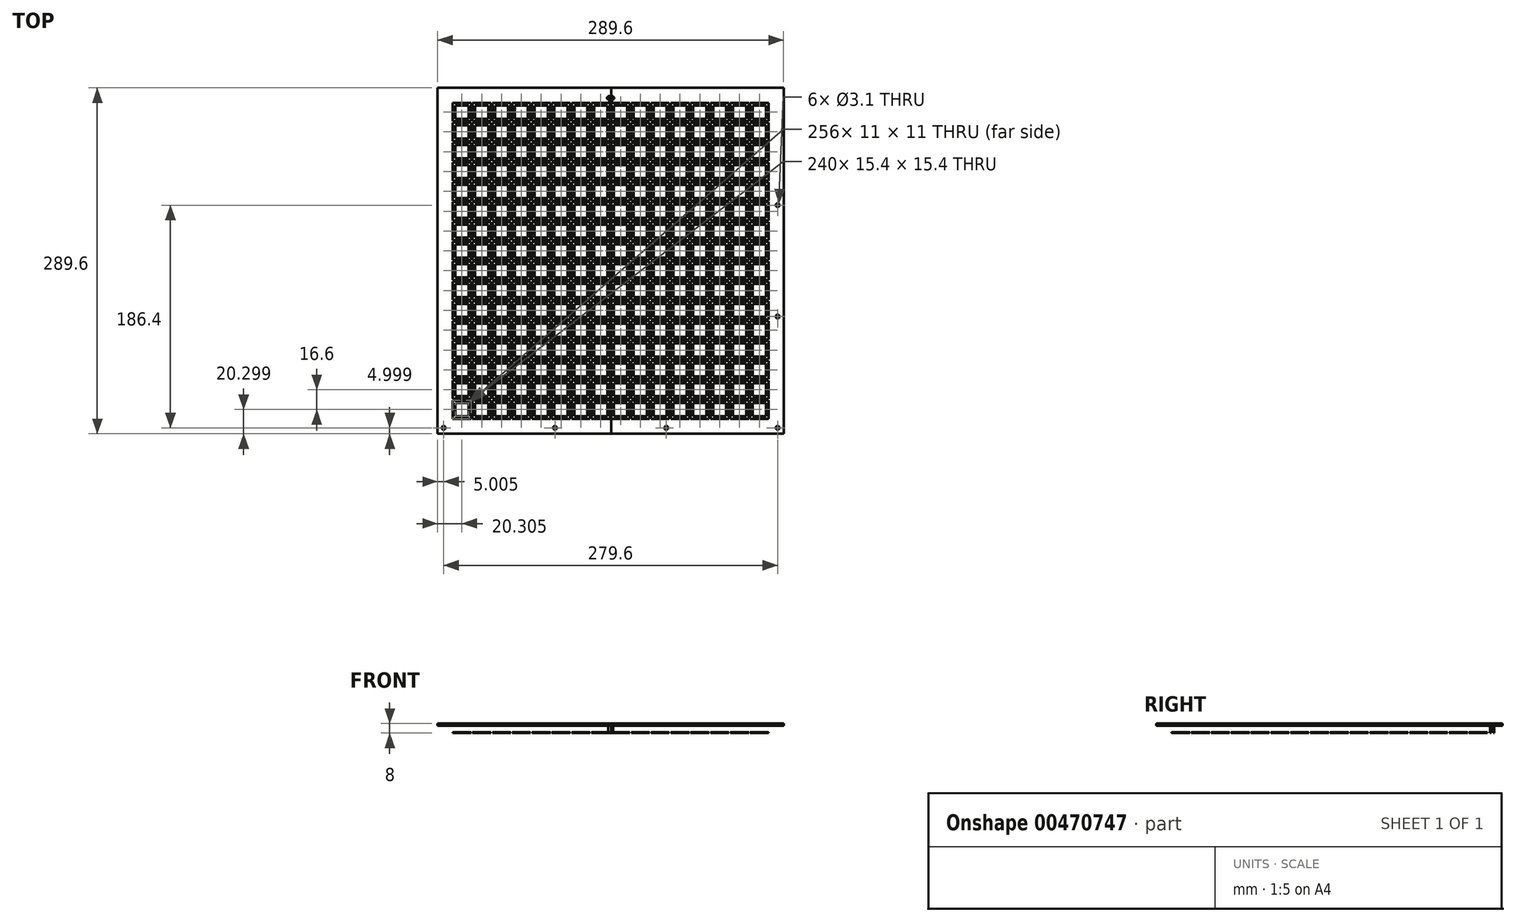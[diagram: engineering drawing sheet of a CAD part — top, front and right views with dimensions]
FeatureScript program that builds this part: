
annotation { "Feature Type Name" : "Feature", "Feature Type Description" : "" }
export const myFeature = defineFeature(function(context is Context, id is Id, definition is map)
    precondition{}
    {
        {
            var Q0;
            Q0=qCreatedBy(makeId("Top.planeOp"),FACE);
            var sketch = newSketch(context, id + "F0", { "sketchPlane" : qUnion([Q0])});
            skLineSegment(sketch, "E0.bottom", {"start": v(-120.53, 25.92) * mm, "end": v(-103.93, 25.92) * mm, "construction": true});
            skLineSegment(sketch, "E0.top", {"start": v(-120.53, 9.32) * mm, "end": v(-103.93, 9.32) * mm, "construction": true});
            skLineSegment(sketch, "E0.left", {"start": v(-120.53, 25.92) * mm, "end": v(-120.53, 9.32) * mm, "construction": true});
            skLineSegment(sketch, "E0.right", {"start": v(-103.93, 25.92) * mm, "end": v(-103.93, 9.32) * mm, "construction": true});
            skLineSegment(sketch, "E1.bottom", {"start": v(-132.53, 286.92) * mm, "end": v(157.07, 286.92) * mm});
            skLineSegment(sketch, "E1.top", {"start": v(-132.53, -2.68) * mm, "end": v(157.07, -2.68) * mm});
            skLineSegment(sketch, "E1.left", {"start": v(-132.53, 286.92) * mm, "end": v(-132.53, -2.68) * mm});
            skLineSegment(sketch, "E1.right", {"start": v(157.07, 286.92) * mm, "end": v(157.07, -2.68) * mm});
            skLineSegment(sketch, "E2.bottom", {"start": v(-127.53, 281.92) * mm, "end": v(152.07, 281.92) * mm, "construction": true});
            skLineSegment(sketch, "E2.top", {"start": v(-127.53, 2.32) * mm, "end": v(152.07, 2.32) * mm, "construction": true});
            skLineSegment(sketch, "E2.left", {"start": v(-127.53, 281.92) * mm, "end": v(-127.53, 2.32) * mm, "construction": true});
            skLineSegment(sketch, "E2.right", {"start": v(152.07, 281.92) * mm, "end": v(152.07, 2.32) * mm, "construction": true});
            skLineSegment(sketch, "E3.bottom", {"start": v(10.27, 280.17) * mm, "end": v(14.27, 280.17) * mm});
            skLineSegment(sketch, "E3.top", {"start": v(10.27, 276.67) * mm, "end": v(14.27, 276.67) * mm});
            skLineSegment(sketch, "E3.left", {"start": v(10.27, 280.17) * mm, "end": v(10.27, 279.42) * mm});
            skLineSegment(sketch, "E3.right", {"start": v(14.27, 280.17) * mm, "end": v(14.27, 279.42) * mm});
            skArc(sketch, "E4", {"start": v(14.27, 277.42) * mm, "mid": v(15.27, 278.42) * mm, "end": v(14.27, 279.42) * mm});
            skArc(sketch, "E5", {"start": v(10.27, 279.42) * mm, "mid": v(9.27, 278.42) * mm, "end": v(10.27, 277.42) * mm});
            skLineSegment(sketch, "E6", {"start": v(10.27, 279.42) * mm, "end": v(14.27, 279.42) * mm});
            skLineSegment(sketch, "E7", {"start": v(14.27, 277.42) * mm, "end": v(10.27, 277.42) * mm});
            skLineSegment(sketch, "E8.trimOffspring", {"start": v(10.27, 277.42) * mm, "end": v(10.27, 276.67) * mm});
            skLineSegment(sketch, "E9.trimOffspring", {"start": v(14.27, 277.42) * mm, "end": v(14.27, 276.67) * mm});
            skLineSegment(sketch, "E10.bottom", {"start": v(-117.73, 12.12) * mm, "end": v(-106.73, 12.12) * mm});
            skLineSegment(sketch, "E10.top", {"start": v(-117.73, 23.12) * mm, "end": v(-106.73, 23.12) * mm});
            skLineSegment(sketch, "E10.left", {"start": v(-117.73, 12.12) * mm, "end": v(-117.73, 23.12) * mm});
            skLineSegment(sketch, "E10.right", {"start": v(-106.73, 12.12) * mm, "end": v(-106.73, 23.12) * mm});
            skLineSegment(sketch, "E11.0.1.0", {"start": v(-117.73, 39.72) * mm, "end": v(-106.73, 39.72) * mm});
            skLineSegment(sketch, "E11.0.1.1", {"start": v(-106.73, 28.72) * mm, "end": v(-106.73, 39.72) * mm});
            skLineSegment(sketch, "E11.0.1.2", {"start": v(-117.73, 28.72) * mm, "end": v(-106.73, 28.72) * mm});
            skLineSegment(sketch, "E11.0.1.3", {"start": v(-117.73, 28.72) * mm, "end": v(-117.73, 39.72) * mm});
            skLineSegment(sketch, "E11.0.2.0", {"start": v(-117.73, 56.32) * mm, "end": v(-106.73, 56.32) * mm});
            skLineSegment(sketch, "E11.0.2.1", {"start": v(-106.73, 45.32) * mm, "end": v(-106.73, 56.32) * mm});
            skLineSegment(sketch, "E11.0.2.2", {"start": v(-117.73, 45.32) * mm, "end": v(-106.73, 45.32) * mm});
            skLineSegment(sketch, "E11.0.2.3", {"start": v(-117.73, 45.32) * mm, "end": v(-117.73, 56.32) * mm});
            skLineSegment(sketch, "E11.0.3.0", {"start": v(-117.73, 72.92) * mm, "end": v(-106.73, 72.92) * mm});
            skLineSegment(sketch, "E11.0.3.1", {"start": v(-106.73, 61.92) * mm, "end": v(-106.73, 72.92) * mm});
            skLineSegment(sketch, "E11.0.3.2", {"start": v(-117.73, 61.92) * mm, "end": v(-106.73, 61.92) * mm});
            skLineSegment(sketch, "E11.0.3.3", {"start": v(-117.73, 61.92) * mm, "end": v(-117.73, 72.92) * mm});
            skLineSegment(sketch, "E11.0.4.0", {"start": v(-117.73, 89.52) * mm, "end": v(-106.73, 89.52) * mm});
            skLineSegment(sketch, "E11.0.4.1", {"start": v(-106.73, 78.52) * mm, "end": v(-106.73, 89.52) * mm});
            skLineSegment(sketch, "E11.0.4.2", {"start": v(-117.73, 78.52) * mm, "end": v(-106.73, 78.52) * mm});
            skLineSegment(sketch, "E11.0.4.3", {"start": v(-117.73, 78.52) * mm, "end": v(-117.73, 89.52) * mm});
            skLineSegment(sketch, "E11.0.5.0", {"start": v(-117.73, 106.12) * mm, "end": v(-106.73, 106.12) * mm});
            skLineSegment(sketch, "E11.0.5.1", {"start": v(-106.73, 95.12) * mm, "end": v(-106.73, 106.12) * mm});
            skLineSegment(sketch, "E11.0.5.2", {"start": v(-117.73, 95.12) * mm, "end": v(-106.73, 95.12) * mm});
            skLineSegment(sketch, "E11.0.5.3", {"start": v(-117.73, 95.12) * mm, "end": v(-117.73, 106.12) * mm});
            skLineSegment(sketch, "E11.0.6.0", {"start": v(-117.73, 122.72) * mm, "end": v(-106.73, 122.72) * mm});
            skLineSegment(sketch, "E11.0.6.1", {"start": v(-106.73, 111.72) * mm, "end": v(-106.73, 122.72) * mm});
            skLineSegment(sketch, "E11.0.6.2", {"start": v(-117.73, 111.72) * mm, "end": v(-106.73, 111.72) * mm});
            skLineSegment(sketch, "E11.0.6.3", {"start": v(-117.73, 111.72) * mm, "end": v(-117.73, 122.72) * mm});
            skLineSegment(sketch, "E11.0.7.0", {"start": v(-117.73, 139.32) * mm, "end": v(-106.73, 139.32) * mm});
            skLineSegment(sketch, "E11.0.7.1", {"start": v(-106.73, 128.32) * mm, "end": v(-106.73, 139.32) * mm});
            skLineSegment(sketch, "E11.0.7.2", {"start": v(-117.73, 128.32) * mm, "end": v(-106.73, 128.32) * mm});
            skLineSegment(sketch, "E11.0.7.3", {"start": v(-117.73, 128.32) * mm, "end": v(-117.73, 139.32) * mm});
            skLineSegment(sketch, "E11.0.8.0", {"start": v(-117.73, 155.92) * mm, "end": v(-106.73, 155.92) * mm});
            skLineSegment(sketch, "E11.0.8.1", {"start": v(-106.73, 144.92) * mm, "end": v(-106.73, 155.92) * mm});
            skLineSegment(sketch, "E11.0.8.2", {"start": v(-117.73, 144.92) * mm, "end": v(-106.73, 144.92) * mm});
            skLineSegment(sketch, "E11.0.8.3", {"start": v(-117.73, 144.92) * mm, "end": v(-117.73, 155.92) * mm});
            skLineSegment(sketch, "E11.0.9.0", {"start": v(-117.73, 172.52) * mm, "end": v(-106.73, 172.52) * mm});
            skLineSegment(sketch, "E11.0.9.1", {"start": v(-106.73, 161.52) * mm, "end": v(-106.73, 172.52) * mm});
            skLineSegment(sketch, "E11.0.9.2", {"start": v(-117.73, 161.52) * mm, "end": v(-106.73, 161.52) * mm});
            skLineSegment(sketch, "E11.0.9.3", {"start": v(-117.73, 161.52) * mm, "end": v(-117.73, 172.52) * mm});
            skLineSegment(sketch, "E11.0.10.0", {"start": v(-117.73, 189.12) * mm, "end": v(-106.73, 189.12) * mm});
            skLineSegment(sketch, "E11.0.10.1", {"start": v(-106.73, 178.12) * mm, "end": v(-106.73, 189.12) * mm});
            skLineSegment(sketch, "E11.0.10.2", {"start": v(-117.73, 178.12) * mm, "end": v(-106.73, 178.12) * mm});
            skLineSegment(sketch, "E11.0.10.3", {"start": v(-117.73, 178.12) * mm, "end": v(-117.73, 189.12) * mm});
            skLineSegment(sketch, "E11.0.11.0", {"start": v(-117.73, 205.72) * mm, "end": v(-106.73, 205.72) * mm});
            skLineSegment(sketch, "E11.0.11.1", {"start": v(-106.73, 194.72) * mm, "end": v(-106.73, 205.72) * mm});
            skLineSegment(sketch, "E11.0.11.2", {"start": v(-117.73, 194.72) * mm, "end": v(-106.73, 194.72) * mm});
            skLineSegment(sketch, "E11.0.11.3", {"start": v(-117.73, 194.72) * mm, "end": v(-117.73, 205.72) * mm});
            skLineSegment(sketch, "E11.0.12.0", {"start": v(-117.73, 222.32) * mm, "end": v(-106.73, 222.32) * mm});
            skLineSegment(sketch, "E11.0.12.1", {"start": v(-106.73, 211.32) * mm, "end": v(-106.73, 222.32) * mm});
            skLineSegment(sketch, "E11.0.12.2", {"start": v(-117.73, 211.32) * mm, "end": v(-106.73, 211.32) * mm});
            skLineSegment(sketch, "E11.0.12.3", {"start": v(-117.73, 211.32) * mm, "end": v(-117.73, 222.32) * mm});
            skLineSegment(sketch, "E11.0.13.0", {"start": v(-117.73, 238.92) * mm, "end": v(-106.73, 238.92) * mm});
            skLineSegment(sketch, "E11.0.13.1", {"start": v(-106.73, 227.92) * mm, "end": v(-106.73, 238.92) * mm});
            skLineSegment(sketch, "E11.0.13.2", {"start": v(-117.73, 227.92) * mm, "end": v(-106.73, 227.92) * mm});
            skLineSegment(sketch, "E11.0.13.3", {"start": v(-117.73, 227.92) * mm, "end": v(-117.73, 238.92) * mm});
            skLineSegment(sketch, "E11.0.14.0", {"start": v(-117.73, 255.52) * mm, "end": v(-106.73, 255.52) * mm});
            skLineSegment(sketch, "E11.0.14.1", {"start": v(-106.73, 244.52) * mm, "end": v(-106.73, 255.52) * mm});
            skLineSegment(sketch, "E11.0.14.2", {"start": v(-117.73, 244.52) * mm, "end": v(-106.73, 244.52) * mm});
            skLineSegment(sketch, "E11.0.14.3", {"start": v(-117.73, 244.52) * mm, "end": v(-117.73, 255.52) * mm});
            skLineSegment(sketch, "E11.0.15.0", {"start": v(-117.73, 272.12) * mm, "end": v(-106.73, 272.12) * mm});
            skLineSegment(sketch, "E11.0.15.1", {"start": v(-106.73, 261.12) * mm, "end": v(-106.73, 272.12) * mm});
            skLineSegment(sketch, "E11.0.15.2", {"start": v(-117.73, 261.12) * mm, "end": v(-106.73, 261.12) * mm});
            skLineSegment(sketch, "E11.0.15.3", {"start": v(-117.73, 261.12) * mm, "end": v(-117.73, 272.12) * mm});
            skLineSegment(sketch, "E11.1.0.0", {"start": v(-101.13, 23.12) * mm, "end": v(-90.13, 23.12) * mm});
            skLineSegment(sketch, "E11.1.0.1", {"start": v(-90.13, 12.12) * mm, "end": v(-90.13, 23.12) * mm});
            skLineSegment(sketch, "E11.1.0.2", {"start": v(-101.13, 12.12) * mm, "end": v(-90.13, 12.12) * mm});
            skLineSegment(sketch, "E11.1.0.3", {"start": v(-101.13, 12.12) * mm, "end": v(-101.13, 23.12) * mm});
            skLineSegment(sketch, "E11.1.1.0", {"start": v(-101.13, 39.72) * mm, "end": v(-90.13, 39.72) * mm});
            skLineSegment(sketch, "E11.1.1.1", {"start": v(-90.13, 28.72) * mm, "end": v(-90.13, 39.72) * mm});
            skLineSegment(sketch, "E11.1.1.2", {"start": v(-101.13, 28.72) * mm, "end": v(-90.13, 28.72) * mm});
            skLineSegment(sketch, "E11.1.1.3", {"start": v(-101.13, 28.72) * mm, "end": v(-101.13, 39.72) * mm});
            skLineSegment(sketch, "E11.1.2.0", {"start": v(-101.13, 56.32) * mm, "end": v(-90.13, 56.32) * mm});
            skLineSegment(sketch, "E11.1.2.1", {"start": v(-90.13, 45.32) * mm, "end": v(-90.13, 56.32) * mm});
            skLineSegment(sketch, "E11.1.2.2", {"start": v(-101.13, 45.32) * mm, "end": v(-90.13, 45.32) * mm});
            skLineSegment(sketch, "E11.1.2.3", {"start": v(-101.13, 45.32) * mm, "end": v(-101.13, 56.32) * mm});
            skLineSegment(sketch, "E11.1.3.0", {"start": v(-101.13, 72.92) * mm, "end": v(-90.13, 72.92) * mm});
            skLineSegment(sketch, "E11.1.3.1", {"start": v(-90.13, 61.92) * mm, "end": v(-90.13, 72.92) * mm});
            skLineSegment(sketch, "E11.1.3.2", {"start": v(-101.13, 61.92) * mm, "end": v(-90.13, 61.92) * mm});
            skLineSegment(sketch, "E11.1.3.3", {"start": v(-101.13, 61.92) * mm, "end": v(-101.13, 72.92) * mm});
            skLineSegment(sketch, "E11.1.4.0", {"start": v(-101.13, 89.52) * mm, "end": v(-90.13, 89.52) * mm});
            skLineSegment(sketch, "E11.1.4.1", {"start": v(-90.13, 78.52) * mm, "end": v(-90.13, 89.52) * mm});
            skLineSegment(sketch, "E11.1.4.2", {"start": v(-101.13, 78.52) * mm, "end": v(-90.13, 78.52) * mm});
            skLineSegment(sketch, "E11.1.4.3", {"start": v(-101.13, 78.52) * mm, "end": v(-101.13, 89.52) * mm});
            skLineSegment(sketch, "E11.1.5.0", {"start": v(-101.13, 106.12) * mm, "end": v(-90.13, 106.12) * mm});
            skLineSegment(sketch, "E11.1.5.1", {"start": v(-90.13, 95.12) * mm, "end": v(-90.13, 106.12) * mm});
            skLineSegment(sketch, "E11.1.5.2", {"start": v(-101.13, 95.12) * mm, "end": v(-90.13, 95.12) * mm});
            skLineSegment(sketch, "E11.1.5.3", {"start": v(-101.13, 95.12) * mm, "end": v(-101.13, 106.12) * mm});
            skLineSegment(sketch, "E11.1.6.0", {"start": v(-101.13, 122.72) * mm, "end": v(-90.13, 122.72) * mm});
            skLineSegment(sketch, "E11.1.6.1", {"start": v(-90.13, 111.72) * mm, "end": v(-90.13, 122.72) * mm});
            skLineSegment(sketch, "E11.1.6.2", {"start": v(-101.13, 111.72) * mm, "end": v(-90.13, 111.72) * mm});
            skLineSegment(sketch, "E11.1.6.3", {"start": v(-101.13, 111.72) * mm, "end": v(-101.13, 122.72) * mm});
            skLineSegment(sketch, "E11.1.7.0", {"start": v(-101.13, 139.32) * mm, "end": v(-90.13, 139.32) * mm});
            skLineSegment(sketch, "E11.1.7.1", {"start": v(-90.13, 128.32) * mm, "end": v(-90.13, 139.32) * mm});
            skLineSegment(sketch, "E11.1.7.2", {"start": v(-101.13, 128.32) * mm, "end": v(-90.13, 128.32) * mm});
            skLineSegment(sketch, "E11.1.7.3", {"start": v(-101.13, 128.32) * mm, "end": v(-101.13, 139.32) * mm});
            skLineSegment(sketch, "E11.1.8.0", {"start": v(-101.13, 155.92) * mm, "end": v(-90.13, 155.92) * mm});
            skLineSegment(sketch, "E11.1.8.1", {"start": v(-90.13, 144.92) * mm, "end": v(-90.13, 155.92) * mm});
            skLineSegment(sketch, "E11.1.8.2", {"start": v(-101.13, 144.92) * mm, "end": v(-90.13, 144.92) * mm});
            skLineSegment(sketch, "E11.1.8.3", {"start": v(-101.13, 144.92) * mm, "end": v(-101.13, 155.92) * mm});
            skLineSegment(sketch, "E11.1.9.0", {"start": v(-101.13, 172.52) * mm, "end": v(-90.13, 172.52) * mm});
            skLineSegment(sketch, "E11.1.9.1", {"start": v(-90.13, 161.52) * mm, "end": v(-90.13, 172.52) * mm});
            skLineSegment(sketch, "E11.1.9.2", {"start": v(-101.13, 161.52) * mm, "end": v(-90.13, 161.52) * mm});
            skLineSegment(sketch, "E11.1.9.3", {"start": v(-101.13, 161.52) * mm, "end": v(-101.13, 172.52) * mm});
            skLineSegment(sketch, "E11.1.10.0", {"start": v(-101.13, 189.12) * mm, "end": v(-90.13, 189.12) * mm});
            skLineSegment(sketch, "E11.1.10.1", {"start": v(-90.13, 178.12) * mm, "end": v(-90.13, 189.12) * mm});
            skLineSegment(sketch, "E11.1.10.2", {"start": v(-101.13, 178.12) * mm, "end": v(-90.13, 178.12) * mm});
            skLineSegment(sketch, "E11.1.10.3", {"start": v(-101.13, 178.12) * mm, "end": v(-101.13, 189.12) * mm});
            skLineSegment(sketch, "E11.1.11.0", {"start": v(-101.13, 205.72) * mm, "end": v(-90.13, 205.72) * mm});
            skLineSegment(sketch, "E11.1.11.1", {"start": v(-90.13, 194.72) * mm, "end": v(-90.13, 205.72) * mm});
            skLineSegment(sketch, "E11.1.11.2", {"start": v(-101.13, 194.72) * mm, "end": v(-90.13, 194.72) * mm});
            skLineSegment(sketch, "E11.1.11.3", {"start": v(-101.13, 194.72) * mm, "end": v(-101.13, 205.72) * mm});
            skLineSegment(sketch, "E11.1.12.0", {"start": v(-101.13, 222.32) * mm, "end": v(-90.13, 222.32) * mm});
            skLineSegment(sketch, "E11.1.12.1", {"start": v(-90.13, 211.32) * mm, "end": v(-90.13, 222.32) * mm});
            skLineSegment(sketch, "E11.1.12.2", {"start": v(-101.13, 211.32) * mm, "end": v(-90.13, 211.32) * mm});
            skLineSegment(sketch, "E11.1.12.3", {"start": v(-101.13, 211.32) * mm, "end": v(-101.13, 222.32) * mm});
            skLineSegment(sketch, "E11.1.13.0", {"start": v(-101.13, 238.92) * mm, "end": v(-90.13, 238.92) * mm});
            skLineSegment(sketch, "E11.1.13.1", {"start": v(-90.13, 227.92) * mm, "end": v(-90.13, 238.92) * mm});
            skLineSegment(sketch, "E11.1.13.2", {"start": v(-101.13, 227.92) * mm, "end": v(-90.13, 227.92) * mm});
            skLineSegment(sketch, "E11.1.13.3", {"start": v(-101.13, 227.92) * mm, "end": v(-101.13, 238.92) * mm});
            skLineSegment(sketch, "E11.1.14.0", {"start": v(-101.13, 255.52) * mm, "end": v(-90.13, 255.52) * mm});
            skLineSegment(sketch, "E11.1.14.1", {"start": v(-90.13, 244.52) * mm, "end": v(-90.13, 255.52) * mm});
            skLineSegment(sketch, "E11.1.14.2", {"start": v(-101.13, 244.52) * mm, "end": v(-90.13, 244.52) * mm});
            skLineSegment(sketch, "E11.1.14.3", {"start": v(-101.13, 244.52) * mm, "end": v(-101.13, 255.52) * mm});
            skLineSegment(sketch, "E11.1.15.0", {"start": v(-101.13, 272.12) * mm, "end": v(-90.13, 272.12) * mm});
            skLineSegment(sketch, "E11.1.15.1", {"start": v(-90.13, 261.12) * mm, "end": v(-90.13, 272.12) * mm});
            skLineSegment(sketch, "E11.1.15.2", {"start": v(-101.13, 261.12) * mm, "end": v(-90.13, 261.12) * mm});
            skLineSegment(sketch, "E11.1.15.3", {"start": v(-101.13, 261.12) * mm, "end": v(-101.13, 272.12) * mm});
            skLineSegment(sketch, "E11.2.0.0", {"start": v(-84.53, 23.12) * mm, "end": v(-73.53, 23.12) * mm});
            skLineSegment(sketch, "E11.2.0.1", {"start": v(-73.53, 12.12) * mm, "end": v(-73.53, 23.12) * mm});
            skLineSegment(sketch, "E11.2.0.2", {"start": v(-84.53, 12.12) * mm, "end": v(-73.53, 12.12) * mm});
            skLineSegment(sketch, "E11.2.0.3", {"start": v(-84.53, 12.12) * mm, "end": v(-84.53, 23.12) * mm});
            skLineSegment(sketch, "E11.2.1.0", {"start": v(-84.53, 39.72) * mm, "end": v(-73.53, 39.72) * mm});
            skLineSegment(sketch, "E11.2.1.1", {"start": v(-73.53, 28.72) * mm, "end": v(-73.53, 39.72) * mm});
            skLineSegment(sketch, "E11.2.1.2", {"start": v(-84.53, 28.72) * mm, "end": v(-73.53, 28.72) * mm});
            skLineSegment(sketch, "E11.2.1.3", {"start": v(-84.53, 28.72) * mm, "end": v(-84.53, 39.72) * mm});
            skLineSegment(sketch, "E11.2.2.0", {"start": v(-84.53, 56.32) * mm, "end": v(-73.53, 56.32) * mm});
            skLineSegment(sketch, "E11.2.2.1", {"start": v(-73.53, 45.32) * mm, "end": v(-73.53, 56.32) * mm});
            skLineSegment(sketch, "E11.2.2.2", {"start": v(-84.53, 45.32) * mm, "end": v(-73.53, 45.32) * mm});
            skLineSegment(sketch, "E11.2.2.3", {"start": v(-84.53, 45.32) * mm, "end": v(-84.53, 56.32) * mm});
            skLineSegment(sketch, "E11.2.3.0", {"start": v(-84.53, 72.92) * mm, "end": v(-73.53, 72.92) * mm});
            skLineSegment(sketch, "E11.2.3.1", {"start": v(-73.53, 61.92) * mm, "end": v(-73.53, 72.92) * mm});
            skLineSegment(sketch, "E11.2.3.2", {"start": v(-84.53, 61.92) * mm, "end": v(-73.53, 61.92) * mm});
            skLineSegment(sketch, "E11.2.3.3", {"start": v(-84.53, 61.92) * mm, "end": v(-84.53, 72.92) * mm});
            skLineSegment(sketch, "E11.2.4.0", {"start": v(-84.53, 89.52) * mm, "end": v(-73.53, 89.52) * mm});
            skLineSegment(sketch, "E11.2.4.1", {"start": v(-73.53, 78.52) * mm, "end": v(-73.53, 89.52) * mm});
            skLineSegment(sketch, "E11.2.4.2", {"start": v(-84.53, 78.52) * mm, "end": v(-73.53, 78.52) * mm});
            skLineSegment(sketch, "E11.2.4.3", {"start": v(-84.53, 78.52) * mm, "end": v(-84.53, 89.52) * mm});
            skLineSegment(sketch, "E11.2.5.0", {"start": v(-84.53, 106.12) * mm, "end": v(-73.53, 106.12) * mm});
            skLineSegment(sketch, "E11.2.5.1", {"start": v(-73.53, 95.12) * mm, "end": v(-73.53, 106.12) * mm});
            skLineSegment(sketch, "E11.2.5.2", {"start": v(-84.53, 95.12) * mm, "end": v(-73.53, 95.12) * mm});
            skLineSegment(sketch, "E11.2.5.3", {"start": v(-84.53, 95.12) * mm, "end": v(-84.53, 106.12) * mm});
            skLineSegment(sketch, "E11.2.6.0", {"start": v(-84.53, 122.72) * mm, "end": v(-73.53, 122.72) * mm});
            skLineSegment(sketch, "E11.2.6.1", {"start": v(-73.53, 111.72) * mm, "end": v(-73.53, 122.72) * mm});
            skLineSegment(sketch, "E11.2.6.2", {"start": v(-84.53, 111.72) * mm, "end": v(-73.53, 111.72) * mm});
            skLineSegment(sketch, "E11.2.6.3", {"start": v(-84.53, 111.72) * mm, "end": v(-84.53, 122.72) * mm});
            skLineSegment(sketch, "E11.2.7.0", {"start": v(-84.53, 139.32) * mm, "end": v(-73.53, 139.32) * mm});
            skLineSegment(sketch, "E11.2.7.1", {"start": v(-73.53, 128.32) * mm, "end": v(-73.53, 139.32) * mm});
            skLineSegment(sketch, "E11.2.7.2", {"start": v(-84.53, 128.32) * mm, "end": v(-73.53, 128.32) * mm});
            skLineSegment(sketch, "E11.2.7.3", {"start": v(-84.53, 128.32) * mm, "end": v(-84.53, 139.32) * mm});
            skLineSegment(sketch, "E11.2.8.0", {"start": v(-84.53, 155.92) * mm, "end": v(-73.53, 155.92) * mm});
            skLineSegment(sketch, "E11.2.8.1", {"start": v(-73.53, 144.92) * mm, "end": v(-73.53, 155.92) * mm});
            skLineSegment(sketch, "E11.2.8.2", {"start": v(-84.53, 144.92) * mm, "end": v(-73.53, 144.92) * mm});
            skLineSegment(sketch, "E11.2.8.3", {"start": v(-84.53, 144.92) * mm, "end": v(-84.53, 155.92) * mm});
            skLineSegment(sketch, "E11.2.9.0", {"start": v(-84.53, 172.52) * mm, "end": v(-73.53, 172.52) * mm});
            skLineSegment(sketch, "E11.2.9.1", {"start": v(-73.53, 161.52) * mm, "end": v(-73.53, 172.52) * mm});
            skLineSegment(sketch, "E11.2.9.2", {"start": v(-84.53, 161.52) * mm, "end": v(-73.53, 161.52) * mm});
            skLineSegment(sketch, "E11.2.9.3", {"start": v(-84.53, 161.52) * mm, "end": v(-84.53, 172.52) * mm});
            skLineSegment(sketch, "E11.2.10.0", {"start": v(-84.53, 189.12) * mm, "end": v(-73.53, 189.12) * mm});
            skLineSegment(sketch, "E11.2.10.1", {"start": v(-73.53, 178.12) * mm, "end": v(-73.53, 189.12) * mm});
            skLineSegment(sketch, "E11.2.10.2", {"start": v(-84.53, 178.12) * mm, "end": v(-73.53, 178.12) * mm});
            skLineSegment(sketch, "E11.2.10.3", {"start": v(-84.53, 178.12) * mm, "end": v(-84.53, 189.12) * mm});
            skLineSegment(sketch, "E11.2.11.0", {"start": v(-84.53, 205.72) * mm, "end": v(-73.53, 205.72) * mm});
            skLineSegment(sketch, "E11.2.11.1", {"start": v(-73.53, 194.72) * mm, "end": v(-73.53, 205.72) * mm});
            skLineSegment(sketch, "E11.2.11.2", {"start": v(-84.53, 194.72) * mm, "end": v(-73.53, 194.72) * mm});
            skLineSegment(sketch, "E11.2.11.3", {"start": v(-84.53, 194.72) * mm, "end": v(-84.53, 205.72) * mm});
            skLineSegment(sketch, "E11.2.12.0", {"start": v(-84.53, 222.32) * mm, "end": v(-73.53, 222.32) * mm});
            skLineSegment(sketch, "E11.2.12.1", {"start": v(-73.53, 211.32) * mm, "end": v(-73.53, 222.32) * mm});
            skLineSegment(sketch, "E11.2.12.2", {"start": v(-84.53, 211.32) * mm, "end": v(-73.53, 211.32) * mm});
            skLineSegment(sketch, "E11.2.12.3", {"start": v(-84.53, 211.32) * mm, "end": v(-84.53, 222.32) * mm});
            skLineSegment(sketch, "E11.2.13.0", {"start": v(-84.53, 238.92) * mm, "end": v(-73.53, 238.92) * mm});
            skLineSegment(sketch, "E11.2.13.1", {"start": v(-73.53, 227.92) * mm, "end": v(-73.53, 238.92) * mm});
            skLineSegment(sketch, "E11.2.13.2", {"start": v(-84.53, 227.92) * mm, "end": v(-73.53, 227.92) * mm});
            skLineSegment(sketch, "E11.2.13.3", {"start": v(-84.53, 227.92) * mm, "end": v(-84.53, 238.92) * mm});
            skLineSegment(sketch, "E11.2.14.0", {"start": v(-84.53, 255.52) * mm, "end": v(-73.53, 255.52) * mm});
            skLineSegment(sketch, "E11.2.14.1", {"start": v(-73.53, 244.52) * mm, "end": v(-73.53, 255.52) * mm});
            skLineSegment(sketch, "E11.2.14.2", {"start": v(-84.53, 244.52) * mm, "end": v(-73.53, 244.52) * mm});
            skLineSegment(sketch, "E11.2.14.3", {"start": v(-84.53, 244.52) * mm, "end": v(-84.53, 255.52) * mm});
            skLineSegment(sketch, "E11.2.15.0", {"start": v(-84.53, 272.12) * mm, "end": v(-73.53, 272.12) * mm});
            skLineSegment(sketch, "E11.2.15.1", {"start": v(-73.53, 261.12) * mm, "end": v(-73.53, 272.12) * mm});
            skLineSegment(sketch, "E11.2.15.2", {"start": v(-84.53, 261.12) * mm, "end": v(-73.53, 261.12) * mm});
            skLineSegment(sketch, "E11.2.15.3", {"start": v(-84.53, 261.12) * mm, "end": v(-84.53, 272.12) * mm});
            skLineSegment(sketch, "E11.3.0.0", {"start": v(-67.93, 23.12) * mm, "end": v(-56.93, 23.12) * mm});
            skLineSegment(sketch, "E11.3.0.1", {"start": v(-56.93, 12.12) * mm, "end": v(-56.93, 23.12) * mm});
            skLineSegment(sketch, "E11.3.0.2", {"start": v(-67.93, 12.12) * mm, "end": v(-56.93, 12.12) * mm});
            skLineSegment(sketch, "E11.3.0.3", {"start": v(-67.93, 12.12) * mm, "end": v(-67.93, 23.12) * mm});
            skLineSegment(sketch, "E11.3.1.0", {"start": v(-67.93, 39.72) * mm, "end": v(-56.93, 39.72) * mm});
            skLineSegment(sketch, "E11.3.1.1", {"start": v(-56.93, 28.72) * mm, "end": v(-56.93, 39.72) * mm});
            skLineSegment(sketch, "E11.3.1.2", {"start": v(-67.93, 28.72) * mm, "end": v(-56.93, 28.72) * mm});
            skLineSegment(sketch, "E11.3.1.3", {"start": v(-67.93, 28.72) * mm, "end": v(-67.93, 39.72) * mm});
            skLineSegment(sketch, "E11.3.2.0", {"start": v(-67.93, 56.32) * mm, "end": v(-56.93, 56.32) * mm});
            skLineSegment(sketch, "E11.3.2.1", {"start": v(-56.93, 45.32) * mm, "end": v(-56.93, 56.32) * mm});
            skLineSegment(sketch, "E11.3.2.2", {"start": v(-67.93, 45.32) * mm, "end": v(-56.93, 45.32) * mm});
            skLineSegment(sketch, "E11.3.2.3", {"start": v(-67.93, 45.32) * mm, "end": v(-67.93, 56.32) * mm});
            skLineSegment(sketch, "E11.3.3.0", {"start": v(-67.93, 72.92) * mm, "end": v(-56.93, 72.92) * mm});
            skLineSegment(sketch, "E11.3.3.1", {"start": v(-56.93, 61.92) * mm, "end": v(-56.93, 72.92) * mm});
            skLineSegment(sketch, "E11.3.3.2", {"start": v(-67.93, 61.92) * mm, "end": v(-56.93, 61.92) * mm});
            skLineSegment(sketch, "E11.3.3.3", {"start": v(-67.93, 61.92) * mm, "end": v(-67.93, 72.92) * mm});
            skLineSegment(sketch, "E11.3.4.0", {"start": v(-67.93, 89.52) * mm, "end": v(-56.93, 89.52) * mm});
            skLineSegment(sketch, "E11.3.4.1", {"start": v(-56.93, 78.52) * mm, "end": v(-56.93, 89.52) * mm});
            skLineSegment(sketch, "E11.3.4.2", {"start": v(-67.93, 78.52) * mm, "end": v(-56.93, 78.52) * mm});
            skLineSegment(sketch, "E11.3.4.3", {"start": v(-67.93, 78.52) * mm, "end": v(-67.93, 89.52) * mm});
            skLineSegment(sketch, "E11.3.5.0", {"start": v(-67.93, 106.12) * mm, "end": v(-56.93, 106.12) * mm});
            skLineSegment(sketch, "E11.3.5.1", {"start": v(-56.93, 95.12) * mm, "end": v(-56.93, 106.12) * mm});
            skLineSegment(sketch, "E11.3.5.2", {"start": v(-67.93, 95.12) * mm, "end": v(-56.93, 95.12) * mm});
            skLineSegment(sketch, "E11.3.5.3", {"start": v(-67.93, 95.12) * mm, "end": v(-67.93, 106.12) * mm});
            skLineSegment(sketch, "E11.3.6.0", {"start": v(-67.93, 122.72) * mm, "end": v(-56.93, 122.72) * mm});
            skLineSegment(sketch, "E11.3.6.1", {"start": v(-56.93, 111.72) * mm, "end": v(-56.93, 122.72) * mm});
            skLineSegment(sketch, "E11.3.6.2", {"start": v(-67.93, 111.72) * mm, "end": v(-56.93, 111.72) * mm});
            skLineSegment(sketch, "E11.3.6.3", {"start": v(-67.93, 111.72) * mm, "end": v(-67.93, 122.72) * mm});
            skLineSegment(sketch, "E11.3.7.0", {"start": v(-67.93, 139.32) * mm, "end": v(-56.93, 139.32) * mm});
            skLineSegment(sketch, "E11.3.7.1", {"start": v(-56.93, 128.32) * mm, "end": v(-56.93, 139.32) * mm});
            skLineSegment(sketch, "E11.3.7.2", {"start": v(-67.93, 128.32) * mm, "end": v(-56.93, 128.32) * mm});
            skLineSegment(sketch, "E11.3.7.3", {"start": v(-67.93, 128.32) * mm, "end": v(-67.93, 139.32) * mm});
            skLineSegment(sketch, "E11.3.8.0", {"start": v(-67.93, 155.92) * mm, "end": v(-56.93, 155.92) * mm});
            skLineSegment(sketch, "E11.3.8.1", {"start": v(-56.93, 144.92) * mm, "end": v(-56.93, 155.92) * mm});
            skLineSegment(sketch, "E11.3.8.2", {"start": v(-67.93, 144.92) * mm, "end": v(-56.93, 144.92) * mm});
            skLineSegment(sketch, "E11.3.8.3", {"start": v(-67.93, 144.92) * mm, "end": v(-67.93, 155.92) * mm});
            skLineSegment(sketch, "E11.3.9.0", {"start": v(-67.93, 172.52) * mm, "end": v(-56.93, 172.52) * mm});
            skLineSegment(sketch, "E11.3.9.1", {"start": v(-56.93, 161.52) * mm, "end": v(-56.93, 172.52) * mm});
            skLineSegment(sketch, "E11.3.9.2", {"start": v(-67.93, 161.52) * mm, "end": v(-56.93, 161.52) * mm});
            skLineSegment(sketch, "E11.3.9.3", {"start": v(-67.93, 161.52) * mm, "end": v(-67.93, 172.52) * mm});
            skLineSegment(sketch, "E11.3.10.0", {"start": v(-67.93, 189.12) * mm, "end": v(-56.93, 189.12) * mm});
            skLineSegment(sketch, "E11.3.10.1", {"start": v(-56.93, 178.12) * mm, "end": v(-56.93, 189.12) * mm});
            skLineSegment(sketch, "E11.3.10.2", {"start": v(-67.93, 178.12) * mm, "end": v(-56.93, 178.12) * mm});
            skLineSegment(sketch, "E11.3.10.3", {"start": v(-67.93, 178.12) * mm, "end": v(-67.93, 189.12) * mm});
            skLineSegment(sketch, "E11.3.11.0", {"start": v(-67.93, 205.72) * mm, "end": v(-56.93, 205.72) * mm});
            skLineSegment(sketch, "E11.3.11.1", {"start": v(-56.93, 194.72) * mm, "end": v(-56.93, 205.72) * mm});
            skLineSegment(sketch, "E11.3.11.2", {"start": v(-67.93, 194.72) * mm, "end": v(-56.93, 194.72) * mm});
            skLineSegment(sketch, "E11.3.11.3", {"start": v(-67.93, 194.72) * mm, "end": v(-67.93, 205.72) * mm});
            skLineSegment(sketch, "E11.3.12.0", {"start": v(-67.93, 222.32) * mm, "end": v(-56.93, 222.32) * mm});
            skLineSegment(sketch, "E11.3.12.1", {"start": v(-56.93, 211.32) * mm, "end": v(-56.93, 222.32) * mm});
            skLineSegment(sketch, "E11.3.12.2", {"start": v(-67.93, 211.32) * mm, "end": v(-56.93, 211.32) * mm});
            skLineSegment(sketch, "E11.3.12.3", {"start": v(-67.93, 211.32) * mm, "end": v(-67.93, 222.32) * mm});
            skLineSegment(sketch, "E11.3.13.0", {"start": v(-67.93, 238.92) * mm, "end": v(-56.93, 238.92) * mm});
            skLineSegment(sketch, "E11.3.13.1", {"start": v(-56.93, 227.92) * mm, "end": v(-56.93, 238.92) * mm});
            skLineSegment(sketch, "E11.3.13.2", {"start": v(-67.93, 227.92) * mm, "end": v(-56.93, 227.92) * mm});
            skLineSegment(sketch, "E11.3.13.3", {"start": v(-67.93, 227.92) * mm, "end": v(-67.93, 238.92) * mm});
            skLineSegment(sketch, "E11.3.14.0", {"start": v(-67.93, 255.52) * mm, "end": v(-56.93, 255.52) * mm});
            skLineSegment(sketch, "E11.3.14.1", {"start": v(-56.93, 244.52) * mm, "end": v(-56.93, 255.52) * mm});
            skLineSegment(sketch, "E11.3.14.2", {"start": v(-67.93, 244.52) * mm, "end": v(-56.93, 244.52) * mm});
            skLineSegment(sketch, "E11.3.14.3", {"start": v(-67.93, 244.52) * mm, "end": v(-67.93, 255.52) * mm});
            skLineSegment(sketch, "E11.3.15.0", {"start": v(-67.93, 272.12) * mm, "end": v(-56.93, 272.12) * mm});
            skLineSegment(sketch, "E11.3.15.1", {"start": v(-56.93, 261.12) * mm, "end": v(-56.93, 272.12) * mm});
            skLineSegment(sketch, "E11.3.15.2", {"start": v(-67.93, 261.12) * mm, "end": v(-56.93, 261.12) * mm});
            skLineSegment(sketch, "E11.3.15.3", {"start": v(-67.93, 261.12) * mm, "end": v(-67.93, 272.12) * mm});
            skLineSegment(sketch, "E11.4.0.0", {"start": v(-51.33, 23.12) * mm, "end": v(-40.33, 23.12) * mm});
            skLineSegment(sketch, "E11.4.0.1", {"start": v(-40.33, 12.12) * mm, "end": v(-40.33, 23.12) * mm});
            skLineSegment(sketch, "E11.4.0.2", {"start": v(-51.33, 12.12) * mm, "end": v(-40.33, 12.12) * mm});
            skLineSegment(sketch, "E11.4.0.3", {"start": v(-51.33, 12.12) * mm, "end": v(-51.33, 23.12) * mm});
            skLineSegment(sketch, "E11.4.1.0", {"start": v(-51.33, 39.72) * mm, "end": v(-40.33, 39.72) * mm});
            skLineSegment(sketch, "E11.4.1.1", {"start": v(-40.33, 28.72) * mm, "end": v(-40.33, 39.72) * mm});
            skLineSegment(sketch, "E11.4.1.2", {"start": v(-51.33, 28.72) * mm, "end": v(-40.33, 28.72) * mm});
            skLineSegment(sketch, "E11.4.1.3", {"start": v(-51.33, 28.72) * mm, "end": v(-51.33, 39.72) * mm});
            skLineSegment(sketch, "E11.4.2.0", {"start": v(-51.33, 56.32) * mm, "end": v(-40.33, 56.32) * mm});
            skLineSegment(sketch, "E11.4.2.1", {"start": v(-40.33, 45.32) * mm, "end": v(-40.33, 56.32) * mm});
            skLineSegment(sketch, "E11.4.2.2", {"start": v(-51.33, 45.32) * mm, "end": v(-40.33, 45.32) * mm});
            skLineSegment(sketch, "E11.4.2.3", {"start": v(-51.33, 45.32) * mm, "end": v(-51.33, 56.32) * mm});
            skLineSegment(sketch, "E11.4.3.0", {"start": v(-51.33, 72.92) * mm, "end": v(-40.33, 72.92) * mm});
            skLineSegment(sketch, "E11.4.3.1", {"start": v(-40.33, 61.92) * mm, "end": v(-40.33, 72.92) * mm});
            skLineSegment(sketch, "E11.4.3.2", {"start": v(-51.33, 61.92) * mm, "end": v(-40.33, 61.92) * mm});
            skLineSegment(sketch, "E11.4.3.3", {"start": v(-51.33, 61.92) * mm, "end": v(-51.33, 72.92) * mm});
            skLineSegment(sketch, "E11.4.4.0", {"start": v(-51.33, 89.52) * mm, "end": v(-40.33, 89.52) * mm});
            skLineSegment(sketch, "E11.4.4.1", {"start": v(-40.33, 78.52) * mm, "end": v(-40.33, 89.52) * mm});
            skLineSegment(sketch, "E11.4.4.2", {"start": v(-51.33, 78.52) * mm, "end": v(-40.33, 78.52) * mm});
            skLineSegment(sketch, "E11.4.4.3", {"start": v(-51.33, 78.52) * mm, "end": v(-51.33, 89.52) * mm});
            skLineSegment(sketch, "E11.4.5.0", {"start": v(-51.33, 106.12) * mm, "end": v(-40.33, 106.12) * mm});
            skLineSegment(sketch, "E11.4.5.1", {"start": v(-40.33, 95.12) * mm, "end": v(-40.33, 106.12) * mm});
            skLineSegment(sketch, "E11.4.5.2", {"start": v(-51.33, 95.12) * mm, "end": v(-40.33, 95.12) * mm});
            skLineSegment(sketch, "E11.4.5.3", {"start": v(-51.33, 95.12) * mm, "end": v(-51.33, 106.12) * mm});
            skLineSegment(sketch, "E11.4.6.0", {"start": v(-51.33, 122.72) * mm, "end": v(-40.33, 122.72) * mm});
            skLineSegment(sketch, "E11.4.6.1", {"start": v(-40.33, 111.72) * mm, "end": v(-40.33, 122.72) * mm});
            skLineSegment(sketch, "E11.4.6.2", {"start": v(-51.33, 111.72) * mm, "end": v(-40.33, 111.72) * mm});
            skLineSegment(sketch, "E11.4.6.3", {"start": v(-51.33, 111.72) * mm, "end": v(-51.33, 122.72) * mm});
            skLineSegment(sketch, "E11.4.7.0", {"start": v(-51.33, 139.32) * mm, "end": v(-40.33, 139.32) * mm});
            skLineSegment(sketch, "E11.4.7.1", {"start": v(-40.33, 128.32) * mm, "end": v(-40.33, 139.32) * mm});
            skLineSegment(sketch, "E11.4.7.2", {"start": v(-51.33, 128.32) * mm, "end": v(-40.33, 128.32) * mm});
            skLineSegment(sketch, "E11.4.7.3", {"start": v(-51.33, 128.32) * mm, "end": v(-51.33, 139.32) * mm});
            skLineSegment(sketch, "E11.4.8.0", {"start": v(-51.33, 155.92) * mm, "end": v(-40.33, 155.92) * mm});
            skLineSegment(sketch, "E11.4.8.1", {"start": v(-40.33, 144.92) * mm, "end": v(-40.33, 155.92) * mm});
            skLineSegment(sketch, "E11.4.8.2", {"start": v(-51.33, 144.92) * mm, "end": v(-40.33, 144.92) * mm});
            skLineSegment(sketch, "E11.4.8.3", {"start": v(-51.33, 144.92) * mm, "end": v(-51.33, 155.92) * mm});
            skLineSegment(sketch, "E11.4.9.0", {"start": v(-51.33, 172.52) * mm, "end": v(-40.33, 172.52) * mm});
            skLineSegment(sketch, "E11.4.9.1", {"start": v(-40.33, 161.52) * mm, "end": v(-40.33, 172.52) * mm});
            skLineSegment(sketch, "E11.4.9.2", {"start": v(-51.33, 161.52) * mm, "end": v(-40.33, 161.52) * mm});
            skLineSegment(sketch, "E11.4.9.3", {"start": v(-51.33, 161.52) * mm, "end": v(-51.33, 172.52) * mm});
            skLineSegment(sketch, "E11.4.10.0", {"start": v(-51.33, 189.12) * mm, "end": v(-40.33, 189.12) * mm});
            skLineSegment(sketch, "E11.4.10.1", {"start": v(-40.33, 178.12) * mm, "end": v(-40.33, 189.12) * mm});
            skLineSegment(sketch, "E11.4.10.2", {"start": v(-51.33, 178.12) * mm, "end": v(-40.33, 178.12) * mm});
            skLineSegment(sketch, "E11.4.10.3", {"start": v(-51.33, 178.12) * mm, "end": v(-51.33, 189.12) * mm});
            skLineSegment(sketch, "E11.4.11.0", {"start": v(-51.33, 205.72) * mm, "end": v(-40.33, 205.72) * mm});
            skLineSegment(sketch, "E11.4.11.1", {"start": v(-40.33, 194.72) * mm, "end": v(-40.33, 205.72) * mm});
            skLineSegment(sketch, "E11.4.11.2", {"start": v(-51.33, 194.72) * mm, "end": v(-40.33, 194.72) * mm});
            skLineSegment(sketch, "E11.4.11.3", {"start": v(-51.33, 194.72) * mm, "end": v(-51.33, 205.72) * mm});
            skLineSegment(sketch, "E11.4.12.0", {"start": v(-51.33, 222.32) * mm, "end": v(-40.33, 222.32) * mm});
            skLineSegment(sketch, "E11.4.12.1", {"start": v(-40.33, 211.32) * mm, "end": v(-40.33, 222.32) * mm});
            skLineSegment(sketch, "E11.4.12.2", {"start": v(-51.33, 211.32) * mm, "end": v(-40.33, 211.32) * mm});
            skLineSegment(sketch, "E11.4.12.3", {"start": v(-51.33, 211.32) * mm, "end": v(-51.33, 222.32) * mm});
            skLineSegment(sketch, "E11.4.13.0", {"start": v(-51.33, 238.92) * mm, "end": v(-40.33, 238.92) * mm});
            skLineSegment(sketch, "E11.4.13.1", {"start": v(-40.33, 227.92) * mm, "end": v(-40.33, 238.92) * mm});
            skLineSegment(sketch, "E11.4.13.2", {"start": v(-51.33, 227.92) * mm, "end": v(-40.33, 227.92) * mm});
            skLineSegment(sketch, "E11.4.13.3", {"start": v(-51.33, 227.92) * mm, "end": v(-51.33, 238.92) * mm});
            skLineSegment(sketch, "E11.4.14.0", {"start": v(-51.33, 255.52) * mm, "end": v(-40.33, 255.52) * mm});
            skLineSegment(sketch, "E11.4.14.1", {"start": v(-40.33, 244.52) * mm, "end": v(-40.33, 255.52) * mm});
            skLineSegment(sketch, "E11.4.14.2", {"start": v(-51.33, 244.52) * mm, "end": v(-40.33, 244.52) * mm});
            skLineSegment(sketch, "E11.4.14.3", {"start": v(-51.33, 244.52) * mm, "end": v(-51.33, 255.52) * mm});
            skLineSegment(sketch, "E11.4.15.0", {"start": v(-51.33, 272.12) * mm, "end": v(-40.33, 272.12) * mm});
            skLineSegment(sketch, "E11.4.15.1", {"start": v(-40.33, 261.12) * mm, "end": v(-40.33, 272.12) * mm});
            skLineSegment(sketch, "E11.4.15.2", {"start": v(-51.33, 261.12) * mm, "end": v(-40.33, 261.12) * mm});
            skLineSegment(sketch, "E11.4.15.3", {"start": v(-51.33, 261.12) * mm, "end": v(-51.33, 272.12) * mm});
            skLineSegment(sketch, "E11.5.0.0", {"start": v(-34.73, 23.12) * mm, "end": v(-23.73, 23.12) * mm});
            skLineSegment(sketch, "E11.5.0.1", {"start": v(-23.73, 12.12) * mm, "end": v(-23.73, 23.12) * mm});
            skLineSegment(sketch, "E11.5.0.2", {"start": v(-34.73, 12.12) * mm, "end": v(-23.73, 12.12) * mm});
            skLineSegment(sketch, "E11.5.0.3", {"start": v(-34.73, 12.12) * mm, "end": v(-34.73, 23.12) * mm});
            skLineSegment(sketch, "E11.5.1.0", {"start": v(-34.73, 39.72) * mm, "end": v(-23.73, 39.72) * mm});
            skLineSegment(sketch, "E11.5.1.1", {"start": v(-23.73, 28.72) * mm, "end": v(-23.73, 39.72) * mm});
            skLineSegment(sketch, "E11.5.1.2", {"start": v(-34.73, 28.72) * mm, "end": v(-23.73, 28.72) * mm});
            skLineSegment(sketch, "E11.5.1.3", {"start": v(-34.73, 28.72) * mm, "end": v(-34.73, 39.72) * mm});
            skLineSegment(sketch, "E11.5.2.0", {"start": v(-34.73, 56.32) * mm, "end": v(-23.73, 56.32) * mm});
            skLineSegment(sketch, "E11.5.2.1", {"start": v(-23.73, 45.32) * mm, "end": v(-23.73, 56.32) * mm});
            skLineSegment(sketch, "E11.5.2.2", {"start": v(-34.73, 45.32) * mm, "end": v(-23.73, 45.32) * mm});
            skLineSegment(sketch, "E11.5.2.3", {"start": v(-34.73, 45.32) * mm, "end": v(-34.73, 56.32) * mm});
            skLineSegment(sketch, "E11.5.3.0", {"start": v(-34.73, 72.92) * mm, "end": v(-23.73, 72.92) * mm});
            skLineSegment(sketch, "E11.5.3.1", {"start": v(-23.73, 61.92) * mm, "end": v(-23.73, 72.92) * mm});
            skLineSegment(sketch, "E11.5.3.2", {"start": v(-34.73, 61.92) * mm, "end": v(-23.73, 61.92) * mm});
            skLineSegment(sketch, "E11.5.3.3", {"start": v(-34.73, 61.92) * mm, "end": v(-34.73, 72.92) * mm});
            skLineSegment(sketch, "E11.5.4.0", {"start": v(-34.73, 89.52) * mm, "end": v(-23.73, 89.52) * mm});
            skLineSegment(sketch, "E11.5.4.1", {"start": v(-23.73, 78.52) * mm, "end": v(-23.73, 89.52) * mm});
            skLineSegment(sketch, "E11.5.4.2", {"start": v(-34.73, 78.52) * mm, "end": v(-23.73, 78.52) * mm});
            skLineSegment(sketch, "E11.5.4.3", {"start": v(-34.73, 78.52) * mm, "end": v(-34.73, 89.52) * mm});
            skLineSegment(sketch, "E11.5.5.0", {"start": v(-34.73, 106.12) * mm, "end": v(-23.73, 106.12) * mm});
            skLineSegment(sketch, "E11.5.5.1", {"start": v(-23.73, 95.12) * mm, "end": v(-23.73, 106.12) * mm});
            skLineSegment(sketch, "E11.5.5.2", {"start": v(-34.73, 95.12) * mm, "end": v(-23.73, 95.12) * mm});
            skLineSegment(sketch, "E11.5.5.3", {"start": v(-34.73, 95.12) * mm, "end": v(-34.73, 106.12) * mm});
            skLineSegment(sketch, "E11.5.6.0", {"start": v(-34.73, 122.72) * mm, "end": v(-23.73, 122.72) * mm});
            skLineSegment(sketch, "E11.5.6.1", {"start": v(-23.73, 111.72) * mm, "end": v(-23.73, 122.72) * mm});
            skLineSegment(sketch, "E11.5.6.2", {"start": v(-34.73, 111.72) * mm, "end": v(-23.73, 111.72) * mm});
            skLineSegment(sketch, "E11.5.6.3", {"start": v(-34.73, 111.72) * mm, "end": v(-34.73, 122.72) * mm});
            skLineSegment(sketch, "E11.5.7.0", {"start": v(-34.73, 139.32) * mm, "end": v(-23.73, 139.32) * mm});
            skLineSegment(sketch, "E11.5.7.1", {"start": v(-23.73, 128.32) * mm, "end": v(-23.73, 139.32) * mm});
            skLineSegment(sketch, "E11.5.7.2", {"start": v(-34.73, 128.32) * mm, "end": v(-23.73, 128.32) * mm});
            skLineSegment(sketch, "E11.5.7.3", {"start": v(-34.73, 128.32) * mm, "end": v(-34.73, 139.32) * mm});
            skLineSegment(sketch, "E11.5.8.0", {"start": v(-34.73, 155.92) * mm, "end": v(-23.73, 155.92) * mm});
            skLineSegment(sketch, "E11.5.8.1", {"start": v(-23.73, 144.92) * mm, "end": v(-23.73, 155.92) * mm});
            skLineSegment(sketch, "E11.5.8.2", {"start": v(-34.73, 144.92) * mm, "end": v(-23.73, 144.92) * mm});
            skLineSegment(sketch, "E11.5.8.3", {"start": v(-34.73, 144.92) * mm, "end": v(-34.73, 155.92) * mm});
            skLineSegment(sketch, "E11.5.9.0", {"start": v(-34.73, 172.52) * mm, "end": v(-23.73, 172.52) * mm});
            skLineSegment(sketch, "E11.5.9.1", {"start": v(-23.73, 161.52) * mm, "end": v(-23.73, 172.52) * mm});
            skLineSegment(sketch, "E11.5.9.2", {"start": v(-34.73, 161.52) * mm, "end": v(-23.73, 161.52) * mm});
            skLineSegment(sketch, "E11.5.9.3", {"start": v(-34.73, 161.52) * mm, "end": v(-34.73, 172.52) * mm});
            skLineSegment(sketch, "E11.5.10.0", {"start": v(-34.73, 189.12) * mm, "end": v(-23.73, 189.12) * mm});
            skLineSegment(sketch, "E11.5.10.1", {"start": v(-23.73, 178.12) * mm, "end": v(-23.73, 189.12) * mm});
            skLineSegment(sketch, "E11.5.10.2", {"start": v(-34.73, 178.12) * mm, "end": v(-23.73, 178.12) * mm});
            skLineSegment(sketch, "E11.5.10.3", {"start": v(-34.73, 178.12) * mm, "end": v(-34.73, 189.12) * mm});
            skLineSegment(sketch, "E11.5.11.0", {"start": v(-34.73, 205.72) * mm, "end": v(-23.73, 205.72) * mm});
            skLineSegment(sketch, "E11.5.11.1", {"start": v(-23.73, 194.72) * mm, "end": v(-23.73, 205.72) * mm});
            skLineSegment(sketch, "E11.5.11.2", {"start": v(-34.73, 194.72) * mm, "end": v(-23.73, 194.72) * mm});
            skLineSegment(sketch, "E11.5.11.3", {"start": v(-34.73, 194.72) * mm, "end": v(-34.73, 205.72) * mm});
            skLineSegment(sketch, "E11.5.12.0", {"start": v(-34.73, 222.32) * mm, "end": v(-23.73, 222.32) * mm});
            skLineSegment(sketch, "E11.5.12.1", {"start": v(-23.73, 211.32) * mm, "end": v(-23.73, 222.32) * mm});
            skLineSegment(sketch, "E11.5.12.2", {"start": v(-34.73, 211.32) * mm, "end": v(-23.73, 211.32) * mm});
            skLineSegment(sketch, "E11.5.12.3", {"start": v(-34.73, 211.32) * mm, "end": v(-34.73, 222.32) * mm});
            skLineSegment(sketch, "E11.5.13.0", {"start": v(-34.73, 238.92) * mm, "end": v(-23.73, 238.92) * mm});
            skLineSegment(sketch, "E11.5.13.1", {"start": v(-23.73, 227.92) * mm, "end": v(-23.73, 238.92) * mm});
            skLineSegment(sketch, "E11.5.13.2", {"start": v(-34.73, 227.92) * mm, "end": v(-23.73, 227.92) * mm});
            skLineSegment(sketch, "E11.5.13.3", {"start": v(-34.73, 227.92) * mm, "end": v(-34.73, 238.92) * mm});
            skLineSegment(sketch, "E11.5.14.0", {"start": v(-34.73, 255.52) * mm, "end": v(-23.73, 255.52) * mm});
            skLineSegment(sketch, "E11.5.14.1", {"start": v(-23.73, 244.52) * mm, "end": v(-23.73, 255.52) * mm});
            skLineSegment(sketch, "E11.5.14.2", {"start": v(-34.73, 244.52) * mm, "end": v(-23.73, 244.52) * mm});
            skLineSegment(sketch, "E11.5.14.3", {"start": v(-34.73, 244.52) * mm, "end": v(-34.73, 255.52) * mm});
            skLineSegment(sketch, "E11.5.15.0", {"start": v(-34.73, 272.12) * mm, "end": v(-23.73, 272.12) * mm});
            skLineSegment(sketch, "E11.5.15.1", {"start": v(-23.73, 261.12) * mm, "end": v(-23.73, 272.12) * mm});
            skLineSegment(sketch, "E11.5.15.2", {"start": v(-34.73, 261.12) * mm, "end": v(-23.73, 261.12) * mm});
            skLineSegment(sketch, "E11.5.15.3", {"start": v(-34.73, 261.12) * mm, "end": v(-34.73, 272.12) * mm});
            skLineSegment(sketch, "E11.6.0.0", {"start": v(-18.13, 23.12) * mm, "end": v(-7.13, 23.12) * mm});
            skLineSegment(sketch, "E11.6.0.1", {"start": v(-7.13, 12.12) * mm, "end": v(-7.13, 23.12) * mm});
            skLineSegment(sketch, "E11.6.0.2", {"start": v(-18.13, 12.12) * mm, "end": v(-7.13, 12.12) * mm});
            skLineSegment(sketch, "E11.6.0.3", {"start": v(-18.13, 12.12) * mm, "end": v(-18.13, 23.12) * mm});
            skLineSegment(sketch, "E11.6.1.0", {"start": v(-18.13, 39.72) * mm, "end": v(-7.13, 39.72) * mm});
            skLineSegment(sketch, "E11.6.1.1", {"start": v(-7.13, 28.72) * mm, "end": v(-7.13, 39.72) * mm});
            skLineSegment(sketch, "E11.6.1.2", {"start": v(-18.13, 28.72) * mm, "end": v(-7.13, 28.72) * mm});
            skLineSegment(sketch, "E11.6.1.3", {"start": v(-18.13, 28.72) * mm, "end": v(-18.13, 39.72) * mm});
            skLineSegment(sketch, "E11.6.2.0", {"start": v(-18.13, 56.32) * mm, "end": v(-7.13, 56.32) * mm});
            skLineSegment(sketch, "E11.6.2.1", {"start": v(-7.13, 45.32) * mm, "end": v(-7.13, 56.32) * mm});
            skLineSegment(sketch, "E11.6.2.2", {"start": v(-18.13, 45.32) * mm, "end": v(-7.13, 45.32) * mm});
            skLineSegment(sketch, "E11.6.2.3", {"start": v(-18.13, 45.32) * mm, "end": v(-18.13, 56.32) * mm});
            skLineSegment(sketch, "E11.6.3.0", {"start": v(-18.13, 72.92) * mm, "end": v(-7.13, 72.92) * mm});
            skLineSegment(sketch, "E11.6.3.1", {"start": v(-7.13, 61.92) * mm, "end": v(-7.13, 72.92) * mm});
            skLineSegment(sketch, "E11.6.3.2", {"start": v(-18.13, 61.92) * mm, "end": v(-7.13, 61.92) * mm});
            skLineSegment(sketch, "E11.6.3.3", {"start": v(-18.13, 61.92) * mm, "end": v(-18.13, 72.92) * mm});
            skLineSegment(sketch, "E11.6.4.0", {"start": v(-18.13, 89.52) * mm, "end": v(-7.13, 89.52) * mm});
            skLineSegment(sketch, "E11.6.4.1", {"start": v(-7.13, 78.52) * mm, "end": v(-7.13, 89.52) * mm});
            skLineSegment(sketch, "E11.6.4.2", {"start": v(-18.13, 78.52) * mm, "end": v(-7.13, 78.52) * mm});
            skLineSegment(sketch, "E11.6.4.3", {"start": v(-18.13, 78.52) * mm, "end": v(-18.13, 89.52) * mm});
            skLineSegment(sketch, "E11.6.5.0", {"start": v(-18.13, 106.12) * mm, "end": v(-7.13, 106.12) * mm});
            skLineSegment(sketch, "E11.6.5.1", {"start": v(-7.13, 95.12) * mm, "end": v(-7.13, 106.12) * mm});
            skLineSegment(sketch, "E11.6.5.2", {"start": v(-18.13, 95.12) * mm, "end": v(-7.13, 95.12) * mm});
            skLineSegment(sketch, "E11.6.5.3", {"start": v(-18.13, 95.12) * mm, "end": v(-18.13, 106.12) * mm});
            skLineSegment(sketch, "E11.6.6.0", {"start": v(-18.13, 122.72) * mm, "end": v(-7.13, 122.72) * mm});
            skLineSegment(sketch, "E11.6.6.1", {"start": v(-7.13, 111.72) * mm, "end": v(-7.13, 122.72) * mm});
            skLineSegment(sketch, "E11.6.6.2", {"start": v(-18.13, 111.72) * mm, "end": v(-7.13, 111.72) * mm});
            skLineSegment(sketch, "E11.6.6.3", {"start": v(-18.13, 111.72) * mm, "end": v(-18.13, 122.72) * mm});
            skLineSegment(sketch, "E11.6.7.0", {"start": v(-18.13, 139.32) * mm, "end": v(-7.13, 139.32) * mm});
            skLineSegment(sketch, "E11.6.7.1", {"start": v(-7.13, 128.32) * mm, "end": v(-7.13, 139.32) * mm});
            skLineSegment(sketch, "E11.6.7.2", {"start": v(-18.13, 128.32) * mm, "end": v(-7.13, 128.32) * mm});
            skLineSegment(sketch, "E11.6.7.3", {"start": v(-18.13, 128.32) * mm, "end": v(-18.13, 139.32) * mm});
            skLineSegment(sketch, "E11.6.8.0", {"start": v(-18.13, 155.92) * mm, "end": v(-7.13, 155.92) * mm});
            skLineSegment(sketch, "E11.6.8.1", {"start": v(-7.13, 144.92) * mm, "end": v(-7.13, 155.92) * mm});
            skLineSegment(sketch, "E11.6.8.2", {"start": v(-18.13, 144.92) * mm, "end": v(-7.13, 144.92) * mm});
            skLineSegment(sketch, "E11.6.8.3", {"start": v(-18.13, 144.92) * mm, "end": v(-18.13, 155.92) * mm});
            skLineSegment(sketch, "E11.6.9.0", {"start": v(-18.13, 172.52) * mm, "end": v(-7.13, 172.52) * mm});
            skLineSegment(sketch, "E11.6.9.1", {"start": v(-7.13, 161.52) * mm, "end": v(-7.13, 172.52) * mm});
            skLineSegment(sketch, "E11.6.9.2", {"start": v(-18.13, 161.52) * mm, "end": v(-7.13, 161.52) * mm});
            skLineSegment(sketch, "E11.6.9.3", {"start": v(-18.13, 161.52) * mm, "end": v(-18.13, 172.52) * mm});
            skLineSegment(sketch, "E11.6.10.0", {"start": v(-18.13, 189.12) * mm, "end": v(-7.13, 189.12) * mm});
            skLineSegment(sketch, "E11.6.10.1", {"start": v(-7.13, 178.12) * mm, "end": v(-7.13, 189.12) * mm});
            skLineSegment(sketch, "E11.6.10.2", {"start": v(-18.13, 178.12) * mm, "end": v(-7.13, 178.12) * mm});
            skLineSegment(sketch, "E11.6.10.3", {"start": v(-18.13, 178.12) * mm, "end": v(-18.13, 189.12) * mm});
            skLineSegment(sketch, "E11.6.11.0", {"start": v(-18.13, 205.72) * mm, "end": v(-7.13, 205.72) * mm});
            skLineSegment(sketch, "E11.6.11.1", {"start": v(-7.13, 194.72) * mm, "end": v(-7.13, 205.72) * mm});
            skLineSegment(sketch, "E11.6.11.2", {"start": v(-18.13, 194.72) * mm, "end": v(-7.13, 194.72) * mm});
            skLineSegment(sketch, "E11.6.11.3", {"start": v(-18.13, 194.72) * mm, "end": v(-18.13, 205.72) * mm});
            skLineSegment(sketch, "E11.6.12.0", {"start": v(-18.13, 222.32) * mm, "end": v(-7.13, 222.32) * mm});
            skLineSegment(sketch, "E11.6.12.1", {"start": v(-7.13, 211.32) * mm, "end": v(-7.13, 222.32) * mm});
            skLineSegment(sketch, "E11.6.12.2", {"start": v(-18.13, 211.32) * mm, "end": v(-7.13, 211.32) * mm});
            skLineSegment(sketch, "E11.6.12.3", {"start": v(-18.13, 211.32) * mm, "end": v(-18.13, 222.32) * mm});
            skLineSegment(sketch, "E11.6.13.0", {"start": v(-18.13, 238.92) * mm, "end": v(-7.13, 238.92) * mm});
            skLineSegment(sketch, "E11.6.13.1", {"start": v(-7.13, 227.92) * mm, "end": v(-7.13, 238.92) * mm});
            skLineSegment(sketch, "E11.6.13.2", {"start": v(-18.13, 227.92) * mm, "end": v(-7.13, 227.92) * mm});
            skLineSegment(sketch, "E11.6.13.3", {"start": v(-18.13, 227.92) * mm, "end": v(-18.13, 238.92) * mm});
            skLineSegment(sketch, "E11.6.14.0", {"start": v(-18.13, 255.52) * mm, "end": v(-7.13, 255.52) * mm});
            skLineSegment(sketch, "E11.6.14.1", {"start": v(-7.13, 244.52) * mm, "end": v(-7.13, 255.52) * mm});
            skLineSegment(sketch, "E11.6.14.2", {"start": v(-18.13, 244.52) * mm, "end": v(-7.13, 244.52) * mm});
            skLineSegment(sketch, "E11.6.14.3", {"start": v(-18.13, 244.52) * mm, "end": v(-18.13, 255.52) * mm});
            skLineSegment(sketch, "E11.6.15.0", {"start": v(-18.13, 272.12) * mm, "end": v(-7.13, 272.12) * mm});
            skLineSegment(sketch, "E11.6.15.1", {"start": v(-7.13, 261.12) * mm, "end": v(-7.13, 272.12) * mm});
            skLineSegment(sketch, "E11.6.15.2", {"start": v(-18.13, 261.12) * mm, "end": v(-7.13, 261.12) * mm});
            skLineSegment(sketch, "E11.6.15.3", {"start": v(-18.13, 261.12) * mm, "end": v(-18.13, 272.12) * mm});
            skLineSegment(sketch, "E11.7.0.0", {"start": v(-1.53, 23.12) * mm, "end": v(9.47, 23.12) * mm});
            skLineSegment(sketch, "E11.7.0.1", {"start": v(9.47, 12.12) * mm, "end": v(9.47, 23.12) * mm});
            skLineSegment(sketch, "E11.7.0.2", {"start": v(-1.53, 12.12) * mm, "end": v(9.47, 12.12) * mm});
            skLineSegment(sketch, "E11.7.0.3", {"start": v(-1.53, 12.12) * mm, "end": v(-1.53, 23.12) * mm});
            skLineSegment(sketch, "E11.7.1.0", {"start": v(-1.53, 39.72) * mm, "end": v(9.47, 39.72) * mm});
            skLineSegment(sketch, "E11.7.1.1", {"start": v(9.47, 28.72) * mm, "end": v(9.47, 39.72) * mm});
            skLineSegment(sketch, "E11.7.1.2", {"start": v(-1.53, 28.72) * mm, "end": v(9.47, 28.72) * mm});
            skLineSegment(sketch, "E11.7.1.3", {"start": v(-1.53, 28.72) * mm, "end": v(-1.53, 39.72) * mm});
            skLineSegment(sketch, "E11.7.2.0", {"start": v(-1.53, 56.32) * mm, "end": v(9.47, 56.32) * mm});
            skLineSegment(sketch, "E11.7.2.1", {"start": v(9.47, 45.32) * mm, "end": v(9.47, 56.32) * mm});
            skLineSegment(sketch, "E11.7.2.2", {"start": v(-1.53, 45.32) * mm, "end": v(9.47, 45.32) * mm});
            skLineSegment(sketch, "E11.7.2.3", {"start": v(-1.53, 45.32) * mm, "end": v(-1.53, 56.32) * mm});
            skLineSegment(sketch, "E11.7.3.0", {"start": v(-1.53, 72.92) * mm, "end": v(9.47, 72.92) * mm});
            skLineSegment(sketch, "E11.7.3.1", {"start": v(9.47, 61.92) * mm, "end": v(9.47, 72.92) * mm});
            skLineSegment(sketch, "E11.7.3.2", {"start": v(-1.53, 61.92) * mm, "end": v(9.47, 61.92) * mm});
            skLineSegment(sketch, "E11.7.3.3", {"start": v(-1.53, 61.92) * mm, "end": v(-1.53, 72.92) * mm});
            skLineSegment(sketch, "E11.7.4.0", {"start": v(-1.53, 89.52) * mm, "end": v(9.47, 89.52) * mm});
            skLineSegment(sketch, "E11.7.4.1", {"start": v(9.47, 78.52) * mm, "end": v(9.47, 89.52) * mm});
            skLineSegment(sketch, "E11.7.4.2", {"start": v(-1.53, 78.52) * mm, "end": v(9.47, 78.52) * mm});
            skLineSegment(sketch, "E11.7.4.3", {"start": v(-1.53, 78.52) * mm, "end": v(-1.53, 89.52) * mm});
            skLineSegment(sketch, "E11.7.5.0", {"start": v(-1.53, 106.12) * mm, "end": v(9.47, 106.12) * mm});
            skLineSegment(sketch, "E11.7.5.1", {"start": v(9.47, 95.12) * mm, "end": v(9.47, 106.12) * mm});
            skLineSegment(sketch, "E11.7.5.2", {"start": v(-1.53, 95.12) * mm, "end": v(9.47, 95.12) * mm});
            skLineSegment(sketch, "E11.7.5.3", {"start": v(-1.53, 95.12) * mm, "end": v(-1.53, 106.12) * mm});
            skLineSegment(sketch, "E11.7.6.0", {"start": v(-1.53, 122.72) * mm, "end": v(9.47, 122.72) * mm});
            skLineSegment(sketch, "E11.7.6.1", {"start": v(9.47, 111.72) * mm, "end": v(9.47, 122.72) * mm});
            skLineSegment(sketch, "E11.7.6.2", {"start": v(-1.53, 111.72) * mm, "end": v(9.47, 111.72) * mm});
            skLineSegment(sketch, "E11.7.6.3", {"start": v(-1.53, 111.72) * mm, "end": v(-1.53, 122.72) * mm});
            skLineSegment(sketch, "E11.7.7.0", {"start": v(-1.53, 139.32) * mm, "end": v(9.47, 139.32) * mm});
            skLineSegment(sketch, "E11.7.7.1", {"start": v(9.47, 128.32) * mm, "end": v(9.47, 139.32) * mm});
            skLineSegment(sketch, "E11.7.7.2", {"start": v(-1.53, 128.32) * mm, "end": v(9.47, 128.32) * mm});
            skLineSegment(sketch, "E11.7.7.3", {"start": v(-1.53, 128.32) * mm, "end": v(-1.53, 139.32) * mm});
            skLineSegment(sketch, "E11.7.8.0", {"start": v(-1.53, 155.92) * mm, "end": v(9.47, 155.92) * mm});
            skLineSegment(sketch, "E11.7.8.1", {"start": v(9.47, 144.92) * mm, "end": v(9.47, 155.92) * mm});
            skLineSegment(sketch, "E11.7.8.2", {"start": v(-1.53, 144.92) * mm, "end": v(9.47, 144.92) * mm});
            skLineSegment(sketch, "E11.7.8.3", {"start": v(-1.53, 144.92) * mm, "end": v(-1.53, 155.92) * mm});
            skLineSegment(sketch, "E11.7.9.0", {"start": v(-1.53, 172.52) * mm, "end": v(9.47, 172.52) * mm});
            skLineSegment(sketch, "E11.7.9.1", {"start": v(9.47, 161.52) * mm, "end": v(9.47, 172.52) * mm});
            skLineSegment(sketch, "E11.7.9.2", {"start": v(-1.53, 161.52) * mm, "end": v(9.47, 161.52) * mm});
            skLineSegment(sketch, "E11.7.9.3", {"start": v(-1.53, 161.52) * mm, "end": v(-1.53, 172.52) * mm});
            skLineSegment(sketch, "E11.7.10.0", {"start": v(-1.53, 189.12) * mm, "end": v(9.47, 189.12) * mm});
            skLineSegment(sketch, "E11.7.10.1", {"start": v(9.47, 178.12) * mm, "end": v(9.47, 189.12) * mm});
            skLineSegment(sketch, "E11.7.10.2", {"start": v(-1.53, 178.12) * mm, "end": v(9.47, 178.12) * mm});
            skLineSegment(sketch, "E11.7.10.3", {"start": v(-1.53, 178.12) * mm, "end": v(-1.53, 189.12) * mm});
            skLineSegment(sketch, "E11.7.11.0", {"start": v(-1.53, 205.72) * mm, "end": v(9.47, 205.72) * mm});
            skLineSegment(sketch, "E11.7.11.1", {"start": v(9.47, 194.72) * mm, "end": v(9.47, 205.72) * mm});
            skLineSegment(sketch, "E11.7.11.2", {"start": v(-1.53, 194.72) * mm, "end": v(9.47, 194.72) * mm});
            skLineSegment(sketch, "E11.7.11.3", {"start": v(-1.53, 194.72) * mm, "end": v(-1.53, 205.72) * mm});
            skLineSegment(sketch, "E11.7.12.0", {"start": v(-1.53, 222.32) * mm, "end": v(9.47, 222.32) * mm});
            skLineSegment(sketch, "E11.7.12.1", {"start": v(9.47, 211.32) * mm, "end": v(9.47, 222.32) * mm});
            skLineSegment(sketch, "E11.7.12.2", {"start": v(-1.53, 211.32) * mm, "end": v(9.47, 211.32) * mm});
            skLineSegment(sketch, "E11.7.12.3", {"start": v(-1.53, 211.32) * mm, "end": v(-1.53, 222.32) * mm});
            skLineSegment(sketch, "E11.7.13.0", {"start": v(-1.53, 238.92) * mm, "end": v(9.47, 238.92) * mm});
            skLineSegment(sketch, "E11.7.13.1", {"start": v(9.47, 227.92) * mm, "end": v(9.47, 238.92) * mm});
            skLineSegment(sketch, "E11.7.13.2", {"start": v(-1.53, 227.92) * mm, "end": v(9.47, 227.92) * mm});
            skLineSegment(sketch, "E11.7.13.3", {"start": v(-1.53, 227.92) * mm, "end": v(-1.53, 238.92) * mm});
            skLineSegment(sketch, "E11.7.14.0", {"start": v(-1.53, 255.52) * mm, "end": v(9.47, 255.52) * mm});
            skLineSegment(sketch, "E11.7.14.1", {"start": v(9.47, 244.52) * mm, "end": v(9.47, 255.52) * mm});
            skLineSegment(sketch, "E11.7.14.2", {"start": v(-1.53, 244.52) * mm, "end": v(9.47, 244.52) * mm});
            skLineSegment(sketch, "E11.7.14.3", {"start": v(-1.53, 244.52) * mm, "end": v(-1.53, 255.52) * mm});
            skLineSegment(sketch, "E11.7.15.0", {"start": v(-1.53, 272.12) * mm, "end": v(9.47, 272.12) * mm});
            skLineSegment(sketch, "E11.7.15.1", {"start": v(9.47, 261.12) * mm, "end": v(9.47, 272.12) * mm});
            skLineSegment(sketch, "E11.7.15.2", {"start": v(-1.53, 261.12) * mm, "end": v(9.47, 261.12) * mm});
            skLineSegment(sketch, "E11.7.15.3", {"start": v(-1.53, 261.12) * mm, "end": v(-1.53, 272.12) * mm});
            skLineSegment(sketch, "E11.8.0.0", {"start": v(15.07, 23.12) * mm, "end": v(26.07, 23.12) * mm});
            skLineSegment(sketch, "E11.8.0.1", {"start": v(26.07, 12.12) * mm, "end": v(26.07, 23.12) * mm});
            skLineSegment(sketch, "E11.8.0.2", {"start": v(15.07, 12.12) * mm, "end": v(26.07, 12.12) * mm});
            skLineSegment(sketch, "E11.8.0.3", {"start": v(15.07, 12.12) * mm, "end": v(15.07, 23.12) * mm});
            skLineSegment(sketch, "E11.8.1.0", {"start": v(15.07, 39.72) * mm, "end": v(26.07, 39.72) * mm});
            skLineSegment(sketch, "E11.8.1.1", {"start": v(26.07, 28.72) * mm, "end": v(26.07, 39.72) * mm});
            skLineSegment(sketch, "E11.8.1.2", {"start": v(15.07, 28.72) * mm, "end": v(26.07, 28.72) * mm});
            skLineSegment(sketch, "E11.8.1.3", {"start": v(15.07, 28.72) * mm, "end": v(15.07, 39.72) * mm});
            skLineSegment(sketch, "E11.8.2.0", {"start": v(15.07, 56.32) * mm, "end": v(26.07, 56.32) * mm});
            skLineSegment(sketch, "E11.8.2.1", {"start": v(26.07, 45.32) * mm, "end": v(26.07, 56.32) * mm});
            skLineSegment(sketch, "E11.8.2.2", {"start": v(15.07, 45.32) * mm, "end": v(26.07, 45.32) * mm});
            skLineSegment(sketch, "E11.8.2.3", {"start": v(15.07, 45.32) * mm, "end": v(15.07, 56.32) * mm});
            skLineSegment(sketch, "E11.8.3.0", {"start": v(15.07, 72.92) * mm, "end": v(26.07, 72.92) * mm});
            skLineSegment(sketch, "E11.8.3.1", {"start": v(26.07, 61.92) * mm, "end": v(26.07, 72.92) * mm});
            skLineSegment(sketch, "E11.8.3.2", {"start": v(15.07, 61.92) * mm, "end": v(26.07, 61.92) * mm});
            skLineSegment(sketch, "E11.8.3.3", {"start": v(15.07, 61.92) * mm, "end": v(15.07, 72.92) * mm});
            skLineSegment(sketch, "E11.8.4.0", {"start": v(15.07, 89.52) * mm, "end": v(26.07, 89.52) * mm});
            skLineSegment(sketch, "E11.8.4.1", {"start": v(26.07, 78.52) * mm, "end": v(26.07, 89.52) * mm});
            skLineSegment(sketch, "E11.8.4.2", {"start": v(15.07, 78.52) * mm, "end": v(26.07, 78.52) * mm});
            skLineSegment(sketch, "E11.8.4.3", {"start": v(15.07, 78.52) * mm, "end": v(15.07, 89.52) * mm});
            skLineSegment(sketch, "E11.8.5.0", {"start": v(15.07, 106.12) * mm, "end": v(26.07, 106.12) * mm});
            skLineSegment(sketch, "E11.8.5.1", {"start": v(26.07, 95.12) * mm, "end": v(26.07, 106.12) * mm});
            skLineSegment(sketch, "E11.8.5.2", {"start": v(15.07, 95.12) * mm, "end": v(26.07, 95.12) * mm});
            skLineSegment(sketch, "E11.8.5.3", {"start": v(15.07, 95.12) * mm, "end": v(15.07, 106.12) * mm});
            skLineSegment(sketch, "E11.8.6.0", {"start": v(15.07, 122.72) * mm, "end": v(26.07, 122.72) * mm});
            skLineSegment(sketch, "E11.8.6.1", {"start": v(26.07, 111.72) * mm, "end": v(26.07, 122.72) * mm});
            skLineSegment(sketch, "E11.8.6.2", {"start": v(15.07, 111.72) * mm, "end": v(26.07, 111.72) * mm});
            skLineSegment(sketch, "E11.8.6.3", {"start": v(15.07, 111.72) * mm, "end": v(15.07, 122.72) * mm});
            skLineSegment(sketch, "E11.8.7.0", {"start": v(15.07, 139.32) * mm, "end": v(26.07, 139.32) * mm});
            skLineSegment(sketch, "E11.8.7.1", {"start": v(26.07, 128.32) * mm, "end": v(26.07, 139.32) * mm});
            skLineSegment(sketch, "E11.8.7.2", {"start": v(15.07, 128.32) * mm, "end": v(26.07, 128.32) * mm});
            skLineSegment(sketch, "E11.8.7.3", {"start": v(15.07, 128.32) * mm, "end": v(15.07, 139.32) * mm});
            skLineSegment(sketch, "E11.8.8.0", {"start": v(15.07, 155.92) * mm, "end": v(26.07, 155.92) * mm});
            skLineSegment(sketch, "E11.8.8.1", {"start": v(26.07, 144.92) * mm, "end": v(26.07, 155.92) * mm});
            skLineSegment(sketch, "E11.8.8.2", {"start": v(15.07, 144.92) * mm, "end": v(26.07, 144.92) * mm});
            skLineSegment(sketch, "E11.8.8.3", {"start": v(15.07, 144.92) * mm, "end": v(15.07, 155.92) * mm});
            skLineSegment(sketch, "E11.8.9.0", {"start": v(15.07, 172.52) * mm, "end": v(26.07, 172.52) * mm});
            skLineSegment(sketch, "E11.8.9.1", {"start": v(26.07, 161.52) * mm, "end": v(26.07, 172.52) * mm});
            skLineSegment(sketch, "E11.8.9.2", {"start": v(15.07, 161.52) * mm, "end": v(26.07, 161.52) * mm});
            skLineSegment(sketch, "E11.8.9.3", {"start": v(15.07, 161.52) * mm, "end": v(15.07, 172.52) * mm});
            skLineSegment(sketch, "E11.8.10.0", {"start": v(15.07, 189.12) * mm, "end": v(26.07, 189.12) * mm});
            skLineSegment(sketch, "E11.8.10.1", {"start": v(26.07, 178.12) * mm, "end": v(26.07, 189.12) * mm});
            skLineSegment(sketch, "E11.8.10.2", {"start": v(15.07, 178.12) * mm, "end": v(26.07, 178.12) * mm});
            skLineSegment(sketch, "E11.8.10.3", {"start": v(15.07, 178.12) * mm, "end": v(15.07, 189.12) * mm});
            skLineSegment(sketch, "E11.8.11.0", {"start": v(15.07, 205.72) * mm, "end": v(26.07, 205.72) * mm});
            skLineSegment(sketch, "E11.8.11.1", {"start": v(26.07, 194.72) * mm, "end": v(26.07, 205.72) * mm});
            skLineSegment(sketch, "E11.8.11.2", {"start": v(15.07, 194.72) * mm, "end": v(26.07, 194.72) * mm});
            skLineSegment(sketch, "E11.8.11.3", {"start": v(15.07, 194.72) * mm, "end": v(15.07, 205.72) * mm});
            skLineSegment(sketch, "E11.8.12.0", {"start": v(15.07, 222.32) * mm, "end": v(26.07, 222.32) * mm});
            skLineSegment(sketch, "E11.8.12.1", {"start": v(26.07, 211.32) * mm, "end": v(26.07, 222.32) * mm});
            skLineSegment(sketch, "E11.8.12.2", {"start": v(15.07, 211.32) * mm, "end": v(26.07, 211.32) * mm});
            skLineSegment(sketch, "E11.8.12.3", {"start": v(15.07, 211.32) * mm, "end": v(15.07, 222.32) * mm});
            skLineSegment(sketch, "E11.8.13.0", {"start": v(15.07, 238.92) * mm, "end": v(26.07, 238.92) * mm});
            skLineSegment(sketch, "E11.8.13.1", {"start": v(26.07, 227.92) * mm, "end": v(26.07, 238.92) * mm});
            skLineSegment(sketch, "E11.8.13.2", {"start": v(15.07, 227.92) * mm, "end": v(26.07, 227.92) * mm});
            skLineSegment(sketch, "E11.8.13.3", {"start": v(15.07, 227.92) * mm, "end": v(15.07, 238.92) * mm});
            skLineSegment(sketch, "E11.8.14.0", {"start": v(15.07, 255.52) * mm, "end": v(26.07, 255.52) * mm});
            skLineSegment(sketch, "E11.8.14.1", {"start": v(26.07, 244.52) * mm, "end": v(26.07, 255.52) * mm});
            skLineSegment(sketch, "E11.8.14.2", {"start": v(15.07, 244.52) * mm, "end": v(26.07, 244.52) * mm});
            skLineSegment(sketch, "E11.8.14.3", {"start": v(15.07, 244.52) * mm, "end": v(15.07, 255.52) * mm});
            skLineSegment(sketch, "E11.8.15.0", {"start": v(15.07, 272.12) * mm, "end": v(26.07, 272.12) * mm});
            skLineSegment(sketch, "E11.8.15.1", {"start": v(26.07, 261.12) * mm, "end": v(26.07, 272.12) * mm});
            skLineSegment(sketch, "E11.8.15.2", {"start": v(15.07, 261.12) * mm, "end": v(26.07, 261.12) * mm});
            skLineSegment(sketch, "E11.8.15.3", {"start": v(15.07, 261.12) * mm, "end": v(15.07, 272.12) * mm});
            skLineSegment(sketch, "E11.9.0.0", {"start": v(31.67, 23.12) * mm, "end": v(42.67, 23.12) * mm});
            skLineSegment(sketch, "E11.9.0.1", {"start": v(42.67, 12.12) * mm, "end": v(42.67, 23.12) * mm});
            skLineSegment(sketch, "E11.9.0.2", {"start": v(31.67, 12.12) * mm, "end": v(42.67, 12.12) * mm});
            skLineSegment(sketch, "E11.9.0.3", {"start": v(31.67, 12.12) * mm, "end": v(31.67, 23.12) * mm});
            skLineSegment(sketch, "E11.9.1.0", {"start": v(31.67, 39.72) * mm, "end": v(42.67, 39.72) * mm});
            skLineSegment(sketch, "E11.9.1.1", {"start": v(42.67, 28.72) * mm, "end": v(42.67, 39.72) * mm});
            skLineSegment(sketch, "E11.9.1.2", {"start": v(31.67, 28.72) * mm, "end": v(42.67, 28.72) * mm});
            skLineSegment(sketch, "E11.9.1.3", {"start": v(31.67, 28.72) * mm, "end": v(31.67, 39.72) * mm});
            skLineSegment(sketch, "E11.9.2.0", {"start": v(31.67, 56.32) * mm, "end": v(42.67, 56.32) * mm});
            skLineSegment(sketch, "E11.9.2.1", {"start": v(42.67, 45.32) * mm, "end": v(42.67, 56.32) * mm});
            skLineSegment(sketch, "E11.9.2.2", {"start": v(31.67, 45.32) * mm, "end": v(42.67, 45.32) * mm});
            skLineSegment(sketch, "E11.9.2.3", {"start": v(31.67, 45.32) * mm, "end": v(31.67, 56.32) * mm});
            skLineSegment(sketch, "E11.9.3.0", {"start": v(31.67, 72.92) * mm, "end": v(42.67, 72.92) * mm});
            skLineSegment(sketch, "E11.9.3.1", {"start": v(42.67, 61.92) * mm, "end": v(42.67, 72.92) * mm});
            skLineSegment(sketch, "E11.9.3.2", {"start": v(31.67, 61.92) * mm, "end": v(42.67, 61.92) * mm});
            skLineSegment(sketch, "E11.9.3.3", {"start": v(31.67, 61.92) * mm, "end": v(31.67, 72.92) * mm});
            skLineSegment(sketch, "E11.9.4.0", {"start": v(31.67, 89.52) * mm, "end": v(42.67, 89.52) * mm});
            skLineSegment(sketch, "E11.9.4.1", {"start": v(42.67, 78.52) * mm, "end": v(42.67, 89.52) * mm});
            skLineSegment(sketch, "E11.9.4.2", {"start": v(31.67, 78.52) * mm, "end": v(42.67, 78.52) * mm});
            skLineSegment(sketch, "E11.9.4.3", {"start": v(31.67, 78.52) * mm, "end": v(31.67, 89.52) * mm});
            skLineSegment(sketch, "E11.9.5.0", {"start": v(31.67, 106.12) * mm, "end": v(42.67, 106.12) * mm});
            skLineSegment(sketch, "E11.9.5.1", {"start": v(42.67, 95.12) * mm, "end": v(42.67, 106.12) * mm});
            skLineSegment(sketch, "E11.9.5.2", {"start": v(31.67, 95.12) * mm, "end": v(42.67, 95.12) * mm});
            skLineSegment(sketch, "E11.9.5.3", {"start": v(31.67, 95.12) * mm, "end": v(31.67, 106.12) * mm});
            skLineSegment(sketch, "E11.9.6.0", {"start": v(31.67, 122.72) * mm, "end": v(42.67, 122.72) * mm});
            skLineSegment(sketch, "E11.9.6.1", {"start": v(42.67, 111.72) * mm, "end": v(42.67, 122.72) * mm});
            skLineSegment(sketch, "E11.9.6.2", {"start": v(31.67, 111.72) * mm, "end": v(42.67, 111.72) * mm});
            skLineSegment(sketch, "E11.9.6.3", {"start": v(31.67, 111.72) * mm, "end": v(31.67, 122.72) * mm});
            skLineSegment(sketch, "E11.9.7.0", {"start": v(31.67, 139.32) * mm, "end": v(42.67, 139.32) * mm});
            skLineSegment(sketch, "E11.9.7.1", {"start": v(42.67, 128.32) * mm, "end": v(42.67, 139.32) * mm});
            skLineSegment(sketch, "E11.9.7.2", {"start": v(31.67, 128.32) * mm, "end": v(42.67, 128.32) * mm});
            skLineSegment(sketch, "E11.9.7.3", {"start": v(31.67, 128.32) * mm, "end": v(31.67, 139.32) * mm});
            skLineSegment(sketch, "E11.9.8.0", {"start": v(31.67, 155.92) * mm, "end": v(42.67, 155.92) * mm});
            skLineSegment(sketch, "E11.9.8.1", {"start": v(42.67, 144.92) * mm, "end": v(42.67, 155.92) * mm});
            skLineSegment(sketch, "E11.9.8.2", {"start": v(31.67, 144.92) * mm, "end": v(42.67, 144.92) * mm});
            skLineSegment(sketch, "E11.9.8.3", {"start": v(31.67, 144.92) * mm, "end": v(31.67, 155.92) * mm});
            skLineSegment(sketch, "E11.9.9.0", {"start": v(31.67, 172.52) * mm, "end": v(42.67, 172.52) * mm});
            skLineSegment(sketch, "E11.9.9.1", {"start": v(42.67, 161.52) * mm, "end": v(42.67, 172.52) * mm});
            skLineSegment(sketch, "E11.9.9.2", {"start": v(31.67, 161.52) * mm, "end": v(42.67, 161.52) * mm});
            skLineSegment(sketch, "E11.9.9.3", {"start": v(31.67, 161.52) * mm, "end": v(31.67, 172.52) * mm});
            skLineSegment(sketch, "E11.9.10.0", {"start": v(31.67, 189.12) * mm, "end": v(42.67, 189.12) * mm});
            skLineSegment(sketch, "E11.9.10.1", {"start": v(42.67, 178.12) * mm, "end": v(42.67, 189.12) * mm});
            skLineSegment(sketch, "E11.9.10.2", {"start": v(31.67, 178.12) * mm, "end": v(42.67, 178.12) * mm});
            skLineSegment(sketch, "E11.9.10.3", {"start": v(31.67, 178.12) * mm, "end": v(31.67, 189.12) * mm});
            skLineSegment(sketch, "E11.9.11.0", {"start": v(31.67, 205.72) * mm, "end": v(42.67, 205.72) * mm});
            skLineSegment(sketch, "E11.9.11.1", {"start": v(42.67, 194.72) * mm, "end": v(42.67, 205.72) * mm});
            skLineSegment(sketch, "E11.9.11.2", {"start": v(31.67, 194.72) * mm, "end": v(42.67, 194.72) * mm});
            skLineSegment(sketch, "E11.9.11.3", {"start": v(31.67, 194.72) * mm, "end": v(31.67, 205.72) * mm});
            skLineSegment(sketch, "E11.9.12.0", {"start": v(31.67, 222.32) * mm, "end": v(42.67, 222.32) * mm});
            skLineSegment(sketch, "E11.9.12.1", {"start": v(42.67, 211.32) * mm, "end": v(42.67, 222.32) * mm});
            skLineSegment(sketch, "E11.9.12.2", {"start": v(31.67, 211.32) * mm, "end": v(42.67, 211.32) * mm});
            skLineSegment(sketch, "E11.9.12.3", {"start": v(31.67, 211.32) * mm, "end": v(31.67, 222.32) * mm});
            skLineSegment(sketch, "E11.9.13.0", {"start": v(31.67, 238.92) * mm, "end": v(42.67, 238.92) * mm});
            skLineSegment(sketch, "E11.9.13.1", {"start": v(42.67, 227.92) * mm, "end": v(42.67, 238.92) * mm});
            skLineSegment(sketch, "E11.9.13.2", {"start": v(31.67, 227.92) * mm, "end": v(42.67, 227.92) * mm});
            skLineSegment(sketch, "E11.9.13.3", {"start": v(31.67, 227.92) * mm, "end": v(31.67, 238.92) * mm});
            skLineSegment(sketch, "E11.9.14.0", {"start": v(31.67, 255.52) * mm, "end": v(42.67, 255.52) * mm});
            skLineSegment(sketch, "E11.9.14.1", {"start": v(42.67, 244.52) * mm, "end": v(42.67, 255.52) * mm});
            skLineSegment(sketch, "E11.9.14.2", {"start": v(31.67, 244.52) * mm, "end": v(42.67, 244.52) * mm});
            skLineSegment(sketch, "E11.9.14.3", {"start": v(31.67, 244.52) * mm, "end": v(31.67, 255.52) * mm});
            skLineSegment(sketch, "E11.9.15.0", {"start": v(31.67, 272.12) * mm, "end": v(42.67, 272.12) * mm});
            skLineSegment(sketch, "E11.9.15.1", {"start": v(42.67, 261.12) * mm, "end": v(42.67, 272.12) * mm});
            skLineSegment(sketch, "E11.9.15.2", {"start": v(31.67, 261.12) * mm, "end": v(42.67, 261.12) * mm});
            skLineSegment(sketch, "E11.9.15.3", {"start": v(31.67, 261.12) * mm, "end": v(31.67, 272.12) * mm});
            skLineSegment(sketch, "E11.10.0.0", {"start": v(48.27, 23.12) * mm, "end": v(59.27, 23.12) * mm});
            skLineSegment(sketch, "E11.10.0.1", {"start": v(59.27, 12.12) * mm, "end": v(59.27, 23.12) * mm});
            skLineSegment(sketch, "E11.10.0.2", {"start": v(48.27, 12.12) * mm, "end": v(59.27, 12.12) * mm});
            skLineSegment(sketch, "E11.10.0.3", {"start": v(48.27, 12.12) * mm, "end": v(48.27, 23.12) * mm});
            skLineSegment(sketch, "E11.10.1.0", {"start": v(48.27, 39.72) * mm, "end": v(59.27, 39.72) * mm});
            skLineSegment(sketch, "E11.10.1.1", {"start": v(59.27, 28.72) * mm, "end": v(59.27, 39.72) * mm});
            skLineSegment(sketch, "E11.10.1.2", {"start": v(48.27, 28.72) * mm, "end": v(59.27, 28.72) * mm});
            skLineSegment(sketch, "E11.10.1.3", {"start": v(48.27, 28.72) * mm, "end": v(48.27, 39.72) * mm});
            skLineSegment(sketch, "E11.10.2.0", {"start": v(48.27, 56.32) * mm, "end": v(59.27, 56.32) * mm});
            skLineSegment(sketch, "E11.10.2.1", {"start": v(59.27, 45.32) * mm, "end": v(59.27, 56.32) * mm});
            skLineSegment(sketch, "E11.10.2.2", {"start": v(48.27, 45.32) * mm, "end": v(59.27, 45.32) * mm});
            skLineSegment(sketch, "E11.10.2.3", {"start": v(48.27, 45.32) * mm, "end": v(48.27, 56.32) * mm});
            skLineSegment(sketch, "E11.10.3.0", {"start": v(48.27, 72.92) * mm, "end": v(59.27, 72.92) * mm});
            skLineSegment(sketch, "E11.10.3.1", {"start": v(59.27, 61.92) * mm, "end": v(59.27, 72.92) * mm});
            skLineSegment(sketch, "E11.10.3.2", {"start": v(48.27, 61.92) * mm, "end": v(59.27, 61.92) * mm});
            skLineSegment(sketch, "E11.10.3.3", {"start": v(48.27, 61.92) * mm, "end": v(48.27, 72.92) * mm});
            skLineSegment(sketch, "E11.10.4.0", {"start": v(48.27, 89.52) * mm, "end": v(59.27, 89.52) * mm});
            skLineSegment(sketch, "E11.10.4.1", {"start": v(59.27, 78.52) * mm, "end": v(59.27, 89.52) * mm});
            skLineSegment(sketch, "E11.10.4.2", {"start": v(48.27, 78.52) * mm, "end": v(59.27, 78.52) * mm});
            skLineSegment(sketch, "E11.10.4.3", {"start": v(48.27, 78.52) * mm, "end": v(48.27, 89.52) * mm});
            skLineSegment(sketch, "E11.10.5.0", {"start": v(48.27, 106.12) * mm, "end": v(59.27, 106.12) * mm});
            skLineSegment(sketch, "E11.10.5.1", {"start": v(59.27, 95.12) * mm, "end": v(59.27, 106.12) * mm});
            skLineSegment(sketch, "E11.10.5.2", {"start": v(48.27, 95.12) * mm, "end": v(59.27, 95.12) * mm});
            skLineSegment(sketch, "E11.10.5.3", {"start": v(48.27, 95.12) * mm, "end": v(48.27, 106.12) * mm});
            skLineSegment(sketch, "E11.10.6.0", {"start": v(48.27, 122.72) * mm, "end": v(59.27, 122.72) * mm});
            skLineSegment(sketch, "E11.10.6.1", {"start": v(59.27, 111.72) * mm, "end": v(59.27, 122.72) * mm});
            skLineSegment(sketch, "E11.10.6.2", {"start": v(48.27, 111.72) * mm, "end": v(59.27, 111.72) * mm});
            skLineSegment(sketch, "E11.10.6.3", {"start": v(48.27, 111.72) * mm, "end": v(48.27, 122.72) * mm});
            skLineSegment(sketch, "E11.10.7.0", {"start": v(48.27, 139.32) * mm, "end": v(59.27, 139.32) * mm});
            skLineSegment(sketch, "E11.10.7.1", {"start": v(59.27, 128.32) * mm, "end": v(59.27, 139.32) * mm});
            skLineSegment(sketch, "E11.10.7.2", {"start": v(48.27, 128.32) * mm, "end": v(59.27, 128.32) * mm});
            skLineSegment(sketch, "E11.10.7.3", {"start": v(48.27, 128.32) * mm, "end": v(48.27, 139.32) * mm});
            skLineSegment(sketch, "E11.10.8.0", {"start": v(48.27, 155.92) * mm, "end": v(59.27, 155.92) * mm});
            skLineSegment(sketch, "E11.10.8.1", {"start": v(59.27, 144.92) * mm, "end": v(59.27, 155.92) * mm});
            skLineSegment(sketch, "E11.10.8.2", {"start": v(48.27, 144.92) * mm, "end": v(59.27, 144.92) * mm});
            skLineSegment(sketch, "E11.10.8.3", {"start": v(48.27, 144.92) * mm, "end": v(48.27, 155.92) * mm});
            skLineSegment(sketch, "E11.10.9.0", {"start": v(48.27, 172.52) * mm, "end": v(59.27, 172.52) * mm});
            skLineSegment(sketch, "E11.10.9.1", {"start": v(59.27, 161.52) * mm, "end": v(59.27, 172.52) * mm});
            skLineSegment(sketch, "E11.10.9.2", {"start": v(48.27, 161.52) * mm, "end": v(59.27, 161.52) * mm});
            skLineSegment(sketch, "E11.10.9.3", {"start": v(48.27, 161.52) * mm, "end": v(48.27, 172.52) * mm});
            skLineSegment(sketch, "E11.10.10.0", {"start": v(48.27, 189.12) * mm, "end": v(59.27, 189.12) * mm});
            skLineSegment(sketch, "E11.10.10.1", {"start": v(59.27, 178.12) * mm, "end": v(59.27, 189.12) * mm});
            skLineSegment(sketch, "E11.10.10.2", {"start": v(48.27, 178.12) * mm, "end": v(59.27, 178.12) * mm});
            skLineSegment(sketch, "E11.10.10.3", {"start": v(48.27, 178.12) * mm, "end": v(48.27, 189.12) * mm});
            skLineSegment(sketch, "E11.10.11.0", {"start": v(48.27, 205.72) * mm, "end": v(59.27, 205.72) * mm});
            skLineSegment(sketch, "E11.10.11.1", {"start": v(59.27, 194.72) * mm, "end": v(59.27, 205.72) * mm});
            skLineSegment(sketch, "E11.10.11.2", {"start": v(48.27, 194.72) * mm, "end": v(59.27, 194.72) * mm});
            skLineSegment(sketch, "E11.10.11.3", {"start": v(48.27, 194.72) * mm, "end": v(48.27, 205.72) * mm});
            skLineSegment(sketch, "E11.10.12.0", {"start": v(48.27, 222.32) * mm, "end": v(59.27, 222.32) * mm});
            skLineSegment(sketch, "E11.10.12.1", {"start": v(59.27, 211.32) * mm, "end": v(59.27, 222.32) * mm});
            skLineSegment(sketch, "E11.10.12.2", {"start": v(48.27, 211.32) * mm, "end": v(59.27, 211.32) * mm});
            skLineSegment(sketch, "E11.10.12.3", {"start": v(48.27, 211.32) * mm, "end": v(48.27, 222.32) * mm});
            skLineSegment(sketch, "E11.10.13.0", {"start": v(48.27, 238.92) * mm, "end": v(59.27, 238.92) * mm});
            skLineSegment(sketch, "E11.10.13.1", {"start": v(59.27, 227.92) * mm, "end": v(59.27, 238.92) * mm});
            skLineSegment(sketch, "E11.10.13.2", {"start": v(48.27, 227.92) * mm, "end": v(59.27, 227.92) * mm});
            skLineSegment(sketch, "E11.10.13.3", {"start": v(48.27, 227.92) * mm, "end": v(48.27, 238.92) * mm});
            skLineSegment(sketch, "E11.10.14.0", {"start": v(48.27, 255.52) * mm, "end": v(59.27, 255.52) * mm});
            skLineSegment(sketch, "E11.10.14.1", {"start": v(59.27, 244.52) * mm, "end": v(59.27, 255.52) * mm});
            skLineSegment(sketch, "E11.10.14.2", {"start": v(48.27, 244.52) * mm, "end": v(59.27, 244.52) * mm});
            skLineSegment(sketch, "E11.10.14.3", {"start": v(48.27, 244.52) * mm, "end": v(48.27, 255.52) * mm});
            skLineSegment(sketch, "E11.10.15.0", {"start": v(48.27, 272.12) * mm, "end": v(59.27, 272.12) * mm});
            skLineSegment(sketch, "E11.10.15.1", {"start": v(59.27, 261.12) * mm, "end": v(59.27, 272.12) * mm});
            skLineSegment(sketch, "E11.10.15.2", {"start": v(48.27, 261.12) * mm, "end": v(59.27, 261.12) * mm});
            skLineSegment(sketch, "E11.10.15.3", {"start": v(48.27, 261.12) * mm, "end": v(48.27, 272.12) * mm});
            skLineSegment(sketch, "E11.11.0.0", {"start": v(64.87, 23.12) * mm, "end": v(75.87, 23.12) * mm});
            skLineSegment(sketch, "E11.11.0.1", {"start": v(75.87, 12.12) * mm, "end": v(75.87, 23.12) * mm});
            skLineSegment(sketch, "E11.11.0.2", {"start": v(64.87, 12.12) * mm, "end": v(75.87, 12.12) * mm});
            skLineSegment(sketch, "E11.11.0.3", {"start": v(64.87, 12.12) * mm, "end": v(64.87, 23.12) * mm});
            skLineSegment(sketch, "E11.11.1.0", {"start": v(64.87, 39.72) * mm, "end": v(75.87, 39.72) * mm});
            skLineSegment(sketch, "E11.11.1.1", {"start": v(75.87, 28.72) * mm, "end": v(75.87, 39.72) * mm});
            skLineSegment(sketch, "E11.11.1.2", {"start": v(64.87, 28.72) * mm, "end": v(75.87, 28.72) * mm});
            skLineSegment(sketch, "E11.11.1.3", {"start": v(64.87, 28.72) * mm, "end": v(64.87, 39.72) * mm});
            skLineSegment(sketch, "E11.11.2.0", {"start": v(64.87, 56.32) * mm, "end": v(75.87, 56.32) * mm});
            skLineSegment(sketch, "E11.11.2.1", {"start": v(75.87, 45.32) * mm, "end": v(75.87, 56.32) * mm});
            skLineSegment(sketch, "E11.11.2.2", {"start": v(64.87, 45.32) * mm, "end": v(75.87, 45.32) * mm});
            skLineSegment(sketch, "E11.11.2.3", {"start": v(64.87, 45.32) * mm, "end": v(64.87, 56.32) * mm});
            skLineSegment(sketch, "E11.11.3.0", {"start": v(64.87, 72.92) * mm, "end": v(75.87, 72.92) * mm});
            skLineSegment(sketch, "E11.11.3.1", {"start": v(75.87, 61.92) * mm, "end": v(75.87, 72.92) * mm});
            skLineSegment(sketch, "E11.11.3.2", {"start": v(64.87, 61.92) * mm, "end": v(75.87, 61.92) * mm});
            skLineSegment(sketch, "E11.11.3.3", {"start": v(64.87, 61.92) * mm, "end": v(64.87, 72.92) * mm});
            skLineSegment(sketch, "E11.11.4.0", {"start": v(64.87, 89.52) * mm, "end": v(75.87, 89.52) * mm});
            skLineSegment(sketch, "E11.11.4.1", {"start": v(75.87, 78.52) * mm, "end": v(75.87, 89.52) * mm});
            skLineSegment(sketch, "E11.11.4.2", {"start": v(64.87, 78.52) * mm, "end": v(75.87, 78.52) * mm});
            skLineSegment(sketch, "E11.11.4.3", {"start": v(64.87, 78.52) * mm, "end": v(64.87, 89.52) * mm});
            skLineSegment(sketch, "E11.11.5.0", {"start": v(64.87, 106.12) * mm, "end": v(75.87, 106.12) * mm});
            skLineSegment(sketch, "E11.11.5.1", {"start": v(75.87, 95.12) * mm, "end": v(75.87, 106.12) * mm});
            skLineSegment(sketch, "E11.11.5.2", {"start": v(64.87, 95.12) * mm, "end": v(75.87, 95.12) * mm});
            skLineSegment(sketch, "E11.11.5.3", {"start": v(64.87, 95.12) * mm, "end": v(64.87, 106.12) * mm});
            skLineSegment(sketch, "E11.11.6.0", {"start": v(64.87, 122.72) * mm, "end": v(75.87, 122.72) * mm});
            skLineSegment(sketch, "E11.11.6.1", {"start": v(75.87, 111.72) * mm, "end": v(75.87, 122.72) * mm});
            skLineSegment(sketch, "E11.11.6.2", {"start": v(64.87, 111.72) * mm, "end": v(75.87, 111.72) * mm});
            skLineSegment(sketch, "E11.11.6.3", {"start": v(64.87, 111.72) * mm, "end": v(64.87, 122.72) * mm});
            skLineSegment(sketch, "E11.11.7.0", {"start": v(64.87, 139.32) * mm, "end": v(75.87, 139.32) * mm});
            skLineSegment(sketch, "E11.11.7.1", {"start": v(75.87, 128.32) * mm, "end": v(75.87, 139.32) * mm});
            skLineSegment(sketch, "E11.11.7.2", {"start": v(64.87, 128.32) * mm, "end": v(75.87, 128.32) * mm});
            skLineSegment(sketch, "E11.11.7.3", {"start": v(64.87, 128.32) * mm, "end": v(64.87, 139.32) * mm});
            skLineSegment(sketch, "E11.11.8.0", {"start": v(64.87, 155.92) * mm, "end": v(75.87, 155.92) * mm});
            skLineSegment(sketch, "E11.11.8.1", {"start": v(75.87, 144.92) * mm, "end": v(75.87, 155.92) * mm});
            skLineSegment(sketch, "E11.11.8.2", {"start": v(64.87, 144.92) * mm, "end": v(75.87, 144.92) * mm});
            skLineSegment(sketch, "E11.11.8.3", {"start": v(64.87, 144.92) * mm, "end": v(64.87, 155.92) * mm});
            skLineSegment(sketch, "E11.11.9.0", {"start": v(64.87, 172.52) * mm, "end": v(75.87, 172.52) * mm});
            skLineSegment(sketch, "E11.11.9.1", {"start": v(75.87, 161.52) * mm, "end": v(75.87, 172.52) * mm});
            skLineSegment(sketch, "E11.11.9.2", {"start": v(64.87, 161.52) * mm, "end": v(75.87, 161.52) * mm});
            skLineSegment(sketch, "E11.11.9.3", {"start": v(64.87, 161.52) * mm, "end": v(64.87, 172.52) * mm});
            skLineSegment(sketch, "E11.11.10.0", {"start": v(64.87, 189.12) * mm, "end": v(75.87, 189.12) * mm});
            skLineSegment(sketch, "E11.11.10.1", {"start": v(75.87, 178.12) * mm, "end": v(75.87, 189.12) * mm});
            skLineSegment(sketch, "E11.11.10.2", {"start": v(64.87, 178.12) * mm, "end": v(75.87, 178.12) * mm});
            skLineSegment(sketch, "E11.11.10.3", {"start": v(64.87, 178.12) * mm, "end": v(64.87, 189.12) * mm});
            skLineSegment(sketch, "E11.11.11.0", {"start": v(64.87, 205.72) * mm, "end": v(75.87, 205.72) * mm});
            skLineSegment(sketch, "E11.11.11.1", {"start": v(75.87, 194.72) * mm, "end": v(75.87, 205.72) * mm});
            skLineSegment(sketch, "E11.11.11.2", {"start": v(64.87, 194.72) * mm, "end": v(75.87, 194.72) * mm});
            skLineSegment(sketch, "E11.11.11.3", {"start": v(64.87, 194.72) * mm, "end": v(64.87, 205.72) * mm});
            skLineSegment(sketch, "E11.11.12.0", {"start": v(64.87, 222.32) * mm, "end": v(75.87, 222.32) * mm});
            skLineSegment(sketch, "E11.11.12.1", {"start": v(75.87, 211.32) * mm, "end": v(75.87, 222.32) * mm});
            skLineSegment(sketch, "E11.11.12.2", {"start": v(64.87, 211.32) * mm, "end": v(75.87, 211.32) * mm});
            skLineSegment(sketch, "E11.11.12.3", {"start": v(64.87, 211.32) * mm, "end": v(64.87, 222.32) * mm});
            skLineSegment(sketch, "E11.11.13.0", {"start": v(64.87, 238.92) * mm, "end": v(75.87, 238.92) * mm});
            skLineSegment(sketch, "E11.11.13.1", {"start": v(75.87, 227.92) * mm, "end": v(75.87, 238.92) * mm});
            skLineSegment(sketch, "E11.11.13.2", {"start": v(64.87, 227.92) * mm, "end": v(75.87, 227.92) * mm});
            skLineSegment(sketch, "E11.11.13.3", {"start": v(64.87, 227.92) * mm, "end": v(64.87, 238.92) * mm});
            skLineSegment(sketch, "E11.11.14.0", {"start": v(64.87, 255.52) * mm, "end": v(75.87, 255.52) * mm});
            skLineSegment(sketch, "E11.11.14.1", {"start": v(75.87, 244.52) * mm, "end": v(75.87, 255.52) * mm});
            skLineSegment(sketch, "E11.11.14.2", {"start": v(64.87, 244.52) * mm, "end": v(75.87, 244.52) * mm});
            skLineSegment(sketch, "E11.11.14.3", {"start": v(64.87, 244.52) * mm, "end": v(64.87, 255.52) * mm});
            skLineSegment(sketch, "E11.11.15.0", {"start": v(64.87, 272.12) * mm, "end": v(75.87, 272.12) * mm});
            skLineSegment(sketch, "E11.11.15.1", {"start": v(75.87, 261.12) * mm, "end": v(75.87, 272.12) * mm});
            skLineSegment(sketch, "E11.11.15.2", {"start": v(64.87, 261.12) * mm, "end": v(75.87, 261.12) * mm});
            skLineSegment(sketch, "E11.11.15.3", {"start": v(64.87, 261.12) * mm, "end": v(64.87, 272.12) * mm});
            skLineSegment(sketch, "E11.12.0.0", {"start": v(81.47, 23.12) * mm, "end": v(92.47, 23.12) * mm});
            skLineSegment(sketch, "E11.12.0.1", {"start": v(92.47, 12.12) * mm, "end": v(92.47, 23.12) * mm});
            skLineSegment(sketch, "E11.12.0.2", {"start": v(81.47, 12.12) * mm, "end": v(92.47, 12.12) * mm});
            skLineSegment(sketch, "E11.12.0.3", {"start": v(81.47, 12.12) * mm, "end": v(81.47, 23.12) * mm});
            skLineSegment(sketch, "E11.12.1.0", {"start": v(81.47, 39.72) * mm, "end": v(92.47, 39.72) * mm});
            skLineSegment(sketch, "E11.12.1.1", {"start": v(92.47, 28.72) * mm, "end": v(92.47, 39.72) * mm});
            skLineSegment(sketch, "E11.12.1.2", {"start": v(81.47, 28.72) * mm, "end": v(92.47, 28.72) * mm});
            skLineSegment(sketch, "E11.12.1.3", {"start": v(81.47, 28.72) * mm, "end": v(81.47, 39.72) * mm});
            skLineSegment(sketch, "E11.12.2.0", {"start": v(81.47, 56.32) * mm, "end": v(92.47, 56.32) * mm});
            skLineSegment(sketch, "E11.12.2.1", {"start": v(92.47, 45.32) * mm, "end": v(92.47, 56.32) * mm});
            skLineSegment(sketch, "E11.12.2.2", {"start": v(81.47, 45.32) * mm, "end": v(92.47, 45.32) * mm});
            skLineSegment(sketch, "E11.12.2.3", {"start": v(81.47, 45.32) * mm, "end": v(81.47, 56.32) * mm});
            skLineSegment(sketch, "E11.12.3.0", {"start": v(81.47, 72.92) * mm, "end": v(92.47, 72.92) * mm});
            skLineSegment(sketch, "E11.12.3.1", {"start": v(92.47, 61.92) * mm, "end": v(92.47, 72.92) * mm});
            skLineSegment(sketch, "E11.12.3.2", {"start": v(81.47, 61.92) * mm, "end": v(92.47, 61.92) * mm});
            skLineSegment(sketch, "E11.12.3.3", {"start": v(81.47, 61.92) * mm, "end": v(81.47, 72.92) * mm});
            skLineSegment(sketch, "E11.12.4.0", {"start": v(81.47, 89.52) * mm, "end": v(92.47, 89.52) * mm});
            skLineSegment(sketch, "E11.12.4.1", {"start": v(92.47, 78.52) * mm, "end": v(92.47, 89.52) * mm});
            skLineSegment(sketch, "E11.12.4.2", {"start": v(81.47, 78.52) * mm, "end": v(92.47, 78.52) * mm});
            skLineSegment(sketch, "E11.12.4.3", {"start": v(81.47, 78.52) * mm, "end": v(81.47, 89.52) * mm});
            skLineSegment(sketch, "E11.12.5.0", {"start": v(81.47, 106.12) * mm, "end": v(92.47, 106.12) * mm});
            skLineSegment(sketch, "E11.12.5.1", {"start": v(92.47, 95.12) * mm, "end": v(92.47, 106.12) * mm});
            skLineSegment(sketch, "E11.12.5.2", {"start": v(81.47, 95.12) * mm, "end": v(92.47, 95.12) * mm});
            skLineSegment(sketch, "E11.12.5.3", {"start": v(81.47, 95.12) * mm, "end": v(81.47, 106.12) * mm});
            skLineSegment(sketch, "E11.12.6.0", {"start": v(81.47, 122.72) * mm, "end": v(92.47, 122.72) * mm});
            skLineSegment(sketch, "E11.12.6.1", {"start": v(92.47, 111.72) * mm, "end": v(92.47, 122.72) * mm});
            skLineSegment(sketch, "E11.12.6.2", {"start": v(81.47, 111.72) * mm, "end": v(92.47, 111.72) * mm});
            skLineSegment(sketch, "E11.12.6.3", {"start": v(81.47, 111.72) * mm, "end": v(81.47, 122.72) * mm});
            skLineSegment(sketch, "E11.12.7.0", {"start": v(81.47, 139.32) * mm, "end": v(92.47, 139.32) * mm});
            skLineSegment(sketch, "E11.12.7.1", {"start": v(92.47, 128.32) * mm, "end": v(92.47, 139.32) * mm});
            skLineSegment(sketch, "E11.12.7.2", {"start": v(81.47, 128.32) * mm, "end": v(92.47, 128.32) * mm});
            skLineSegment(sketch, "E11.12.7.3", {"start": v(81.47, 128.32) * mm, "end": v(81.47, 139.32) * mm});
            skLineSegment(sketch, "E11.12.8.0", {"start": v(81.47, 155.92) * mm, "end": v(92.47, 155.92) * mm});
            skLineSegment(sketch, "E11.12.8.1", {"start": v(92.47, 144.92) * mm, "end": v(92.47, 155.92) * mm});
            skLineSegment(sketch, "E11.12.8.2", {"start": v(81.47, 144.92) * mm, "end": v(92.47, 144.92) * mm});
            skLineSegment(sketch, "E11.12.8.3", {"start": v(81.47, 144.92) * mm, "end": v(81.47, 155.92) * mm});
            skLineSegment(sketch, "E11.12.9.0", {"start": v(81.47, 172.52) * mm, "end": v(92.47, 172.52) * mm});
            skLineSegment(sketch, "E11.12.9.1", {"start": v(92.47, 161.52) * mm, "end": v(92.47, 172.52) * mm});
            skLineSegment(sketch, "E11.12.9.2", {"start": v(81.47, 161.52) * mm, "end": v(92.47, 161.52) * mm});
            skLineSegment(sketch, "E11.12.9.3", {"start": v(81.47, 161.52) * mm, "end": v(81.47, 172.52) * mm});
            skLineSegment(sketch, "E11.12.10.0", {"start": v(81.47, 189.12) * mm, "end": v(92.47, 189.12) * mm});
            skLineSegment(sketch, "E11.12.10.1", {"start": v(92.47, 178.12) * mm, "end": v(92.47, 189.12) * mm});
            skLineSegment(sketch, "E11.12.10.2", {"start": v(81.47, 178.12) * mm, "end": v(92.47, 178.12) * mm});
            skLineSegment(sketch, "E11.12.10.3", {"start": v(81.47, 178.12) * mm, "end": v(81.47, 189.12) * mm});
            skLineSegment(sketch, "E11.12.11.0", {"start": v(81.47, 205.72) * mm, "end": v(92.47, 205.72) * mm});
            skLineSegment(sketch, "E11.12.11.1", {"start": v(92.47, 194.72) * mm, "end": v(92.47, 205.72) * mm});
            skLineSegment(sketch, "E11.12.11.2", {"start": v(81.47, 194.72) * mm, "end": v(92.47, 194.72) * mm});
            skLineSegment(sketch, "E11.12.11.3", {"start": v(81.47, 194.72) * mm, "end": v(81.47, 205.72) * mm});
            skLineSegment(sketch, "E11.12.12.0", {"start": v(81.47, 222.32) * mm, "end": v(92.47, 222.32) * mm});
            skLineSegment(sketch, "E11.12.12.1", {"start": v(92.47, 211.32) * mm, "end": v(92.47, 222.32) * mm});
            skLineSegment(sketch, "E11.12.12.2", {"start": v(81.47, 211.32) * mm, "end": v(92.47, 211.32) * mm});
            skLineSegment(sketch, "E11.12.12.3", {"start": v(81.47, 211.32) * mm, "end": v(81.47, 222.32) * mm});
            skLineSegment(sketch, "E11.12.13.0", {"start": v(81.47, 238.92) * mm, "end": v(92.47, 238.92) * mm});
            skLineSegment(sketch, "E11.12.13.1", {"start": v(92.47, 227.92) * mm, "end": v(92.47, 238.92) * mm});
            skLineSegment(sketch, "E11.12.13.2", {"start": v(81.47, 227.92) * mm, "end": v(92.47, 227.92) * mm});
            skLineSegment(sketch, "E11.12.13.3", {"start": v(81.47, 227.92) * mm, "end": v(81.47, 238.92) * mm});
            skLineSegment(sketch, "E11.12.14.0", {"start": v(81.47, 255.52) * mm, "end": v(92.47, 255.52) * mm});
            skLineSegment(sketch, "E11.12.14.1", {"start": v(92.47, 244.52) * mm, "end": v(92.47, 255.52) * mm});
            skLineSegment(sketch, "E11.12.14.2", {"start": v(81.47, 244.52) * mm, "end": v(92.47, 244.52) * mm});
            skLineSegment(sketch, "E11.12.14.3", {"start": v(81.47, 244.52) * mm, "end": v(81.47, 255.52) * mm});
            skLineSegment(sketch, "E11.12.15.0", {"start": v(81.47, 272.12) * mm, "end": v(92.47, 272.12) * mm});
            skLineSegment(sketch, "E11.12.15.1", {"start": v(92.47, 261.12) * mm, "end": v(92.47, 272.12) * mm});
            skLineSegment(sketch, "E11.12.15.2", {"start": v(81.47, 261.12) * mm, "end": v(92.47, 261.12) * mm});
            skLineSegment(sketch, "E11.12.15.3", {"start": v(81.47, 261.12) * mm, "end": v(81.47, 272.12) * mm});
            skLineSegment(sketch, "E11.13.0.0", {"start": v(98.07, 23.12) * mm, "end": v(109.07, 23.12) * mm});
            skLineSegment(sketch, "E11.13.0.1", {"start": v(109.07, 12.12) * mm, "end": v(109.07, 23.12) * mm});
            skLineSegment(sketch, "E11.13.0.2", {"start": v(98.07, 12.12) * mm, "end": v(109.07, 12.12) * mm});
            skLineSegment(sketch, "E11.13.0.3", {"start": v(98.07, 12.12) * mm, "end": v(98.07, 23.12) * mm});
            skLineSegment(sketch, "E11.13.1.0", {"start": v(98.07, 39.72) * mm, "end": v(109.07, 39.72) * mm});
            skLineSegment(sketch, "E11.13.1.1", {"start": v(109.07, 28.72) * mm, "end": v(109.07, 39.72) * mm});
            skLineSegment(sketch, "E11.13.1.2", {"start": v(98.07, 28.72) * mm, "end": v(109.07, 28.72) * mm});
            skLineSegment(sketch, "E11.13.1.3", {"start": v(98.07, 28.72) * mm, "end": v(98.07, 39.72) * mm});
            skLineSegment(sketch, "E11.13.2.0", {"start": v(98.07, 56.32) * mm, "end": v(109.07, 56.32) * mm});
            skLineSegment(sketch, "E11.13.2.1", {"start": v(109.07, 45.32) * mm, "end": v(109.07, 56.32) * mm});
            skLineSegment(sketch, "E11.13.2.2", {"start": v(98.07, 45.32) * mm, "end": v(109.07, 45.32) * mm});
            skLineSegment(sketch, "E11.13.2.3", {"start": v(98.07, 45.32) * mm, "end": v(98.07, 56.32) * mm});
            skLineSegment(sketch, "E11.13.3.0", {"start": v(98.07, 72.92) * mm, "end": v(109.07, 72.92) * mm});
            skLineSegment(sketch, "E11.13.3.1", {"start": v(109.07, 61.92) * mm, "end": v(109.07, 72.92) * mm});
            skLineSegment(sketch, "E11.13.3.2", {"start": v(98.07, 61.92) * mm, "end": v(109.07, 61.92) * mm});
            skLineSegment(sketch, "E11.13.3.3", {"start": v(98.07, 61.92) * mm, "end": v(98.07, 72.92) * mm});
            skLineSegment(sketch, "E11.13.4.0", {"start": v(98.07, 89.52) * mm, "end": v(109.07, 89.52) * mm});
            skLineSegment(sketch, "E11.13.4.1", {"start": v(109.07, 78.52) * mm, "end": v(109.07, 89.52) * mm});
            skLineSegment(sketch, "E11.13.4.2", {"start": v(98.07, 78.52) * mm, "end": v(109.07, 78.52) * mm});
            skLineSegment(sketch, "E11.13.4.3", {"start": v(98.07, 78.52) * mm, "end": v(98.07, 89.52) * mm});
            skLineSegment(sketch, "E11.13.5.0", {"start": v(98.07, 106.12) * mm, "end": v(109.07, 106.12) * mm});
            skLineSegment(sketch, "E11.13.5.1", {"start": v(109.07, 95.12) * mm, "end": v(109.07, 106.12) * mm});
            skLineSegment(sketch, "E11.13.5.2", {"start": v(98.07, 95.12) * mm, "end": v(109.07, 95.12) * mm});
            skLineSegment(sketch, "E11.13.5.3", {"start": v(98.07, 95.12) * mm, "end": v(98.07, 106.12) * mm});
            skLineSegment(sketch, "E11.13.6.0", {"start": v(98.07, 122.72) * mm, "end": v(109.07, 122.72) * mm});
            skLineSegment(sketch, "E11.13.6.1", {"start": v(109.07, 111.72) * mm, "end": v(109.07, 122.72) * mm});
            skLineSegment(sketch, "E11.13.6.2", {"start": v(98.07, 111.72) * mm, "end": v(109.07, 111.72) * mm});
            skLineSegment(sketch, "E11.13.6.3", {"start": v(98.07, 111.72) * mm, "end": v(98.07, 122.72) * mm});
            skLineSegment(sketch, "E11.13.7.0", {"start": v(98.07, 139.32) * mm, "end": v(109.07, 139.32) * mm});
            skLineSegment(sketch, "E11.13.7.1", {"start": v(109.07, 128.32) * mm, "end": v(109.07, 139.32) * mm});
            skLineSegment(sketch, "E11.13.7.2", {"start": v(98.07, 128.32) * mm, "end": v(109.07, 128.32) * mm});
            skLineSegment(sketch, "E11.13.7.3", {"start": v(98.07, 128.32) * mm, "end": v(98.07, 139.32) * mm});
            skLineSegment(sketch, "E11.13.8.0", {"start": v(98.07, 155.92) * mm, "end": v(109.07, 155.92) * mm});
            skLineSegment(sketch, "E11.13.8.1", {"start": v(109.07, 144.92) * mm, "end": v(109.07, 155.92) * mm});
            skLineSegment(sketch, "E11.13.8.2", {"start": v(98.07, 144.92) * mm, "end": v(109.07, 144.92) * mm});
            skLineSegment(sketch, "E11.13.8.3", {"start": v(98.07, 144.92) * mm, "end": v(98.07, 155.92) * mm});
            skLineSegment(sketch, "E11.13.9.0", {"start": v(98.07, 172.52) * mm, "end": v(109.07, 172.52) * mm});
            skLineSegment(sketch, "E11.13.9.1", {"start": v(109.07, 161.52) * mm, "end": v(109.07, 172.52) * mm});
            skLineSegment(sketch, "E11.13.9.2", {"start": v(98.07, 161.52) * mm, "end": v(109.07, 161.52) * mm});
            skLineSegment(sketch, "E11.13.9.3", {"start": v(98.07, 161.52) * mm, "end": v(98.07, 172.52) * mm});
            skLineSegment(sketch, "E11.13.10.0", {"start": v(98.07, 189.12) * mm, "end": v(109.07, 189.12) * mm});
            skLineSegment(sketch, "E11.13.10.1", {"start": v(109.07, 178.12) * mm, "end": v(109.07, 189.12) * mm});
            skLineSegment(sketch, "E11.13.10.2", {"start": v(98.07, 178.12) * mm, "end": v(109.07, 178.12) * mm});
            skLineSegment(sketch, "E11.13.10.3", {"start": v(98.07, 178.12) * mm, "end": v(98.07, 189.12) * mm});
            skLineSegment(sketch, "E11.13.11.0", {"start": v(98.07, 205.72) * mm, "end": v(109.07, 205.72) * mm});
            skLineSegment(sketch, "E11.13.11.1", {"start": v(109.07, 194.72) * mm, "end": v(109.07, 205.72) * mm});
            skLineSegment(sketch, "E11.13.11.2", {"start": v(98.07, 194.72) * mm, "end": v(109.07, 194.72) * mm});
            skLineSegment(sketch, "E11.13.11.3", {"start": v(98.07, 194.72) * mm, "end": v(98.07, 205.72) * mm});
            skLineSegment(sketch, "E11.13.12.0", {"start": v(98.07, 222.32) * mm, "end": v(109.07, 222.32) * mm});
            skLineSegment(sketch, "E11.13.12.1", {"start": v(109.07, 211.32) * mm, "end": v(109.07, 222.32) * mm});
            skLineSegment(sketch, "E11.13.12.2", {"start": v(98.07, 211.32) * mm, "end": v(109.07, 211.32) * mm});
            skLineSegment(sketch, "E11.13.12.3", {"start": v(98.07, 211.32) * mm, "end": v(98.07, 222.32) * mm});
            skLineSegment(sketch, "E11.13.13.0", {"start": v(98.07, 238.92) * mm, "end": v(109.07, 238.92) * mm});
            skLineSegment(sketch, "E11.13.13.1", {"start": v(109.07, 227.92) * mm, "end": v(109.07, 238.92) * mm});
            skLineSegment(sketch, "E11.13.13.2", {"start": v(98.07, 227.92) * mm, "end": v(109.07, 227.92) * mm});
            skLineSegment(sketch, "E11.13.13.3", {"start": v(98.07, 227.92) * mm, "end": v(98.07, 238.92) * mm});
            skLineSegment(sketch, "E11.13.14.0", {"start": v(98.07, 255.52) * mm, "end": v(109.07, 255.52) * mm});
            skLineSegment(sketch, "E11.13.14.1", {"start": v(109.07, 244.52) * mm, "end": v(109.07, 255.52) * mm});
            skLineSegment(sketch, "E11.13.14.2", {"start": v(98.07, 244.52) * mm, "end": v(109.07, 244.52) * mm});
            skLineSegment(sketch, "E11.13.14.3", {"start": v(98.07, 244.52) * mm, "end": v(98.07, 255.52) * mm});
            skLineSegment(sketch, "E11.13.15.0", {"start": v(98.07, 272.12) * mm, "end": v(109.07, 272.12) * mm});
            skLineSegment(sketch, "E11.13.15.1", {"start": v(109.07, 261.12) * mm, "end": v(109.07, 272.12) * mm});
            skLineSegment(sketch, "E11.13.15.2", {"start": v(98.07, 261.12) * mm, "end": v(109.07, 261.12) * mm});
            skLineSegment(sketch, "E11.13.15.3", {"start": v(98.07, 261.12) * mm, "end": v(98.07, 272.12) * mm});
            skLineSegment(sketch, "E11.14.0.0", {"start": v(114.67, 23.12) * mm, "end": v(125.67, 23.12) * mm});
            skLineSegment(sketch, "E11.14.0.1", {"start": v(125.67, 12.12) * mm, "end": v(125.67, 23.12) * mm});
            skLineSegment(sketch, "E11.14.0.2", {"start": v(114.67, 12.12) * mm, "end": v(125.67, 12.12) * mm});
            skLineSegment(sketch, "E11.14.0.3", {"start": v(114.67, 12.12) * mm, "end": v(114.67, 23.12) * mm});
            skLineSegment(sketch, "E11.14.1.0", {"start": v(114.67, 39.72) * mm, "end": v(125.67, 39.72) * mm});
            skLineSegment(sketch, "E11.14.1.1", {"start": v(125.67, 28.72) * mm, "end": v(125.67, 39.72) * mm});
            skLineSegment(sketch, "E11.14.1.2", {"start": v(114.67, 28.72) * mm, "end": v(125.67, 28.72) * mm});
            skLineSegment(sketch, "E11.14.1.3", {"start": v(114.67, 28.72) * mm, "end": v(114.67, 39.72) * mm});
            skLineSegment(sketch, "E11.14.2.0", {"start": v(114.67, 56.32) * mm, "end": v(125.67, 56.32) * mm});
            skLineSegment(sketch, "E11.14.2.1", {"start": v(125.67, 45.32) * mm, "end": v(125.67, 56.32) * mm});
            skLineSegment(sketch, "E11.14.2.2", {"start": v(114.67, 45.32) * mm, "end": v(125.67, 45.32) * mm});
            skLineSegment(sketch, "E11.14.2.3", {"start": v(114.67, 45.32) * mm, "end": v(114.67, 56.32) * mm});
            skLineSegment(sketch, "E11.14.3.0", {"start": v(114.67, 72.92) * mm, "end": v(125.67, 72.92) * mm});
            skLineSegment(sketch, "E11.14.3.1", {"start": v(125.67, 61.92) * mm, "end": v(125.67, 72.92) * mm});
            skLineSegment(sketch, "E11.14.3.2", {"start": v(114.67, 61.92) * mm, "end": v(125.67, 61.92) * mm});
            skLineSegment(sketch, "E11.14.3.3", {"start": v(114.67, 61.92) * mm, "end": v(114.67, 72.92) * mm});
            skLineSegment(sketch, "E11.14.4.0", {"start": v(114.67, 89.52) * mm, "end": v(125.67, 89.52) * mm});
            skLineSegment(sketch, "E11.14.4.1", {"start": v(125.67, 78.52) * mm, "end": v(125.67, 89.52) * mm});
            skLineSegment(sketch, "E11.14.4.2", {"start": v(114.67, 78.52) * mm, "end": v(125.67, 78.52) * mm});
            skLineSegment(sketch, "E11.14.4.3", {"start": v(114.67, 78.52) * mm, "end": v(114.67, 89.52) * mm});
            skLineSegment(sketch, "E11.14.5.0", {"start": v(114.67, 106.12) * mm, "end": v(125.67, 106.12) * mm});
            skLineSegment(sketch, "E11.14.5.1", {"start": v(125.67, 95.12) * mm, "end": v(125.67, 106.12) * mm});
            skLineSegment(sketch, "E11.14.5.2", {"start": v(114.67, 95.12) * mm, "end": v(125.67, 95.12) * mm});
            skLineSegment(sketch, "E11.14.5.3", {"start": v(114.67, 95.12) * mm, "end": v(114.67, 106.12) * mm});
            skLineSegment(sketch, "E11.14.6.0", {"start": v(114.67, 122.72) * mm, "end": v(125.67, 122.72) * mm});
            skLineSegment(sketch, "E11.14.6.1", {"start": v(125.67, 111.72) * mm, "end": v(125.67, 122.72) * mm});
            skLineSegment(sketch, "E11.14.6.2", {"start": v(114.67, 111.72) * mm, "end": v(125.67, 111.72) * mm});
            skLineSegment(sketch, "E11.14.6.3", {"start": v(114.67, 111.72) * mm, "end": v(114.67, 122.72) * mm});
            skLineSegment(sketch, "E11.14.7.0", {"start": v(114.67, 139.32) * mm, "end": v(125.67, 139.32) * mm});
            skLineSegment(sketch, "E11.14.7.1", {"start": v(125.67, 128.32) * mm, "end": v(125.67, 139.32) * mm});
            skLineSegment(sketch, "E11.14.7.2", {"start": v(114.67, 128.32) * mm, "end": v(125.67, 128.32) * mm});
            skLineSegment(sketch, "E11.14.7.3", {"start": v(114.67, 128.32) * mm, "end": v(114.67, 139.32) * mm});
            skLineSegment(sketch, "E11.14.8.0", {"start": v(114.67, 155.92) * mm, "end": v(125.67, 155.92) * mm});
            skLineSegment(sketch, "E11.14.8.1", {"start": v(125.67, 144.92) * mm, "end": v(125.67, 155.92) * mm});
            skLineSegment(sketch, "E11.14.8.2", {"start": v(114.67, 144.92) * mm, "end": v(125.67, 144.92) * mm});
            skLineSegment(sketch, "E11.14.8.3", {"start": v(114.67, 144.92) * mm, "end": v(114.67, 155.92) * mm});
            skLineSegment(sketch, "E11.14.9.0", {"start": v(114.67, 172.52) * mm, "end": v(125.67, 172.52) * mm});
            skLineSegment(sketch, "E11.14.9.1", {"start": v(125.67, 161.52) * mm, "end": v(125.67, 172.52) * mm});
            skLineSegment(sketch, "E11.14.9.2", {"start": v(114.67, 161.52) * mm, "end": v(125.67, 161.52) * mm});
            skLineSegment(sketch, "E11.14.9.3", {"start": v(114.67, 161.52) * mm, "end": v(114.67, 172.52) * mm});
            skLineSegment(sketch, "E11.14.10.0", {"start": v(114.67, 189.12) * mm, "end": v(125.67, 189.12) * mm});
            skLineSegment(sketch, "E11.14.10.1", {"start": v(125.67, 178.12) * mm, "end": v(125.67, 189.12) * mm});
            skLineSegment(sketch, "E11.14.10.2", {"start": v(114.67, 178.12) * mm, "end": v(125.67, 178.12) * mm});
            skLineSegment(sketch, "E11.14.10.3", {"start": v(114.67, 178.12) * mm, "end": v(114.67, 189.12) * mm});
            skLineSegment(sketch, "E11.14.11.0", {"start": v(114.67, 205.72) * mm, "end": v(125.67, 205.72) * mm});
            skLineSegment(sketch, "E11.14.11.1", {"start": v(125.67, 194.72) * mm, "end": v(125.67, 205.72) * mm});
            skLineSegment(sketch, "E11.14.11.2", {"start": v(114.67, 194.72) * mm, "end": v(125.67, 194.72) * mm});
            skLineSegment(sketch, "E11.14.11.3", {"start": v(114.67, 194.72) * mm, "end": v(114.67, 205.72) * mm});
            skLineSegment(sketch, "E11.14.12.0", {"start": v(114.67, 222.32) * mm, "end": v(125.67, 222.32) * mm});
            skLineSegment(sketch, "E11.14.12.1", {"start": v(125.67, 211.32) * mm, "end": v(125.67, 222.32) * mm});
            skLineSegment(sketch, "E11.14.12.2", {"start": v(114.67, 211.32) * mm, "end": v(125.67, 211.32) * mm});
            skLineSegment(sketch, "E11.14.12.3", {"start": v(114.67, 211.32) * mm, "end": v(114.67, 222.32) * mm});
            skLineSegment(sketch, "E11.14.13.0", {"start": v(114.67, 238.92) * mm, "end": v(125.67, 238.92) * mm});
            skLineSegment(sketch, "E11.14.13.1", {"start": v(125.67, 227.92) * mm, "end": v(125.67, 238.92) * mm});
            skLineSegment(sketch, "E11.14.13.2", {"start": v(114.67, 227.92) * mm, "end": v(125.67, 227.92) * mm});
            skLineSegment(sketch, "E11.14.13.3", {"start": v(114.67, 227.92) * mm, "end": v(114.67, 238.92) * mm});
            skLineSegment(sketch, "E11.14.14.0", {"start": v(114.67, 255.52) * mm, "end": v(125.67, 255.52) * mm});
            skLineSegment(sketch, "E11.14.14.1", {"start": v(125.67, 244.52) * mm, "end": v(125.67, 255.52) * mm});
            skLineSegment(sketch, "E11.14.14.2", {"start": v(114.67, 244.52) * mm, "end": v(125.67, 244.52) * mm});
            skLineSegment(sketch, "E11.14.14.3", {"start": v(114.67, 244.52) * mm, "end": v(114.67, 255.52) * mm});
            skLineSegment(sketch, "E11.14.15.0", {"start": v(114.67, 272.12) * mm, "end": v(125.67, 272.12) * mm});
            skLineSegment(sketch, "E11.14.15.1", {"start": v(125.67, 261.12) * mm, "end": v(125.67, 272.12) * mm});
            skLineSegment(sketch, "E11.14.15.2", {"start": v(114.67, 261.12) * mm, "end": v(125.67, 261.12) * mm});
            skLineSegment(sketch, "E11.14.15.3", {"start": v(114.67, 261.12) * mm, "end": v(114.67, 272.12) * mm});
            skLineSegment(sketch, "E11.15.0.0", {"start": v(131.27, 23.12) * mm, "end": v(142.27, 23.12) * mm});
            skLineSegment(sketch, "E11.15.0.1", {"start": v(142.27, 12.12) * mm, "end": v(142.27, 23.12) * mm});
            skLineSegment(sketch, "E11.15.0.2", {"start": v(131.27, 12.12) * mm, "end": v(142.27, 12.12) * mm});
            skLineSegment(sketch, "E11.15.0.3", {"start": v(131.27, 12.12) * mm, "end": v(131.27, 23.12) * mm});
            skLineSegment(sketch, "E11.15.1.0", {"start": v(131.27, 39.72) * mm, "end": v(142.27, 39.72) * mm});
            skLineSegment(sketch, "E11.15.1.1", {"start": v(142.27, 28.72) * mm, "end": v(142.27, 39.72) * mm});
            skLineSegment(sketch, "E11.15.1.2", {"start": v(131.27, 28.72) * mm, "end": v(142.27, 28.72) * mm});
            skLineSegment(sketch, "E11.15.1.3", {"start": v(131.27, 28.72) * mm, "end": v(131.27, 39.72) * mm});
            skLineSegment(sketch, "E11.15.2.0", {"start": v(131.27, 56.32) * mm, "end": v(142.27, 56.32) * mm});
            skLineSegment(sketch, "E11.15.2.1", {"start": v(142.27, 45.32) * mm, "end": v(142.27, 56.32) * mm});
            skLineSegment(sketch, "E11.15.2.2", {"start": v(131.27, 45.32) * mm, "end": v(142.27, 45.32) * mm});
            skLineSegment(sketch, "E11.15.2.3", {"start": v(131.27, 45.32) * mm, "end": v(131.27, 56.32) * mm});
            skLineSegment(sketch, "E11.15.3.0", {"start": v(131.27, 72.92) * mm, "end": v(142.27, 72.92) * mm});
            skLineSegment(sketch, "E11.15.3.1", {"start": v(142.27, 61.92) * mm, "end": v(142.27, 72.92) * mm});
            skLineSegment(sketch, "E11.15.3.2", {"start": v(131.27, 61.92) * mm, "end": v(142.27, 61.92) * mm});
            skLineSegment(sketch, "E11.15.3.3", {"start": v(131.27, 61.92) * mm, "end": v(131.27, 72.92) * mm});
            skLineSegment(sketch, "E11.15.4.0", {"start": v(131.27, 89.52) * mm, "end": v(142.27, 89.52) * mm});
            skLineSegment(sketch, "E11.15.4.1", {"start": v(142.27, 78.52) * mm, "end": v(142.27, 89.52) * mm});
            skLineSegment(sketch, "E11.15.4.2", {"start": v(131.27, 78.52) * mm, "end": v(142.27, 78.52) * mm});
            skLineSegment(sketch, "E11.15.4.3", {"start": v(131.27, 78.52) * mm, "end": v(131.27, 89.52) * mm});
            skLineSegment(sketch, "E11.15.5.0", {"start": v(131.27, 106.12) * mm, "end": v(142.27, 106.12) * mm});
            skLineSegment(sketch, "E11.15.5.1", {"start": v(142.27, 95.12) * mm, "end": v(142.27, 106.12) * mm});
            skLineSegment(sketch, "E11.15.5.2", {"start": v(131.27, 95.12) * mm, "end": v(142.27, 95.12) * mm});
            skLineSegment(sketch, "E11.15.5.3", {"start": v(131.27, 95.12) * mm, "end": v(131.27, 106.12) * mm});
            skLineSegment(sketch, "E11.15.6.0", {"start": v(131.27, 122.72) * mm, "end": v(142.27, 122.72) * mm});
            skLineSegment(sketch, "E11.15.6.1", {"start": v(142.27, 111.72) * mm, "end": v(142.27, 122.72) * mm});
            skLineSegment(sketch, "E11.15.6.2", {"start": v(131.27, 111.72) * mm, "end": v(142.27, 111.72) * mm});
            skLineSegment(sketch, "E11.15.6.3", {"start": v(131.27, 111.72) * mm, "end": v(131.27, 122.72) * mm});
            skLineSegment(sketch, "E11.15.7.0", {"start": v(131.27, 139.32) * mm, "end": v(142.27, 139.32) * mm});
            skLineSegment(sketch, "E11.15.7.1", {"start": v(142.27, 128.32) * mm, "end": v(142.27, 139.32) * mm});
            skLineSegment(sketch, "E11.15.7.2", {"start": v(131.27, 128.32) * mm, "end": v(142.27, 128.32) * mm});
            skLineSegment(sketch, "E11.15.7.3", {"start": v(131.27, 128.32) * mm, "end": v(131.27, 139.32) * mm});
            skLineSegment(sketch, "E11.15.8.0", {"start": v(131.27, 155.92) * mm, "end": v(142.27, 155.92) * mm});
            skLineSegment(sketch, "E11.15.8.1", {"start": v(142.27, 144.92) * mm, "end": v(142.27, 155.92) * mm});
            skLineSegment(sketch, "E11.15.8.2", {"start": v(131.27, 144.92) * mm, "end": v(142.27, 144.92) * mm});
            skLineSegment(sketch, "E11.15.8.3", {"start": v(131.27, 144.92) * mm, "end": v(131.27, 155.92) * mm});
            skLineSegment(sketch, "E11.15.9.0", {"start": v(131.27, 172.52) * mm, "end": v(142.27, 172.52) * mm});
            skLineSegment(sketch, "E11.15.9.1", {"start": v(142.27, 161.52) * mm, "end": v(142.27, 172.52) * mm});
            skLineSegment(sketch, "E11.15.9.2", {"start": v(131.27, 161.52) * mm, "end": v(142.27, 161.52) * mm});
            skLineSegment(sketch, "E11.15.9.3", {"start": v(131.27, 161.52) * mm, "end": v(131.27, 172.52) * mm});
            skLineSegment(sketch, "E11.15.10.0", {"start": v(131.27, 189.12) * mm, "end": v(142.27, 189.12) * mm});
            skLineSegment(sketch, "E11.15.10.1", {"start": v(142.27, 178.12) * mm, "end": v(142.27, 189.12) * mm});
            skLineSegment(sketch, "E11.15.10.2", {"start": v(131.27, 178.12) * mm, "end": v(142.27, 178.12) * mm});
            skLineSegment(sketch, "E11.15.10.3", {"start": v(131.27, 178.12) * mm, "end": v(131.27, 189.12) * mm});
            skLineSegment(sketch, "E11.15.11.0", {"start": v(131.27, 205.72) * mm, "end": v(142.27, 205.72) * mm});
            skLineSegment(sketch, "E11.15.11.1", {"start": v(142.27, 194.72) * mm, "end": v(142.27, 205.72) * mm});
            skLineSegment(sketch, "E11.15.11.2", {"start": v(131.27, 194.72) * mm, "end": v(142.27, 194.72) * mm});
            skLineSegment(sketch, "E11.15.11.3", {"start": v(131.27, 194.72) * mm, "end": v(131.27, 205.72) * mm});
            skLineSegment(sketch, "E11.15.12.0", {"start": v(131.27, 222.32) * mm, "end": v(142.27, 222.32) * mm});
            skLineSegment(sketch, "E11.15.12.1", {"start": v(142.27, 211.32) * mm, "end": v(142.27, 222.32) * mm});
            skLineSegment(sketch, "E11.15.12.2", {"start": v(131.27, 211.32) * mm, "end": v(142.27, 211.32) * mm});
            skLineSegment(sketch, "E11.15.12.3", {"start": v(131.27, 211.32) * mm, "end": v(131.27, 222.32) * mm});
            skLineSegment(sketch, "E11.15.13.0", {"start": v(131.27, 238.92) * mm, "end": v(142.27, 238.92) * mm});
            skLineSegment(sketch, "E11.15.13.1", {"start": v(142.27, 227.92) * mm, "end": v(142.27, 238.92) * mm});
            skLineSegment(sketch, "E11.15.13.2", {"start": v(131.27, 227.92) * mm, "end": v(142.27, 227.92) * mm});
            skLineSegment(sketch, "E11.15.13.3", {"start": v(131.27, 227.92) * mm, "end": v(131.27, 238.92) * mm});
            skLineSegment(sketch, "E11.15.14.0", {"start": v(131.27, 255.52) * mm, "end": v(142.27, 255.52) * mm});
            skLineSegment(sketch, "E11.15.14.1", {"start": v(142.27, 244.52) * mm, "end": v(142.27, 255.52) * mm});
            skLineSegment(sketch, "E11.15.14.2", {"start": v(131.27, 244.52) * mm, "end": v(142.27, 244.52) * mm});
            skLineSegment(sketch, "E11.15.14.3", {"start": v(131.27, 244.52) * mm, "end": v(131.27, 255.52) * mm});
            skLineSegment(sketch, "E11.15.15.0", {"start": v(131.27, 272.12) * mm, "end": v(142.27, 272.12) * mm});
            skLineSegment(sketch, "E11.15.15.1", {"start": v(142.27, 261.12) * mm, "end": v(142.27, 272.12) * mm});
            skLineSegment(sketch, "E11.15.15.2", {"start": v(131.27, 261.12) * mm, "end": v(142.27, 261.12) * mm});
            skLineSegment(sketch, "E11.15.15.3", {"start": v(131.27, 261.12) * mm, "end": v(131.27, 272.12) * mm});
            skLineSegment(sketch, "E11.direction2", {"start": v(-117.73, 12.12) * mm, "end": v(-117.73, 28.72) * mm, "construction": true});
            skLineSegment(sketch, "E12.bottom", {"start": v(-119.93, 9.92) * mm, "end": v(-104.53, 9.92) * mm});
            skLineSegment(sketch, "E12.top", {"start": v(-119.93, 25.32) * mm, "end": v(-104.53, 25.32) * mm});
            skLineSegment(sketch, "E12.left", {"start": v(-119.93, 9.92) * mm, "end": v(-119.93, 25.32) * mm});
            skLineSegment(sketch, "E12.right", {"start": v(-104.53, 9.92) * mm, "end": v(-104.53, 25.32) * mm});
            skLineSegment(sketch, "E13.0.1.0", {"start": v(-119.93, 26.52) * mm, "end": v(-119.93, 41.92) * mm});
            skLineSegment(sketch, "E13.0.1.1", {"start": v(-119.93, 26.52) * mm, "end": v(-104.53, 26.52) * mm});
            skLineSegment(sketch, "E13.0.1.2", {"start": v(-104.53, 26.52) * mm, "end": v(-104.53, 41.92) * mm});
            skLineSegment(sketch, "E13.0.1.3", {"start": v(-119.93, 41.92) * mm, "end": v(-104.53, 41.92) * mm});
            skLineSegment(sketch, "E13.0.2.0", {"start": v(-119.93, 43.12) * mm, "end": v(-119.93, 58.52) * mm});
            skLineSegment(sketch, "E13.0.2.1", {"start": v(-119.93, 43.12) * mm, "end": v(-104.53, 43.12) * mm});
            skLineSegment(sketch, "E13.0.2.2", {"start": v(-104.53, 43.12) * mm, "end": v(-104.53, 58.52) * mm});
            skLineSegment(sketch, "E13.0.2.3", {"start": v(-119.93, 58.52) * mm, "end": v(-104.53, 58.52) * mm});
            skLineSegment(sketch, "E13.0.3.0", {"start": v(-119.93, 59.72) * mm, "end": v(-119.93, 75.12) * mm});
            skLineSegment(sketch, "E13.0.3.1", {"start": v(-119.93, 59.72) * mm, "end": v(-104.53, 59.72) * mm});
            skLineSegment(sketch, "E13.0.3.2", {"start": v(-104.53, 59.72) * mm, "end": v(-104.53, 75.12) * mm});
            skLineSegment(sketch, "E13.0.3.3", {"start": v(-119.93, 75.12) * mm, "end": v(-104.53, 75.12) * mm});
            skLineSegment(sketch, "E13.0.4.0", {"start": v(-119.93, 76.32) * mm, "end": v(-119.93, 91.72) * mm});
            skLineSegment(sketch, "E13.0.4.1", {"start": v(-119.93, 76.32) * mm, "end": v(-104.53, 76.32) * mm});
            skLineSegment(sketch, "E13.0.4.2", {"start": v(-104.53, 76.32) * mm, "end": v(-104.53, 91.72) * mm});
            skLineSegment(sketch, "E13.0.4.3", {"start": v(-119.93, 91.72) * mm, "end": v(-104.53, 91.72) * mm});
            skLineSegment(sketch, "E13.0.5.0", {"start": v(-119.93, 92.92) * mm, "end": v(-119.93, 108.32) * mm});
            skLineSegment(sketch, "E13.0.5.1", {"start": v(-119.93, 92.92) * mm, "end": v(-104.53, 92.92) * mm});
            skLineSegment(sketch, "E13.0.5.2", {"start": v(-104.53, 92.92) * mm, "end": v(-104.53, 108.32) * mm});
            skLineSegment(sketch, "E13.0.5.3", {"start": v(-119.93, 108.32) * mm, "end": v(-104.53, 108.32) * mm});
            skLineSegment(sketch, "E13.0.6.0", {"start": v(-119.93, 109.52) * mm, "end": v(-119.93, 124.92) * mm});
            skLineSegment(sketch, "E13.0.6.1", {"start": v(-119.93, 109.52) * mm, "end": v(-104.53, 109.52) * mm});
            skLineSegment(sketch, "E13.0.6.2", {"start": v(-104.53, 109.52) * mm, "end": v(-104.53, 124.92) * mm});
            skLineSegment(sketch, "E13.0.6.3", {"start": v(-119.93, 124.92) * mm, "end": v(-104.53, 124.92) * mm});
            skLineSegment(sketch, "E13.0.7.0", {"start": v(-119.93, 126.12) * mm, "end": v(-119.93, 141.52) * mm});
            skLineSegment(sketch, "E13.0.7.1", {"start": v(-119.93, 126.12) * mm, "end": v(-104.53, 126.12) * mm});
            skLineSegment(sketch, "E13.0.7.2", {"start": v(-104.53, 126.12) * mm, "end": v(-104.53, 141.52) * mm});
            skLineSegment(sketch, "E13.0.7.3", {"start": v(-119.93, 141.52) * mm, "end": v(-104.53, 141.52) * mm});
            skLineSegment(sketch, "E13.0.8.0", {"start": v(-119.93, 142.72) * mm, "end": v(-119.93, 158.12) * mm});
            skLineSegment(sketch, "E13.0.8.1", {"start": v(-119.93, 142.72) * mm, "end": v(-104.53, 142.72) * mm});
            skLineSegment(sketch, "E13.0.8.2", {"start": v(-104.53, 142.72) * mm, "end": v(-104.53, 158.12) * mm});
            skLineSegment(sketch, "E13.0.8.3", {"start": v(-119.93, 158.12) * mm, "end": v(-104.53, 158.12) * mm});
            skLineSegment(sketch, "E13.0.9.0", {"start": v(-119.93, 159.32) * mm, "end": v(-119.93, 174.72) * mm});
            skLineSegment(sketch, "E13.0.9.1", {"start": v(-119.93, 159.32) * mm, "end": v(-104.53, 159.32) * mm});
            skLineSegment(sketch, "E13.0.9.2", {"start": v(-104.53, 159.32) * mm, "end": v(-104.53, 174.72) * mm});
            skLineSegment(sketch, "E13.0.9.3", {"start": v(-119.93, 174.72) * mm, "end": v(-104.53, 174.72) * mm});
            skLineSegment(sketch, "E13.0.10.0", {"start": v(-119.93, 175.92) * mm, "end": v(-119.93, 191.32) * mm});
            skLineSegment(sketch, "E13.0.10.1", {"start": v(-119.93, 175.92) * mm, "end": v(-104.53, 175.92) * mm});
            skLineSegment(sketch, "E13.0.10.2", {"start": v(-104.53, 175.92) * mm, "end": v(-104.53, 191.32) * mm});
            skLineSegment(sketch, "E13.0.10.3", {"start": v(-119.93, 191.32) * mm, "end": v(-104.53, 191.32) * mm});
            skLineSegment(sketch, "E13.0.11.0", {"start": v(-119.93, 192.52) * mm, "end": v(-119.93, 207.92) * mm});
            skLineSegment(sketch, "E13.0.11.1", {"start": v(-119.93, 192.52) * mm, "end": v(-104.53, 192.52) * mm});
            skLineSegment(sketch, "E13.0.11.2", {"start": v(-104.53, 192.52) * mm, "end": v(-104.53, 207.92) * mm});
            skLineSegment(sketch, "E13.0.11.3", {"start": v(-119.93, 207.92) * mm, "end": v(-104.53, 207.92) * mm});
            skLineSegment(sketch, "E13.0.12.0", {"start": v(-119.93, 209.12) * mm, "end": v(-119.93, 224.52) * mm});
            skLineSegment(sketch, "E13.0.12.1", {"start": v(-119.93, 209.12) * mm, "end": v(-104.53, 209.12) * mm});
            skLineSegment(sketch, "E13.0.12.2", {"start": v(-104.53, 209.12) * mm, "end": v(-104.53, 224.52) * mm});
            skLineSegment(sketch, "E13.0.12.3", {"start": v(-119.93, 224.52) * mm, "end": v(-104.53, 224.52) * mm});
            skLineSegment(sketch, "E13.0.13.0", {"start": v(-119.93, 225.72) * mm, "end": v(-119.93, 241.12) * mm});
            skLineSegment(sketch, "E13.0.13.1", {"start": v(-119.93, 225.72) * mm, "end": v(-104.53, 225.72) * mm});
            skLineSegment(sketch, "E13.0.13.2", {"start": v(-104.53, 225.72) * mm, "end": v(-104.53, 241.12) * mm});
            skLineSegment(sketch, "E13.0.13.3", {"start": v(-119.93, 241.12) * mm, "end": v(-104.53, 241.12) * mm});
            skLineSegment(sketch, "E13.0.14.0", {"start": v(-119.93, 242.32) * mm, "end": v(-119.93, 257.72) * mm});
            skLineSegment(sketch, "E13.0.14.1", {"start": v(-119.93, 242.32) * mm, "end": v(-104.53, 242.32) * mm});
            skLineSegment(sketch, "E13.0.14.2", {"start": v(-104.53, 242.32) * mm, "end": v(-104.53, 257.72) * mm});
            skLineSegment(sketch, "E13.0.14.3", {"start": v(-119.93, 257.72) * mm, "end": v(-104.53, 257.72) * mm});
            skLineSegment(sketch, "E13.0.15.0", {"start": v(-119.93, 258.92) * mm, "end": v(-119.93, 274.32) * mm});
            skLineSegment(sketch, "E13.0.15.1", {"start": v(-119.93, 258.92) * mm, "end": v(-104.53, 258.92) * mm});
            skLineSegment(sketch, "E13.0.15.2", {"start": v(-104.53, 258.92) * mm, "end": v(-104.53, 274.32) * mm});
            skLineSegment(sketch, "E13.0.15.3", {"start": v(-119.93, 274.32) * mm, "end": v(-104.53, 274.32) * mm});
            skLineSegment(sketch, "E13.1.0.0", {"start": v(-103.33, 9.92) * mm, "end": v(-103.33, 25.32) * mm});
            skLineSegment(sketch, "E13.1.0.1", {"start": v(-103.33, 9.92) * mm, "end": v(-87.93, 9.92) * mm});
            skLineSegment(sketch, "E13.1.0.2", {"start": v(-87.93, 9.92) * mm, "end": v(-87.93, 25.32) * mm});
            skLineSegment(sketch, "E13.1.0.3", {"start": v(-103.33, 25.32) * mm, "end": v(-87.93, 25.32) * mm});
            skLineSegment(sketch, "E13.1.1.0", {"start": v(-103.33, 26.52) * mm, "end": v(-103.33, 41.92) * mm});
            skLineSegment(sketch, "E13.1.1.1", {"start": v(-103.33, 26.52) * mm, "end": v(-87.93, 26.52) * mm});
            skLineSegment(sketch, "E13.1.1.2", {"start": v(-87.93, 26.52) * mm, "end": v(-87.93, 41.92) * mm});
            skLineSegment(sketch, "E13.1.1.3", {"start": v(-103.33, 41.92) * mm, "end": v(-87.93, 41.92) * mm});
            skLineSegment(sketch, "E13.1.2.0", {"start": v(-103.33, 43.12) * mm, "end": v(-103.33, 58.52) * mm});
            skLineSegment(sketch, "E13.1.2.1", {"start": v(-103.33, 43.12) * mm, "end": v(-87.93, 43.12) * mm});
            skLineSegment(sketch, "E13.1.2.2", {"start": v(-87.93, 43.12) * mm, "end": v(-87.93, 58.52) * mm});
            skLineSegment(sketch, "E13.1.2.3", {"start": v(-103.33, 58.52) * mm, "end": v(-87.93, 58.52) * mm});
            skLineSegment(sketch, "E13.1.3.0", {"start": v(-103.33, 59.72) * mm, "end": v(-103.33, 75.12) * mm});
            skLineSegment(sketch, "E13.1.3.1", {"start": v(-103.33, 59.72) * mm, "end": v(-87.93, 59.72) * mm});
            skLineSegment(sketch, "E13.1.3.2", {"start": v(-87.93, 59.72) * mm, "end": v(-87.93, 75.12) * mm});
            skLineSegment(sketch, "E13.1.3.3", {"start": v(-103.33, 75.12) * mm, "end": v(-87.93, 75.12) * mm});
            skLineSegment(sketch, "E13.1.4.0", {"start": v(-103.33, 76.32) * mm, "end": v(-103.33, 91.72) * mm});
            skLineSegment(sketch, "E13.1.4.1", {"start": v(-103.33, 76.32) * mm, "end": v(-87.93, 76.32) * mm});
            skLineSegment(sketch, "E13.1.4.2", {"start": v(-87.93, 76.32) * mm, "end": v(-87.93, 91.72) * mm});
            skLineSegment(sketch, "E13.1.4.3", {"start": v(-103.33, 91.72) * mm, "end": v(-87.93, 91.72) * mm});
            skLineSegment(sketch, "E13.1.5.0", {"start": v(-103.33, 92.92) * mm, "end": v(-103.33, 108.32) * mm});
            skLineSegment(sketch, "E13.1.5.1", {"start": v(-103.33, 92.92) * mm, "end": v(-87.93, 92.92) * mm});
            skLineSegment(sketch, "E13.1.5.2", {"start": v(-87.93, 92.92) * mm, "end": v(-87.93, 108.32) * mm});
            skLineSegment(sketch, "E13.1.5.3", {"start": v(-103.33, 108.32) * mm, "end": v(-87.93, 108.32) * mm});
            skLineSegment(sketch, "E13.1.6.0", {"start": v(-103.33, 109.52) * mm, "end": v(-103.33, 124.92) * mm});
            skLineSegment(sketch, "E13.1.6.1", {"start": v(-103.33, 109.52) * mm, "end": v(-87.93, 109.52) * mm});
            skLineSegment(sketch, "E13.1.6.2", {"start": v(-87.93, 109.52) * mm, "end": v(-87.93, 124.92) * mm});
            skLineSegment(sketch, "E13.1.6.3", {"start": v(-103.33, 124.92) * mm, "end": v(-87.93, 124.92) * mm});
            skLineSegment(sketch, "E13.1.7.0", {"start": v(-103.33, 126.12) * mm, "end": v(-103.33, 141.52) * mm});
            skLineSegment(sketch, "E13.1.7.1", {"start": v(-103.33, 126.12) * mm, "end": v(-87.93, 126.12) * mm});
            skLineSegment(sketch, "E13.1.7.2", {"start": v(-87.93, 126.12) * mm, "end": v(-87.93, 141.52) * mm});
            skLineSegment(sketch, "E13.1.7.3", {"start": v(-103.33, 141.52) * mm, "end": v(-87.93, 141.52) * mm});
            skLineSegment(sketch, "E13.1.8.0", {"start": v(-103.33, 142.72) * mm, "end": v(-103.33, 158.12) * mm});
            skLineSegment(sketch, "E13.1.8.1", {"start": v(-103.33, 142.72) * mm, "end": v(-87.93, 142.72) * mm});
            skLineSegment(sketch, "E13.1.8.2", {"start": v(-87.93, 142.72) * mm, "end": v(-87.93, 158.12) * mm});
            skLineSegment(sketch, "E13.1.8.3", {"start": v(-103.33, 158.12) * mm, "end": v(-87.93, 158.12) * mm});
            skLineSegment(sketch, "E13.1.9.0", {"start": v(-103.33, 159.32) * mm, "end": v(-103.33, 174.72) * mm});
            skLineSegment(sketch, "E13.1.9.1", {"start": v(-103.33, 159.32) * mm, "end": v(-87.93, 159.32) * mm});
            skLineSegment(sketch, "E13.1.9.2", {"start": v(-87.93, 159.32) * mm, "end": v(-87.93, 174.72) * mm});
            skLineSegment(sketch, "E13.1.9.3", {"start": v(-103.33, 174.72) * mm, "end": v(-87.93, 174.72) * mm});
            skLineSegment(sketch, "E13.1.10.0", {"start": v(-103.33, 175.92) * mm, "end": v(-103.33, 191.32) * mm});
            skLineSegment(sketch, "E13.1.10.1", {"start": v(-103.33, 175.92) * mm, "end": v(-87.93, 175.92) * mm});
            skLineSegment(sketch, "E13.1.10.2", {"start": v(-87.93, 175.92) * mm, "end": v(-87.93, 191.32) * mm});
            skLineSegment(sketch, "E13.1.10.3", {"start": v(-103.33, 191.32) * mm, "end": v(-87.93, 191.32) * mm});
            skLineSegment(sketch, "E13.1.11.0", {"start": v(-103.33, 192.52) * mm, "end": v(-103.33, 207.92) * mm});
            skLineSegment(sketch, "E13.1.11.1", {"start": v(-103.33, 192.52) * mm, "end": v(-87.93, 192.52) * mm});
            skLineSegment(sketch, "E13.1.11.2", {"start": v(-87.93, 192.52) * mm, "end": v(-87.93, 207.92) * mm});
            skLineSegment(sketch, "E13.1.11.3", {"start": v(-103.33, 207.92) * mm, "end": v(-87.93, 207.92) * mm});
            skLineSegment(sketch, "E13.1.12.0", {"start": v(-103.33, 209.12) * mm, "end": v(-103.33, 224.52) * mm});
            skLineSegment(sketch, "E13.1.12.1", {"start": v(-103.33, 209.12) * mm, "end": v(-87.93, 209.12) * mm});
            skLineSegment(sketch, "E13.1.12.2", {"start": v(-87.93, 209.12) * mm, "end": v(-87.93, 224.52) * mm});
            skLineSegment(sketch, "E13.1.12.3", {"start": v(-103.33, 224.52) * mm, "end": v(-87.93, 224.52) * mm});
            skLineSegment(sketch, "E13.1.13.0", {"start": v(-103.33, 225.72) * mm, "end": v(-103.33, 241.12) * mm});
            skLineSegment(sketch, "E13.1.13.1", {"start": v(-103.33, 225.72) * mm, "end": v(-87.93, 225.72) * mm});
            skLineSegment(sketch, "E13.1.13.2", {"start": v(-87.93, 225.72) * mm, "end": v(-87.93, 241.12) * mm});
            skLineSegment(sketch, "E13.1.13.3", {"start": v(-103.33, 241.12) * mm, "end": v(-87.93, 241.12) * mm});
            skLineSegment(sketch, "E13.1.14.0", {"start": v(-103.33, 242.32) * mm, "end": v(-103.33, 257.72) * mm});
            skLineSegment(sketch, "E13.1.14.1", {"start": v(-103.33, 242.32) * mm, "end": v(-87.93, 242.32) * mm});
            skLineSegment(sketch, "E13.1.14.2", {"start": v(-87.93, 242.32) * mm, "end": v(-87.93, 257.72) * mm});
            skLineSegment(sketch, "E13.1.14.3", {"start": v(-103.33, 257.72) * mm, "end": v(-87.93, 257.72) * mm});
            skLineSegment(sketch, "E13.1.15.0", {"start": v(-103.33, 258.92) * mm, "end": v(-103.33, 274.32) * mm});
            skLineSegment(sketch, "E13.1.15.1", {"start": v(-103.33, 258.92) * mm, "end": v(-87.93, 258.92) * mm});
            skLineSegment(sketch, "E13.1.15.2", {"start": v(-87.93, 258.92) * mm, "end": v(-87.93, 274.32) * mm});
            skLineSegment(sketch, "E13.1.15.3", {"start": v(-103.33, 274.32) * mm, "end": v(-87.93, 274.32) * mm});
            skLineSegment(sketch, "E13.2.0.0", {"start": v(-86.73, 9.92) * mm, "end": v(-86.73, 25.32) * mm});
            skLineSegment(sketch, "E13.2.0.1", {"start": v(-86.73, 9.92) * mm, "end": v(-71.33, 9.92) * mm});
            skLineSegment(sketch, "E13.2.0.2", {"start": v(-71.33, 9.92) * mm, "end": v(-71.33, 25.32) * mm});
            skLineSegment(sketch, "E13.2.0.3", {"start": v(-86.73, 25.32) * mm, "end": v(-71.33, 25.32) * mm});
            skLineSegment(sketch, "E13.2.1.0", {"start": v(-86.73, 26.52) * mm, "end": v(-86.73, 41.92) * mm});
            skLineSegment(sketch, "E13.2.1.1", {"start": v(-86.73, 26.52) * mm, "end": v(-71.33, 26.52) * mm});
            skLineSegment(sketch, "E13.2.1.2", {"start": v(-71.33, 26.52) * mm, "end": v(-71.33, 41.92) * mm});
            skLineSegment(sketch, "E13.2.1.3", {"start": v(-86.73, 41.92) * mm, "end": v(-71.33, 41.92) * mm});
            skLineSegment(sketch, "E13.2.2.0", {"start": v(-86.73, 43.12) * mm, "end": v(-86.73, 58.52) * mm});
            skLineSegment(sketch, "E13.2.2.1", {"start": v(-86.73, 43.12) * mm, "end": v(-71.33, 43.12) * mm});
            skLineSegment(sketch, "E13.2.2.2", {"start": v(-71.33, 43.12) * mm, "end": v(-71.33, 58.52) * mm});
            skLineSegment(sketch, "E13.2.2.3", {"start": v(-86.73, 58.52) * mm, "end": v(-71.33, 58.52) * mm});
            skLineSegment(sketch, "E13.2.3.0", {"start": v(-86.73, 59.72) * mm, "end": v(-86.73, 75.12) * mm});
            skLineSegment(sketch, "E13.2.3.1", {"start": v(-86.73, 59.72) * mm, "end": v(-71.33, 59.72) * mm});
            skLineSegment(sketch, "E13.2.3.2", {"start": v(-71.33, 59.72) * mm, "end": v(-71.33, 75.12) * mm});
            skLineSegment(sketch, "E13.2.3.3", {"start": v(-86.73, 75.12) * mm, "end": v(-71.33, 75.12) * mm});
            skLineSegment(sketch, "E13.2.4.0", {"start": v(-86.73, 76.32) * mm, "end": v(-86.73, 91.72) * mm});
            skLineSegment(sketch, "E13.2.4.1", {"start": v(-86.73, 76.32) * mm, "end": v(-71.33, 76.32) * mm});
            skLineSegment(sketch, "E13.2.4.2", {"start": v(-71.33, 76.32) * mm, "end": v(-71.33, 91.72) * mm});
            skLineSegment(sketch, "E13.2.4.3", {"start": v(-86.73, 91.72) * mm, "end": v(-71.33, 91.72) * mm});
            skLineSegment(sketch, "E13.2.5.0", {"start": v(-86.73, 92.92) * mm, "end": v(-86.73, 108.32) * mm});
            skLineSegment(sketch, "E13.2.5.1", {"start": v(-86.73, 92.92) * mm, "end": v(-71.33, 92.92) * mm});
            skLineSegment(sketch, "E13.2.5.2", {"start": v(-71.33, 92.92) * mm, "end": v(-71.33, 108.32) * mm});
            skLineSegment(sketch, "E13.2.5.3", {"start": v(-86.73, 108.32) * mm, "end": v(-71.33, 108.32) * mm});
            skLineSegment(sketch, "E13.2.6.0", {"start": v(-86.73, 109.52) * mm, "end": v(-86.73, 124.92) * mm});
            skLineSegment(sketch, "E13.2.6.1", {"start": v(-86.73, 109.52) * mm, "end": v(-71.33, 109.52) * mm});
            skLineSegment(sketch, "E13.2.6.2", {"start": v(-71.33, 109.52) * mm, "end": v(-71.33, 124.92) * mm});
            skLineSegment(sketch, "E13.2.6.3", {"start": v(-86.73, 124.92) * mm, "end": v(-71.33, 124.92) * mm});
            skLineSegment(sketch, "E13.2.7.0", {"start": v(-86.73, 126.12) * mm, "end": v(-86.73, 141.52) * mm});
            skLineSegment(sketch, "E13.2.7.1", {"start": v(-86.73, 126.12) * mm, "end": v(-71.33, 126.12) * mm});
            skLineSegment(sketch, "E13.2.7.2", {"start": v(-71.33, 126.12) * mm, "end": v(-71.33, 141.52) * mm});
            skLineSegment(sketch, "E13.2.7.3", {"start": v(-86.73, 141.52) * mm, "end": v(-71.33, 141.52) * mm});
            skLineSegment(sketch, "E13.2.8.0", {"start": v(-86.73, 142.72) * mm, "end": v(-86.73, 158.12) * mm});
            skLineSegment(sketch, "E13.2.8.1", {"start": v(-86.73, 142.72) * mm, "end": v(-71.33, 142.72) * mm});
            skLineSegment(sketch, "E13.2.8.2", {"start": v(-71.33, 142.72) * mm, "end": v(-71.33, 158.12) * mm});
            skLineSegment(sketch, "E13.2.8.3", {"start": v(-86.73, 158.12) * mm, "end": v(-71.33, 158.12) * mm});
            skLineSegment(sketch, "E13.2.9.0", {"start": v(-86.73, 159.32) * mm, "end": v(-86.73, 174.72) * mm});
            skLineSegment(sketch, "E13.2.9.1", {"start": v(-86.73, 159.32) * mm, "end": v(-71.33, 159.32) * mm});
            skLineSegment(sketch, "E13.2.9.2", {"start": v(-71.33, 159.32) * mm, "end": v(-71.33, 174.72) * mm});
            skLineSegment(sketch, "E13.2.9.3", {"start": v(-86.73, 174.72) * mm, "end": v(-71.33, 174.72) * mm});
            skLineSegment(sketch, "E13.2.10.0", {"start": v(-86.73, 175.92) * mm, "end": v(-86.73, 191.32) * mm});
            skLineSegment(sketch, "E13.2.10.1", {"start": v(-86.73, 175.92) * mm, "end": v(-71.33, 175.92) * mm});
            skLineSegment(sketch, "E13.2.10.2", {"start": v(-71.33, 175.92) * mm, "end": v(-71.33, 191.32) * mm});
            skLineSegment(sketch, "E13.2.10.3", {"start": v(-86.73, 191.32) * mm, "end": v(-71.33, 191.32) * mm});
            skLineSegment(sketch, "E13.2.11.0", {"start": v(-86.73, 192.52) * mm, "end": v(-86.73, 207.92) * mm});
            skLineSegment(sketch, "E13.2.11.1", {"start": v(-86.73, 192.52) * mm, "end": v(-71.33, 192.52) * mm});
            skLineSegment(sketch, "E13.2.11.2", {"start": v(-71.33, 192.52) * mm, "end": v(-71.33, 207.92) * mm});
            skLineSegment(sketch, "E13.2.11.3", {"start": v(-86.73, 207.92) * mm, "end": v(-71.33, 207.92) * mm});
            skLineSegment(sketch, "E13.2.12.0", {"start": v(-86.73, 209.12) * mm, "end": v(-86.73, 224.52) * mm});
            skLineSegment(sketch, "E13.2.12.1", {"start": v(-86.73, 209.12) * mm, "end": v(-71.33, 209.12) * mm});
            skLineSegment(sketch, "E13.2.12.2", {"start": v(-71.33, 209.12) * mm, "end": v(-71.33, 224.52) * mm});
            skLineSegment(sketch, "E13.2.12.3", {"start": v(-86.73, 224.52) * mm, "end": v(-71.33, 224.52) * mm});
            skLineSegment(sketch, "E13.2.13.0", {"start": v(-86.73, 225.72) * mm, "end": v(-86.73, 241.12) * mm});
            skLineSegment(sketch, "E13.2.13.1", {"start": v(-86.73, 225.72) * mm, "end": v(-71.33, 225.72) * mm});
            skLineSegment(sketch, "E13.2.13.2", {"start": v(-71.33, 225.72) * mm, "end": v(-71.33, 241.12) * mm});
            skLineSegment(sketch, "E13.2.13.3", {"start": v(-86.73, 241.12) * mm, "end": v(-71.33, 241.12) * mm});
            skLineSegment(sketch, "E13.2.14.0", {"start": v(-86.73, 242.32) * mm, "end": v(-86.73, 257.72) * mm});
            skLineSegment(sketch, "E13.2.14.1", {"start": v(-86.73, 242.32) * mm, "end": v(-71.33, 242.32) * mm});
            skLineSegment(sketch, "E13.2.14.2", {"start": v(-71.33, 242.32) * mm, "end": v(-71.33, 257.72) * mm});
            skLineSegment(sketch, "E13.2.14.3", {"start": v(-86.73, 257.72) * mm, "end": v(-71.33, 257.72) * mm});
            skLineSegment(sketch, "E13.2.15.0", {"start": v(-86.73, 258.92) * mm, "end": v(-86.73, 274.32) * mm});
            skLineSegment(sketch, "E13.2.15.1", {"start": v(-86.73, 258.92) * mm, "end": v(-71.33, 258.92) * mm});
            skLineSegment(sketch, "E13.2.15.2", {"start": v(-71.33, 258.92) * mm, "end": v(-71.33, 274.32) * mm});
            skLineSegment(sketch, "E13.2.15.3", {"start": v(-86.73, 274.32) * mm, "end": v(-71.33, 274.32) * mm});
            skLineSegment(sketch, "E13.3.0.0", {"start": v(-70.13, 9.92) * mm, "end": v(-70.13, 25.32) * mm});
            skLineSegment(sketch, "E13.3.0.1", {"start": v(-70.13, 9.92) * mm, "end": v(-54.73, 9.92) * mm});
            skLineSegment(sketch, "E13.3.0.2", {"start": v(-54.73, 9.92) * mm, "end": v(-54.73, 25.32) * mm});
            skLineSegment(sketch, "E13.3.0.3", {"start": v(-70.13, 25.32) * mm, "end": v(-54.73, 25.32) * mm});
            skLineSegment(sketch, "E13.3.1.0", {"start": v(-70.13, 26.52) * mm, "end": v(-70.13, 41.92) * mm});
            skLineSegment(sketch, "E13.3.1.1", {"start": v(-70.13, 26.52) * mm, "end": v(-54.73, 26.52) * mm});
            skLineSegment(sketch, "E13.3.1.2", {"start": v(-54.73, 26.52) * mm, "end": v(-54.73, 41.92) * mm});
            skLineSegment(sketch, "E13.3.1.3", {"start": v(-70.13, 41.92) * mm, "end": v(-54.73, 41.92) * mm});
            skLineSegment(sketch, "E13.3.2.0", {"start": v(-70.13, 43.12) * mm, "end": v(-70.13, 58.52) * mm});
            skLineSegment(sketch, "E13.3.2.1", {"start": v(-70.13, 43.12) * mm, "end": v(-54.73, 43.12) * mm});
            skLineSegment(sketch, "E13.3.2.2", {"start": v(-54.73, 43.12) * mm, "end": v(-54.73, 58.52) * mm});
            skLineSegment(sketch, "E13.3.2.3", {"start": v(-70.13, 58.52) * mm, "end": v(-54.73, 58.52) * mm});
            skLineSegment(sketch, "E13.3.3.0", {"start": v(-70.13, 59.72) * mm, "end": v(-70.13, 75.12) * mm});
            skLineSegment(sketch, "E13.3.3.1", {"start": v(-70.13, 59.72) * mm, "end": v(-54.73, 59.72) * mm});
            skLineSegment(sketch, "E13.3.3.2", {"start": v(-54.73, 59.72) * mm, "end": v(-54.73, 75.12) * mm});
            skLineSegment(sketch, "E13.3.3.3", {"start": v(-70.13, 75.12) * mm, "end": v(-54.73, 75.12) * mm});
            skLineSegment(sketch, "E13.3.4.0", {"start": v(-70.13, 76.32) * mm, "end": v(-70.13, 91.72) * mm});
            skLineSegment(sketch, "E13.3.4.1", {"start": v(-70.13, 76.32) * mm, "end": v(-54.73, 76.32) * mm});
            skLineSegment(sketch, "E13.3.4.2", {"start": v(-54.73, 76.32) * mm, "end": v(-54.73, 91.72) * mm});
            skLineSegment(sketch, "E13.3.4.3", {"start": v(-70.13, 91.72) * mm, "end": v(-54.73, 91.72) * mm});
            skLineSegment(sketch, "E13.3.5.0", {"start": v(-70.13, 92.92) * mm, "end": v(-70.13, 108.32) * mm});
            skLineSegment(sketch, "E13.3.5.1", {"start": v(-70.13, 92.92) * mm, "end": v(-54.73, 92.92) * mm});
            skLineSegment(sketch, "E13.3.5.2", {"start": v(-54.73, 92.92) * mm, "end": v(-54.73, 108.32) * mm});
            skLineSegment(sketch, "E13.3.5.3", {"start": v(-70.13, 108.32) * mm, "end": v(-54.73, 108.32) * mm});
            skLineSegment(sketch, "E13.3.6.0", {"start": v(-70.13, 109.52) * mm, "end": v(-70.13, 124.92) * mm});
            skLineSegment(sketch, "E13.3.6.1", {"start": v(-70.13, 109.52) * mm, "end": v(-54.73, 109.52) * mm});
            skLineSegment(sketch, "E13.3.6.2", {"start": v(-54.73, 109.52) * mm, "end": v(-54.73, 124.92) * mm});
            skLineSegment(sketch, "E13.3.6.3", {"start": v(-70.13, 124.92) * mm, "end": v(-54.73, 124.92) * mm});
            skLineSegment(sketch, "E13.3.7.0", {"start": v(-70.13, 126.12) * mm, "end": v(-70.13, 141.52) * mm});
            skLineSegment(sketch, "E13.3.7.1", {"start": v(-70.13, 126.12) * mm, "end": v(-54.73, 126.12) * mm});
            skLineSegment(sketch, "E13.3.7.2", {"start": v(-54.73, 126.12) * mm, "end": v(-54.73, 141.52) * mm});
            skLineSegment(sketch, "E13.3.7.3", {"start": v(-70.13, 141.52) * mm, "end": v(-54.73, 141.52) * mm});
            skLineSegment(sketch, "E13.3.8.0", {"start": v(-70.13, 142.72) * mm, "end": v(-70.13, 158.12) * mm});
            skLineSegment(sketch, "E13.3.8.1", {"start": v(-70.13, 142.72) * mm, "end": v(-54.73, 142.72) * mm});
            skLineSegment(sketch, "E13.3.8.2", {"start": v(-54.73, 142.72) * mm, "end": v(-54.73, 158.12) * mm});
            skLineSegment(sketch, "E13.3.8.3", {"start": v(-70.13, 158.12) * mm, "end": v(-54.73, 158.12) * mm});
            skLineSegment(sketch, "E13.3.9.0", {"start": v(-70.13, 159.32) * mm, "end": v(-70.13, 174.72) * mm});
            skLineSegment(sketch, "E13.3.9.1", {"start": v(-70.13, 159.32) * mm, "end": v(-54.73, 159.32) * mm});
            skLineSegment(sketch, "E13.3.9.2", {"start": v(-54.73, 159.32) * mm, "end": v(-54.73, 174.72) * mm});
            skLineSegment(sketch, "E13.3.9.3", {"start": v(-70.13, 174.72) * mm, "end": v(-54.73, 174.72) * mm});
            skLineSegment(sketch, "E13.3.10.0", {"start": v(-70.13, 175.92) * mm, "end": v(-70.13, 191.32) * mm});
            skLineSegment(sketch, "E13.3.10.1", {"start": v(-70.13, 175.92) * mm, "end": v(-54.73, 175.92) * mm});
            skLineSegment(sketch, "E13.3.10.2", {"start": v(-54.73, 175.92) * mm, "end": v(-54.73, 191.32) * mm});
            skLineSegment(sketch, "E13.3.10.3", {"start": v(-70.13, 191.32) * mm, "end": v(-54.73, 191.32) * mm});
            skLineSegment(sketch, "E13.3.11.0", {"start": v(-70.13, 192.52) * mm, "end": v(-70.13, 207.92) * mm});
            skLineSegment(sketch, "E13.3.11.1", {"start": v(-70.13, 192.52) * mm, "end": v(-54.73, 192.52) * mm});
            skLineSegment(sketch, "E13.3.11.2", {"start": v(-54.73, 192.52) * mm, "end": v(-54.73, 207.92) * mm});
            skLineSegment(sketch, "E13.3.11.3", {"start": v(-70.13, 207.92) * mm, "end": v(-54.73, 207.92) * mm});
            skLineSegment(sketch, "E13.3.12.0", {"start": v(-70.13, 209.12) * mm, "end": v(-70.13, 224.52) * mm});
            skLineSegment(sketch, "E13.3.12.1", {"start": v(-70.13, 209.12) * mm, "end": v(-54.73, 209.12) * mm});
            skLineSegment(sketch, "E13.3.12.2", {"start": v(-54.73, 209.12) * mm, "end": v(-54.73, 224.52) * mm});
            skLineSegment(sketch, "E13.3.12.3", {"start": v(-70.13, 224.52) * mm, "end": v(-54.73, 224.52) * mm});
            skLineSegment(sketch, "E13.3.13.0", {"start": v(-70.13, 225.72) * mm, "end": v(-70.13, 241.12) * mm});
            skLineSegment(sketch, "E13.3.13.1", {"start": v(-70.13, 225.72) * mm, "end": v(-54.73, 225.72) * mm});
            skLineSegment(sketch, "E13.3.13.2", {"start": v(-54.73, 225.72) * mm, "end": v(-54.73, 241.12) * mm});
            skLineSegment(sketch, "E13.3.13.3", {"start": v(-70.13, 241.12) * mm, "end": v(-54.73, 241.12) * mm});
            skLineSegment(sketch, "E13.3.14.0", {"start": v(-70.13, 242.32) * mm, "end": v(-70.13, 257.72) * mm});
            skLineSegment(sketch, "E13.3.14.1", {"start": v(-70.13, 242.32) * mm, "end": v(-54.73, 242.32) * mm});
            skLineSegment(sketch, "E13.3.14.2", {"start": v(-54.73, 242.32) * mm, "end": v(-54.73, 257.72) * mm});
            skLineSegment(sketch, "E13.3.14.3", {"start": v(-70.13, 257.72) * mm, "end": v(-54.73, 257.72) * mm});
            skLineSegment(sketch, "E13.3.15.0", {"start": v(-70.13, 258.92) * mm, "end": v(-70.13, 274.32) * mm});
            skLineSegment(sketch, "E13.3.15.1", {"start": v(-70.13, 258.92) * mm, "end": v(-54.73, 258.92) * mm});
            skLineSegment(sketch, "E13.3.15.2", {"start": v(-54.73, 258.92) * mm, "end": v(-54.73, 274.32) * mm});
            skLineSegment(sketch, "E13.3.15.3", {"start": v(-70.13, 274.32) * mm, "end": v(-54.73, 274.32) * mm});
            skLineSegment(sketch, "E13.4.0.0", {"start": v(-53.53, 9.92) * mm, "end": v(-53.53, 25.32) * mm});
            skLineSegment(sketch, "E13.4.0.1", {"start": v(-53.53, 9.92) * mm, "end": v(-38.13, 9.92) * mm});
            skLineSegment(sketch, "E13.4.0.2", {"start": v(-38.13, 9.92) * mm, "end": v(-38.13, 25.32) * mm});
            skLineSegment(sketch, "E13.4.0.3", {"start": v(-53.53, 25.32) * mm, "end": v(-38.13, 25.32) * mm});
            skLineSegment(sketch, "E13.4.1.0", {"start": v(-53.53, 26.52) * mm, "end": v(-53.53, 41.92) * mm});
            skLineSegment(sketch, "E13.4.1.1", {"start": v(-53.53, 26.52) * mm, "end": v(-38.13, 26.52) * mm});
            skLineSegment(sketch, "E13.4.1.2", {"start": v(-38.13, 26.52) * mm, "end": v(-38.13, 41.92) * mm});
            skLineSegment(sketch, "E13.4.1.3", {"start": v(-53.53, 41.92) * mm, "end": v(-38.13, 41.92) * mm});
            skLineSegment(sketch, "E13.4.2.0", {"start": v(-53.53, 43.12) * mm, "end": v(-53.53, 58.52) * mm});
            skLineSegment(sketch, "E13.4.2.1", {"start": v(-53.53, 43.12) * mm, "end": v(-38.13, 43.12) * mm});
            skLineSegment(sketch, "E13.4.2.2", {"start": v(-38.13, 43.12) * mm, "end": v(-38.13, 58.52) * mm});
            skLineSegment(sketch, "E13.4.2.3", {"start": v(-53.53, 58.52) * mm, "end": v(-38.13, 58.52) * mm});
            skLineSegment(sketch, "E13.4.3.0", {"start": v(-53.53, 59.72) * mm, "end": v(-53.53, 75.12) * mm});
            skLineSegment(sketch, "E13.4.3.1", {"start": v(-53.53, 59.72) * mm, "end": v(-38.13, 59.72) * mm});
            skLineSegment(sketch, "E13.4.3.2", {"start": v(-38.13, 59.72) * mm, "end": v(-38.13, 75.12) * mm});
            skLineSegment(sketch, "E13.4.3.3", {"start": v(-53.53, 75.12) * mm, "end": v(-38.13, 75.12) * mm});
            skLineSegment(sketch, "E13.4.4.0", {"start": v(-53.53, 76.32) * mm, "end": v(-53.53, 91.72) * mm});
            skLineSegment(sketch, "E13.4.4.1", {"start": v(-53.53, 76.32) * mm, "end": v(-38.13, 76.32) * mm});
            skLineSegment(sketch, "E13.4.4.2", {"start": v(-38.13, 76.32) * mm, "end": v(-38.13, 91.72) * mm});
            skLineSegment(sketch, "E13.4.4.3", {"start": v(-53.53, 91.72) * mm, "end": v(-38.13, 91.72) * mm});
            skLineSegment(sketch, "E13.4.5.0", {"start": v(-53.53, 92.92) * mm, "end": v(-53.53, 108.32) * mm});
            skLineSegment(sketch, "E13.4.5.1", {"start": v(-53.53, 92.92) * mm, "end": v(-38.13, 92.92) * mm});
            skLineSegment(sketch, "E13.4.5.2", {"start": v(-38.13, 92.92) * mm, "end": v(-38.13, 108.32) * mm});
            skLineSegment(sketch, "E13.4.5.3", {"start": v(-53.53, 108.32) * mm, "end": v(-38.13, 108.32) * mm});
            skLineSegment(sketch, "E13.4.6.0", {"start": v(-53.53, 109.52) * mm, "end": v(-53.53, 124.92) * mm});
            skLineSegment(sketch, "E13.4.6.1", {"start": v(-53.53, 109.52) * mm, "end": v(-38.13, 109.52) * mm});
            skLineSegment(sketch, "E13.4.6.2", {"start": v(-38.13, 109.52) * mm, "end": v(-38.13, 124.92) * mm});
            skLineSegment(sketch, "E13.4.6.3", {"start": v(-53.53, 124.92) * mm, "end": v(-38.13, 124.92) * mm});
            skLineSegment(sketch, "E13.4.7.0", {"start": v(-53.53, 126.12) * mm, "end": v(-53.53, 141.52) * mm});
            skLineSegment(sketch, "E13.4.7.1", {"start": v(-53.53, 126.12) * mm, "end": v(-38.13, 126.12) * mm});
            skLineSegment(sketch, "E13.4.7.2", {"start": v(-38.13, 126.12) * mm, "end": v(-38.13, 141.52) * mm});
            skLineSegment(sketch, "E13.4.7.3", {"start": v(-53.53, 141.52) * mm, "end": v(-38.13, 141.52) * mm});
            skLineSegment(sketch, "E13.4.8.0", {"start": v(-53.53, 142.72) * mm, "end": v(-53.53, 158.12) * mm});
            skLineSegment(sketch, "E13.4.8.1", {"start": v(-53.53, 142.72) * mm, "end": v(-38.13, 142.72) * mm});
            skLineSegment(sketch, "E13.4.8.2", {"start": v(-38.13, 142.72) * mm, "end": v(-38.13, 158.12) * mm});
            skLineSegment(sketch, "E13.4.8.3", {"start": v(-53.53, 158.12) * mm, "end": v(-38.13, 158.12) * mm});
            skLineSegment(sketch, "E13.4.9.0", {"start": v(-53.53, 159.32) * mm, "end": v(-53.53, 174.72) * mm});
            skLineSegment(sketch, "E13.4.9.1", {"start": v(-53.53, 159.32) * mm, "end": v(-38.13, 159.32) * mm});
            skLineSegment(sketch, "E13.4.9.2", {"start": v(-38.13, 159.32) * mm, "end": v(-38.13, 174.72) * mm});
            skLineSegment(sketch, "E13.4.9.3", {"start": v(-53.53, 174.72) * mm, "end": v(-38.13, 174.72) * mm});
            skLineSegment(sketch, "E13.4.10.0", {"start": v(-53.53, 175.92) * mm, "end": v(-53.53, 191.32) * mm});
            skLineSegment(sketch, "E13.4.10.1", {"start": v(-53.53, 175.92) * mm, "end": v(-38.13, 175.92) * mm});
            skLineSegment(sketch, "E13.4.10.2", {"start": v(-38.13, 175.92) * mm, "end": v(-38.13, 191.32) * mm});
            skLineSegment(sketch, "E13.4.10.3", {"start": v(-53.53, 191.32) * mm, "end": v(-38.13, 191.32) * mm});
            skLineSegment(sketch, "E13.4.11.0", {"start": v(-53.53, 192.52) * mm, "end": v(-53.53, 207.92) * mm});
            skLineSegment(sketch, "E13.4.11.1", {"start": v(-53.53, 192.52) * mm, "end": v(-38.13, 192.52) * mm});
            skLineSegment(sketch, "E13.4.11.2", {"start": v(-38.13, 192.52) * mm, "end": v(-38.13, 207.92) * mm});
            skLineSegment(sketch, "E13.4.11.3", {"start": v(-53.53, 207.92) * mm, "end": v(-38.13, 207.92) * mm});
            skLineSegment(sketch, "E13.4.12.0", {"start": v(-53.53, 209.12) * mm, "end": v(-53.53, 224.52) * mm});
            skLineSegment(sketch, "E13.4.12.1", {"start": v(-53.53, 209.12) * mm, "end": v(-38.13, 209.12) * mm});
            skLineSegment(sketch, "E13.4.12.2", {"start": v(-38.13, 209.12) * mm, "end": v(-38.13, 224.52) * mm});
            skLineSegment(sketch, "E13.4.12.3", {"start": v(-53.53, 224.52) * mm, "end": v(-38.13, 224.52) * mm});
            skLineSegment(sketch, "E13.4.13.0", {"start": v(-53.53, 225.72) * mm, "end": v(-53.53, 241.12) * mm});
            skLineSegment(sketch, "E13.4.13.1", {"start": v(-53.53, 225.72) * mm, "end": v(-38.13, 225.72) * mm});
            skLineSegment(sketch, "E13.4.13.2", {"start": v(-38.13, 225.72) * mm, "end": v(-38.13, 241.12) * mm});
            skLineSegment(sketch, "E13.4.13.3", {"start": v(-53.53, 241.12) * mm, "end": v(-38.13, 241.12) * mm});
            skLineSegment(sketch, "E13.4.14.0", {"start": v(-53.53, 242.32) * mm, "end": v(-53.53, 257.72) * mm});
            skLineSegment(sketch, "E13.4.14.1", {"start": v(-53.53, 242.32) * mm, "end": v(-38.13, 242.32) * mm});
            skLineSegment(sketch, "E13.4.14.2", {"start": v(-38.13, 242.32) * mm, "end": v(-38.13, 257.72) * mm});
            skLineSegment(sketch, "E13.4.14.3", {"start": v(-53.53, 257.72) * mm, "end": v(-38.13, 257.72) * mm});
            skLineSegment(sketch, "E13.4.15.0", {"start": v(-53.53, 258.92) * mm, "end": v(-53.53, 274.32) * mm});
            skLineSegment(sketch, "E13.4.15.1", {"start": v(-53.53, 258.92) * mm, "end": v(-38.13, 258.92) * mm});
            skLineSegment(sketch, "E13.4.15.2", {"start": v(-38.13, 258.92) * mm, "end": v(-38.13, 274.32) * mm});
            skLineSegment(sketch, "E13.4.15.3", {"start": v(-53.53, 274.32) * mm, "end": v(-38.13, 274.32) * mm});
            skLineSegment(sketch, "E13.5.0.0", {"start": v(-36.93, 9.92) * mm, "end": v(-36.93, 25.32) * mm});
            skLineSegment(sketch, "E13.5.0.1", {"start": v(-36.93, 9.92) * mm, "end": v(-21.53, 9.92) * mm});
            skLineSegment(sketch, "E13.5.0.2", {"start": v(-21.53, 9.92) * mm, "end": v(-21.53, 25.32) * mm});
            skLineSegment(sketch, "E13.5.0.3", {"start": v(-36.93, 25.32) * mm, "end": v(-21.53, 25.32) * mm});
            skLineSegment(sketch, "E13.5.1.0", {"start": v(-36.93, 26.52) * mm, "end": v(-36.93, 41.92) * mm});
            skLineSegment(sketch, "E13.5.1.1", {"start": v(-36.93, 26.52) * mm, "end": v(-21.53, 26.52) * mm});
            skLineSegment(sketch, "E13.5.1.2", {"start": v(-21.53, 26.52) * mm, "end": v(-21.53, 41.92) * mm});
            skLineSegment(sketch, "E13.5.1.3", {"start": v(-36.93, 41.92) * mm, "end": v(-21.53, 41.92) * mm});
            skLineSegment(sketch, "E13.5.2.0", {"start": v(-36.93, 43.12) * mm, "end": v(-36.93, 58.52) * mm});
            skLineSegment(sketch, "E13.5.2.1", {"start": v(-36.93, 43.12) * mm, "end": v(-21.53, 43.12) * mm});
            skLineSegment(sketch, "E13.5.2.2", {"start": v(-21.53, 43.12) * mm, "end": v(-21.53, 58.52) * mm});
            skLineSegment(sketch, "E13.5.2.3", {"start": v(-36.93, 58.52) * mm, "end": v(-21.53, 58.52) * mm});
            skLineSegment(sketch, "E13.5.3.0", {"start": v(-36.93, 59.72) * mm, "end": v(-36.93, 75.12) * mm});
            skLineSegment(sketch, "E13.5.3.1", {"start": v(-36.93, 59.72) * mm, "end": v(-21.53, 59.72) * mm});
            skLineSegment(sketch, "E13.5.3.2", {"start": v(-21.53, 59.72) * mm, "end": v(-21.53, 75.12) * mm});
            skLineSegment(sketch, "E13.5.3.3", {"start": v(-36.93, 75.12) * mm, "end": v(-21.53, 75.12) * mm});
            skLineSegment(sketch, "E13.5.4.0", {"start": v(-36.93, 76.32) * mm, "end": v(-36.93, 91.72) * mm});
            skLineSegment(sketch, "E13.5.4.1", {"start": v(-36.93, 76.32) * mm, "end": v(-21.53, 76.32) * mm});
            skLineSegment(sketch, "E13.5.4.2", {"start": v(-21.53, 76.32) * mm, "end": v(-21.53, 91.72) * mm});
            skLineSegment(sketch, "E13.5.4.3", {"start": v(-36.93, 91.72) * mm, "end": v(-21.53, 91.72) * mm});
            skLineSegment(sketch, "E13.5.5.0", {"start": v(-36.93, 92.92) * mm, "end": v(-36.93, 108.32) * mm});
            skLineSegment(sketch, "E13.5.5.1", {"start": v(-36.93, 92.92) * mm, "end": v(-21.53, 92.92) * mm});
            skLineSegment(sketch, "E13.5.5.2", {"start": v(-21.53, 92.92) * mm, "end": v(-21.53, 108.32) * mm});
            skLineSegment(sketch, "E13.5.5.3", {"start": v(-36.93, 108.32) * mm, "end": v(-21.53, 108.32) * mm});
            skLineSegment(sketch, "E13.5.6.0", {"start": v(-36.93, 109.52) * mm, "end": v(-36.93, 124.92) * mm});
            skLineSegment(sketch, "E13.5.6.1", {"start": v(-36.93, 109.52) * mm, "end": v(-21.53, 109.52) * mm});
            skLineSegment(sketch, "E13.5.6.2", {"start": v(-21.53, 109.52) * mm, "end": v(-21.53, 124.92) * mm});
            skLineSegment(sketch, "E13.5.6.3", {"start": v(-36.93, 124.92) * mm, "end": v(-21.53, 124.92) * mm});
            skLineSegment(sketch, "E13.5.7.0", {"start": v(-36.93, 126.12) * mm, "end": v(-36.93, 141.52) * mm});
            skLineSegment(sketch, "E13.5.7.1", {"start": v(-36.93, 126.12) * mm, "end": v(-21.53, 126.12) * mm});
            skLineSegment(sketch, "E13.5.7.2", {"start": v(-21.53, 126.12) * mm, "end": v(-21.53, 141.52) * mm});
            skLineSegment(sketch, "E13.5.7.3", {"start": v(-36.93, 141.52) * mm, "end": v(-21.53, 141.52) * mm});
            skLineSegment(sketch, "E13.5.8.0", {"start": v(-36.93, 142.72) * mm, "end": v(-36.93, 158.12) * mm});
            skLineSegment(sketch, "E13.5.8.1", {"start": v(-36.93, 142.72) * mm, "end": v(-21.53, 142.72) * mm});
            skLineSegment(sketch, "E13.5.8.2", {"start": v(-21.53, 142.72) * mm, "end": v(-21.53, 158.12) * mm});
            skLineSegment(sketch, "E13.5.8.3", {"start": v(-36.93, 158.12) * mm, "end": v(-21.53, 158.12) * mm});
            skLineSegment(sketch, "E13.5.9.0", {"start": v(-36.93, 159.32) * mm, "end": v(-36.93, 174.72) * mm});
            skLineSegment(sketch, "E13.5.9.1", {"start": v(-36.93, 159.32) * mm, "end": v(-21.53, 159.32) * mm});
            skLineSegment(sketch, "E13.5.9.2", {"start": v(-21.53, 159.32) * mm, "end": v(-21.53, 174.72) * mm});
            skLineSegment(sketch, "E13.5.9.3", {"start": v(-36.93, 174.72) * mm, "end": v(-21.53, 174.72) * mm});
            skLineSegment(sketch, "E13.5.10.0", {"start": v(-36.93, 175.92) * mm, "end": v(-36.93, 191.32) * mm});
            skLineSegment(sketch, "E13.5.10.1", {"start": v(-36.93, 175.92) * mm, "end": v(-21.53, 175.92) * mm});
            skLineSegment(sketch, "E13.5.10.2", {"start": v(-21.53, 175.92) * mm, "end": v(-21.53, 191.32) * mm});
            skLineSegment(sketch, "E13.5.10.3", {"start": v(-36.93, 191.32) * mm, "end": v(-21.53, 191.32) * mm});
            skLineSegment(sketch, "E13.5.11.0", {"start": v(-36.93, 192.52) * mm, "end": v(-36.93, 207.92) * mm});
            skLineSegment(sketch, "E13.5.11.1", {"start": v(-36.93, 192.52) * mm, "end": v(-21.53, 192.52) * mm});
            skLineSegment(sketch, "E13.5.11.2", {"start": v(-21.53, 192.52) * mm, "end": v(-21.53, 207.92) * mm});
            skLineSegment(sketch, "E13.5.11.3", {"start": v(-36.93, 207.92) * mm, "end": v(-21.53, 207.92) * mm});
            skLineSegment(sketch, "E13.5.12.0", {"start": v(-36.93, 209.12) * mm, "end": v(-36.93, 224.52) * mm});
            skLineSegment(sketch, "E13.5.12.1", {"start": v(-36.93, 209.12) * mm, "end": v(-21.53, 209.12) * mm});
            skLineSegment(sketch, "E13.5.12.2", {"start": v(-21.53, 209.12) * mm, "end": v(-21.53, 224.52) * mm});
            skLineSegment(sketch, "E13.5.12.3", {"start": v(-36.93, 224.52) * mm, "end": v(-21.53, 224.52) * mm});
            skLineSegment(sketch, "E13.5.13.0", {"start": v(-36.93, 225.72) * mm, "end": v(-36.93, 241.12) * mm});
            skLineSegment(sketch, "E13.5.13.1", {"start": v(-36.93, 225.72) * mm, "end": v(-21.53, 225.72) * mm});
            skLineSegment(sketch, "E13.5.13.2", {"start": v(-21.53, 225.72) * mm, "end": v(-21.53, 241.12) * mm});
            skLineSegment(sketch, "E13.5.13.3", {"start": v(-36.93, 241.12) * mm, "end": v(-21.53, 241.12) * mm});
            skLineSegment(sketch, "E13.5.14.0", {"start": v(-36.93, 242.32) * mm, "end": v(-36.93, 257.72) * mm});
            skLineSegment(sketch, "E13.5.14.1", {"start": v(-36.93, 242.32) * mm, "end": v(-21.53, 242.32) * mm});
            skLineSegment(sketch, "E13.5.14.2", {"start": v(-21.53, 242.32) * mm, "end": v(-21.53, 257.72) * mm});
            skLineSegment(sketch, "E13.5.14.3", {"start": v(-36.93, 257.72) * mm, "end": v(-21.53, 257.72) * mm});
            skLineSegment(sketch, "E13.5.15.0", {"start": v(-36.93, 258.92) * mm, "end": v(-36.93, 274.32) * mm});
            skLineSegment(sketch, "E13.5.15.1", {"start": v(-36.93, 258.92) * mm, "end": v(-21.53, 258.92) * mm});
            skLineSegment(sketch, "E13.5.15.2", {"start": v(-21.53, 258.92) * mm, "end": v(-21.53, 274.32) * mm});
            skLineSegment(sketch, "E13.5.15.3", {"start": v(-36.93, 274.32) * mm, "end": v(-21.53, 274.32) * mm});
            skLineSegment(sketch, "E13.6.0.0", {"start": v(-20.33, 9.92) * mm, "end": v(-20.33, 25.32) * mm});
            skLineSegment(sketch, "E13.6.0.1", {"start": v(-20.33, 9.92) * mm, "end": v(-4.93, 9.92) * mm});
            skLineSegment(sketch, "E13.6.0.2", {"start": v(-4.93, 9.92) * mm, "end": v(-4.93, 25.32) * mm});
            skLineSegment(sketch, "E13.6.0.3", {"start": v(-20.33, 25.32) * mm, "end": v(-4.93, 25.32) * mm});
            skLineSegment(sketch, "E13.6.1.0", {"start": v(-20.33, 26.52) * mm, "end": v(-20.33, 41.92) * mm});
            skLineSegment(sketch, "E13.6.1.1", {"start": v(-20.33, 26.52) * mm, "end": v(-4.93, 26.52) * mm});
            skLineSegment(sketch, "E13.6.1.2", {"start": v(-4.93, 26.52) * mm, "end": v(-4.93, 41.92) * mm});
            skLineSegment(sketch, "E13.6.1.3", {"start": v(-20.33, 41.92) * mm, "end": v(-4.93, 41.92) * mm});
            skLineSegment(sketch, "E13.6.2.0", {"start": v(-20.33, 43.12) * mm, "end": v(-20.33, 58.52) * mm});
            skLineSegment(sketch, "E13.6.2.1", {"start": v(-20.33, 43.12) * mm, "end": v(-4.93, 43.12) * mm});
            skLineSegment(sketch, "E13.6.2.2", {"start": v(-4.93, 43.12) * mm, "end": v(-4.93, 58.52) * mm});
            skLineSegment(sketch, "E13.6.2.3", {"start": v(-20.33, 58.52) * mm, "end": v(-4.93, 58.52) * mm});
            skLineSegment(sketch, "E13.6.3.0", {"start": v(-20.33, 59.72) * mm, "end": v(-20.33, 75.12) * mm});
            skLineSegment(sketch, "E13.6.3.1", {"start": v(-20.33, 59.72) * mm, "end": v(-4.93, 59.72) * mm});
            skLineSegment(sketch, "E13.6.3.2", {"start": v(-4.93, 59.72) * mm, "end": v(-4.93, 75.12) * mm});
            skLineSegment(sketch, "E13.6.3.3", {"start": v(-20.33, 75.12) * mm, "end": v(-4.93, 75.12) * mm});
            skLineSegment(sketch, "E13.6.4.0", {"start": v(-20.33, 76.32) * mm, "end": v(-20.33, 91.72) * mm});
            skLineSegment(sketch, "E13.6.4.1", {"start": v(-20.33, 76.32) * mm, "end": v(-4.93, 76.32) * mm});
            skLineSegment(sketch, "E13.6.4.2", {"start": v(-4.93, 76.32) * mm, "end": v(-4.93, 91.72) * mm});
            skLineSegment(sketch, "E13.6.4.3", {"start": v(-20.33, 91.72) * mm, "end": v(-4.93, 91.72) * mm});
            skLineSegment(sketch, "E13.6.5.0", {"start": v(-20.33, 92.92) * mm, "end": v(-20.33, 108.32) * mm});
            skLineSegment(sketch, "E13.6.5.1", {"start": v(-20.33, 92.92) * mm, "end": v(-4.93, 92.92) * mm});
            skLineSegment(sketch, "E13.6.5.2", {"start": v(-4.93, 92.92) * mm, "end": v(-4.93, 108.32) * mm});
            skLineSegment(sketch, "E13.6.5.3", {"start": v(-20.33, 108.32) * mm, "end": v(-4.93, 108.32) * mm});
            skLineSegment(sketch, "E13.6.6.0", {"start": v(-20.33, 109.52) * mm, "end": v(-20.33, 124.92) * mm});
            skLineSegment(sketch, "E13.6.6.1", {"start": v(-20.33, 109.52) * mm, "end": v(-4.93, 109.52) * mm});
            skLineSegment(sketch, "E13.6.6.2", {"start": v(-4.93, 109.52) * mm, "end": v(-4.93, 124.92) * mm});
            skLineSegment(sketch, "E13.6.6.3", {"start": v(-20.33, 124.92) * mm, "end": v(-4.93, 124.92) * mm});
            skLineSegment(sketch, "E13.6.7.0", {"start": v(-20.33, 126.12) * mm, "end": v(-20.33, 141.52) * mm});
            skLineSegment(sketch, "E13.6.7.1", {"start": v(-20.33, 126.12) * mm, "end": v(-4.93, 126.12) * mm});
            skLineSegment(sketch, "E13.6.7.2", {"start": v(-4.93, 126.12) * mm, "end": v(-4.93, 141.52) * mm});
            skLineSegment(sketch, "E13.6.7.3", {"start": v(-20.33, 141.52) * mm, "end": v(-4.93, 141.52) * mm});
            skLineSegment(sketch, "E13.6.8.0", {"start": v(-20.33, 142.72) * mm, "end": v(-20.33, 158.12) * mm});
            skLineSegment(sketch, "E13.6.8.1", {"start": v(-20.33, 142.72) * mm, "end": v(-4.93, 142.72) * mm});
            skLineSegment(sketch, "E13.6.8.2", {"start": v(-4.93, 142.72) * mm, "end": v(-4.93, 158.12) * mm});
            skLineSegment(sketch, "E13.6.8.3", {"start": v(-20.33, 158.12) * mm, "end": v(-4.93, 158.12) * mm});
            skLineSegment(sketch, "E13.6.9.0", {"start": v(-20.33, 159.32) * mm, "end": v(-20.33, 174.72) * mm});
            skLineSegment(sketch, "E13.6.9.1", {"start": v(-20.33, 159.32) * mm, "end": v(-4.93, 159.32) * mm});
            skLineSegment(sketch, "E13.6.9.2", {"start": v(-4.93, 159.32) * mm, "end": v(-4.93, 174.72) * mm});
            skLineSegment(sketch, "E13.6.9.3", {"start": v(-20.33, 174.72) * mm, "end": v(-4.93, 174.72) * mm});
            skLineSegment(sketch, "E13.6.10.0", {"start": v(-20.33, 175.92) * mm, "end": v(-20.33, 191.32) * mm});
            skLineSegment(sketch, "E13.6.10.1", {"start": v(-20.33, 175.92) * mm, "end": v(-4.93, 175.92) * mm});
            skLineSegment(sketch, "E13.6.10.2", {"start": v(-4.93, 175.92) * mm, "end": v(-4.93, 191.32) * mm});
            skLineSegment(sketch, "E13.6.10.3", {"start": v(-20.33, 191.32) * mm, "end": v(-4.93, 191.32) * mm});
            skLineSegment(sketch, "E13.6.11.0", {"start": v(-20.33, 192.52) * mm, "end": v(-20.33, 207.92) * mm});
            skLineSegment(sketch, "E13.6.11.1", {"start": v(-20.33, 192.52) * mm, "end": v(-4.93, 192.52) * mm});
            skLineSegment(sketch, "E13.6.11.2", {"start": v(-4.93, 192.52) * mm, "end": v(-4.93, 207.92) * mm});
            skLineSegment(sketch, "E13.6.11.3", {"start": v(-20.33, 207.92) * mm, "end": v(-4.93, 207.92) * mm});
            skLineSegment(sketch, "E13.6.12.0", {"start": v(-20.33, 209.12) * mm, "end": v(-20.33, 224.52) * mm});
            skLineSegment(sketch, "E13.6.12.1", {"start": v(-20.33, 209.12) * mm, "end": v(-4.93, 209.12) * mm});
            skLineSegment(sketch, "E13.6.12.2", {"start": v(-4.93, 209.12) * mm, "end": v(-4.93, 224.52) * mm});
            skLineSegment(sketch, "E13.6.12.3", {"start": v(-20.33, 224.52) * mm, "end": v(-4.93, 224.52) * mm});
            skLineSegment(sketch, "E13.6.13.0", {"start": v(-20.33, 225.72) * mm, "end": v(-20.33, 241.12) * mm});
            skLineSegment(sketch, "E13.6.13.1", {"start": v(-20.33, 225.72) * mm, "end": v(-4.93, 225.72) * mm});
            skLineSegment(sketch, "E13.6.13.2", {"start": v(-4.93, 225.72) * mm, "end": v(-4.93, 241.12) * mm});
            skLineSegment(sketch, "E13.6.13.3", {"start": v(-20.33, 241.12) * mm, "end": v(-4.93, 241.12) * mm});
            skLineSegment(sketch, "E13.6.14.0", {"start": v(-20.33, 242.32) * mm, "end": v(-20.33, 257.72) * mm});
            skLineSegment(sketch, "E13.6.14.1", {"start": v(-20.33, 242.32) * mm, "end": v(-4.93, 242.32) * mm});
            skLineSegment(sketch, "E13.6.14.2", {"start": v(-4.93, 242.32) * mm, "end": v(-4.93, 257.72) * mm});
            skLineSegment(sketch, "E13.6.14.3", {"start": v(-20.33, 257.72) * mm, "end": v(-4.93, 257.72) * mm});
            skLineSegment(sketch, "E13.6.15.0", {"start": v(-20.33, 258.92) * mm, "end": v(-20.33, 274.32) * mm});
            skLineSegment(sketch, "E13.6.15.1", {"start": v(-20.33, 258.92) * mm, "end": v(-4.93, 258.92) * mm});
            skLineSegment(sketch, "E13.6.15.2", {"start": v(-4.93, 258.92) * mm, "end": v(-4.93, 274.32) * mm});
            skLineSegment(sketch, "E13.6.15.3", {"start": v(-20.33, 274.32) * mm, "end": v(-4.93, 274.32) * mm});
            skLineSegment(sketch, "E13.7.0.0", {"start": v(-3.73, 9.92) * mm, "end": v(-3.73, 25.32) * mm});
            skLineSegment(sketch, "E13.7.0.1", {"start": v(-3.73, 9.92) * mm, "end": v(11.67, 9.92) * mm});
            skLineSegment(sketch, "E13.7.0.2", {"start": v(11.67, 9.92) * mm, "end": v(11.67, 25.32) * mm});
            skLineSegment(sketch, "E13.7.0.3", {"start": v(-3.73, 25.32) * mm, "end": v(11.67, 25.32) * mm});
            skLineSegment(sketch, "E13.7.1.0", {"start": v(-3.73, 26.52) * mm, "end": v(-3.73, 41.92) * mm});
            skLineSegment(sketch, "E13.7.1.1", {"start": v(-3.73, 26.52) * mm, "end": v(11.67, 26.52) * mm});
            skLineSegment(sketch, "E13.7.1.2", {"start": v(11.67, 26.52) * mm, "end": v(11.67, 41.92) * mm});
            skLineSegment(sketch, "E13.7.1.3", {"start": v(-3.73, 41.92) * mm, "end": v(11.67, 41.92) * mm});
            skLineSegment(sketch, "E13.7.2.0", {"start": v(-3.73, 43.12) * mm, "end": v(-3.73, 58.52) * mm});
            skLineSegment(sketch, "E13.7.2.1", {"start": v(-3.73, 43.12) * mm, "end": v(11.67, 43.12) * mm});
            skLineSegment(sketch, "E13.7.2.2", {"start": v(11.67, 43.12) * mm, "end": v(11.67, 58.52) * mm});
            skLineSegment(sketch, "E13.7.2.3", {"start": v(-3.73, 58.52) * mm, "end": v(11.67, 58.52) * mm});
            skLineSegment(sketch, "E13.7.3.0", {"start": v(-3.73, 59.72) * mm, "end": v(-3.73, 75.12) * mm});
            skLineSegment(sketch, "E13.7.3.1", {"start": v(-3.73, 59.72) * mm, "end": v(11.67, 59.72) * mm});
            skLineSegment(sketch, "E13.7.3.2", {"start": v(11.67, 59.72) * mm, "end": v(11.67, 75.12) * mm});
            skLineSegment(sketch, "E13.7.3.3", {"start": v(-3.73, 75.12) * mm, "end": v(11.67, 75.12) * mm});
            skLineSegment(sketch, "E13.7.4.0", {"start": v(-3.73, 76.32) * mm, "end": v(-3.73, 91.72) * mm});
            skLineSegment(sketch, "E13.7.4.1", {"start": v(-3.73, 76.32) * mm, "end": v(11.67, 76.32) * mm});
            skLineSegment(sketch, "E13.7.4.2", {"start": v(11.67, 76.32) * mm, "end": v(11.67, 91.72) * mm});
            skLineSegment(sketch, "E13.7.4.3", {"start": v(-3.73, 91.72) * mm, "end": v(11.67, 91.72) * mm});
            skLineSegment(sketch, "E13.7.5.0", {"start": v(-3.73, 92.92) * mm, "end": v(-3.73, 108.32) * mm});
            skLineSegment(sketch, "E13.7.5.1", {"start": v(-3.73, 92.92) * mm, "end": v(11.67, 92.92) * mm});
            skLineSegment(sketch, "E13.7.5.2", {"start": v(11.67, 92.92) * mm, "end": v(11.67, 108.32) * mm});
            skLineSegment(sketch, "E13.7.5.3", {"start": v(-3.73, 108.32) * mm, "end": v(11.67, 108.32) * mm});
            skLineSegment(sketch, "E13.7.6.0", {"start": v(-3.73, 109.52) * mm, "end": v(-3.73, 124.92) * mm});
            skLineSegment(sketch, "E13.7.6.1", {"start": v(-3.73, 109.52) * mm, "end": v(11.67, 109.52) * mm});
            skLineSegment(sketch, "E13.7.6.2", {"start": v(11.67, 109.52) * mm, "end": v(11.67, 124.92) * mm});
            skLineSegment(sketch, "E13.7.6.3", {"start": v(-3.73, 124.92) * mm, "end": v(11.67, 124.92) * mm});
            skLineSegment(sketch, "E13.7.7.0", {"start": v(-3.73, 126.12) * mm, "end": v(-3.73, 141.52) * mm});
            skLineSegment(sketch, "E13.7.7.1", {"start": v(-3.73, 126.12) * mm, "end": v(11.67, 126.12) * mm});
            skLineSegment(sketch, "E13.7.7.2", {"start": v(11.67, 126.12) * mm, "end": v(11.67, 141.52) * mm});
            skLineSegment(sketch, "E13.7.7.3", {"start": v(-3.73, 141.52) * mm, "end": v(11.67, 141.52) * mm});
            skLineSegment(sketch, "E13.7.8.0", {"start": v(-3.73, 142.72) * mm, "end": v(-3.73, 158.12) * mm});
            skLineSegment(sketch, "E13.7.8.1", {"start": v(-3.73, 142.72) * mm, "end": v(11.67, 142.72) * mm});
            skLineSegment(sketch, "E13.7.8.2", {"start": v(11.67, 142.72) * mm, "end": v(11.67, 158.12) * mm});
            skLineSegment(sketch, "E13.7.8.3", {"start": v(-3.73, 158.12) * mm, "end": v(11.67, 158.12) * mm});
            skLineSegment(sketch, "E13.7.9.0", {"start": v(-3.73, 159.32) * mm, "end": v(-3.73, 174.72) * mm});
            skLineSegment(sketch, "E13.7.9.1", {"start": v(-3.73, 159.32) * mm, "end": v(11.67, 159.32) * mm});
            skLineSegment(sketch, "E13.7.9.2", {"start": v(11.67, 159.32) * mm, "end": v(11.67, 174.72) * mm});
            skLineSegment(sketch, "E13.7.9.3", {"start": v(-3.73, 174.72) * mm, "end": v(11.67, 174.72) * mm});
            skLineSegment(sketch, "E13.7.10.0", {"start": v(-3.73, 175.92) * mm, "end": v(-3.73, 191.32) * mm});
            skLineSegment(sketch, "E13.7.10.1", {"start": v(-3.73, 175.92) * mm, "end": v(11.67, 175.92) * mm});
            skLineSegment(sketch, "E13.7.10.2", {"start": v(11.67, 175.92) * mm, "end": v(11.67, 191.32) * mm});
            skLineSegment(sketch, "E13.7.10.3", {"start": v(-3.73, 191.32) * mm, "end": v(11.67, 191.32) * mm});
            skLineSegment(sketch, "E13.7.11.0", {"start": v(-3.73, 192.52) * mm, "end": v(-3.73, 207.92) * mm});
            skLineSegment(sketch, "E13.7.11.1", {"start": v(-3.73, 192.52) * mm, "end": v(11.67, 192.52) * mm});
            skLineSegment(sketch, "E13.7.11.2", {"start": v(11.67, 192.52) * mm, "end": v(11.67, 207.92) * mm});
            skLineSegment(sketch, "E13.7.11.3", {"start": v(-3.73, 207.92) * mm, "end": v(11.67, 207.92) * mm});
            skLineSegment(sketch, "E13.7.12.0", {"start": v(-3.73, 209.12) * mm, "end": v(-3.73, 224.52) * mm});
            skLineSegment(sketch, "E13.7.12.1", {"start": v(-3.73, 209.12) * mm, "end": v(11.67, 209.12) * mm});
            skLineSegment(sketch, "E13.7.12.2", {"start": v(11.67, 209.12) * mm, "end": v(11.67, 224.52) * mm});
            skLineSegment(sketch, "E13.7.12.3", {"start": v(-3.73, 224.52) * mm, "end": v(11.67, 224.52) * mm});
            skLineSegment(sketch, "E13.7.13.0", {"start": v(-3.73, 225.72) * mm, "end": v(-3.73, 241.12) * mm});
            skLineSegment(sketch, "E13.7.13.1", {"start": v(-3.73, 225.72) * mm, "end": v(11.67, 225.72) * mm});
            skLineSegment(sketch, "E13.7.13.2", {"start": v(11.67, 225.72) * mm, "end": v(11.67, 241.12) * mm});
            skLineSegment(sketch, "E13.7.13.3", {"start": v(-3.73, 241.12) * mm, "end": v(11.67, 241.12) * mm});
            skLineSegment(sketch, "E13.7.14.0", {"start": v(-3.73, 242.32) * mm, "end": v(-3.73, 257.72) * mm});
            skLineSegment(sketch, "E13.7.14.1", {"start": v(-3.73, 242.32) * mm, "end": v(11.67, 242.32) * mm});
            skLineSegment(sketch, "E13.7.14.2", {"start": v(11.67, 242.32) * mm, "end": v(11.67, 257.72) * mm});
            skLineSegment(sketch, "E13.7.14.3", {"start": v(-3.73, 257.72) * mm, "end": v(11.67, 257.72) * mm});
            skLineSegment(sketch, "E13.7.15.0", {"start": v(-3.73, 258.92) * mm, "end": v(-3.73, 274.32) * mm});
            skLineSegment(sketch, "E13.7.15.1", {"start": v(-3.73, 258.92) * mm, "end": v(11.67, 258.92) * mm});
            skLineSegment(sketch, "E13.7.15.2", {"start": v(11.67, 258.92) * mm, "end": v(11.67, 274.32) * mm});
            skLineSegment(sketch, "E13.7.15.3", {"start": v(-3.73, 274.32) * mm, "end": v(11.67, 274.32) * mm});
            skLineSegment(sketch, "E13.8.0.0", {"start": v(12.87, 9.92) * mm, "end": v(12.87, 25.32) * mm});
            skLineSegment(sketch, "E13.8.0.1", {"start": v(12.87, 9.92) * mm, "end": v(28.27, 9.92) * mm});
            skLineSegment(sketch, "E13.8.0.2", {"start": v(28.27, 9.92) * mm, "end": v(28.27, 25.32) * mm});
            skLineSegment(sketch, "E13.8.0.3", {"start": v(12.87, 25.32) * mm, "end": v(28.27, 25.32) * mm});
            skLineSegment(sketch, "E13.8.1.0", {"start": v(12.87, 26.52) * mm, "end": v(12.87, 41.92) * mm});
            skLineSegment(sketch, "E13.8.1.1", {"start": v(12.87, 26.52) * mm, "end": v(28.27, 26.52) * mm});
            skLineSegment(sketch, "E13.8.1.2", {"start": v(28.27, 26.52) * mm, "end": v(28.27, 41.92) * mm});
            skLineSegment(sketch, "E13.8.1.3", {"start": v(12.87, 41.92) * mm, "end": v(28.27, 41.92) * mm});
            skLineSegment(sketch, "E13.8.2.0", {"start": v(12.87, 43.12) * mm, "end": v(12.87, 58.52) * mm});
            skLineSegment(sketch, "E13.8.2.1", {"start": v(12.87, 43.12) * mm, "end": v(28.27, 43.12) * mm});
            skLineSegment(sketch, "E13.8.2.2", {"start": v(28.27, 43.12) * mm, "end": v(28.27, 58.52) * mm});
            skLineSegment(sketch, "E13.8.2.3", {"start": v(12.87, 58.52) * mm, "end": v(28.27, 58.52) * mm});
            skLineSegment(sketch, "E13.8.3.0", {"start": v(12.87, 59.72) * mm, "end": v(12.87, 75.12) * mm});
            skLineSegment(sketch, "E13.8.3.1", {"start": v(12.87, 59.72) * mm, "end": v(28.27, 59.72) * mm});
            skLineSegment(sketch, "E13.8.3.2", {"start": v(28.27, 59.72) * mm, "end": v(28.27, 75.12) * mm});
            skLineSegment(sketch, "E13.8.3.3", {"start": v(12.87, 75.12) * mm, "end": v(28.27, 75.12) * mm});
            skLineSegment(sketch, "E13.8.4.0", {"start": v(12.87, 76.32) * mm, "end": v(12.87, 91.72) * mm});
            skLineSegment(sketch, "E13.8.4.1", {"start": v(12.87, 76.32) * mm, "end": v(28.27, 76.32) * mm});
            skLineSegment(sketch, "E13.8.4.2", {"start": v(28.27, 76.32) * mm, "end": v(28.27, 91.72) * mm});
            skLineSegment(sketch, "E13.8.4.3", {"start": v(12.87, 91.72) * mm, "end": v(28.27, 91.72) * mm});
            skLineSegment(sketch, "E13.8.5.0", {"start": v(12.87, 92.92) * mm, "end": v(12.87, 108.32) * mm});
            skLineSegment(sketch, "E13.8.5.1", {"start": v(12.87, 92.92) * mm, "end": v(28.27, 92.92) * mm});
            skLineSegment(sketch, "E13.8.5.2", {"start": v(28.27, 92.92) * mm, "end": v(28.27, 108.32) * mm});
            skLineSegment(sketch, "E13.8.5.3", {"start": v(12.87, 108.32) * mm, "end": v(28.27, 108.32) * mm});
            skLineSegment(sketch, "E13.8.6.0", {"start": v(12.87, 109.52) * mm, "end": v(12.87, 124.92) * mm});
            skLineSegment(sketch, "E13.8.6.1", {"start": v(12.87, 109.52) * mm, "end": v(28.27, 109.52) * mm});
            skLineSegment(sketch, "E13.8.6.2", {"start": v(28.27, 109.52) * mm, "end": v(28.27, 124.92) * mm});
            skLineSegment(sketch, "E13.8.6.3", {"start": v(12.87, 124.92) * mm, "end": v(28.27, 124.92) * mm});
            skLineSegment(sketch, "E13.8.7.0", {"start": v(12.87, 126.12) * mm, "end": v(12.87, 141.52) * mm});
            skLineSegment(sketch, "E13.8.7.1", {"start": v(12.87, 126.12) * mm, "end": v(28.27, 126.12) * mm});
            skLineSegment(sketch, "E13.8.7.2", {"start": v(28.27, 126.12) * mm, "end": v(28.27, 141.52) * mm});
            skLineSegment(sketch, "E13.8.7.3", {"start": v(12.87, 141.52) * mm, "end": v(28.27, 141.52) * mm});
            skLineSegment(sketch, "E13.8.8.0", {"start": v(12.87, 142.72) * mm, "end": v(12.87, 158.12) * mm});
            skLineSegment(sketch, "E13.8.8.1", {"start": v(12.87, 142.72) * mm, "end": v(28.27, 142.72) * mm});
            skLineSegment(sketch, "E13.8.8.2", {"start": v(28.27, 142.72) * mm, "end": v(28.27, 158.12) * mm});
            skLineSegment(sketch, "E13.8.8.3", {"start": v(12.87, 158.12) * mm, "end": v(28.27, 158.12) * mm});
            skLineSegment(sketch, "E13.8.9.0", {"start": v(12.87, 159.32) * mm, "end": v(12.87, 174.72) * mm});
            skLineSegment(sketch, "E13.8.9.1", {"start": v(12.87, 159.32) * mm, "end": v(28.27, 159.32) * mm});
            skLineSegment(sketch, "E13.8.9.2", {"start": v(28.27, 159.32) * mm, "end": v(28.27, 174.72) * mm});
            skLineSegment(sketch, "E13.8.9.3", {"start": v(12.87, 174.72) * mm, "end": v(28.27, 174.72) * mm});
            skLineSegment(sketch, "E13.8.10.0", {"start": v(12.87, 175.92) * mm, "end": v(12.87, 191.32) * mm});
            skLineSegment(sketch, "E13.8.10.1", {"start": v(12.87, 175.92) * mm, "end": v(28.27, 175.92) * mm});
            skLineSegment(sketch, "E13.8.10.2", {"start": v(28.27, 175.92) * mm, "end": v(28.27, 191.32) * mm});
            skLineSegment(sketch, "E13.8.10.3", {"start": v(12.87, 191.32) * mm, "end": v(28.27, 191.32) * mm});
            skLineSegment(sketch, "E13.8.11.0", {"start": v(12.87, 192.52) * mm, "end": v(12.87, 207.92) * mm});
            skLineSegment(sketch, "E13.8.11.1", {"start": v(12.87, 192.52) * mm, "end": v(28.27, 192.52) * mm});
            skLineSegment(sketch, "E13.8.11.2", {"start": v(28.27, 192.52) * mm, "end": v(28.27, 207.92) * mm});
            skLineSegment(sketch, "E13.8.11.3", {"start": v(12.87, 207.92) * mm, "end": v(28.27, 207.92) * mm});
            skLineSegment(sketch, "E13.8.12.0", {"start": v(12.87, 209.12) * mm, "end": v(12.87, 224.52) * mm});
            skLineSegment(sketch, "E13.8.12.1", {"start": v(12.87, 209.12) * mm, "end": v(28.27, 209.12) * mm});
            skLineSegment(sketch, "E13.8.12.2", {"start": v(28.27, 209.12) * mm, "end": v(28.27, 224.52) * mm});
            skLineSegment(sketch, "E13.8.12.3", {"start": v(12.87, 224.52) * mm, "end": v(28.27, 224.52) * mm});
            skLineSegment(sketch, "E13.8.13.0", {"start": v(12.87, 225.72) * mm, "end": v(12.87, 241.12) * mm});
            skLineSegment(sketch, "E13.8.13.1", {"start": v(12.87, 225.72) * mm, "end": v(28.27, 225.72) * mm});
            skLineSegment(sketch, "E13.8.13.2", {"start": v(28.27, 225.72) * mm, "end": v(28.27, 241.12) * mm});
            skLineSegment(sketch, "E13.8.13.3", {"start": v(12.87, 241.12) * mm, "end": v(28.27, 241.12) * mm});
            skLineSegment(sketch, "E13.8.14.0", {"start": v(12.87, 242.32) * mm, "end": v(12.87, 257.72) * mm});
            skLineSegment(sketch, "E13.8.14.1", {"start": v(12.87, 242.32) * mm, "end": v(28.27, 242.32) * mm});
            skLineSegment(sketch, "E13.8.14.2", {"start": v(28.27, 242.32) * mm, "end": v(28.27, 257.72) * mm});
            skLineSegment(sketch, "E13.8.14.3", {"start": v(12.87, 257.72) * mm, "end": v(28.27, 257.72) * mm});
            skLineSegment(sketch, "E13.8.15.0", {"start": v(12.87, 258.92) * mm, "end": v(12.87, 274.32) * mm});
            skLineSegment(sketch, "E13.8.15.1", {"start": v(12.87, 258.92) * mm, "end": v(28.27, 258.92) * mm});
            skLineSegment(sketch, "E13.8.15.2", {"start": v(28.27, 258.92) * mm, "end": v(28.27, 274.32) * mm});
            skLineSegment(sketch, "E13.8.15.3", {"start": v(12.87, 274.32) * mm, "end": v(28.27, 274.32) * mm});
            skLineSegment(sketch, "E13.9.0.0", {"start": v(29.47, 9.92) * mm, "end": v(29.47, 25.32) * mm});
            skLineSegment(sketch, "E13.9.0.1", {"start": v(29.47, 9.92) * mm, "end": v(44.87, 9.92) * mm});
            skLineSegment(sketch, "E13.9.0.2", {"start": v(44.87, 9.92) * mm, "end": v(44.87, 25.32) * mm});
            skLineSegment(sketch, "E13.9.0.3", {"start": v(29.47, 25.32) * mm, "end": v(44.87, 25.32) * mm});
            skLineSegment(sketch, "E13.9.1.0", {"start": v(29.47, 26.52) * mm, "end": v(29.47, 41.92) * mm});
            skLineSegment(sketch, "E13.9.1.1", {"start": v(29.47, 26.52) * mm, "end": v(44.87, 26.52) * mm});
            skLineSegment(sketch, "E13.9.1.2", {"start": v(44.87, 26.52) * mm, "end": v(44.87, 41.92) * mm});
            skLineSegment(sketch, "E13.9.1.3", {"start": v(29.47, 41.92) * mm, "end": v(44.87, 41.92) * mm});
            skLineSegment(sketch, "E13.9.2.0", {"start": v(29.47, 43.12) * mm, "end": v(29.47, 58.52) * mm});
            skLineSegment(sketch, "E13.9.2.1", {"start": v(29.47, 43.12) * mm, "end": v(44.87, 43.12) * mm});
            skLineSegment(sketch, "E13.9.2.2", {"start": v(44.87, 43.12) * mm, "end": v(44.87, 58.52) * mm});
            skLineSegment(sketch, "E13.9.2.3", {"start": v(29.47, 58.52) * mm, "end": v(44.87, 58.52) * mm});
            skLineSegment(sketch, "E13.9.3.0", {"start": v(29.47, 59.72) * mm, "end": v(29.47, 75.12) * mm});
            skLineSegment(sketch, "E13.9.3.1", {"start": v(29.47, 59.72) * mm, "end": v(44.87, 59.72) * mm});
            skLineSegment(sketch, "E13.9.3.2", {"start": v(44.87, 59.72) * mm, "end": v(44.87, 75.12) * mm});
            skLineSegment(sketch, "E13.9.3.3", {"start": v(29.47, 75.12) * mm, "end": v(44.87, 75.12) * mm});
            skLineSegment(sketch, "E13.9.4.0", {"start": v(29.47, 76.32) * mm, "end": v(29.47, 91.72) * mm});
            skLineSegment(sketch, "E13.9.4.1", {"start": v(29.47, 76.32) * mm, "end": v(44.87, 76.32) * mm});
            skLineSegment(sketch, "E13.9.4.2", {"start": v(44.87, 76.32) * mm, "end": v(44.87, 91.72) * mm});
            skLineSegment(sketch, "E13.9.4.3", {"start": v(29.47, 91.72) * mm, "end": v(44.87, 91.72) * mm});
            skLineSegment(sketch, "E13.9.5.0", {"start": v(29.47, 92.92) * mm, "end": v(29.47, 108.32) * mm});
            skLineSegment(sketch, "E13.9.5.1", {"start": v(29.47, 92.92) * mm, "end": v(44.87, 92.92) * mm});
            skLineSegment(sketch, "E13.9.5.2", {"start": v(44.87, 92.92) * mm, "end": v(44.87, 108.32) * mm});
            skLineSegment(sketch, "E13.9.5.3", {"start": v(29.47, 108.32) * mm, "end": v(44.87, 108.32) * mm});
            skLineSegment(sketch, "E13.9.6.0", {"start": v(29.47, 109.52) * mm, "end": v(29.47, 124.92) * mm});
            skLineSegment(sketch, "E13.9.6.1", {"start": v(29.47, 109.52) * mm, "end": v(44.87, 109.52) * mm});
            skLineSegment(sketch, "E13.9.6.2", {"start": v(44.87, 109.52) * mm, "end": v(44.87, 124.92) * mm});
            skLineSegment(sketch, "E13.9.6.3", {"start": v(29.47, 124.92) * mm, "end": v(44.87, 124.92) * mm});
            skLineSegment(sketch, "E13.9.7.0", {"start": v(29.47, 126.12) * mm, "end": v(29.47, 141.52) * mm});
            skLineSegment(sketch, "E13.9.7.1", {"start": v(29.47, 126.12) * mm, "end": v(44.87, 126.12) * mm});
            skLineSegment(sketch, "E13.9.7.2", {"start": v(44.87, 126.12) * mm, "end": v(44.87, 141.52) * mm});
            skLineSegment(sketch, "E13.9.7.3", {"start": v(29.47, 141.52) * mm, "end": v(44.87, 141.52) * mm});
            skLineSegment(sketch, "E13.9.8.0", {"start": v(29.47, 142.72) * mm, "end": v(29.47, 158.12) * mm});
            skLineSegment(sketch, "E13.9.8.1", {"start": v(29.47, 142.72) * mm, "end": v(44.87, 142.72) * mm});
            skLineSegment(sketch, "E13.9.8.2", {"start": v(44.87, 142.72) * mm, "end": v(44.87, 158.12) * mm});
            skLineSegment(sketch, "E13.9.8.3", {"start": v(29.47, 158.12) * mm, "end": v(44.87, 158.12) * mm});
            skLineSegment(sketch, "E13.9.9.0", {"start": v(29.47, 159.32) * mm, "end": v(29.47, 174.72) * mm});
            skLineSegment(sketch, "E13.9.9.1", {"start": v(29.47, 159.32) * mm, "end": v(44.87, 159.32) * mm});
            skLineSegment(sketch, "E13.9.9.2", {"start": v(44.87, 159.32) * mm, "end": v(44.87, 174.72) * mm});
            skLineSegment(sketch, "E13.9.9.3", {"start": v(29.47, 174.72) * mm, "end": v(44.87, 174.72) * mm});
            skLineSegment(sketch, "E13.9.10.0", {"start": v(29.47, 175.92) * mm, "end": v(29.47, 191.32) * mm});
            skLineSegment(sketch, "E13.9.10.1", {"start": v(29.47, 175.92) * mm, "end": v(44.87, 175.92) * mm});
            skLineSegment(sketch, "E13.9.10.2", {"start": v(44.87, 175.92) * mm, "end": v(44.87, 191.32) * mm});
            skLineSegment(sketch, "E13.9.10.3", {"start": v(29.47, 191.32) * mm, "end": v(44.87, 191.32) * mm});
            skLineSegment(sketch, "E13.9.11.0", {"start": v(29.47, 192.52) * mm, "end": v(29.47, 207.92) * mm});
            skLineSegment(sketch, "E13.9.11.1", {"start": v(29.47, 192.52) * mm, "end": v(44.87, 192.52) * mm});
            skLineSegment(sketch, "E13.9.11.2", {"start": v(44.87, 192.52) * mm, "end": v(44.87, 207.92) * mm});
            skLineSegment(sketch, "E13.9.11.3", {"start": v(29.47, 207.92) * mm, "end": v(44.87, 207.92) * mm});
            skLineSegment(sketch, "E13.9.12.0", {"start": v(29.47, 209.12) * mm, "end": v(29.47, 224.52) * mm});
            skLineSegment(sketch, "E13.9.12.1", {"start": v(29.47, 209.12) * mm, "end": v(44.87, 209.12) * mm});
            skLineSegment(sketch, "E13.9.12.2", {"start": v(44.87, 209.12) * mm, "end": v(44.87, 224.52) * mm});
            skLineSegment(sketch, "E13.9.12.3", {"start": v(29.47, 224.52) * mm, "end": v(44.87, 224.52) * mm});
            skLineSegment(sketch, "E13.9.13.0", {"start": v(29.47, 225.72) * mm, "end": v(29.47, 241.12) * mm});
            skLineSegment(sketch, "E13.9.13.1", {"start": v(29.47, 225.72) * mm, "end": v(44.87, 225.72) * mm});
            skLineSegment(sketch, "E13.9.13.2", {"start": v(44.87, 225.72) * mm, "end": v(44.87, 241.12) * mm});
            skLineSegment(sketch, "E13.9.13.3", {"start": v(29.47, 241.12) * mm, "end": v(44.87, 241.12) * mm});
            skLineSegment(sketch, "E13.9.14.0", {"start": v(29.47, 242.32) * mm, "end": v(29.47, 257.72) * mm});
            skLineSegment(sketch, "E13.9.14.1", {"start": v(29.47, 242.32) * mm, "end": v(44.87, 242.32) * mm});
            skLineSegment(sketch, "E13.9.14.2", {"start": v(44.87, 242.32) * mm, "end": v(44.87, 257.72) * mm});
            skLineSegment(sketch, "E13.9.14.3", {"start": v(29.47, 257.72) * mm, "end": v(44.87, 257.72) * mm});
            skLineSegment(sketch, "E13.9.15.0", {"start": v(29.47, 258.92) * mm, "end": v(29.47, 274.32) * mm});
            skLineSegment(sketch, "E13.9.15.1", {"start": v(29.47, 258.92) * mm, "end": v(44.87, 258.92) * mm});
            skLineSegment(sketch, "E13.9.15.2", {"start": v(44.87, 258.92) * mm, "end": v(44.87, 274.32) * mm});
            skLineSegment(sketch, "E13.9.15.3", {"start": v(29.47, 274.32) * mm, "end": v(44.87, 274.32) * mm});
            skLineSegment(sketch, "E13.10.0.0", {"start": v(46.07, 9.92) * mm, "end": v(46.07, 25.32) * mm});
            skLineSegment(sketch, "E13.10.0.1", {"start": v(46.07, 9.92) * mm, "end": v(61.47, 9.92) * mm});
            skLineSegment(sketch, "E13.10.0.2", {"start": v(61.47, 9.92) * mm, "end": v(61.47, 25.32) * mm});
            skLineSegment(sketch, "E13.10.0.3", {"start": v(46.07, 25.32) * mm, "end": v(61.47, 25.32) * mm});
            skLineSegment(sketch, "E13.10.1.0", {"start": v(46.07, 26.52) * mm, "end": v(46.07, 41.92) * mm});
            skLineSegment(sketch, "E13.10.1.1", {"start": v(46.07, 26.52) * mm, "end": v(61.47, 26.52) * mm});
            skLineSegment(sketch, "E13.10.1.2", {"start": v(61.47, 26.52) * mm, "end": v(61.47, 41.92) * mm});
            skLineSegment(sketch, "E13.10.1.3", {"start": v(46.07, 41.92) * mm, "end": v(61.47, 41.92) * mm});
            skLineSegment(sketch, "E13.10.2.0", {"start": v(46.07, 43.12) * mm, "end": v(46.07, 58.52) * mm});
            skLineSegment(sketch, "E13.10.2.1", {"start": v(46.07, 43.12) * mm, "end": v(61.47, 43.12) * mm});
            skLineSegment(sketch, "E13.10.2.2", {"start": v(61.47, 43.12) * mm, "end": v(61.47, 58.52) * mm});
            skLineSegment(sketch, "E13.10.2.3", {"start": v(46.07, 58.52) * mm, "end": v(61.47, 58.52) * mm});
            skLineSegment(sketch, "E13.10.3.0", {"start": v(46.07, 59.72) * mm, "end": v(46.07, 75.12) * mm});
            skLineSegment(sketch, "E13.10.3.1", {"start": v(46.07, 59.72) * mm, "end": v(61.47, 59.72) * mm});
            skLineSegment(sketch, "E13.10.3.2", {"start": v(61.47, 59.72) * mm, "end": v(61.47, 75.12) * mm});
            skLineSegment(sketch, "E13.10.3.3", {"start": v(46.07, 75.12) * mm, "end": v(61.47, 75.12) * mm});
            skLineSegment(sketch, "E13.10.4.0", {"start": v(46.07, 76.32) * mm, "end": v(46.07, 91.72) * mm});
            skLineSegment(sketch, "E13.10.4.1", {"start": v(46.07, 76.32) * mm, "end": v(61.47, 76.32) * mm});
            skLineSegment(sketch, "E13.10.4.2", {"start": v(61.47, 76.32) * mm, "end": v(61.47, 91.72) * mm});
            skLineSegment(sketch, "E13.10.4.3", {"start": v(46.07, 91.72) * mm, "end": v(61.47, 91.72) * mm});
            skLineSegment(sketch, "E13.10.5.0", {"start": v(46.07, 92.92) * mm, "end": v(46.07, 108.32) * mm});
            skLineSegment(sketch, "E13.10.5.1", {"start": v(46.07, 92.92) * mm, "end": v(61.47, 92.92) * mm});
            skLineSegment(sketch, "E13.10.5.2", {"start": v(61.47, 92.92) * mm, "end": v(61.47, 108.32) * mm});
            skLineSegment(sketch, "E13.10.5.3", {"start": v(46.07, 108.32) * mm, "end": v(61.47, 108.32) * mm});
            skLineSegment(sketch, "E13.10.6.0", {"start": v(46.07, 109.52) * mm, "end": v(46.07, 124.92) * mm});
            skLineSegment(sketch, "E13.10.6.1", {"start": v(46.07, 109.52) * mm, "end": v(61.47, 109.52) * mm});
            skLineSegment(sketch, "E13.10.6.2", {"start": v(61.47, 109.52) * mm, "end": v(61.47, 124.92) * mm});
            skLineSegment(sketch, "E13.10.6.3", {"start": v(46.07, 124.92) * mm, "end": v(61.47, 124.92) * mm});
            skLineSegment(sketch, "E13.10.7.0", {"start": v(46.07, 126.12) * mm, "end": v(46.07, 141.52) * mm});
            skLineSegment(sketch, "E13.10.7.1", {"start": v(46.07, 126.12) * mm, "end": v(61.47, 126.12) * mm});
            skLineSegment(sketch, "E13.10.7.2", {"start": v(61.47, 126.12) * mm, "end": v(61.47, 141.52) * mm});
            skLineSegment(sketch, "E13.10.7.3", {"start": v(46.07, 141.52) * mm, "end": v(61.47, 141.52) * mm});
            skLineSegment(sketch, "E13.10.8.0", {"start": v(46.07, 142.72) * mm, "end": v(46.07, 158.12) * mm});
            skLineSegment(sketch, "E13.10.8.1", {"start": v(46.07, 142.72) * mm, "end": v(61.47, 142.72) * mm});
            skLineSegment(sketch, "E13.10.8.2", {"start": v(61.47, 142.72) * mm, "end": v(61.47, 158.12) * mm});
            skLineSegment(sketch, "E13.10.8.3", {"start": v(46.07, 158.12) * mm, "end": v(61.47, 158.12) * mm});
            skLineSegment(sketch, "E13.10.9.0", {"start": v(46.07, 159.32) * mm, "end": v(46.07, 174.72) * mm});
            skLineSegment(sketch, "E13.10.9.1", {"start": v(46.07, 159.32) * mm, "end": v(61.47, 159.32) * mm});
            skLineSegment(sketch, "E13.10.9.2", {"start": v(61.47, 159.32) * mm, "end": v(61.47, 174.72) * mm});
            skLineSegment(sketch, "E13.10.9.3", {"start": v(46.07, 174.72) * mm, "end": v(61.47, 174.72) * mm});
            skLineSegment(sketch, "E13.10.10.0", {"start": v(46.07, 175.92) * mm, "end": v(46.07, 191.32) * mm});
            skLineSegment(sketch, "E13.10.10.1", {"start": v(46.07, 175.92) * mm, "end": v(61.47, 175.92) * mm});
            skLineSegment(sketch, "E13.10.10.2", {"start": v(61.47, 175.92) * mm, "end": v(61.47, 191.32) * mm});
            skLineSegment(sketch, "E13.10.10.3", {"start": v(46.07, 191.32) * mm, "end": v(61.47, 191.32) * mm});
            skLineSegment(sketch, "E13.10.11.0", {"start": v(46.07, 192.52) * mm, "end": v(46.07, 207.92) * mm});
            skLineSegment(sketch, "E13.10.11.1", {"start": v(46.07, 192.52) * mm, "end": v(61.47, 192.52) * mm});
            skLineSegment(sketch, "E13.10.11.2", {"start": v(61.47, 192.52) * mm, "end": v(61.47, 207.92) * mm});
            skLineSegment(sketch, "E13.10.11.3", {"start": v(46.07, 207.92) * mm, "end": v(61.47, 207.92) * mm});
            skLineSegment(sketch, "E13.10.12.0", {"start": v(46.07, 209.12) * mm, "end": v(46.07, 224.52) * mm});
            skLineSegment(sketch, "E13.10.12.1", {"start": v(46.07, 209.12) * mm, "end": v(61.47, 209.12) * mm});
            skLineSegment(sketch, "E13.10.12.2", {"start": v(61.47, 209.12) * mm, "end": v(61.47, 224.52) * mm});
            skLineSegment(sketch, "E13.10.12.3", {"start": v(46.07, 224.52) * mm, "end": v(61.47, 224.52) * mm});
            skLineSegment(sketch, "E13.10.13.0", {"start": v(46.07, 225.72) * mm, "end": v(46.07, 241.12) * mm});
            skLineSegment(sketch, "E13.10.13.1", {"start": v(46.07, 225.72) * mm, "end": v(61.47, 225.72) * mm});
            skLineSegment(sketch, "E13.10.13.2", {"start": v(61.47, 225.72) * mm, "end": v(61.47, 241.12) * mm});
            skLineSegment(sketch, "E13.10.13.3", {"start": v(46.07, 241.12) * mm, "end": v(61.47, 241.12) * mm});
            skLineSegment(sketch, "E13.10.14.0", {"start": v(46.07, 242.32) * mm, "end": v(46.07, 257.72) * mm});
            skLineSegment(sketch, "E13.10.14.1", {"start": v(46.07, 242.32) * mm, "end": v(61.47, 242.32) * mm});
            skLineSegment(sketch, "E13.10.14.2", {"start": v(61.47, 242.32) * mm, "end": v(61.47, 257.72) * mm});
            skLineSegment(sketch, "E13.10.14.3", {"start": v(46.07, 257.72) * mm, "end": v(61.47, 257.72) * mm});
            skLineSegment(sketch, "E13.10.15.0", {"start": v(46.07, 258.92) * mm, "end": v(46.07, 274.32) * mm});
            skLineSegment(sketch, "E13.10.15.1", {"start": v(46.07, 258.92) * mm, "end": v(61.47, 258.92) * mm});
            skLineSegment(sketch, "E13.10.15.2", {"start": v(61.47, 258.92) * mm, "end": v(61.47, 274.32) * mm});
            skLineSegment(sketch, "E13.10.15.3", {"start": v(46.07, 274.32) * mm, "end": v(61.47, 274.32) * mm});
            skLineSegment(sketch, "E13.11.0.0", {"start": v(62.67, 9.92) * mm, "end": v(62.67, 25.32) * mm});
            skLineSegment(sketch, "E13.11.0.1", {"start": v(62.67, 9.92) * mm, "end": v(78.07, 9.92) * mm});
            skLineSegment(sketch, "E13.11.0.2", {"start": v(78.07, 9.92) * mm, "end": v(78.07, 25.32) * mm});
            skLineSegment(sketch, "E13.11.0.3", {"start": v(62.67, 25.32) * mm, "end": v(78.07, 25.32) * mm});
            skLineSegment(sketch, "E13.11.1.0", {"start": v(62.67, 26.52) * mm, "end": v(62.67, 41.92) * mm});
            skLineSegment(sketch, "E13.11.1.1", {"start": v(62.67, 26.52) * mm, "end": v(78.07, 26.52) * mm});
            skLineSegment(sketch, "E13.11.1.2", {"start": v(78.07, 26.52) * mm, "end": v(78.07, 41.92) * mm});
            skLineSegment(sketch, "E13.11.1.3", {"start": v(62.67, 41.92) * mm, "end": v(78.07, 41.92) * mm});
            skLineSegment(sketch, "E13.11.2.0", {"start": v(62.67, 43.12) * mm, "end": v(62.67, 58.52) * mm});
            skLineSegment(sketch, "E13.11.2.1", {"start": v(62.67, 43.12) * mm, "end": v(78.07, 43.12) * mm});
            skLineSegment(sketch, "E13.11.2.2", {"start": v(78.07, 43.12) * mm, "end": v(78.07, 58.52) * mm});
            skLineSegment(sketch, "E13.11.2.3", {"start": v(62.67, 58.52) * mm, "end": v(78.07, 58.52) * mm});
            skLineSegment(sketch, "E13.11.3.0", {"start": v(62.67, 59.72) * mm, "end": v(62.67, 75.12) * mm});
            skLineSegment(sketch, "E13.11.3.1", {"start": v(62.67, 59.72) * mm, "end": v(78.07, 59.72) * mm});
            skLineSegment(sketch, "E13.11.3.2", {"start": v(78.07, 59.72) * mm, "end": v(78.07, 75.12) * mm});
            skLineSegment(sketch, "E13.11.3.3", {"start": v(62.67, 75.12) * mm, "end": v(78.07, 75.12) * mm});
            skLineSegment(sketch, "E13.11.4.0", {"start": v(62.67, 76.32) * mm, "end": v(62.67, 91.72) * mm});
            skLineSegment(sketch, "E13.11.4.1", {"start": v(62.67, 76.32) * mm, "end": v(78.07, 76.32) * mm});
            skLineSegment(sketch, "E13.11.4.2", {"start": v(78.07, 76.32) * mm, "end": v(78.07, 91.72) * mm});
            skLineSegment(sketch, "E13.11.4.3", {"start": v(62.67, 91.72) * mm, "end": v(78.07, 91.72) * mm});
            skLineSegment(sketch, "E13.11.5.0", {"start": v(62.67, 92.92) * mm, "end": v(62.67, 108.32) * mm});
            skLineSegment(sketch, "E13.11.5.1", {"start": v(62.67, 92.92) * mm, "end": v(78.07, 92.92) * mm});
            skLineSegment(sketch, "E13.11.5.2", {"start": v(78.07, 92.92) * mm, "end": v(78.07, 108.32) * mm});
            skLineSegment(sketch, "E13.11.5.3", {"start": v(62.67, 108.32) * mm, "end": v(78.07, 108.32) * mm});
            skLineSegment(sketch, "E13.11.6.0", {"start": v(62.67, 109.52) * mm, "end": v(62.67, 124.92) * mm});
            skLineSegment(sketch, "E13.11.6.1", {"start": v(62.67, 109.52) * mm, "end": v(78.07, 109.52) * mm});
            skLineSegment(sketch, "E13.11.6.2", {"start": v(78.07, 109.52) * mm, "end": v(78.07, 124.92) * mm});
            skLineSegment(sketch, "E13.11.6.3", {"start": v(62.67, 124.92) * mm, "end": v(78.07, 124.92) * mm});
            skLineSegment(sketch, "E13.11.7.0", {"start": v(62.67, 126.12) * mm, "end": v(62.67, 141.52) * mm});
            skLineSegment(sketch, "E13.11.7.1", {"start": v(62.67, 126.12) * mm, "end": v(78.07, 126.12) * mm});
            skLineSegment(sketch, "E13.11.7.2", {"start": v(78.07, 126.12) * mm, "end": v(78.07, 141.52) * mm});
            skLineSegment(sketch, "E13.11.7.3", {"start": v(62.67, 141.52) * mm, "end": v(78.07, 141.52) * mm});
            skLineSegment(sketch, "E13.11.8.0", {"start": v(62.67, 142.72) * mm, "end": v(62.67, 158.12) * mm});
            skLineSegment(sketch, "E13.11.8.1", {"start": v(62.67, 142.72) * mm, "end": v(78.07, 142.72) * mm});
            skLineSegment(sketch, "E13.11.8.2", {"start": v(78.07, 142.72) * mm, "end": v(78.07, 158.12) * mm});
            skLineSegment(sketch, "E13.11.8.3", {"start": v(62.67, 158.12) * mm, "end": v(78.07, 158.12) * mm});
            skLineSegment(sketch, "E13.11.9.0", {"start": v(62.67, 159.32) * mm, "end": v(62.67, 174.72) * mm});
            skLineSegment(sketch, "E13.11.9.1", {"start": v(62.67, 159.32) * mm, "end": v(78.07, 159.32) * mm});
            skLineSegment(sketch, "E13.11.9.2", {"start": v(78.07, 159.32) * mm, "end": v(78.07, 174.72) * mm});
            skLineSegment(sketch, "E13.11.9.3", {"start": v(62.67, 174.72) * mm, "end": v(78.07, 174.72) * mm});
            skLineSegment(sketch, "E13.11.10.0", {"start": v(62.67, 175.92) * mm, "end": v(62.67, 191.32) * mm});
            skLineSegment(sketch, "E13.11.10.1", {"start": v(62.67, 175.92) * mm, "end": v(78.07, 175.92) * mm});
            skLineSegment(sketch, "E13.11.10.2", {"start": v(78.07, 175.92) * mm, "end": v(78.07, 191.32) * mm});
            skLineSegment(sketch, "E13.11.10.3", {"start": v(62.67, 191.32) * mm, "end": v(78.07, 191.32) * mm});
            skLineSegment(sketch, "E13.11.11.0", {"start": v(62.67, 192.52) * mm, "end": v(62.67, 207.92) * mm});
            skLineSegment(sketch, "E13.11.11.1", {"start": v(62.67, 192.52) * mm, "end": v(78.07, 192.52) * mm});
            skLineSegment(sketch, "E13.11.11.2", {"start": v(78.07, 192.52) * mm, "end": v(78.07, 207.92) * mm});
            skLineSegment(sketch, "E13.11.11.3", {"start": v(62.67, 207.92) * mm, "end": v(78.07, 207.92) * mm});
            skLineSegment(sketch, "E13.11.12.0", {"start": v(62.67, 209.12) * mm, "end": v(62.67, 224.52) * mm});
            skLineSegment(sketch, "E13.11.12.1", {"start": v(62.67, 209.12) * mm, "end": v(78.07, 209.12) * mm});
            skLineSegment(sketch, "E13.11.12.2", {"start": v(78.07, 209.12) * mm, "end": v(78.07, 224.52) * mm});
            skLineSegment(sketch, "E13.11.12.3", {"start": v(62.67, 224.52) * mm, "end": v(78.07, 224.52) * mm});
            skLineSegment(sketch, "E13.11.13.0", {"start": v(62.67, 225.72) * mm, "end": v(62.67, 241.12) * mm});
            skLineSegment(sketch, "E13.11.13.1", {"start": v(62.67, 225.72) * mm, "end": v(78.07, 225.72) * mm});
            skLineSegment(sketch, "E13.11.13.2", {"start": v(78.07, 225.72) * mm, "end": v(78.07, 241.12) * mm});
            skLineSegment(sketch, "E13.11.13.3", {"start": v(62.67, 241.12) * mm, "end": v(78.07, 241.12) * mm});
            skLineSegment(sketch, "E13.11.14.0", {"start": v(62.67, 242.32) * mm, "end": v(62.67, 257.72) * mm});
            skLineSegment(sketch, "E13.11.14.1", {"start": v(62.67, 242.32) * mm, "end": v(78.07, 242.32) * mm});
            skLineSegment(sketch, "E13.11.14.2", {"start": v(78.07, 242.32) * mm, "end": v(78.07, 257.72) * mm});
            skLineSegment(sketch, "E13.11.14.3", {"start": v(62.67, 257.72) * mm, "end": v(78.07, 257.72) * mm});
            skLineSegment(sketch, "E13.11.15.0", {"start": v(62.67, 258.92) * mm, "end": v(62.67, 274.32) * mm});
            skLineSegment(sketch, "E13.11.15.1", {"start": v(62.67, 258.92) * mm, "end": v(78.07, 258.92) * mm});
            skLineSegment(sketch, "E13.11.15.2", {"start": v(78.07, 258.92) * mm, "end": v(78.07, 274.32) * mm});
            skLineSegment(sketch, "E13.11.15.3", {"start": v(62.67, 274.32) * mm, "end": v(78.07, 274.32) * mm});
            skLineSegment(sketch, "E13.12.0.0", {"start": v(79.27, 9.92) * mm, "end": v(79.27, 25.32) * mm});
            skLineSegment(sketch, "E13.12.0.1", {"start": v(79.27, 9.92) * mm, "end": v(94.67, 9.92) * mm});
            skLineSegment(sketch, "E13.12.0.2", {"start": v(94.67, 9.92) * mm, "end": v(94.67, 25.32) * mm});
            skLineSegment(sketch, "E13.12.0.3", {"start": v(79.27, 25.32) * mm, "end": v(94.67, 25.32) * mm});
            skLineSegment(sketch, "E13.12.1.0", {"start": v(79.27, 26.52) * mm, "end": v(79.27, 41.92) * mm});
            skLineSegment(sketch, "E13.12.1.1", {"start": v(79.27, 26.52) * mm, "end": v(94.67, 26.52) * mm});
            skLineSegment(sketch, "E13.12.1.2", {"start": v(94.67, 26.52) * mm, "end": v(94.67, 41.92) * mm});
            skLineSegment(sketch, "E13.12.1.3", {"start": v(79.27, 41.92) * mm, "end": v(94.67, 41.92) * mm});
            skLineSegment(sketch, "E13.12.2.0", {"start": v(79.27, 43.12) * mm, "end": v(79.27, 58.52) * mm});
            skLineSegment(sketch, "E13.12.2.1", {"start": v(79.27, 43.12) * mm, "end": v(94.67, 43.12) * mm});
            skLineSegment(sketch, "E13.12.2.2", {"start": v(94.67, 43.12) * mm, "end": v(94.67, 58.52) * mm});
            skLineSegment(sketch, "E13.12.2.3", {"start": v(79.27, 58.52) * mm, "end": v(94.67, 58.52) * mm});
            skLineSegment(sketch, "E13.12.3.0", {"start": v(79.27, 59.72) * mm, "end": v(79.27, 75.12) * mm});
            skLineSegment(sketch, "E13.12.3.1", {"start": v(79.27, 59.72) * mm, "end": v(94.67, 59.72) * mm});
            skLineSegment(sketch, "E13.12.3.2", {"start": v(94.67, 59.72) * mm, "end": v(94.67, 75.12) * mm});
            skLineSegment(sketch, "E13.12.3.3", {"start": v(79.27, 75.12) * mm, "end": v(94.67, 75.12) * mm});
            skLineSegment(sketch, "E13.12.4.0", {"start": v(79.27, 76.32) * mm, "end": v(79.27, 91.72) * mm});
            skLineSegment(sketch, "E13.12.4.1", {"start": v(79.27, 76.32) * mm, "end": v(94.67, 76.32) * mm});
            skLineSegment(sketch, "E13.12.4.2", {"start": v(94.67, 76.32) * mm, "end": v(94.67, 91.72) * mm});
            skLineSegment(sketch, "E13.12.4.3", {"start": v(79.27, 91.72) * mm, "end": v(94.67, 91.72) * mm});
            skLineSegment(sketch, "E13.12.5.0", {"start": v(79.27, 92.92) * mm, "end": v(79.27, 108.32) * mm});
            skLineSegment(sketch, "E13.12.5.1", {"start": v(79.27, 92.92) * mm, "end": v(94.67, 92.92) * mm});
            skLineSegment(sketch, "E13.12.5.2", {"start": v(94.67, 92.92) * mm, "end": v(94.67, 108.32) * mm});
            skLineSegment(sketch, "E13.12.5.3", {"start": v(79.27, 108.32) * mm, "end": v(94.67, 108.32) * mm});
            skLineSegment(sketch, "E13.12.6.0", {"start": v(79.27, 109.52) * mm, "end": v(79.27, 124.92) * mm});
            skLineSegment(sketch, "E13.12.6.1", {"start": v(79.27, 109.52) * mm, "end": v(94.67, 109.52) * mm});
            skLineSegment(sketch, "E13.12.6.2", {"start": v(94.67, 109.52) * mm, "end": v(94.67, 124.92) * mm});
            skLineSegment(sketch, "E13.12.6.3", {"start": v(79.27, 124.92) * mm, "end": v(94.67, 124.92) * mm});
            skLineSegment(sketch, "E13.12.7.0", {"start": v(79.27, 126.12) * mm, "end": v(79.27, 141.52) * mm});
            skLineSegment(sketch, "E13.12.7.1", {"start": v(79.27, 126.12) * mm, "end": v(94.67, 126.12) * mm});
            skLineSegment(sketch, "E13.12.7.2", {"start": v(94.67, 126.12) * mm, "end": v(94.67, 141.52) * mm});
            skLineSegment(sketch, "E13.12.7.3", {"start": v(79.27, 141.52) * mm, "end": v(94.67, 141.52) * mm});
            skLineSegment(sketch, "E13.12.8.0", {"start": v(79.27, 142.72) * mm, "end": v(79.27, 158.12) * mm});
            skLineSegment(sketch, "E13.12.8.1", {"start": v(79.27, 142.72) * mm, "end": v(94.67, 142.72) * mm});
            skLineSegment(sketch, "E13.12.8.2", {"start": v(94.67, 142.72) * mm, "end": v(94.67, 158.12) * mm});
            skLineSegment(sketch, "E13.12.8.3", {"start": v(79.27, 158.12) * mm, "end": v(94.67, 158.12) * mm});
            skLineSegment(sketch, "E13.12.9.0", {"start": v(79.27, 159.32) * mm, "end": v(79.27, 174.72) * mm});
            skLineSegment(sketch, "E13.12.9.1", {"start": v(79.27, 159.32) * mm, "end": v(94.67, 159.32) * mm});
            skLineSegment(sketch, "E13.12.9.2", {"start": v(94.67, 159.32) * mm, "end": v(94.67, 174.72) * mm});
            skLineSegment(sketch, "E13.12.9.3", {"start": v(79.27, 174.72) * mm, "end": v(94.67, 174.72) * mm});
            skLineSegment(sketch, "E13.12.10.0", {"start": v(79.27, 175.92) * mm, "end": v(79.27, 191.32) * mm});
            skLineSegment(sketch, "E13.12.10.1", {"start": v(79.27, 175.92) * mm, "end": v(94.67, 175.92) * mm});
            skLineSegment(sketch, "E13.12.10.2", {"start": v(94.67, 175.92) * mm, "end": v(94.67, 191.32) * mm});
            skLineSegment(sketch, "E13.12.10.3", {"start": v(79.27, 191.32) * mm, "end": v(94.67, 191.32) * mm});
            skLineSegment(sketch, "E13.12.11.0", {"start": v(79.27, 192.52) * mm, "end": v(79.27, 207.92) * mm});
            skLineSegment(sketch, "E13.12.11.1", {"start": v(79.27, 192.52) * mm, "end": v(94.67, 192.52) * mm});
            skLineSegment(sketch, "E13.12.11.2", {"start": v(94.67, 192.52) * mm, "end": v(94.67, 207.92) * mm});
            skLineSegment(sketch, "E13.12.11.3", {"start": v(79.27, 207.92) * mm, "end": v(94.67, 207.92) * mm});
            skLineSegment(sketch, "E13.12.12.0", {"start": v(79.27, 209.12) * mm, "end": v(79.27, 224.52) * mm});
            skLineSegment(sketch, "E13.12.12.1", {"start": v(79.27, 209.12) * mm, "end": v(94.67, 209.12) * mm});
            skLineSegment(sketch, "E13.12.12.2", {"start": v(94.67, 209.12) * mm, "end": v(94.67, 224.52) * mm});
            skLineSegment(sketch, "E13.12.12.3", {"start": v(79.27, 224.52) * mm, "end": v(94.67, 224.52) * mm});
            skLineSegment(sketch, "E13.12.13.0", {"start": v(79.27, 225.72) * mm, "end": v(79.27, 241.12) * mm});
            skLineSegment(sketch, "E13.12.13.1", {"start": v(79.27, 225.72) * mm, "end": v(94.67, 225.72) * mm});
            skLineSegment(sketch, "E13.12.13.2", {"start": v(94.67, 225.72) * mm, "end": v(94.67, 241.12) * mm});
            skLineSegment(sketch, "E13.12.13.3", {"start": v(79.27, 241.12) * mm, "end": v(94.67, 241.12) * mm});
            skLineSegment(sketch, "E13.12.14.0", {"start": v(79.27, 242.32) * mm, "end": v(79.27, 257.72) * mm});
            skLineSegment(sketch, "E13.12.14.1", {"start": v(79.27, 242.32) * mm, "end": v(94.67, 242.32) * mm});
            skLineSegment(sketch, "E13.12.14.2", {"start": v(94.67, 242.32) * mm, "end": v(94.67, 257.72) * mm});
            skLineSegment(sketch, "E13.12.14.3", {"start": v(79.27, 257.72) * mm, "end": v(94.67, 257.72) * mm});
            skLineSegment(sketch, "E13.12.15.0", {"start": v(79.27, 258.92) * mm, "end": v(79.27, 274.32) * mm});
            skLineSegment(sketch, "E13.12.15.1", {"start": v(79.27, 258.92) * mm, "end": v(94.67, 258.92) * mm});
            skLineSegment(sketch, "E13.12.15.2", {"start": v(94.67, 258.92) * mm, "end": v(94.67, 274.32) * mm});
            skLineSegment(sketch, "E13.12.15.3", {"start": v(79.27, 274.32) * mm, "end": v(94.67, 274.32) * mm});
            skLineSegment(sketch, "E13.13.0.0", {"start": v(95.87, 9.92) * mm, "end": v(95.87, 25.32) * mm});
            skLineSegment(sketch, "E13.13.0.1", {"start": v(95.87, 9.92) * mm, "end": v(111.27, 9.92) * mm});
            skLineSegment(sketch, "E13.13.0.2", {"start": v(111.27, 9.92) * mm, "end": v(111.27, 25.32) * mm});
            skLineSegment(sketch, "E13.13.0.3", {"start": v(95.87, 25.32) * mm, "end": v(111.27, 25.32) * mm});
            skLineSegment(sketch, "E13.13.1.0", {"start": v(95.87, 26.52) * mm, "end": v(95.87, 41.92) * mm});
            skLineSegment(sketch, "E13.13.1.1", {"start": v(95.87, 26.52) * mm, "end": v(111.27, 26.52) * mm});
            skLineSegment(sketch, "E13.13.1.2", {"start": v(111.27, 26.52) * mm, "end": v(111.27, 41.92) * mm});
            skLineSegment(sketch, "E13.13.1.3", {"start": v(95.87, 41.92) * mm, "end": v(111.27, 41.92) * mm});
            skLineSegment(sketch, "E13.13.2.0", {"start": v(95.87, 43.12) * mm, "end": v(95.87, 58.52) * mm});
            skLineSegment(sketch, "E13.13.2.1", {"start": v(95.87, 43.12) * mm, "end": v(111.27, 43.12) * mm});
            skLineSegment(sketch, "E13.13.2.2", {"start": v(111.27, 43.12) * mm, "end": v(111.27, 58.52) * mm});
            skLineSegment(sketch, "E13.13.2.3", {"start": v(95.87, 58.52) * mm, "end": v(111.27, 58.52) * mm});
            skLineSegment(sketch, "E13.13.3.0", {"start": v(95.87, 59.72) * mm, "end": v(95.87, 75.12) * mm});
            skLineSegment(sketch, "E13.13.3.1", {"start": v(95.87, 59.72) * mm, "end": v(111.27, 59.72) * mm});
            skLineSegment(sketch, "E13.13.3.2", {"start": v(111.27, 59.72) * mm, "end": v(111.27, 75.12) * mm});
            skLineSegment(sketch, "E13.13.3.3", {"start": v(95.87, 75.12) * mm, "end": v(111.27, 75.12) * mm});
            skLineSegment(sketch, "E13.13.4.0", {"start": v(95.87, 76.32) * mm, "end": v(95.87, 91.72) * mm});
            skLineSegment(sketch, "E13.13.4.1", {"start": v(95.87, 76.32) * mm, "end": v(111.27, 76.32) * mm});
            skLineSegment(sketch, "E13.13.4.2", {"start": v(111.27, 76.32) * mm, "end": v(111.27, 91.72) * mm});
            skLineSegment(sketch, "E13.13.4.3", {"start": v(95.87, 91.72) * mm, "end": v(111.27, 91.72) * mm});
            skLineSegment(sketch, "E13.13.5.0", {"start": v(95.87, 92.92) * mm, "end": v(95.87, 108.32) * mm});
            skLineSegment(sketch, "E13.13.5.1", {"start": v(95.87, 92.92) * mm, "end": v(111.27, 92.92) * mm});
            skLineSegment(sketch, "E13.13.5.2", {"start": v(111.27, 92.92) * mm, "end": v(111.27, 108.32) * mm});
            skLineSegment(sketch, "E13.13.5.3", {"start": v(95.87, 108.32) * mm, "end": v(111.27, 108.32) * mm});
            skLineSegment(sketch, "E13.13.6.0", {"start": v(95.87, 109.52) * mm, "end": v(95.87, 124.92) * mm});
            skLineSegment(sketch, "E13.13.6.1", {"start": v(95.87, 109.52) * mm, "end": v(111.27, 109.52) * mm});
            skLineSegment(sketch, "E13.13.6.2", {"start": v(111.27, 109.52) * mm, "end": v(111.27, 124.92) * mm});
            skLineSegment(sketch, "E13.13.6.3", {"start": v(95.87, 124.92) * mm, "end": v(111.27, 124.92) * mm});
            skLineSegment(sketch, "E13.13.7.0", {"start": v(95.87, 126.12) * mm, "end": v(95.87, 141.52) * mm});
            skLineSegment(sketch, "E13.13.7.1", {"start": v(95.87, 126.12) * mm, "end": v(111.27, 126.12) * mm});
            skLineSegment(sketch, "E13.13.7.2", {"start": v(111.27, 126.12) * mm, "end": v(111.27, 141.52) * mm});
            skLineSegment(sketch, "E13.13.7.3", {"start": v(95.87, 141.52) * mm, "end": v(111.27, 141.52) * mm});
            skLineSegment(sketch, "E13.13.8.0", {"start": v(95.87, 142.72) * mm, "end": v(95.87, 158.12) * mm});
            skLineSegment(sketch, "E13.13.8.1", {"start": v(95.87, 142.72) * mm, "end": v(111.27, 142.72) * mm});
            skLineSegment(sketch, "E13.13.8.2", {"start": v(111.27, 142.72) * mm, "end": v(111.27, 158.12) * mm});
            skLineSegment(sketch, "E13.13.8.3", {"start": v(95.87, 158.12) * mm, "end": v(111.27, 158.12) * mm});
            skLineSegment(sketch, "E13.13.9.0", {"start": v(95.87, 159.32) * mm, "end": v(95.87, 174.72) * mm});
            skLineSegment(sketch, "E13.13.9.1", {"start": v(95.87, 159.32) * mm, "end": v(111.27, 159.32) * mm});
            skLineSegment(sketch, "E13.13.9.2", {"start": v(111.27, 159.32) * mm, "end": v(111.27, 174.72) * mm});
            skLineSegment(sketch, "E13.13.9.3", {"start": v(95.87, 174.72) * mm, "end": v(111.27, 174.72) * mm});
            skLineSegment(sketch, "E13.13.10.0", {"start": v(95.87, 175.92) * mm, "end": v(95.87, 191.32) * mm});
            skLineSegment(sketch, "E13.13.10.1", {"start": v(95.87, 175.92) * mm, "end": v(111.27, 175.92) * mm});
            skLineSegment(sketch, "E13.13.10.2", {"start": v(111.27, 175.92) * mm, "end": v(111.27, 191.32) * mm});
            skLineSegment(sketch, "E13.13.10.3", {"start": v(95.87, 191.32) * mm, "end": v(111.27, 191.32) * mm});
            skLineSegment(sketch, "E13.13.11.0", {"start": v(95.87, 192.52) * mm, "end": v(95.87, 207.92) * mm});
            skLineSegment(sketch, "E13.13.11.1", {"start": v(95.87, 192.52) * mm, "end": v(111.27, 192.52) * mm});
            skLineSegment(sketch, "E13.13.11.2", {"start": v(111.27, 192.52) * mm, "end": v(111.27, 207.92) * mm});
            skLineSegment(sketch, "E13.13.11.3", {"start": v(95.87, 207.92) * mm, "end": v(111.27, 207.92) * mm});
            skLineSegment(sketch, "E13.13.12.0", {"start": v(95.87, 209.12) * mm, "end": v(95.87, 224.52) * mm});
            skLineSegment(sketch, "E13.13.12.1", {"start": v(95.87, 209.12) * mm, "end": v(111.27, 209.12) * mm});
            skLineSegment(sketch, "E13.13.12.2", {"start": v(111.27, 209.12) * mm, "end": v(111.27, 224.52) * mm});
            skLineSegment(sketch, "E13.13.12.3", {"start": v(95.87, 224.52) * mm, "end": v(111.27, 224.52) * mm});
            skLineSegment(sketch, "E13.13.13.0", {"start": v(95.87, 225.72) * mm, "end": v(95.87, 241.12) * mm});
            skLineSegment(sketch, "E13.13.13.1", {"start": v(95.87, 225.72) * mm, "end": v(111.27, 225.72) * mm});
            skLineSegment(sketch, "E13.13.13.2", {"start": v(111.27, 225.72) * mm, "end": v(111.27, 241.12) * mm});
            skLineSegment(sketch, "E13.13.13.3", {"start": v(95.87, 241.12) * mm, "end": v(111.27, 241.12) * mm});
            skLineSegment(sketch, "E13.13.14.0", {"start": v(95.87, 242.32) * mm, "end": v(95.87, 257.72) * mm});
            skLineSegment(sketch, "E13.13.14.1", {"start": v(95.87, 242.32) * mm, "end": v(111.27, 242.32) * mm});
            skLineSegment(sketch, "E13.13.14.2", {"start": v(111.27, 242.32) * mm, "end": v(111.27, 257.72) * mm});
            skLineSegment(sketch, "E13.13.14.3", {"start": v(95.87, 257.72) * mm, "end": v(111.27, 257.72) * mm});
            skLineSegment(sketch, "E13.13.15.0", {"start": v(95.87, 258.92) * mm, "end": v(95.87, 274.32) * mm});
            skLineSegment(sketch, "E13.13.15.1", {"start": v(95.87, 258.92) * mm, "end": v(111.27, 258.92) * mm});
            skLineSegment(sketch, "E13.13.15.2", {"start": v(111.27, 258.92) * mm, "end": v(111.27, 274.32) * mm});
            skLineSegment(sketch, "E13.13.15.3", {"start": v(95.87, 274.32) * mm, "end": v(111.27, 274.32) * mm});
            skLineSegment(sketch, "E13.14.0.0", {"start": v(112.47, 9.92) * mm, "end": v(112.47, 25.32) * mm});
            skLineSegment(sketch, "E13.14.0.1", {"start": v(112.47, 9.92) * mm, "end": v(127.87, 9.92) * mm});
            skLineSegment(sketch, "E13.14.0.2", {"start": v(127.87, 9.92) * mm, "end": v(127.87, 25.32) * mm});
            skLineSegment(sketch, "E13.14.0.3", {"start": v(112.47, 25.32) * mm, "end": v(127.87, 25.32) * mm});
            skLineSegment(sketch, "E13.14.1.0", {"start": v(112.47, 26.52) * mm, "end": v(112.47, 41.92) * mm});
            skLineSegment(sketch, "E13.14.1.1", {"start": v(112.47, 26.52) * mm, "end": v(127.87, 26.52) * mm});
            skLineSegment(sketch, "E13.14.1.2", {"start": v(127.87, 26.52) * mm, "end": v(127.87, 41.92) * mm});
            skLineSegment(sketch, "E13.14.1.3", {"start": v(112.47, 41.92) * mm, "end": v(127.87, 41.92) * mm});
            skLineSegment(sketch, "E13.14.2.0", {"start": v(112.47, 43.12) * mm, "end": v(112.47, 58.52) * mm});
            skLineSegment(sketch, "E13.14.2.1", {"start": v(112.47, 43.12) * mm, "end": v(127.87, 43.12) * mm});
            skLineSegment(sketch, "E13.14.2.2", {"start": v(127.87, 43.12) * mm, "end": v(127.87, 58.52) * mm});
            skLineSegment(sketch, "E13.14.2.3", {"start": v(112.47, 58.52) * mm, "end": v(127.87, 58.52) * mm});
            skLineSegment(sketch, "E13.14.3.0", {"start": v(112.47, 59.72) * mm, "end": v(112.47, 75.12) * mm});
            skLineSegment(sketch, "E13.14.3.1", {"start": v(112.47, 59.72) * mm, "end": v(127.87, 59.72) * mm});
            skLineSegment(sketch, "E13.14.3.2", {"start": v(127.87, 59.72) * mm, "end": v(127.87, 75.12) * mm});
            skLineSegment(sketch, "E13.14.3.3", {"start": v(112.47, 75.12) * mm, "end": v(127.87, 75.12) * mm});
            skLineSegment(sketch, "E13.14.4.0", {"start": v(112.47, 76.32) * mm, "end": v(112.47, 91.72) * mm});
            skLineSegment(sketch, "E13.14.4.1", {"start": v(112.47, 76.32) * mm, "end": v(127.87, 76.32) * mm});
            skLineSegment(sketch, "E13.14.4.2", {"start": v(127.87, 76.32) * mm, "end": v(127.87, 91.72) * mm});
            skLineSegment(sketch, "E13.14.4.3", {"start": v(112.47, 91.72) * mm, "end": v(127.87, 91.72) * mm});
            skLineSegment(sketch, "E13.14.5.0", {"start": v(112.47, 92.92) * mm, "end": v(112.47, 108.32) * mm});
            skLineSegment(sketch, "E13.14.5.1", {"start": v(112.47, 92.92) * mm, "end": v(127.87, 92.92) * mm});
            skLineSegment(sketch, "E13.14.5.2", {"start": v(127.87, 92.92) * mm, "end": v(127.87, 108.32) * mm});
            skLineSegment(sketch, "E13.14.5.3", {"start": v(112.47, 108.32) * mm, "end": v(127.87, 108.32) * mm});
            skLineSegment(sketch, "E13.14.6.0", {"start": v(112.47, 109.52) * mm, "end": v(112.47, 124.92) * mm});
            skLineSegment(sketch, "E13.14.6.1", {"start": v(112.47, 109.52) * mm, "end": v(127.87, 109.52) * mm});
            skLineSegment(sketch, "E13.14.6.2", {"start": v(127.87, 109.52) * mm, "end": v(127.87, 124.92) * mm});
            skLineSegment(sketch, "E13.14.6.3", {"start": v(112.47, 124.92) * mm, "end": v(127.87, 124.92) * mm});
            skLineSegment(sketch, "E13.14.7.0", {"start": v(112.47, 126.12) * mm, "end": v(112.47, 141.52) * mm});
            skLineSegment(sketch, "E13.14.7.1", {"start": v(112.47, 126.12) * mm, "end": v(127.87, 126.12) * mm});
            skLineSegment(sketch, "E13.14.7.2", {"start": v(127.87, 126.12) * mm, "end": v(127.87, 141.52) * mm});
            skLineSegment(sketch, "E13.14.7.3", {"start": v(112.47, 141.52) * mm, "end": v(127.87, 141.52) * mm});
            skLineSegment(sketch, "E13.14.8.0", {"start": v(112.47, 142.72) * mm, "end": v(112.47, 158.12) * mm});
            skLineSegment(sketch, "E13.14.8.1", {"start": v(112.47, 142.72) * mm, "end": v(127.87, 142.72) * mm});
            skLineSegment(sketch, "E13.14.8.2", {"start": v(127.87, 142.72) * mm, "end": v(127.87, 158.12) * mm});
            skLineSegment(sketch, "E13.14.8.3", {"start": v(112.47, 158.12) * mm, "end": v(127.87, 158.12) * mm});
            skLineSegment(sketch, "E13.14.9.0", {"start": v(112.47, 159.32) * mm, "end": v(112.47, 174.72) * mm});
            skLineSegment(sketch, "E13.14.9.1", {"start": v(112.47, 159.32) * mm, "end": v(127.87, 159.32) * mm});
            skLineSegment(sketch, "E13.14.9.2", {"start": v(127.87, 159.32) * mm, "end": v(127.87, 174.72) * mm});
            skLineSegment(sketch, "E13.14.9.3", {"start": v(112.47, 174.72) * mm, "end": v(127.87, 174.72) * mm});
            skLineSegment(sketch, "E13.14.10.0", {"start": v(112.47, 175.92) * mm, "end": v(112.47, 191.32) * mm});
            skLineSegment(sketch, "E13.14.10.1", {"start": v(112.47, 175.92) * mm, "end": v(127.87, 175.92) * mm});
            skLineSegment(sketch, "E13.14.10.2", {"start": v(127.87, 175.92) * mm, "end": v(127.87, 191.32) * mm});
            skLineSegment(sketch, "E13.14.10.3", {"start": v(112.47, 191.32) * mm, "end": v(127.87, 191.32) * mm});
            skLineSegment(sketch, "E13.14.11.0", {"start": v(112.47, 192.52) * mm, "end": v(112.47, 207.92) * mm});
            skLineSegment(sketch, "E13.14.11.1", {"start": v(112.47, 192.52) * mm, "end": v(127.87, 192.52) * mm});
            skLineSegment(sketch, "E13.14.11.2", {"start": v(127.87, 192.52) * mm, "end": v(127.87, 207.92) * mm});
            skLineSegment(sketch, "E13.14.11.3", {"start": v(112.47, 207.92) * mm, "end": v(127.87, 207.92) * mm});
            skLineSegment(sketch, "E13.14.12.0", {"start": v(112.47, 209.12) * mm, "end": v(112.47, 224.52) * mm});
            skLineSegment(sketch, "E13.14.12.1", {"start": v(112.47, 209.12) * mm, "end": v(127.87, 209.12) * mm});
            skLineSegment(sketch, "E13.14.12.2", {"start": v(127.87, 209.12) * mm, "end": v(127.87, 224.52) * mm});
            skLineSegment(sketch, "E13.14.12.3", {"start": v(112.47, 224.52) * mm, "end": v(127.87, 224.52) * mm});
            skLineSegment(sketch, "E13.14.13.0", {"start": v(112.47, 225.72) * mm, "end": v(112.47, 241.12) * mm});
            skLineSegment(sketch, "E13.14.13.1", {"start": v(112.47, 225.72) * mm, "end": v(127.87, 225.72) * mm});
            skLineSegment(sketch, "E13.14.13.2", {"start": v(127.87, 225.72) * mm, "end": v(127.87, 241.12) * mm});
            skLineSegment(sketch, "E13.14.13.3", {"start": v(112.47, 241.12) * mm, "end": v(127.87, 241.12) * mm});
            skLineSegment(sketch, "E13.14.14.0", {"start": v(112.47, 242.32) * mm, "end": v(112.47, 257.72) * mm});
            skLineSegment(sketch, "E13.14.14.1", {"start": v(112.47, 242.32) * mm, "end": v(127.87, 242.32) * mm});
            skLineSegment(sketch, "E13.14.14.2", {"start": v(127.87, 242.32) * mm, "end": v(127.87, 257.72) * mm});
            skLineSegment(sketch, "E13.14.14.3", {"start": v(112.47, 257.72) * mm, "end": v(127.87, 257.72) * mm});
            skLineSegment(sketch, "E13.14.15.0", {"start": v(112.47, 258.92) * mm, "end": v(112.47, 274.32) * mm});
            skLineSegment(sketch, "E13.14.15.1", {"start": v(112.47, 258.92) * mm, "end": v(127.87, 258.92) * mm});
            skLineSegment(sketch, "E13.14.15.2", {"start": v(127.87, 258.92) * mm, "end": v(127.87, 274.32) * mm});
            skLineSegment(sketch, "E13.14.15.3", {"start": v(112.47, 274.32) * mm, "end": v(127.87, 274.32) * mm});
            skLineSegment(sketch, "E13.15.0.0", {"start": v(129.07, 9.92) * mm, "end": v(129.07, 25.32) * mm});
            skLineSegment(sketch, "E13.15.0.1", {"start": v(129.07, 9.92) * mm, "end": v(144.47, 9.92) * mm});
            skLineSegment(sketch, "E13.15.0.2", {"start": v(144.47, 9.92) * mm, "end": v(144.47, 25.32) * mm});
            skLineSegment(sketch, "E13.15.0.3", {"start": v(129.07, 25.32) * mm, "end": v(144.47, 25.32) * mm});
            skLineSegment(sketch, "E13.15.1.0", {"start": v(129.07, 26.52) * mm, "end": v(129.07, 41.92) * mm});
            skLineSegment(sketch, "E13.15.1.1", {"start": v(129.07, 26.52) * mm, "end": v(144.47, 26.52) * mm});
            skLineSegment(sketch, "E13.15.1.2", {"start": v(144.47, 26.52) * mm, "end": v(144.47, 41.92) * mm});
            skLineSegment(sketch, "E13.15.1.3", {"start": v(129.07, 41.92) * mm, "end": v(144.47, 41.92) * mm});
            skLineSegment(sketch, "E13.15.2.0", {"start": v(129.07, 43.12) * mm, "end": v(129.07, 58.52) * mm});
            skLineSegment(sketch, "E13.15.2.1", {"start": v(129.07, 43.12) * mm, "end": v(144.47, 43.12) * mm});
            skLineSegment(sketch, "E13.15.2.2", {"start": v(144.47, 43.12) * mm, "end": v(144.47, 58.52) * mm});
            skLineSegment(sketch, "E13.15.2.3", {"start": v(129.07, 58.52) * mm, "end": v(144.47, 58.52) * mm});
            skLineSegment(sketch, "E13.15.3.0", {"start": v(129.07, 59.72) * mm, "end": v(129.07, 75.12) * mm});
            skLineSegment(sketch, "E13.15.3.1", {"start": v(129.07, 59.72) * mm, "end": v(144.47, 59.72) * mm});
            skLineSegment(sketch, "E13.15.3.2", {"start": v(144.47, 59.72) * mm, "end": v(144.47, 75.12) * mm});
            skLineSegment(sketch, "E13.15.3.3", {"start": v(129.07, 75.12) * mm, "end": v(144.47, 75.12) * mm});
            skLineSegment(sketch, "E13.15.4.0", {"start": v(129.07, 76.32) * mm, "end": v(129.07, 91.72) * mm});
            skLineSegment(sketch, "E13.15.4.1", {"start": v(129.07, 76.32) * mm, "end": v(144.47, 76.32) * mm});
            skLineSegment(sketch, "E13.15.4.2", {"start": v(144.47, 76.32) * mm, "end": v(144.47, 91.72) * mm});
            skLineSegment(sketch, "E13.15.4.3", {"start": v(129.07, 91.72) * mm, "end": v(144.47, 91.72) * mm});
            skLineSegment(sketch, "E13.15.5.0", {"start": v(129.07, 92.92) * mm, "end": v(129.07, 108.32) * mm});
            skLineSegment(sketch, "E13.15.5.1", {"start": v(129.07, 92.92) * mm, "end": v(144.47, 92.92) * mm});
            skLineSegment(sketch, "E13.15.5.2", {"start": v(144.47, 92.92) * mm, "end": v(144.47, 108.32) * mm});
            skLineSegment(sketch, "E13.15.5.3", {"start": v(129.07, 108.32) * mm, "end": v(144.47, 108.32) * mm});
            skLineSegment(sketch, "E13.15.6.0", {"start": v(129.07, 109.52) * mm, "end": v(129.07, 124.92) * mm});
            skLineSegment(sketch, "E13.15.6.1", {"start": v(129.07, 109.52) * mm, "end": v(144.47, 109.52) * mm});
            skLineSegment(sketch, "E13.15.6.2", {"start": v(144.47, 109.52) * mm, "end": v(144.47, 124.92) * mm});
            skLineSegment(sketch, "E13.15.6.3", {"start": v(129.07, 124.92) * mm, "end": v(144.47, 124.92) * mm});
            skLineSegment(sketch, "E13.15.7.0", {"start": v(129.07, 126.12) * mm, "end": v(129.07, 141.52) * mm});
            skLineSegment(sketch, "E13.15.7.1", {"start": v(129.07, 126.12) * mm, "end": v(144.47, 126.12) * mm});
            skLineSegment(sketch, "E13.15.7.2", {"start": v(144.47, 126.12) * mm, "end": v(144.47, 141.52) * mm});
            skLineSegment(sketch, "E13.15.7.3", {"start": v(129.07, 141.52) * mm, "end": v(144.47, 141.52) * mm});
            skLineSegment(sketch, "E13.15.8.0", {"start": v(129.07, 142.72) * mm, "end": v(129.07, 158.12) * mm});
            skLineSegment(sketch, "E13.15.8.1", {"start": v(129.07, 142.72) * mm, "end": v(144.47, 142.72) * mm});
            skLineSegment(sketch, "E13.15.8.2", {"start": v(144.47, 142.72) * mm, "end": v(144.47, 158.12) * mm});
            skLineSegment(sketch, "E13.15.8.3", {"start": v(129.07, 158.12) * mm, "end": v(144.47, 158.12) * mm});
            skLineSegment(sketch, "E13.15.9.0", {"start": v(129.07, 159.32) * mm, "end": v(129.07, 174.72) * mm});
            skLineSegment(sketch, "E13.15.9.1", {"start": v(129.07, 159.32) * mm, "end": v(144.47, 159.32) * mm});
            skLineSegment(sketch, "E13.15.9.2", {"start": v(144.47, 159.32) * mm, "end": v(144.47, 174.72) * mm});
            skLineSegment(sketch, "E13.15.9.3", {"start": v(129.07, 174.72) * mm, "end": v(144.47, 174.72) * mm});
            skLineSegment(sketch, "E13.15.10.0", {"start": v(129.07, 175.92) * mm, "end": v(129.07, 191.32) * mm});
            skLineSegment(sketch, "E13.15.10.1", {"start": v(129.07, 175.92) * mm, "end": v(144.47, 175.92) * mm});
            skLineSegment(sketch, "E13.15.10.2", {"start": v(144.47, 175.92) * mm, "end": v(144.47, 191.32) * mm});
            skLineSegment(sketch, "E13.15.10.3", {"start": v(129.07, 191.32) * mm, "end": v(144.47, 191.32) * mm});
            skLineSegment(sketch, "E13.15.11.0", {"start": v(129.07, 192.52) * mm, "end": v(129.07, 207.92) * mm});
            skLineSegment(sketch, "E13.15.11.1", {"start": v(129.07, 192.52) * mm, "end": v(144.47, 192.52) * mm});
            skLineSegment(sketch, "E13.15.11.2", {"start": v(144.47, 192.52) * mm, "end": v(144.47, 207.92) * mm});
            skLineSegment(sketch, "E13.15.11.3", {"start": v(129.07, 207.92) * mm, "end": v(144.47, 207.92) * mm});
            skLineSegment(sketch, "E13.15.12.0", {"start": v(129.07, 209.12) * mm, "end": v(129.07, 224.52) * mm});
            skLineSegment(sketch, "E13.15.12.1", {"start": v(129.07, 209.12) * mm, "end": v(144.47, 209.12) * mm});
            skLineSegment(sketch, "E13.15.12.2", {"start": v(144.47, 209.12) * mm, "end": v(144.47, 224.52) * mm});
            skLineSegment(sketch, "E13.15.12.3", {"start": v(129.07, 224.52) * mm, "end": v(144.47, 224.52) * mm});
            skLineSegment(sketch, "E13.15.13.0", {"start": v(129.07, 225.72) * mm, "end": v(129.07, 241.12) * mm});
            skLineSegment(sketch, "E13.15.13.1", {"start": v(129.07, 225.72) * mm, "end": v(144.47, 225.72) * mm});
            skLineSegment(sketch, "E13.15.13.2", {"start": v(144.47, 225.72) * mm, "end": v(144.47, 241.12) * mm});
            skLineSegment(sketch, "E13.15.13.3", {"start": v(129.07, 241.12) * mm, "end": v(144.47, 241.12) * mm});
            skLineSegment(sketch, "E13.15.14.0", {"start": v(129.07, 242.32) * mm, "end": v(129.07, 257.72) * mm});
            skLineSegment(sketch, "E13.15.14.1", {"start": v(129.07, 242.32) * mm, "end": v(144.47, 242.32) * mm});
            skLineSegment(sketch, "E13.15.14.2", {"start": v(144.47, 242.32) * mm, "end": v(144.47, 257.72) * mm});
            skLineSegment(sketch, "E13.15.14.3", {"start": v(129.07, 257.72) * mm, "end": v(144.47, 257.72) * mm});
            skLineSegment(sketch, "E13.15.15.0", {"start": v(129.07, 258.92) * mm, "end": v(129.07, 274.32) * mm});
            skLineSegment(sketch, "E13.15.15.1", {"start": v(129.07, 258.92) * mm, "end": v(144.47, 258.92) * mm});
            skLineSegment(sketch, "E13.15.15.2", {"start": v(144.47, 258.92) * mm, "end": v(144.47, 274.32) * mm});
            skLineSegment(sketch, "E13.15.15.3", {"start": v(129.07, 274.32) * mm, "end": v(144.47, 274.32) * mm});
            skLineSegment(sketch, "E13.direction2", {"start": v(-119.93, 9.92) * mm, "end": v(-119.93, 26.52) * mm, "construction": true});
            skLineSegment(sketch, "E14.0.1.1", {"start": v(-120.53, 42.52) * mm, "end": v(-120.53, 25.92) * mm, "construction": true});
            skLineSegment(sketch, "E14.0.1.2", {"start": v(-120.53, 42.52) * mm, "end": v(-103.93, 42.52) * mm, "construction": true});
            skLineSegment(sketch, "E14.0.1.3", {"start": v(-103.93, 42.52) * mm, "end": v(-103.93, 25.92) * mm, "construction": true});
            skLineSegment(sketch, "E14.0.2.0", {"start": v(-120.53, 42.52) * mm, "end": v(-103.93, 42.52) * mm, "construction": true});
            skLineSegment(sketch, "E14.0.2.1", {"start": v(-120.53, 59.12) * mm, "end": v(-120.53, 42.52) * mm, "construction": true});
            skLineSegment(sketch, "E14.0.2.2", {"start": v(-120.53, 59.12) * mm, "end": v(-103.93, 59.12) * mm, "construction": true});
            skLineSegment(sketch, "E14.0.2.3", {"start": v(-103.93, 59.12) * mm, "end": v(-103.93, 42.52) * mm, "construction": true});
            skLineSegment(sketch, "E14.0.3.0", {"start": v(-120.53, 59.12) * mm, "end": v(-103.93, 59.12) * mm, "construction": true});
            skLineSegment(sketch, "E14.0.3.1", {"start": v(-120.53, 75.72) * mm, "end": v(-120.53, 59.12) * mm, "construction": true});
            skLineSegment(sketch, "E14.0.3.2", {"start": v(-120.53, 75.72) * mm, "end": v(-103.93, 75.72) * mm, "construction": true});
            skLineSegment(sketch, "E14.0.3.3", {"start": v(-103.93, 75.72) * mm, "end": v(-103.93, 59.12) * mm, "construction": true});
            skLineSegment(sketch, "E14.0.4.0", {"start": v(-120.53, 75.72) * mm, "end": v(-103.93, 75.72) * mm, "construction": true});
            skLineSegment(sketch, "E14.0.4.1", {"start": v(-120.53, 92.32) * mm, "end": v(-120.53, 75.72) * mm, "construction": true});
            skLineSegment(sketch, "E14.0.4.2", {"start": v(-120.53, 92.32) * mm, "end": v(-103.93, 92.32) * mm, "construction": true});
            skLineSegment(sketch, "E14.0.4.3", {"start": v(-103.93, 92.32) * mm, "end": v(-103.93, 75.72) * mm, "construction": true});
            skLineSegment(sketch, "E14.0.5.0", {"start": v(-120.53, 92.32) * mm, "end": v(-103.93, 92.32) * mm, "construction": true});
            skLineSegment(sketch, "E14.0.5.1", {"start": v(-120.53, 108.92) * mm, "end": v(-120.53, 92.32) * mm, "construction": true});
            skLineSegment(sketch, "E14.0.5.2", {"start": v(-120.53, 108.92) * mm, "end": v(-103.93, 108.92) * mm, "construction": true});
            skLineSegment(sketch, "E14.0.5.3", {"start": v(-103.93, 108.92) * mm, "end": v(-103.93, 92.32) * mm, "construction": true});
            skLineSegment(sketch, "E14.0.6.0", {"start": v(-120.53, 108.92) * mm, "end": v(-103.93, 108.92) * mm, "construction": true});
            skLineSegment(sketch, "E14.0.6.1", {"start": v(-120.53, 125.52) * mm, "end": v(-120.53, 108.92) * mm, "construction": true});
            skLineSegment(sketch, "E14.0.6.2", {"start": v(-120.53, 125.52) * mm, "end": v(-103.93, 125.52) * mm, "construction": true});
            skLineSegment(sketch, "E14.0.6.3", {"start": v(-103.93, 125.52) * mm, "end": v(-103.93, 108.92) * mm, "construction": true});
            skLineSegment(sketch, "E14.0.7.0", {"start": v(-120.53, 125.52) * mm, "end": v(-103.93, 125.52) * mm, "construction": true});
            skLineSegment(sketch, "E14.0.7.1", {"start": v(-120.53, 142.12) * mm, "end": v(-120.53, 125.52) * mm, "construction": true});
            skLineSegment(sketch, "E14.0.7.2", {"start": v(-120.53, 142.12) * mm, "end": v(-103.93, 142.12) * mm, "construction": true});
            skLineSegment(sketch, "E14.0.7.3", {"start": v(-103.93, 142.12) * mm, "end": v(-103.93, 125.52) * mm, "construction": true});
            skLineSegment(sketch, "E14.0.8.0", {"start": v(-120.53, 142.12) * mm, "end": v(-103.93, 142.12) * mm, "construction": true});
            skLineSegment(sketch, "E14.0.8.1", {"start": v(-120.53, 158.72) * mm, "end": v(-120.53, 142.12) * mm, "construction": true});
            skLineSegment(sketch, "E14.0.8.2", {"start": v(-120.53, 158.72) * mm, "end": v(-103.93, 158.72) * mm, "construction": true});
            skLineSegment(sketch, "E14.0.8.3", {"start": v(-103.93, 158.72) * mm, "end": v(-103.93, 142.12) * mm, "construction": true});
            skLineSegment(sketch, "E14.0.9.0", {"start": v(-120.53, 158.72) * mm, "end": v(-103.93, 158.72) * mm, "construction": true});
            skLineSegment(sketch, "E14.0.9.1", {"start": v(-120.53, 175.32) * mm, "end": v(-120.53, 158.72) * mm, "construction": true});
            skLineSegment(sketch, "E14.0.9.2", {"start": v(-120.53, 175.32) * mm, "end": v(-103.93, 175.32) * mm, "construction": true});
            skLineSegment(sketch, "E14.0.9.3", {"start": v(-103.93, 175.32) * mm, "end": v(-103.93, 158.72) * mm, "construction": true});
            skLineSegment(sketch, "E14.0.10.0", {"start": v(-120.53, 175.32) * mm, "end": v(-103.93, 175.32) * mm, "construction": true});
            skLineSegment(sketch, "E14.0.10.1", {"start": v(-120.53, 191.92) * mm, "end": v(-120.53, 175.32) * mm, "construction": true});
            skLineSegment(sketch, "E14.0.10.2", {"start": v(-120.53, 191.92) * mm, "end": v(-103.93, 191.92) * mm, "construction": true});
            skLineSegment(sketch, "E14.0.10.3", {"start": v(-103.93, 191.92) * mm, "end": v(-103.93, 175.32) * mm, "construction": true});
            skLineSegment(sketch, "E14.0.11.0", {"start": v(-120.53, 191.92) * mm, "end": v(-103.93, 191.92) * mm, "construction": true});
            skLineSegment(sketch, "E14.0.11.1", {"start": v(-120.53, 208.52) * mm, "end": v(-120.53, 191.92) * mm, "construction": true});
            skLineSegment(sketch, "E14.0.11.2", {"start": v(-120.53, 208.52) * mm, "end": v(-103.93, 208.52) * mm, "construction": true});
            skLineSegment(sketch, "E14.0.11.3", {"start": v(-103.93, 208.52) * mm, "end": v(-103.93, 191.92) * mm, "construction": true});
            skLineSegment(sketch, "E14.0.12.0", {"start": v(-120.53, 208.52) * mm, "end": v(-103.93, 208.52) * mm, "construction": true});
            skLineSegment(sketch, "E14.0.12.1", {"start": v(-120.53, 225.12) * mm, "end": v(-120.53, 208.52) * mm, "construction": true});
            skLineSegment(sketch, "E14.0.12.2", {"start": v(-120.53, 225.12) * mm, "end": v(-103.93, 225.12) * mm, "construction": true});
            skLineSegment(sketch, "E14.0.12.3", {"start": v(-103.93, 225.12) * mm, "end": v(-103.93, 208.52) * mm, "construction": true});
            skLineSegment(sketch, "E14.0.13.0", {"start": v(-120.53, 225.12) * mm, "end": v(-103.93, 225.12) * mm, "construction": true});
            skLineSegment(sketch, "E14.0.13.1", {"start": v(-120.53, 241.72) * mm, "end": v(-120.53, 225.12) * mm, "construction": true});
            skLineSegment(sketch, "E14.0.13.2", {"start": v(-120.53, 241.72) * mm, "end": v(-103.93, 241.72) * mm, "construction": true});
            skLineSegment(sketch, "E14.0.13.3", {"start": v(-103.93, 241.72) * mm, "end": v(-103.93, 225.12) * mm, "construction": true});
            skLineSegment(sketch, "E14.0.14.0", {"start": v(-120.53, 241.72) * mm, "end": v(-103.93, 241.72) * mm, "construction": true});
            skLineSegment(sketch, "E14.0.14.1", {"start": v(-120.53, 258.32) * mm, "end": v(-120.53, 241.72) * mm, "construction": true});
            skLineSegment(sketch, "E14.0.14.2", {"start": v(-120.53, 258.32) * mm, "end": v(-103.93, 258.32) * mm, "construction": true});
            skLineSegment(sketch, "E14.0.14.3", {"start": v(-103.93, 258.32) * mm, "end": v(-103.93, 241.72) * mm, "construction": true});
            skLineSegment(sketch, "E14.0.15.0", {"start": v(-120.53, 258.32) * mm, "end": v(-103.93, 258.32) * mm, "construction": true});
            skLineSegment(sketch, "E14.0.15.1", {"start": v(-120.53, 274.92) * mm, "end": v(-120.53, 258.32) * mm, "construction": true});
            skLineSegment(sketch, "E14.0.15.2", {"start": v(-120.53, 274.92) * mm, "end": v(-103.93, 274.92) * mm, "construction": true});
            skLineSegment(sketch, "E14.0.15.3", {"start": v(-103.93, 274.92) * mm, "end": v(-103.93, 258.32) * mm, "construction": true});
            skLineSegment(sketch, "E14.1.0.0", {"start": v(-103.93, 9.32) * mm, "end": v(-87.33, 9.32) * mm, "construction": true});
            skLineSegment(sketch, "E14.1.0.2", {"start": v(-103.93, 25.92) * mm, "end": v(-87.33, 25.92) * mm, "construction": true});
            skLineSegment(sketch, "E14.1.0.3", {"start": v(-87.33, 25.92) * mm, "end": v(-87.33, 9.32) * mm, "construction": true});
            skLineSegment(sketch, "E14.1.1.0", {"start": v(-103.93, 25.92) * mm, "end": v(-87.33, 25.92) * mm, "construction": true});
            skLineSegment(sketch, "E14.1.1.1", {"start": v(-103.93, 42.52) * mm, "end": v(-103.93, 25.92) * mm, "construction": true});
            skLineSegment(sketch, "E14.1.1.2", {"start": v(-103.93, 42.52) * mm, "end": v(-87.33, 42.52) * mm, "construction": true});
            skLineSegment(sketch, "E14.1.1.3", {"start": v(-87.33, 42.52) * mm, "end": v(-87.33, 25.92) * mm, "construction": true});
            skLineSegment(sketch, "E14.1.2.0", {"start": v(-103.93, 42.52) * mm, "end": v(-87.33, 42.52) * mm, "construction": true});
            skLineSegment(sketch, "E14.1.2.1", {"start": v(-103.93, 59.12) * mm, "end": v(-103.93, 42.52) * mm, "construction": true});
            skLineSegment(sketch, "E14.1.2.2", {"start": v(-103.93, 59.12) * mm, "end": v(-87.33, 59.12) * mm, "construction": true});
            skLineSegment(sketch, "E14.1.2.3", {"start": v(-87.33, 59.12) * mm, "end": v(-87.33, 42.52) * mm, "construction": true});
            skLineSegment(sketch, "E14.1.3.0", {"start": v(-103.93, 59.12) * mm, "end": v(-87.33, 59.12) * mm, "construction": true});
            skLineSegment(sketch, "E14.1.3.1", {"start": v(-103.93, 75.72) * mm, "end": v(-103.93, 59.12) * mm, "construction": true});
            skLineSegment(sketch, "E14.1.3.2", {"start": v(-103.93, 75.72) * mm, "end": v(-87.33, 75.72) * mm, "construction": true});
            skLineSegment(sketch, "E14.1.3.3", {"start": v(-87.33, 75.72) * mm, "end": v(-87.33, 59.12) * mm, "construction": true});
            skLineSegment(sketch, "E14.1.4.0", {"start": v(-103.93, 75.72) * mm, "end": v(-87.33, 75.72) * mm, "construction": true});
            skLineSegment(sketch, "E14.1.4.1", {"start": v(-103.93, 92.32) * mm, "end": v(-103.93, 75.72) * mm, "construction": true});
            skLineSegment(sketch, "E14.1.4.2", {"start": v(-103.93, 92.32) * mm, "end": v(-87.33, 92.32) * mm, "construction": true});
            skLineSegment(sketch, "E14.1.4.3", {"start": v(-87.33, 92.32) * mm, "end": v(-87.33, 75.72) * mm, "construction": true});
            skLineSegment(sketch, "E14.1.5.0", {"start": v(-103.93, 92.32) * mm, "end": v(-87.33, 92.32) * mm, "construction": true});
            skLineSegment(sketch, "E14.1.5.1", {"start": v(-103.93, 108.92) * mm, "end": v(-103.93, 92.32) * mm, "construction": true});
            skLineSegment(sketch, "E14.1.5.2", {"start": v(-103.93, 108.92) * mm, "end": v(-87.33, 108.92) * mm, "construction": true});
            skLineSegment(sketch, "E14.1.5.3", {"start": v(-87.33, 108.92) * mm, "end": v(-87.33, 92.32) * mm, "construction": true});
            skLineSegment(sketch, "E14.1.6.0", {"start": v(-103.93, 108.92) * mm, "end": v(-87.33, 108.92) * mm, "construction": true});
            skLineSegment(sketch, "E14.1.6.1", {"start": v(-103.93, 125.52) * mm, "end": v(-103.93, 108.92) * mm, "construction": true});
            skLineSegment(sketch, "E14.1.6.2", {"start": v(-103.93, 125.52) * mm, "end": v(-87.33, 125.52) * mm, "construction": true});
            skLineSegment(sketch, "E14.1.6.3", {"start": v(-87.33, 125.52) * mm, "end": v(-87.33, 108.92) * mm, "construction": true});
            skLineSegment(sketch, "E14.1.7.0", {"start": v(-103.93, 125.52) * mm, "end": v(-87.33, 125.52) * mm, "construction": true});
            skLineSegment(sketch, "E14.1.7.1", {"start": v(-103.93, 142.12) * mm, "end": v(-103.93, 125.52) * mm, "construction": true});
            skLineSegment(sketch, "E14.1.7.2", {"start": v(-103.93, 142.12) * mm, "end": v(-87.33, 142.12) * mm, "construction": true});
            skLineSegment(sketch, "E14.1.7.3", {"start": v(-87.33, 142.12) * mm, "end": v(-87.33, 125.52) * mm, "construction": true});
            skLineSegment(sketch, "E14.1.8.0", {"start": v(-103.93, 142.12) * mm, "end": v(-87.33, 142.12) * mm, "construction": true});
            skLineSegment(sketch, "E14.1.8.1", {"start": v(-103.93, 158.72) * mm, "end": v(-103.93, 142.12) * mm, "construction": true});
            skLineSegment(sketch, "E14.1.8.2", {"start": v(-103.93, 158.72) * mm, "end": v(-87.33, 158.72) * mm, "construction": true});
            skLineSegment(sketch, "E14.1.8.3", {"start": v(-87.33, 158.72) * mm, "end": v(-87.33, 142.12) * mm, "construction": true});
            skLineSegment(sketch, "E14.1.9.0", {"start": v(-103.93, 158.72) * mm, "end": v(-87.33, 158.72) * mm, "construction": true});
            skLineSegment(sketch, "E14.1.9.1", {"start": v(-103.93, 175.32) * mm, "end": v(-103.93, 158.72) * mm, "construction": true});
            skLineSegment(sketch, "E14.1.9.2", {"start": v(-103.93, 175.32) * mm, "end": v(-87.33, 175.32) * mm, "construction": true});
            skLineSegment(sketch, "E14.1.9.3", {"start": v(-87.33, 175.32) * mm, "end": v(-87.33, 158.72) * mm, "construction": true});
            skLineSegment(sketch, "E14.1.10.0", {"start": v(-103.93, 175.32) * mm, "end": v(-87.33, 175.32) * mm, "construction": true});
            skLineSegment(sketch, "E14.1.10.1", {"start": v(-103.93, 191.92) * mm, "end": v(-103.93, 175.32) * mm, "construction": true});
            skLineSegment(sketch, "E14.1.10.2", {"start": v(-103.93, 191.92) * mm, "end": v(-87.33, 191.92) * mm, "construction": true});
            skLineSegment(sketch, "E14.1.10.3", {"start": v(-87.33, 191.92) * mm, "end": v(-87.33, 175.32) * mm, "construction": true});
            skLineSegment(sketch, "E14.1.11.0", {"start": v(-103.93, 191.92) * mm, "end": v(-87.33, 191.92) * mm, "construction": true});
            skLineSegment(sketch, "E14.1.11.1", {"start": v(-103.93, 208.52) * mm, "end": v(-103.93, 191.92) * mm, "construction": true});
            skLineSegment(sketch, "E14.1.11.2", {"start": v(-103.93, 208.52) * mm, "end": v(-87.33, 208.52) * mm, "construction": true});
            skLineSegment(sketch, "E14.1.11.3", {"start": v(-87.33, 208.52) * mm, "end": v(-87.33, 191.92) * mm, "construction": true});
            skLineSegment(sketch, "E14.1.12.0", {"start": v(-103.93, 208.52) * mm, "end": v(-87.33, 208.52) * mm, "construction": true});
            skLineSegment(sketch, "E14.1.12.1", {"start": v(-103.93, 225.12) * mm, "end": v(-103.93, 208.52) * mm, "construction": true});
            skLineSegment(sketch, "E14.1.12.2", {"start": v(-103.93, 225.12) * mm, "end": v(-87.33, 225.12) * mm, "construction": true});
            skLineSegment(sketch, "E14.1.12.3", {"start": v(-87.33, 225.12) * mm, "end": v(-87.33, 208.52) * mm, "construction": true});
            skLineSegment(sketch, "E14.1.13.0", {"start": v(-103.93, 225.12) * mm, "end": v(-87.33, 225.12) * mm, "construction": true});
            skLineSegment(sketch, "E14.1.13.1", {"start": v(-103.93, 241.72) * mm, "end": v(-103.93, 225.12) * mm, "construction": true});
            skLineSegment(sketch, "E14.1.13.2", {"start": v(-103.93, 241.72) * mm, "end": v(-87.33, 241.72) * mm, "construction": true});
            skLineSegment(sketch, "E14.1.13.3", {"start": v(-87.33, 241.72) * mm, "end": v(-87.33, 225.12) * mm, "construction": true});
            skLineSegment(sketch, "E14.1.14.0", {"start": v(-103.93, 241.72) * mm, "end": v(-87.33, 241.72) * mm, "construction": true});
            skLineSegment(sketch, "E14.1.14.1", {"start": v(-103.93, 258.32) * mm, "end": v(-103.93, 241.72) * mm, "construction": true});
            skLineSegment(sketch, "E14.1.14.2", {"start": v(-103.93, 258.32) * mm, "end": v(-87.33, 258.32) * mm, "construction": true});
            skLineSegment(sketch, "E14.1.14.3", {"start": v(-87.33, 258.32) * mm, "end": v(-87.33, 241.72) * mm, "construction": true});
            skLineSegment(sketch, "E14.1.15.0", {"start": v(-103.93, 258.32) * mm, "end": v(-87.33, 258.32) * mm, "construction": true});
            skLineSegment(sketch, "E14.1.15.1", {"start": v(-103.93, 274.92) * mm, "end": v(-103.93, 258.32) * mm, "construction": true});
            skLineSegment(sketch, "E14.1.15.2", {"start": v(-103.93, 274.92) * mm, "end": v(-87.33, 274.92) * mm, "construction": true});
            skLineSegment(sketch, "E14.1.15.3", {"start": v(-87.33, 274.92) * mm, "end": v(-87.33, 258.32) * mm, "construction": true});
            skLineSegment(sketch, "E14.2.0.0", {"start": v(-87.33, 9.32) * mm, "end": v(-70.73, 9.32) * mm, "construction": true});
            skLineSegment(sketch, "E14.2.0.1", {"start": v(-87.33, 25.92) * mm, "end": v(-87.33, 9.32) * mm, "construction": true});
            skLineSegment(sketch, "E14.2.0.2", {"start": v(-87.33, 25.92) * mm, "end": v(-70.73, 25.92) * mm, "construction": true});
            skLineSegment(sketch, "E14.2.0.3", {"start": v(-70.73, 25.92) * mm, "end": v(-70.73, 9.32) * mm, "construction": true});
            skLineSegment(sketch, "E14.2.1.0", {"start": v(-87.33, 25.92) * mm, "end": v(-70.73, 25.92) * mm, "construction": true});
            skLineSegment(sketch, "E14.2.1.1", {"start": v(-87.33, 42.52) * mm, "end": v(-87.33, 25.92) * mm, "construction": true});
            skLineSegment(sketch, "E14.2.1.2", {"start": v(-87.33, 42.52) * mm, "end": v(-70.73, 42.52) * mm, "construction": true});
            skLineSegment(sketch, "E14.2.1.3", {"start": v(-70.73, 42.52) * mm, "end": v(-70.73, 25.92) * mm, "construction": true});
            skLineSegment(sketch, "E14.2.2.0", {"start": v(-87.33, 42.52) * mm, "end": v(-70.73, 42.52) * mm, "construction": true});
            skLineSegment(sketch, "E14.2.2.1", {"start": v(-87.33, 59.12) * mm, "end": v(-87.33, 42.52) * mm, "construction": true});
            skLineSegment(sketch, "E14.2.2.2", {"start": v(-87.33, 59.12) * mm, "end": v(-70.73, 59.12) * mm, "construction": true});
            skLineSegment(sketch, "E14.2.2.3", {"start": v(-70.73, 59.12) * mm, "end": v(-70.73, 42.52) * mm, "construction": true});
            skLineSegment(sketch, "E14.2.3.0", {"start": v(-87.33, 59.12) * mm, "end": v(-70.73, 59.12) * mm, "construction": true});
            skLineSegment(sketch, "E14.2.3.1", {"start": v(-87.33, 75.72) * mm, "end": v(-87.33, 59.12) * mm, "construction": true});
            skLineSegment(sketch, "E14.2.3.2", {"start": v(-87.33, 75.72) * mm, "end": v(-70.73, 75.72) * mm, "construction": true});
            skLineSegment(sketch, "E14.2.3.3", {"start": v(-70.73, 75.72) * mm, "end": v(-70.73, 59.12) * mm, "construction": true});
            skLineSegment(sketch, "E14.2.4.0", {"start": v(-87.33, 75.72) * mm, "end": v(-70.73, 75.72) * mm, "construction": true});
            skLineSegment(sketch, "E14.2.4.1", {"start": v(-87.33, 92.32) * mm, "end": v(-87.33, 75.72) * mm, "construction": true});
            skLineSegment(sketch, "E14.2.4.2", {"start": v(-87.33, 92.32) * mm, "end": v(-70.73, 92.32) * mm, "construction": true});
            skLineSegment(sketch, "E14.2.4.3", {"start": v(-70.73, 92.32) * mm, "end": v(-70.73, 75.72) * mm, "construction": true});
            skLineSegment(sketch, "E14.2.5.0", {"start": v(-87.33, 92.32) * mm, "end": v(-70.73, 92.32) * mm, "construction": true});
            skLineSegment(sketch, "E14.2.5.1", {"start": v(-87.33, 108.92) * mm, "end": v(-87.33, 92.32) * mm, "construction": true});
            skLineSegment(sketch, "E14.2.5.2", {"start": v(-87.33, 108.92) * mm, "end": v(-70.73, 108.92) * mm, "construction": true});
            skLineSegment(sketch, "E14.2.5.3", {"start": v(-70.73, 108.92) * mm, "end": v(-70.73, 92.32) * mm, "construction": true});
            skLineSegment(sketch, "E14.2.6.0", {"start": v(-87.33, 108.92) * mm, "end": v(-70.73, 108.92) * mm, "construction": true});
            skLineSegment(sketch, "E14.2.6.1", {"start": v(-87.33, 125.52) * mm, "end": v(-87.33, 108.92) * mm, "construction": true});
            skLineSegment(sketch, "E14.2.6.2", {"start": v(-87.33, 125.52) * mm, "end": v(-70.73, 125.52) * mm, "construction": true});
            skLineSegment(sketch, "E14.2.6.3", {"start": v(-70.73, 125.52) * mm, "end": v(-70.73, 108.92) * mm, "construction": true});
            skLineSegment(sketch, "E14.2.7.0", {"start": v(-87.33, 125.52) * mm, "end": v(-70.73, 125.52) * mm, "construction": true});
            skLineSegment(sketch, "E14.2.7.1", {"start": v(-87.33, 142.12) * mm, "end": v(-87.33, 125.52) * mm, "construction": true});
            skLineSegment(sketch, "E14.2.7.2", {"start": v(-87.33, 142.12) * mm, "end": v(-70.73, 142.12) * mm, "construction": true});
            skLineSegment(sketch, "E14.2.7.3", {"start": v(-70.73, 142.12) * mm, "end": v(-70.73, 125.52) * mm, "construction": true});
            skLineSegment(sketch, "E14.2.8.0", {"start": v(-87.33, 142.12) * mm, "end": v(-70.73, 142.12) * mm, "construction": true});
            skLineSegment(sketch, "E14.2.8.1", {"start": v(-87.33, 158.72) * mm, "end": v(-87.33, 142.12) * mm, "construction": true});
            skLineSegment(sketch, "E14.2.8.2", {"start": v(-87.33, 158.72) * mm, "end": v(-70.73, 158.72) * mm, "construction": true});
            skLineSegment(sketch, "E14.2.8.3", {"start": v(-70.73, 158.72) * mm, "end": v(-70.73, 142.12) * mm, "construction": true});
            skLineSegment(sketch, "E14.2.9.0", {"start": v(-87.33, 158.72) * mm, "end": v(-70.73, 158.72) * mm, "construction": true});
            skLineSegment(sketch, "E14.2.9.1", {"start": v(-87.33, 175.32) * mm, "end": v(-87.33, 158.72) * mm, "construction": true});
            skLineSegment(sketch, "E14.2.9.2", {"start": v(-87.33, 175.32) * mm, "end": v(-70.73, 175.32) * mm, "construction": true});
            skLineSegment(sketch, "E14.2.9.3", {"start": v(-70.73, 175.32) * mm, "end": v(-70.73, 158.72) * mm, "construction": true});
            skLineSegment(sketch, "E14.2.10.0", {"start": v(-87.33, 175.32) * mm, "end": v(-70.73, 175.32) * mm, "construction": true});
            skLineSegment(sketch, "E14.2.10.1", {"start": v(-87.33, 191.92) * mm, "end": v(-87.33, 175.32) * mm, "construction": true});
            skLineSegment(sketch, "E14.2.10.2", {"start": v(-87.33, 191.92) * mm, "end": v(-70.73, 191.92) * mm, "construction": true});
            skLineSegment(sketch, "E14.2.10.3", {"start": v(-70.73, 191.92) * mm, "end": v(-70.73, 175.32) * mm, "construction": true});
            skLineSegment(sketch, "E14.2.11.0", {"start": v(-87.33, 191.92) * mm, "end": v(-70.73, 191.92) * mm, "construction": true});
            skLineSegment(sketch, "E14.2.11.1", {"start": v(-87.33, 208.52) * mm, "end": v(-87.33, 191.92) * mm, "construction": true});
            skLineSegment(sketch, "E14.2.11.2", {"start": v(-87.33, 208.52) * mm, "end": v(-70.73, 208.52) * mm, "construction": true});
            skLineSegment(sketch, "E14.2.11.3", {"start": v(-70.73, 208.52) * mm, "end": v(-70.73, 191.92) * mm, "construction": true});
            skLineSegment(sketch, "E14.2.12.0", {"start": v(-87.33, 208.52) * mm, "end": v(-70.73, 208.52) * mm, "construction": true});
            skLineSegment(sketch, "E14.2.12.1", {"start": v(-87.33, 225.12) * mm, "end": v(-87.33, 208.52) * mm, "construction": true});
            skLineSegment(sketch, "E14.2.12.2", {"start": v(-87.33, 225.12) * mm, "end": v(-70.73, 225.12) * mm, "construction": true});
            skLineSegment(sketch, "E14.2.12.3", {"start": v(-70.73, 225.12) * mm, "end": v(-70.73, 208.52) * mm, "construction": true});
            skLineSegment(sketch, "E14.2.13.0", {"start": v(-87.33, 225.12) * mm, "end": v(-70.73, 225.12) * mm, "construction": true});
            skLineSegment(sketch, "E14.2.13.1", {"start": v(-87.33, 241.72) * mm, "end": v(-87.33, 225.12) * mm, "construction": true});
            skLineSegment(sketch, "E14.2.13.2", {"start": v(-87.33, 241.72) * mm, "end": v(-70.73, 241.72) * mm, "construction": true});
            skLineSegment(sketch, "E14.2.13.3", {"start": v(-70.73, 241.72) * mm, "end": v(-70.73, 225.12) * mm, "construction": true});
            skLineSegment(sketch, "E14.2.14.0", {"start": v(-87.33, 241.72) * mm, "end": v(-70.73, 241.72) * mm, "construction": true});
            skLineSegment(sketch, "E14.2.14.1", {"start": v(-87.33, 258.32) * mm, "end": v(-87.33, 241.72) * mm, "construction": true});
            skLineSegment(sketch, "E14.2.14.2", {"start": v(-87.33, 258.32) * mm, "end": v(-70.73, 258.32) * mm, "construction": true});
            skLineSegment(sketch, "E14.2.14.3", {"start": v(-70.73, 258.32) * mm, "end": v(-70.73, 241.72) * mm, "construction": true});
            skLineSegment(sketch, "E14.2.15.0", {"start": v(-87.33, 258.32) * mm, "end": v(-70.73, 258.32) * mm, "construction": true});
            skLineSegment(sketch, "E14.2.15.1", {"start": v(-87.33, 274.92) * mm, "end": v(-87.33, 258.32) * mm, "construction": true});
            skLineSegment(sketch, "E14.2.15.2", {"start": v(-87.33, 274.92) * mm, "end": v(-70.73, 274.92) * mm, "construction": true});
            skLineSegment(sketch, "E14.2.15.3", {"start": v(-70.73, 274.92) * mm, "end": v(-70.73, 258.32) * mm, "construction": true});
            skLineSegment(sketch, "E14.3.0.0", {"start": v(-70.73, 9.32) * mm, "end": v(-54.13, 9.32) * mm, "construction": true});
            skLineSegment(sketch, "E14.3.0.1", {"start": v(-70.73, 25.92) * mm, "end": v(-70.73, 9.32) * mm, "construction": true});
            skLineSegment(sketch, "E14.3.0.2", {"start": v(-70.73, 25.92) * mm, "end": v(-54.13, 25.92) * mm, "construction": true});
            skLineSegment(sketch, "E14.3.0.3", {"start": v(-54.13, 25.92) * mm, "end": v(-54.13, 9.32) * mm, "construction": true});
            skLineSegment(sketch, "E14.3.1.0", {"start": v(-70.73, 25.92) * mm, "end": v(-54.13, 25.92) * mm, "construction": true});
            skLineSegment(sketch, "E14.3.1.1", {"start": v(-70.73, 42.52) * mm, "end": v(-70.73, 25.92) * mm, "construction": true});
            skLineSegment(sketch, "E14.3.1.2", {"start": v(-70.73, 42.52) * mm, "end": v(-54.13, 42.52) * mm, "construction": true});
            skLineSegment(sketch, "E14.3.1.3", {"start": v(-54.13, 42.52) * mm, "end": v(-54.13, 25.92) * mm, "construction": true});
            skLineSegment(sketch, "E14.3.2.0", {"start": v(-70.73, 42.52) * mm, "end": v(-54.13, 42.52) * mm, "construction": true});
            skLineSegment(sketch, "E14.3.2.1", {"start": v(-70.73, 59.12) * mm, "end": v(-70.73, 42.52) * mm, "construction": true});
            skLineSegment(sketch, "E14.3.2.2", {"start": v(-70.73, 59.12) * mm, "end": v(-54.13, 59.12) * mm, "construction": true});
            skLineSegment(sketch, "E14.3.2.3", {"start": v(-54.13, 59.12) * mm, "end": v(-54.13, 42.52) * mm, "construction": true});
            skLineSegment(sketch, "E14.3.3.0", {"start": v(-70.73, 59.12) * mm, "end": v(-54.13, 59.12) * mm, "construction": true});
            skLineSegment(sketch, "E14.3.3.1", {"start": v(-70.73, 75.72) * mm, "end": v(-70.73, 59.12) * mm, "construction": true});
            skLineSegment(sketch, "E14.3.3.2", {"start": v(-70.73, 75.72) * mm, "end": v(-54.13, 75.72) * mm, "construction": true});
            skLineSegment(sketch, "E14.3.3.3", {"start": v(-54.13, 75.72) * mm, "end": v(-54.13, 59.12) * mm, "construction": true});
            skLineSegment(sketch, "E14.3.4.0", {"start": v(-70.73, 75.72) * mm, "end": v(-54.13, 75.72) * mm, "construction": true});
            skLineSegment(sketch, "E14.3.4.1", {"start": v(-70.73, 92.32) * mm, "end": v(-70.73, 75.72) * mm, "construction": true});
            skLineSegment(sketch, "E14.3.4.2", {"start": v(-70.73, 92.32) * mm, "end": v(-54.13, 92.32) * mm, "construction": true});
            skLineSegment(sketch, "E14.3.4.3", {"start": v(-54.13, 92.32) * mm, "end": v(-54.13, 75.72) * mm, "construction": true});
            skLineSegment(sketch, "E14.3.5.0", {"start": v(-70.73, 92.32) * mm, "end": v(-54.13, 92.32) * mm, "construction": true});
            skLineSegment(sketch, "E14.3.5.1", {"start": v(-70.73, 108.92) * mm, "end": v(-70.73, 92.32) * mm, "construction": true});
            skLineSegment(sketch, "E14.3.5.2", {"start": v(-70.73, 108.92) * mm, "end": v(-54.13, 108.92) * mm, "construction": true});
            skLineSegment(sketch, "E14.3.5.3", {"start": v(-54.13, 108.92) * mm, "end": v(-54.13, 92.32) * mm, "construction": true});
            skLineSegment(sketch, "E14.3.6.0", {"start": v(-70.73, 108.92) * mm, "end": v(-54.13, 108.92) * mm, "construction": true});
            skLineSegment(sketch, "E14.3.6.1", {"start": v(-70.73, 125.52) * mm, "end": v(-70.73, 108.92) * mm, "construction": true});
            skLineSegment(sketch, "E14.3.6.2", {"start": v(-70.73, 125.52) * mm, "end": v(-54.13, 125.52) * mm, "construction": true});
            skLineSegment(sketch, "E14.3.6.3", {"start": v(-54.13, 125.52) * mm, "end": v(-54.13, 108.92) * mm, "construction": true});
            skLineSegment(sketch, "E14.3.7.0", {"start": v(-70.73, 125.52) * mm, "end": v(-54.13, 125.52) * mm, "construction": true});
            skLineSegment(sketch, "E14.3.7.1", {"start": v(-70.73, 142.12) * mm, "end": v(-70.73, 125.52) * mm, "construction": true});
            skLineSegment(sketch, "E14.3.7.2", {"start": v(-70.73, 142.12) * mm, "end": v(-54.13, 142.12) * mm, "construction": true});
            skLineSegment(sketch, "E14.3.7.3", {"start": v(-54.13, 142.12) * mm, "end": v(-54.13, 125.52) * mm, "construction": true});
            skLineSegment(sketch, "E14.3.8.0", {"start": v(-70.73, 142.12) * mm, "end": v(-54.13, 142.12) * mm, "construction": true});
            skLineSegment(sketch, "E14.3.8.1", {"start": v(-70.73, 158.72) * mm, "end": v(-70.73, 142.12) * mm, "construction": true});
            skLineSegment(sketch, "E14.3.8.2", {"start": v(-70.73, 158.72) * mm, "end": v(-54.13, 158.72) * mm, "construction": true});
            skLineSegment(sketch, "E14.3.8.3", {"start": v(-54.13, 158.72) * mm, "end": v(-54.13, 142.12) * mm, "construction": true});
            skLineSegment(sketch, "E14.3.9.0", {"start": v(-70.73, 158.72) * mm, "end": v(-54.13, 158.72) * mm, "construction": true});
            skLineSegment(sketch, "E14.3.9.1", {"start": v(-70.73, 175.32) * mm, "end": v(-70.73, 158.72) * mm, "construction": true});
            skLineSegment(sketch, "E14.3.9.2", {"start": v(-70.73, 175.32) * mm, "end": v(-54.13, 175.32) * mm, "construction": true});
            skLineSegment(sketch, "E14.3.9.3", {"start": v(-54.13, 175.32) * mm, "end": v(-54.13, 158.72) * mm, "construction": true});
            skLineSegment(sketch, "E14.3.10.0", {"start": v(-70.73, 175.32) * mm, "end": v(-54.13, 175.32) * mm, "construction": true});
            skLineSegment(sketch, "E14.3.10.1", {"start": v(-70.73, 191.92) * mm, "end": v(-70.73, 175.32) * mm, "construction": true});
            skLineSegment(sketch, "E14.3.10.2", {"start": v(-70.73, 191.92) * mm, "end": v(-54.13, 191.92) * mm, "construction": true});
            skLineSegment(sketch, "E14.3.10.3", {"start": v(-54.13, 191.92) * mm, "end": v(-54.13, 175.32) * mm, "construction": true});
            skLineSegment(sketch, "E14.3.11.0", {"start": v(-70.73, 191.92) * mm, "end": v(-54.13, 191.92) * mm, "construction": true});
            skLineSegment(sketch, "E14.3.11.1", {"start": v(-70.73, 208.52) * mm, "end": v(-70.73, 191.92) * mm, "construction": true});
            skLineSegment(sketch, "E14.3.11.2", {"start": v(-70.73, 208.52) * mm, "end": v(-54.13, 208.52) * mm, "construction": true});
            skLineSegment(sketch, "E14.3.11.3", {"start": v(-54.13, 208.52) * mm, "end": v(-54.13, 191.92) * mm, "construction": true});
            skLineSegment(sketch, "E14.3.12.0", {"start": v(-70.73, 208.52) * mm, "end": v(-54.13, 208.52) * mm, "construction": true});
            skLineSegment(sketch, "E14.3.12.1", {"start": v(-70.73, 225.12) * mm, "end": v(-70.73, 208.52) * mm, "construction": true});
            skLineSegment(sketch, "E14.3.12.2", {"start": v(-70.73, 225.12) * mm, "end": v(-54.13, 225.12) * mm, "construction": true});
            skLineSegment(sketch, "E14.3.12.3", {"start": v(-54.13, 225.12) * mm, "end": v(-54.13, 208.52) * mm, "construction": true});
            skLineSegment(sketch, "E14.3.13.0", {"start": v(-70.73, 225.12) * mm, "end": v(-54.13, 225.12) * mm, "construction": true});
            skLineSegment(sketch, "E14.3.13.1", {"start": v(-70.73, 241.72) * mm, "end": v(-70.73, 225.12) * mm, "construction": true});
            skLineSegment(sketch, "E14.3.13.2", {"start": v(-70.73, 241.72) * mm, "end": v(-54.13, 241.72) * mm, "construction": true});
            skLineSegment(sketch, "E14.3.13.3", {"start": v(-54.13, 241.72) * mm, "end": v(-54.13, 225.12) * mm, "construction": true});
            skLineSegment(sketch, "E14.3.14.0", {"start": v(-70.73, 241.72) * mm, "end": v(-54.13, 241.72) * mm, "construction": true});
            skLineSegment(sketch, "E14.3.14.1", {"start": v(-70.73, 258.32) * mm, "end": v(-70.73, 241.72) * mm, "construction": true});
            skLineSegment(sketch, "E14.3.14.2", {"start": v(-70.73, 258.32) * mm, "end": v(-54.13, 258.32) * mm, "construction": true});
            skLineSegment(sketch, "E14.3.14.3", {"start": v(-54.13, 258.32) * mm, "end": v(-54.13, 241.72) * mm, "construction": true});
            skLineSegment(sketch, "E14.3.15.0", {"start": v(-70.73, 258.32) * mm, "end": v(-54.13, 258.32) * mm, "construction": true});
            skLineSegment(sketch, "E14.3.15.1", {"start": v(-70.73, 274.92) * mm, "end": v(-70.73, 258.32) * mm, "construction": true});
            skLineSegment(sketch, "E14.3.15.2", {"start": v(-70.73, 274.92) * mm, "end": v(-54.13, 274.92) * mm, "construction": true});
            skLineSegment(sketch, "E14.3.15.3", {"start": v(-54.13, 274.92) * mm, "end": v(-54.13, 258.32) * mm, "construction": true});
            skLineSegment(sketch, "E14.4.0.0", {"start": v(-54.13, 9.32) * mm, "end": v(-37.53, 9.32) * mm, "construction": true});
            skLineSegment(sketch, "E14.4.0.1", {"start": v(-54.13, 25.92) * mm, "end": v(-54.13, 9.32) * mm, "construction": true});
            skLineSegment(sketch, "E14.4.0.2", {"start": v(-54.13, 25.92) * mm, "end": v(-37.53, 25.92) * mm, "construction": true});
            skLineSegment(sketch, "E14.4.0.3", {"start": v(-37.53, 25.92) * mm, "end": v(-37.53, 9.32) * mm, "construction": true});
            skLineSegment(sketch, "E14.4.1.0", {"start": v(-54.13, 25.92) * mm, "end": v(-37.53, 25.92) * mm, "construction": true});
            skLineSegment(sketch, "E14.4.1.1", {"start": v(-54.13, 42.52) * mm, "end": v(-54.13, 25.92) * mm, "construction": true});
            skLineSegment(sketch, "E14.4.1.2", {"start": v(-54.13, 42.52) * mm, "end": v(-37.53, 42.52) * mm, "construction": true});
            skLineSegment(sketch, "E14.4.1.3", {"start": v(-37.53, 42.52) * mm, "end": v(-37.53, 25.92) * mm, "construction": true});
            skLineSegment(sketch, "E14.4.2.0", {"start": v(-54.13, 42.52) * mm, "end": v(-37.53, 42.52) * mm, "construction": true});
            skLineSegment(sketch, "E14.4.2.1", {"start": v(-54.13, 59.12) * mm, "end": v(-54.13, 42.52) * mm, "construction": true});
            skLineSegment(sketch, "E14.4.2.2", {"start": v(-54.13, 59.12) * mm, "end": v(-37.53, 59.12) * mm, "construction": true});
            skLineSegment(sketch, "E14.4.2.3", {"start": v(-37.53, 59.12) * mm, "end": v(-37.53, 42.52) * mm, "construction": true});
            skLineSegment(sketch, "E14.4.3.0", {"start": v(-54.13, 59.12) * mm, "end": v(-37.53, 59.12) * mm, "construction": true});
            skLineSegment(sketch, "E14.4.3.1", {"start": v(-54.13, 75.72) * mm, "end": v(-54.13, 59.12) * mm, "construction": true});
            skLineSegment(sketch, "E14.4.3.2", {"start": v(-54.13, 75.72) * mm, "end": v(-37.53, 75.72) * mm, "construction": true});
            skLineSegment(sketch, "E14.4.3.3", {"start": v(-37.53, 75.72) * mm, "end": v(-37.53, 59.12) * mm, "construction": true});
            skLineSegment(sketch, "E14.4.4.0", {"start": v(-54.13, 75.72) * mm, "end": v(-37.53, 75.72) * mm, "construction": true});
            skLineSegment(sketch, "E14.4.4.1", {"start": v(-54.13, 92.32) * mm, "end": v(-54.13, 75.72) * mm, "construction": true});
            skLineSegment(sketch, "E14.4.4.2", {"start": v(-54.13, 92.32) * mm, "end": v(-37.53, 92.32) * mm, "construction": true});
            skLineSegment(sketch, "E14.4.4.3", {"start": v(-37.53, 92.32) * mm, "end": v(-37.53, 75.72) * mm, "construction": true});
            skLineSegment(sketch, "E14.4.5.0", {"start": v(-54.13, 92.32) * mm, "end": v(-37.53, 92.32) * mm, "construction": true});
            skLineSegment(sketch, "E14.4.5.1", {"start": v(-54.13, 108.92) * mm, "end": v(-54.13, 92.32) * mm, "construction": true});
            skLineSegment(sketch, "E14.4.5.2", {"start": v(-54.13, 108.92) * mm, "end": v(-37.53, 108.92) * mm, "construction": true});
            skLineSegment(sketch, "E14.4.5.3", {"start": v(-37.53, 108.92) * mm, "end": v(-37.53, 92.32) * mm, "construction": true});
            skLineSegment(sketch, "E14.4.6.0", {"start": v(-54.13, 108.92) * mm, "end": v(-37.53, 108.92) * mm, "construction": true});
            skLineSegment(sketch, "E14.4.6.1", {"start": v(-54.13, 125.52) * mm, "end": v(-54.13, 108.92) * mm, "construction": true});
            skLineSegment(sketch, "E14.4.6.2", {"start": v(-54.13, 125.52) * mm, "end": v(-37.53, 125.52) * mm, "construction": true});
            skLineSegment(sketch, "E14.4.6.3", {"start": v(-37.53, 125.52) * mm, "end": v(-37.53, 108.92) * mm, "construction": true});
            skLineSegment(sketch, "E14.4.7.0", {"start": v(-54.13, 125.52) * mm, "end": v(-37.53, 125.52) * mm, "construction": true});
            skLineSegment(sketch, "E14.4.7.1", {"start": v(-54.13, 142.12) * mm, "end": v(-54.13, 125.52) * mm, "construction": true});
            skLineSegment(sketch, "E14.4.7.2", {"start": v(-54.13, 142.12) * mm, "end": v(-37.53, 142.12) * mm, "construction": true});
            skLineSegment(sketch, "E14.4.7.3", {"start": v(-37.53, 142.12) * mm, "end": v(-37.53, 125.52) * mm, "construction": true});
            skLineSegment(sketch, "E14.4.8.0", {"start": v(-54.13, 142.12) * mm, "end": v(-37.53, 142.12) * mm, "construction": true});
            skLineSegment(sketch, "E14.4.8.1", {"start": v(-54.13, 158.72) * mm, "end": v(-54.13, 142.12) * mm, "construction": true});
            skLineSegment(sketch, "E14.4.8.2", {"start": v(-54.13, 158.72) * mm, "end": v(-37.53, 158.72) * mm, "construction": true});
            skLineSegment(sketch, "E14.4.8.3", {"start": v(-37.53, 158.72) * mm, "end": v(-37.53, 142.12) * mm, "construction": true});
            skLineSegment(sketch, "E14.4.9.0", {"start": v(-54.13, 158.72) * mm, "end": v(-37.53, 158.72) * mm, "construction": true});
            skLineSegment(sketch, "E14.4.9.1", {"start": v(-54.13, 175.32) * mm, "end": v(-54.13, 158.72) * mm, "construction": true});
            skLineSegment(sketch, "E14.4.9.2", {"start": v(-54.13, 175.32) * mm, "end": v(-37.53, 175.32) * mm, "construction": true});
            skLineSegment(sketch, "E14.4.9.3", {"start": v(-37.53, 175.32) * mm, "end": v(-37.53, 158.72) * mm, "construction": true});
            skLineSegment(sketch, "E14.4.10.0", {"start": v(-54.13, 175.32) * mm, "end": v(-37.53, 175.32) * mm, "construction": true});
            skLineSegment(sketch, "E14.4.10.1", {"start": v(-54.13, 191.92) * mm, "end": v(-54.13, 175.32) * mm, "construction": true});
            skLineSegment(sketch, "E14.4.10.2", {"start": v(-54.13, 191.92) * mm, "end": v(-37.53, 191.92) * mm, "construction": true});
            skLineSegment(sketch, "E14.4.10.3", {"start": v(-37.53, 191.92) * mm, "end": v(-37.53, 175.32) * mm, "construction": true});
            skLineSegment(sketch, "E14.4.11.0", {"start": v(-54.13, 191.92) * mm, "end": v(-37.53, 191.92) * mm, "construction": true});
            skLineSegment(sketch, "E14.4.11.1", {"start": v(-54.13, 208.52) * mm, "end": v(-54.13, 191.92) * mm, "construction": true});
            skLineSegment(sketch, "E14.4.11.2", {"start": v(-54.13, 208.52) * mm, "end": v(-37.53, 208.52) * mm, "construction": true});
            skLineSegment(sketch, "E14.4.11.3", {"start": v(-37.53, 208.52) * mm, "end": v(-37.53, 191.92) * mm, "construction": true});
            skLineSegment(sketch, "E14.4.12.0", {"start": v(-54.13, 208.52) * mm, "end": v(-37.53, 208.52) * mm, "construction": true});
            skLineSegment(sketch, "E14.4.12.1", {"start": v(-54.13, 225.12) * mm, "end": v(-54.13, 208.52) * mm, "construction": true});
            skLineSegment(sketch, "E14.4.12.2", {"start": v(-54.13, 225.12) * mm, "end": v(-37.53, 225.12) * mm, "construction": true});
            skLineSegment(sketch, "E14.4.12.3", {"start": v(-37.53, 225.12) * mm, "end": v(-37.53, 208.52) * mm, "construction": true});
            skLineSegment(sketch, "E14.4.13.0", {"start": v(-54.13, 225.12) * mm, "end": v(-37.53, 225.12) * mm, "construction": true});
            skLineSegment(sketch, "E14.4.13.1", {"start": v(-54.13, 241.72) * mm, "end": v(-54.13, 225.12) * mm, "construction": true});
            skLineSegment(sketch, "E14.4.13.2", {"start": v(-54.13, 241.72) * mm, "end": v(-37.53, 241.72) * mm, "construction": true});
            skLineSegment(sketch, "E14.4.13.3", {"start": v(-37.53, 241.72) * mm, "end": v(-37.53, 225.12) * mm, "construction": true});
            skLineSegment(sketch, "E14.4.14.0", {"start": v(-54.13, 241.72) * mm, "end": v(-37.53, 241.72) * mm, "construction": true});
            skLineSegment(sketch, "E14.4.14.1", {"start": v(-54.13, 258.32) * mm, "end": v(-54.13, 241.72) * mm, "construction": true});
            skLineSegment(sketch, "E14.4.14.2", {"start": v(-54.13, 258.32) * mm, "end": v(-37.53, 258.32) * mm, "construction": true});
            skLineSegment(sketch, "E14.4.14.3", {"start": v(-37.53, 258.32) * mm, "end": v(-37.53, 241.72) * mm, "construction": true});
            skLineSegment(sketch, "E14.4.15.0", {"start": v(-54.13, 258.32) * mm, "end": v(-37.53, 258.32) * mm, "construction": true});
            skLineSegment(sketch, "E14.4.15.1", {"start": v(-54.13, 274.92) * mm, "end": v(-54.13, 258.32) * mm, "construction": true});
            skLineSegment(sketch, "E14.4.15.2", {"start": v(-54.13, 274.92) * mm, "end": v(-37.53, 274.92) * mm, "construction": true});
            skLineSegment(sketch, "E14.4.15.3", {"start": v(-37.53, 274.92) * mm, "end": v(-37.53, 258.32) * mm, "construction": true});
            skLineSegment(sketch, "E14.5.0.0", {"start": v(-37.53, 9.32) * mm, "end": v(-20.93, 9.32) * mm, "construction": true});
            skLineSegment(sketch, "E14.5.0.1", {"start": v(-37.53, 25.92) * mm, "end": v(-37.53, 9.32) * mm, "construction": true});
            skLineSegment(sketch, "E14.5.0.2", {"start": v(-37.53, 25.92) * mm, "end": v(-20.93, 25.92) * mm, "construction": true});
            skLineSegment(sketch, "E14.5.0.3", {"start": v(-20.93, 25.92) * mm, "end": v(-20.93, 9.32) * mm, "construction": true});
            skLineSegment(sketch, "E14.5.1.0", {"start": v(-37.53, 25.92) * mm, "end": v(-20.93, 25.92) * mm, "construction": true});
            skLineSegment(sketch, "E14.5.1.1", {"start": v(-37.53, 42.52) * mm, "end": v(-37.53, 25.92) * mm, "construction": true});
            skLineSegment(sketch, "E14.5.1.2", {"start": v(-37.53, 42.52) * mm, "end": v(-20.93, 42.52) * mm, "construction": true});
            skLineSegment(sketch, "E14.5.1.3", {"start": v(-20.93, 42.52) * mm, "end": v(-20.93, 25.92) * mm, "construction": true});
            skLineSegment(sketch, "E14.5.2.0", {"start": v(-37.53, 42.52) * mm, "end": v(-20.93, 42.52) * mm, "construction": true});
            skLineSegment(sketch, "E14.5.2.1", {"start": v(-37.53, 59.12) * mm, "end": v(-37.53, 42.52) * mm, "construction": true});
            skLineSegment(sketch, "E14.5.2.2", {"start": v(-37.53, 59.12) * mm, "end": v(-20.93, 59.12) * mm, "construction": true});
            skLineSegment(sketch, "E14.5.2.3", {"start": v(-20.93, 59.12) * mm, "end": v(-20.93, 42.52) * mm, "construction": true});
            skLineSegment(sketch, "E14.5.3.0", {"start": v(-37.53, 59.12) * mm, "end": v(-20.93, 59.12) * mm, "construction": true});
            skLineSegment(sketch, "E14.5.3.1", {"start": v(-37.53, 75.72) * mm, "end": v(-37.53, 59.12) * mm, "construction": true});
            skLineSegment(sketch, "E14.5.3.2", {"start": v(-37.53, 75.72) * mm, "end": v(-20.93, 75.72) * mm, "construction": true});
            skLineSegment(sketch, "E14.5.3.3", {"start": v(-20.93, 75.72) * mm, "end": v(-20.93, 59.12) * mm, "construction": true});
            skLineSegment(sketch, "E14.5.4.0", {"start": v(-37.53, 75.72) * mm, "end": v(-20.93, 75.72) * mm, "construction": true});
            skLineSegment(sketch, "E14.5.4.1", {"start": v(-37.53, 92.32) * mm, "end": v(-37.53, 75.72) * mm, "construction": true});
            skLineSegment(sketch, "E14.5.4.2", {"start": v(-37.53, 92.32) * mm, "end": v(-20.93, 92.32) * mm, "construction": true});
            skLineSegment(sketch, "E14.5.4.3", {"start": v(-20.93, 92.32) * mm, "end": v(-20.93, 75.72) * mm, "construction": true});
            skLineSegment(sketch, "E14.5.5.0", {"start": v(-37.53, 92.32) * mm, "end": v(-20.93, 92.32) * mm, "construction": true});
            skLineSegment(sketch, "E14.5.5.1", {"start": v(-37.53, 108.92) * mm, "end": v(-37.53, 92.32) * mm, "construction": true});
            skLineSegment(sketch, "E14.5.5.2", {"start": v(-37.53, 108.92) * mm, "end": v(-20.93, 108.92) * mm, "construction": true});
            skLineSegment(sketch, "E14.5.5.3", {"start": v(-20.93, 108.92) * mm, "end": v(-20.93, 92.32) * mm, "construction": true});
            skLineSegment(sketch, "E14.5.6.0", {"start": v(-37.53, 108.92) * mm, "end": v(-20.93, 108.92) * mm, "construction": true});
            skLineSegment(sketch, "E14.5.6.1", {"start": v(-37.53, 125.52) * mm, "end": v(-37.53, 108.92) * mm, "construction": true});
            skLineSegment(sketch, "E14.5.6.2", {"start": v(-37.53, 125.52) * mm, "end": v(-20.93, 125.52) * mm, "construction": true});
            skLineSegment(sketch, "E14.5.6.3", {"start": v(-20.93, 125.52) * mm, "end": v(-20.93, 108.92) * mm, "construction": true});
            skLineSegment(sketch, "E14.5.7.0", {"start": v(-37.53, 125.52) * mm, "end": v(-20.93, 125.52) * mm, "construction": true});
            skLineSegment(sketch, "E14.5.7.1", {"start": v(-37.53, 142.12) * mm, "end": v(-37.53, 125.52) * mm, "construction": true});
            skLineSegment(sketch, "E14.5.7.2", {"start": v(-37.53, 142.12) * mm, "end": v(-20.93, 142.12) * mm, "construction": true});
            skLineSegment(sketch, "E14.5.7.3", {"start": v(-20.93, 142.12) * mm, "end": v(-20.93, 125.52) * mm, "construction": true});
            skLineSegment(sketch, "E14.5.8.0", {"start": v(-37.53, 142.12) * mm, "end": v(-20.93, 142.12) * mm, "construction": true});
            skLineSegment(sketch, "E14.5.8.1", {"start": v(-37.53, 158.72) * mm, "end": v(-37.53, 142.12) * mm, "construction": true});
            skLineSegment(sketch, "E14.5.8.2", {"start": v(-37.53, 158.72) * mm, "end": v(-20.93, 158.72) * mm, "construction": true});
            skLineSegment(sketch, "E14.5.8.3", {"start": v(-20.93, 158.72) * mm, "end": v(-20.93, 142.12) * mm, "construction": true});
            skLineSegment(sketch, "E14.5.9.0", {"start": v(-37.53, 158.72) * mm, "end": v(-20.93, 158.72) * mm, "construction": true});
            skLineSegment(sketch, "E14.5.9.1", {"start": v(-37.53, 175.32) * mm, "end": v(-37.53, 158.72) * mm, "construction": true});
            skLineSegment(sketch, "E14.5.9.2", {"start": v(-37.53, 175.32) * mm, "end": v(-20.93, 175.32) * mm, "construction": true});
            skLineSegment(sketch, "E14.5.9.3", {"start": v(-20.93, 175.32) * mm, "end": v(-20.93, 158.72) * mm, "construction": true});
            skLineSegment(sketch, "E14.5.10.0", {"start": v(-37.53, 175.32) * mm, "end": v(-20.93, 175.32) * mm, "construction": true});
            skLineSegment(sketch, "E14.5.10.1", {"start": v(-37.53, 191.92) * mm, "end": v(-37.53, 175.32) * mm, "construction": true});
            skLineSegment(sketch, "E14.5.10.2", {"start": v(-37.53, 191.92) * mm, "end": v(-20.93, 191.92) * mm, "construction": true});
            skLineSegment(sketch, "E14.5.10.3", {"start": v(-20.93, 191.92) * mm, "end": v(-20.93, 175.32) * mm, "construction": true});
            skLineSegment(sketch, "E14.5.11.0", {"start": v(-37.53, 191.92) * mm, "end": v(-20.93, 191.92) * mm, "construction": true});
            skLineSegment(sketch, "E14.5.11.1", {"start": v(-37.53, 208.52) * mm, "end": v(-37.53, 191.92) * mm, "construction": true});
            skLineSegment(sketch, "E14.5.11.2", {"start": v(-37.53, 208.52) * mm, "end": v(-20.93, 208.52) * mm, "construction": true});
            skLineSegment(sketch, "E14.5.11.3", {"start": v(-20.93, 208.52) * mm, "end": v(-20.93, 191.92) * mm, "construction": true});
            skLineSegment(sketch, "E14.5.12.0", {"start": v(-37.53, 208.52) * mm, "end": v(-20.93, 208.52) * mm, "construction": true});
            skLineSegment(sketch, "E14.5.12.1", {"start": v(-37.53, 225.12) * mm, "end": v(-37.53, 208.52) * mm, "construction": true});
            skLineSegment(sketch, "E14.5.12.2", {"start": v(-37.53, 225.12) * mm, "end": v(-20.93, 225.12) * mm, "construction": true});
            skLineSegment(sketch, "E14.5.12.3", {"start": v(-20.93, 225.12) * mm, "end": v(-20.93, 208.52) * mm, "construction": true});
            skLineSegment(sketch, "E14.5.13.0", {"start": v(-37.53, 225.12) * mm, "end": v(-20.93, 225.12) * mm, "construction": true});
            skLineSegment(sketch, "E14.5.13.1", {"start": v(-37.53, 241.72) * mm, "end": v(-37.53, 225.12) * mm, "construction": true});
            skLineSegment(sketch, "E14.5.13.2", {"start": v(-37.53, 241.72) * mm, "end": v(-20.93, 241.72) * mm, "construction": true});
            skLineSegment(sketch, "E14.5.13.3", {"start": v(-20.93, 241.72) * mm, "end": v(-20.93, 225.12) * mm, "construction": true});
            skLineSegment(sketch, "E14.5.14.0", {"start": v(-37.53, 241.72) * mm, "end": v(-20.93, 241.72) * mm, "construction": true});
            skLineSegment(sketch, "E14.5.14.1", {"start": v(-37.53, 258.32) * mm, "end": v(-37.53, 241.72) * mm, "construction": true});
            skLineSegment(sketch, "E14.5.14.2", {"start": v(-37.53, 258.32) * mm, "end": v(-20.93, 258.32) * mm, "construction": true});
            skLineSegment(sketch, "E14.5.14.3", {"start": v(-20.93, 258.32) * mm, "end": v(-20.93, 241.72) * mm, "construction": true});
            skLineSegment(sketch, "E14.5.15.0", {"start": v(-37.53, 258.32) * mm, "end": v(-20.93, 258.32) * mm, "construction": true});
            skLineSegment(sketch, "E14.5.15.1", {"start": v(-37.53, 274.92) * mm, "end": v(-37.53, 258.32) * mm, "construction": true});
            skLineSegment(sketch, "E14.5.15.2", {"start": v(-37.53, 274.92) * mm, "end": v(-20.93, 274.92) * mm, "construction": true});
            skLineSegment(sketch, "E14.5.15.3", {"start": v(-20.93, 274.92) * mm, "end": v(-20.93, 258.32) * mm, "construction": true});
            skLineSegment(sketch, "E14.6.0.0", {"start": v(-20.93, 9.32) * mm, "end": v(-4.33, 9.32) * mm, "construction": true});
            skLineSegment(sketch, "E14.6.0.1", {"start": v(-20.93, 25.92) * mm, "end": v(-20.93, 9.32) * mm, "construction": true});
            skLineSegment(sketch, "E14.6.0.2", {"start": v(-20.93, 25.92) * mm, "end": v(-4.33, 25.92) * mm, "construction": true});
            skLineSegment(sketch, "E14.6.0.3", {"start": v(-4.33, 25.92) * mm, "end": v(-4.33, 9.32) * mm, "construction": true});
            skLineSegment(sketch, "E14.6.1.0", {"start": v(-20.93, 25.92) * mm, "end": v(-4.33, 25.92) * mm, "construction": true});
            skLineSegment(sketch, "E14.6.1.1", {"start": v(-20.93, 42.52) * mm, "end": v(-20.93, 25.92) * mm, "construction": true});
            skLineSegment(sketch, "E14.6.1.2", {"start": v(-20.93, 42.52) * mm, "end": v(-4.33, 42.52) * mm, "construction": true});
            skLineSegment(sketch, "E14.6.1.3", {"start": v(-4.33, 42.52) * mm, "end": v(-4.33, 25.92) * mm, "construction": true});
            skLineSegment(sketch, "E14.6.2.0", {"start": v(-20.93, 42.52) * mm, "end": v(-4.33, 42.52) * mm, "construction": true});
            skLineSegment(sketch, "E14.6.2.1", {"start": v(-20.93, 59.12) * mm, "end": v(-20.93, 42.52) * mm, "construction": true});
            skLineSegment(sketch, "E14.6.2.2", {"start": v(-20.93, 59.12) * mm, "end": v(-4.33, 59.12) * mm, "construction": true});
            skLineSegment(sketch, "E14.6.2.3", {"start": v(-4.33, 59.12) * mm, "end": v(-4.33, 42.52) * mm, "construction": true});
            skLineSegment(sketch, "E14.6.3.0", {"start": v(-20.93, 59.12) * mm, "end": v(-4.33, 59.12) * mm, "construction": true});
            skLineSegment(sketch, "E14.6.3.1", {"start": v(-20.93, 75.72) * mm, "end": v(-20.93, 59.12) * mm, "construction": true});
            skLineSegment(sketch, "E14.6.3.2", {"start": v(-20.93, 75.72) * mm, "end": v(-4.33, 75.72) * mm, "construction": true});
            skLineSegment(sketch, "E14.6.3.3", {"start": v(-4.33, 75.72) * mm, "end": v(-4.33, 59.12) * mm, "construction": true});
            skLineSegment(sketch, "E14.6.4.0", {"start": v(-20.93, 75.72) * mm, "end": v(-4.33, 75.72) * mm, "construction": true});
            skLineSegment(sketch, "E14.6.4.1", {"start": v(-20.93, 92.32) * mm, "end": v(-20.93, 75.72) * mm, "construction": true});
            skLineSegment(sketch, "E14.6.4.2", {"start": v(-20.93, 92.32) * mm, "end": v(-4.33, 92.32) * mm, "construction": true});
            skLineSegment(sketch, "E14.6.4.3", {"start": v(-4.33, 92.32) * mm, "end": v(-4.33, 75.72) * mm, "construction": true});
            skLineSegment(sketch, "E14.6.5.0", {"start": v(-20.93, 92.32) * mm, "end": v(-4.33, 92.32) * mm, "construction": true});
            skLineSegment(sketch, "E14.6.5.1", {"start": v(-20.93, 108.92) * mm, "end": v(-20.93, 92.32) * mm, "construction": true});
            skLineSegment(sketch, "E14.6.5.2", {"start": v(-20.93, 108.92) * mm, "end": v(-4.33, 108.92) * mm, "construction": true});
            skLineSegment(sketch, "E14.6.5.3", {"start": v(-4.33, 108.92) * mm, "end": v(-4.33, 92.32) * mm, "construction": true});
            skLineSegment(sketch, "E14.6.6.0", {"start": v(-20.93, 108.92) * mm, "end": v(-4.33, 108.92) * mm, "construction": true});
            skLineSegment(sketch, "E14.6.6.1", {"start": v(-20.93, 125.52) * mm, "end": v(-20.93, 108.92) * mm, "construction": true});
            skLineSegment(sketch, "E14.6.6.2", {"start": v(-20.93, 125.52) * mm, "end": v(-4.33, 125.52) * mm, "construction": true});
            skLineSegment(sketch, "E14.6.6.3", {"start": v(-4.33, 125.52) * mm, "end": v(-4.33, 108.92) * mm, "construction": true});
            skLineSegment(sketch, "E14.6.7.0", {"start": v(-20.93, 125.52) * mm, "end": v(-4.33, 125.52) * mm, "construction": true});
            skLineSegment(sketch, "E14.6.7.1", {"start": v(-20.93, 142.12) * mm, "end": v(-20.93, 125.52) * mm, "construction": true});
            skLineSegment(sketch, "E14.6.7.2", {"start": v(-20.93, 142.12) * mm, "end": v(-4.33, 142.12) * mm, "construction": true});
            skLineSegment(sketch, "E14.6.7.3", {"start": v(-4.33, 142.12) * mm, "end": v(-4.33, 125.52) * mm, "construction": true});
            skLineSegment(sketch, "E14.6.8.0", {"start": v(-20.93, 142.12) * mm, "end": v(-4.33, 142.12) * mm, "construction": true});
            skLineSegment(sketch, "E14.6.8.1", {"start": v(-20.93, 158.72) * mm, "end": v(-20.93, 142.12) * mm, "construction": true});
            skLineSegment(sketch, "E14.6.8.2", {"start": v(-20.93, 158.72) * mm, "end": v(-4.33, 158.72) * mm, "construction": true});
            skLineSegment(sketch, "E14.6.8.3", {"start": v(-4.33, 158.72) * mm, "end": v(-4.33, 142.12) * mm, "construction": true});
            skLineSegment(sketch, "E14.6.9.0", {"start": v(-20.93, 158.72) * mm, "end": v(-4.33, 158.72) * mm, "construction": true});
            skLineSegment(sketch, "E14.6.9.1", {"start": v(-20.93, 175.32) * mm, "end": v(-20.93, 158.72) * mm, "construction": true});
            skLineSegment(sketch, "E14.6.9.2", {"start": v(-20.93, 175.32) * mm, "end": v(-4.33, 175.32) * mm, "construction": true});
            skLineSegment(sketch, "E14.6.9.3", {"start": v(-4.33, 175.32) * mm, "end": v(-4.33, 158.72) * mm, "construction": true});
            skLineSegment(sketch, "E14.6.10.0", {"start": v(-20.93, 175.32) * mm, "end": v(-4.33, 175.32) * mm, "construction": true});
            skLineSegment(sketch, "E14.6.10.1", {"start": v(-20.93, 191.92) * mm, "end": v(-20.93, 175.32) * mm, "construction": true});
            skLineSegment(sketch, "E14.6.10.2", {"start": v(-20.93, 191.92) * mm, "end": v(-4.33, 191.92) * mm, "construction": true});
            skLineSegment(sketch, "E14.6.10.3", {"start": v(-4.33, 191.92) * mm, "end": v(-4.33, 175.32) * mm, "construction": true});
            skLineSegment(sketch, "E14.6.11.0", {"start": v(-20.93, 191.92) * mm, "end": v(-4.33, 191.92) * mm, "construction": true});
            skLineSegment(sketch, "E14.6.11.1", {"start": v(-20.93, 208.52) * mm, "end": v(-20.93, 191.92) * mm, "construction": true});
            skLineSegment(sketch, "E14.6.11.2", {"start": v(-20.93, 208.52) * mm, "end": v(-4.33, 208.52) * mm, "construction": true});
            skLineSegment(sketch, "E14.6.11.3", {"start": v(-4.33, 208.52) * mm, "end": v(-4.33, 191.92) * mm, "construction": true});
            skLineSegment(sketch, "E14.6.12.0", {"start": v(-20.93, 208.52) * mm, "end": v(-4.33, 208.52) * mm, "construction": true});
            skLineSegment(sketch, "E14.6.12.1", {"start": v(-20.93, 225.12) * mm, "end": v(-20.93, 208.52) * mm, "construction": true});
            skLineSegment(sketch, "E14.6.12.2", {"start": v(-20.93, 225.12) * mm, "end": v(-4.33, 225.12) * mm, "construction": true});
            skLineSegment(sketch, "E14.6.12.3", {"start": v(-4.33, 225.12) * mm, "end": v(-4.33, 208.52) * mm, "construction": true});
            skLineSegment(sketch, "E14.6.13.0", {"start": v(-20.93, 225.12) * mm, "end": v(-4.33, 225.12) * mm, "construction": true});
            skLineSegment(sketch, "E14.6.13.1", {"start": v(-20.93, 241.72) * mm, "end": v(-20.93, 225.12) * mm, "construction": true});
            skLineSegment(sketch, "E14.6.13.2", {"start": v(-20.93, 241.72) * mm, "end": v(-4.33, 241.72) * mm, "construction": true});
            skLineSegment(sketch, "E14.6.13.3", {"start": v(-4.33, 241.72) * mm, "end": v(-4.33, 225.12) * mm, "construction": true});
            skLineSegment(sketch, "E14.6.14.0", {"start": v(-20.93, 241.72) * mm, "end": v(-4.33, 241.72) * mm, "construction": true});
            skLineSegment(sketch, "E14.6.14.1", {"start": v(-20.93, 258.32) * mm, "end": v(-20.93, 241.72) * mm, "construction": true});
            skLineSegment(sketch, "E14.6.14.2", {"start": v(-20.93, 258.32) * mm, "end": v(-4.33, 258.32) * mm, "construction": true});
            skLineSegment(sketch, "E14.6.14.3", {"start": v(-4.33, 258.32) * mm, "end": v(-4.33, 241.72) * mm, "construction": true});
            skLineSegment(sketch, "E14.6.15.0", {"start": v(-20.93, 258.32) * mm, "end": v(-4.33, 258.32) * mm, "construction": true});
            skLineSegment(sketch, "E14.6.15.1", {"start": v(-20.93, 274.92) * mm, "end": v(-20.93, 258.32) * mm, "construction": true});
            skLineSegment(sketch, "E14.6.15.2", {"start": v(-20.93, 274.92) * mm, "end": v(-4.33, 274.92) * mm, "construction": true});
            skLineSegment(sketch, "E14.6.15.3", {"start": v(-4.33, 274.92) * mm, "end": v(-4.33, 258.32) * mm, "construction": true});
            skLineSegment(sketch, "E14.7.0.0", {"start": v(-4.33, 9.32) * mm, "end": v(12.27, 9.32) * mm, "construction": true});
            skLineSegment(sketch, "E14.7.0.1", {"start": v(-4.33, 25.92) * mm, "end": v(-4.33, 9.32) * mm, "construction": true});
            skLineSegment(sketch, "E14.7.0.2", {"start": v(-4.33, 25.92) * mm, "end": v(12.27, 25.92) * mm, "construction": true});
            skLineSegment(sketch, "E14.7.0.3", {"start": v(12.27, 25.92) * mm, "end": v(12.27, 9.32) * mm, "construction": true});
            skLineSegment(sketch, "E14.7.1.0", {"start": v(-4.33, 25.92) * mm, "end": v(12.27, 25.92) * mm, "construction": true});
            skLineSegment(sketch, "E14.7.1.1", {"start": v(-4.33, 42.52) * mm, "end": v(-4.33, 25.92) * mm, "construction": true});
            skLineSegment(sketch, "E14.7.1.2", {"start": v(-4.33, 42.52) * mm, "end": v(12.27, 42.52) * mm, "construction": true});
            skLineSegment(sketch, "E14.7.1.3", {"start": v(12.27, 42.52) * mm, "end": v(12.27, 25.92) * mm, "construction": true});
            skLineSegment(sketch, "E14.7.2.0", {"start": v(-4.33, 42.52) * mm, "end": v(12.27, 42.52) * mm, "construction": true});
            skLineSegment(sketch, "E14.7.2.1", {"start": v(-4.33, 59.12) * mm, "end": v(-4.33, 42.52) * mm, "construction": true});
            skLineSegment(sketch, "E14.7.2.2", {"start": v(-4.33, 59.12) * mm, "end": v(12.27, 59.12) * mm, "construction": true});
            skLineSegment(sketch, "E14.7.2.3", {"start": v(12.27, 59.12) * mm, "end": v(12.27, 42.52) * mm, "construction": true});
            skLineSegment(sketch, "E14.7.3.0", {"start": v(-4.33, 59.12) * mm, "end": v(12.27, 59.12) * mm, "construction": true});
            skLineSegment(sketch, "E14.7.3.1", {"start": v(-4.33, 75.72) * mm, "end": v(-4.33, 59.12) * mm, "construction": true});
            skLineSegment(sketch, "E14.7.3.2", {"start": v(-4.33, 75.72) * mm, "end": v(12.27, 75.72) * mm, "construction": true});
            skLineSegment(sketch, "E14.7.3.3", {"start": v(12.27, 75.72) * mm, "end": v(12.27, 59.12) * mm, "construction": true});
            skLineSegment(sketch, "E14.7.4.0", {"start": v(-4.33, 75.72) * mm, "end": v(12.27, 75.72) * mm, "construction": true});
            skLineSegment(sketch, "E14.7.4.1", {"start": v(-4.33, 92.32) * mm, "end": v(-4.33, 75.72) * mm, "construction": true});
            skLineSegment(sketch, "E14.7.4.2", {"start": v(-4.33, 92.32) * mm, "end": v(12.27, 92.32) * mm, "construction": true});
            skLineSegment(sketch, "E14.7.4.3", {"start": v(12.27, 92.32) * mm, "end": v(12.27, 75.72) * mm, "construction": true});
            skLineSegment(sketch, "E14.7.5.0", {"start": v(-4.33, 92.32) * mm, "end": v(12.27, 92.32) * mm, "construction": true});
            skLineSegment(sketch, "E14.7.5.1", {"start": v(-4.33, 108.92) * mm, "end": v(-4.33, 92.32) * mm, "construction": true});
            skLineSegment(sketch, "E14.7.5.2", {"start": v(-4.33, 108.92) * mm, "end": v(12.27, 108.92) * mm, "construction": true});
            skLineSegment(sketch, "E14.7.5.3", {"start": v(12.27, 108.92) * mm, "end": v(12.27, 92.32) * mm, "construction": true});
            skLineSegment(sketch, "E14.7.6.0", {"start": v(-4.33, 108.92) * mm, "end": v(12.27, 108.92) * mm, "construction": true});
            skLineSegment(sketch, "E14.7.6.1", {"start": v(-4.33, 125.52) * mm, "end": v(-4.33, 108.92) * mm, "construction": true});
            skLineSegment(sketch, "E14.7.6.2", {"start": v(-4.33, 125.52) * mm, "end": v(12.27, 125.52) * mm, "construction": true});
            skLineSegment(sketch, "E14.7.6.3", {"start": v(12.27, 125.52) * mm, "end": v(12.27, 108.92) * mm, "construction": true});
            skLineSegment(sketch, "E14.7.7.0", {"start": v(-4.33, 125.52) * mm, "end": v(12.27, 125.52) * mm, "construction": true});
            skLineSegment(sketch, "E14.7.7.1", {"start": v(-4.33, 142.12) * mm, "end": v(-4.33, 125.52) * mm, "construction": true});
            skLineSegment(sketch, "E14.7.7.2", {"start": v(-4.33, 142.12) * mm, "end": v(12.27, 142.12) * mm, "construction": true});
            skLineSegment(sketch, "E14.7.7.3", {"start": v(12.27, 142.12) * mm, "end": v(12.27, 125.52) * mm, "construction": true});
            skLineSegment(sketch, "E14.7.8.0", {"start": v(-4.33, 142.12) * mm, "end": v(12.27, 142.12) * mm, "construction": true});
            skLineSegment(sketch, "E14.7.8.1", {"start": v(-4.33, 158.72) * mm, "end": v(-4.33, 142.12) * mm, "construction": true});
            skLineSegment(sketch, "E14.7.8.2", {"start": v(-4.33, 158.72) * mm, "end": v(12.27, 158.72) * mm, "construction": true});
            skLineSegment(sketch, "E14.7.8.3", {"start": v(12.27, 158.72) * mm, "end": v(12.27, 142.12) * mm, "construction": true});
            skLineSegment(sketch, "E14.7.9.0", {"start": v(-4.33, 158.72) * mm, "end": v(12.27, 158.72) * mm, "construction": true});
            skLineSegment(sketch, "E14.7.9.1", {"start": v(-4.33, 175.32) * mm, "end": v(-4.33, 158.72) * mm, "construction": true});
            skLineSegment(sketch, "E14.7.9.2", {"start": v(-4.33, 175.32) * mm, "end": v(12.27, 175.32) * mm, "construction": true});
            skLineSegment(sketch, "E14.7.9.3", {"start": v(12.27, 175.32) * mm, "end": v(12.27, 158.72) * mm, "construction": true});
            skLineSegment(sketch, "E14.7.10.0", {"start": v(-4.33, 175.32) * mm, "end": v(12.27, 175.32) * mm, "construction": true});
            skLineSegment(sketch, "E14.7.10.1", {"start": v(-4.33, 191.92) * mm, "end": v(-4.33, 175.32) * mm, "construction": true});
            skLineSegment(sketch, "E14.7.10.2", {"start": v(-4.33, 191.92) * mm, "end": v(12.27, 191.92) * mm, "construction": true});
            skLineSegment(sketch, "E14.7.10.3", {"start": v(12.27, 191.92) * mm, "end": v(12.27, 175.32) * mm, "construction": true});
            skLineSegment(sketch, "E14.7.11.0", {"start": v(-4.33, 191.92) * mm, "end": v(12.27, 191.92) * mm, "construction": true});
            skLineSegment(sketch, "E14.7.11.1", {"start": v(-4.33, 208.52) * mm, "end": v(-4.33, 191.92) * mm, "construction": true});
            skLineSegment(sketch, "E14.7.11.2", {"start": v(-4.33, 208.52) * mm, "end": v(12.27, 208.52) * mm, "construction": true});
            skLineSegment(sketch, "E14.7.11.3", {"start": v(12.27, 208.52) * mm, "end": v(12.27, 191.92) * mm, "construction": true});
            skLineSegment(sketch, "E14.7.12.0", {"start": v(-4.33, 208.52) * mm, "end": v(12.27, 208.52) * mm, "construction": true});
            skLineSegment(sketch, "E14.7.12.1", {"start": v(-4.33, 225.12) * mm, "end": v(-4.33, 208.52) * mm, "construction": true});
            skLineSegment(sketch, "E14.7.12.2", {"start": v(-4.33, 225.12) * mm, "end": v(12.27, 225.12) * mm, "construction": true});
            skLineSegment(sketch, "E14.7.12.3", {"start": v(12.27, 225.12) * mm, "end": v(12.27, 208.52) * mm, "construction": true});
            skLineSegment(sketch, "E14.7.13.0", {"start": v(-4.33, 225.12) * mm, "end": v(12.27, 225.12) * mm, "construction": true});
            skLineSegment(sketch, "E14.7.13.1", {"start": v(-4.33, 241.72) * mm, "end": v(-4.33, 225.12) * mm, "construction": true});
            skLineSegment(sketch, "E14.7.13.2", {"start": v(-4.33, 241.72) * mm, "end": v(12.27, 241.72) * mm, "construction": true});
            skLineSegment(sketch, "E14.7.13.3", {"start": v(12.27, 241.72) * mm, "end": v(12.27, 225.12) * mm, "construction": true});
            skLineSegment(sketch, "E14.7.14.0", {"start": v(-4.33, 241.72) * mm, "end": v(12.27, 241.72) * mm, "construction": true});
            skLineSegment(sketch, "E14.7.14.1", {"start": v(-4.33, 258.32) * mm, "end": v(-4.33, 241.72) * mm, "construction": true});
            skLineSegment(sketch, "E14.7.14.2", {"start": v(-4.33, 258.32) * mm, "end": v(12.27, 258.32) * mm, "construction": true});
            skLineSegment(sketch, "E14.7.14.3", {"start": v(12.27, 258.32) * mm, "end": v(12.27, 241.72) * mm, "construction": true});
            skLineSegment(sketch, "E14.7.15.0", {"start": v(-4.33, 258.32) * mm, "end": v(12.27, 258.32) * mm, "construction": true});
            skLineSegment(sketch, "E14.7.15.1", {"start": v(-4.33, 274.92) * mm, "end": v(-4.33, 258.32) * mm, "construction": true});
            skLineSegment(sketch, "E14.7.15.2", {"start": v(-4.33, 274.92) * mm, "end": v(12.27, 274.92) * mm, "construction": true});
            skLineSegment(sketch, "E14.7.15.3", {"start": v(12.27, 274.92) * mm, "end": v(12.27, 258.32) * mm, "construction": true});
            skLineSegment(sketch, "E14.8.0.0", {"start": v(12.27, 9.32) * mm, "end": v(28.87, 9.32) * mm, "construction": true});
            skLineSegment(sketch, "E14.8.0.1", {"start": v(12.27, 25.92) * mm, "end": v(12.27, 9.32) * mm, "construction": true});
            skLineSegment(sketch, "E14.8.0.2", {"start": v(12.27, 25.92) * mm, "end": v(28.87, 25.92) * mm, "construction": true});
            skLineSegment(sketch, "E14.8.0.3", {"start": v(28.87, 25.92) * mm, "end": v(28.87, 9.32) * mm, "construction": true});
            skLineSegment(sketch, "E14.8.1.0", {"start": v(12.27, 25.92) * mm, "end": v(28.87, 25.92) * mm, "construction": true});
            skLineSegment(sketch, "E14.8.1.1", {"start": v(12.27, 42.52) * mm, "end": v(12.27, 25.92) * mm, "construction": true});
            skLineSegment(sketch, "E14.8.1.2", {"start": v(12.27, 42.52) * mm, "end": v(28.87, 42.52) * mm, "construction": true});
            skLineSegment(sketch, "E14.8.1.3", {"start": v(28.87, 42.52) * mm, "end": v(28.87, 25.92) * mm, "construction": true});
            skLineSegment(sketch, "E14.8.2.0", {"start": v(12.27, 42.52) * mm, "end": v(28.87, 42.52) * mm, "construction": true});
            skLineSegment(sketch, "E14.8.2.1", {"start": v(12.27, 59.12) * mm, "end": v(12.27, 42.52) * mm, "construction": true});
            skLineSegment(sketch, "E14.8.2.2", {"start": v(12.27, 59.12) * mm, "end": v(28.87, 59.12) * mm, "construction": true});
            skLineSegment(sketch, "E14.8.2.3", {"start": v(28.87, 59.12) * mm, "end": v(28.87, 42.52) * mm, "construction": true});
            skLineSegment(sketch, "E14.8.3.0", {"start": v(12.27, 59.12) * mm, "end": v(28.87, 59.12) * mm, "construction": true});
            skLineSegment(sketch, "E14.8.3.1", {"start": v(12.27, 75.72) * mm, "end": v(12.27, 59.12) * mm, "construction": true});
            skLineSegment(sketch, "E14.8.3.2", {"start": v(12.27, 75.72) * mm, "end": v(28.87, 75.72) * mm, "construction": true});
            skLineSegment(sketch, "E14.8.3.3", {"start": v(28.87, 75.72) * mm, "end": v(28.87, 59.12) * mm, "construction": true});
            skLineSegment(sketch, "E14.8.4.0", {"start": v(12.27, 75.72) * mm, "end": v(28.87, 75.72) * mm, "construction": true});
            skLineSegment(sketch, "E14.8.4.1", {"start": v(12.27, 92.32) * mm, "end": v(12.27, 75.72) * mm, "construction": true});
            skLineSegment(sketch, "E14.8.4.2", {"start": v(12.27, 92.32) * mm, "end": v(28.87, 92.32) * mm, "construction": true});
            skLineSegment(sketch, "E14.8.4.3", {"start": v(28.87, 92.32) * mm, "end": v(28.87, 75.72) * mm, "construction": true});
            skLineSegment(sketch, "E14.8.5.0", {"start": v(12.27, 92.32) * mm, "end": v(28.87, 92.32) * mm, "construction": true});
            skLineSegment(sketch, "E14.8.5.1", {"start": v(12.27, 108.92) * mm, "end": v(12.27, 92.32) * mm, "construction": true});
            skLineSegment(sketch, "E14.8.5.2", {"start": v(12.27, 108.92) * mm, "end": v(28.87, 108.92) * mm, "construction": true});
            skLineSegment(sketch, "E14.8.5.3", {"start": v(28.87, 108.92) * mm, "end": v(28.87, 92.32) * mm, "construction": true});
            skLineSegment(sketch, "E14.8.6.0", {"start": v(12.27, 108.92) * mm, "end": v(28.87, 108.92) * mm, "construction": true});
            skLineSegment(sketch, "E14.8.6.1", {"start": v(12.27, 125.52) * mm, "end": v(12.27, 108.92) * mm, "construction": true});
            skLineSegment(sketch, "E14.8.6.2", {"start": v(12.27, 125.52) * mm, "end": v(28.87, 125.52) * mm, "construction": true});
            skLineSegment(sketch, "E14.8.6.3", {"start": v(28.87, 125.52) * mm, "end": v(28.87, 108.92) * mm, "construction": true});
            skLineSegment(sketch, "E14.8.7.0", {"start": v(12.27, 125.52) * mm, "end": v(28.87, 125.52) * mm, "construction": true});
            skLineSegment(sketch, "E14.8.7.1", {"start": v(12.27, 142.12) * mm, "end": v(12.27, 125.52) * mm, "construction": true});
            skLineSegment(sketch, "E14.8.7.2", {"start": v(12.27, 142.12) * mm, "end": v(28.87, 142.12) * mm, "construction": true});
            skLineSegment(sketch, "E14.8.7.3", {"start": v(28.87, 142.12) * mm, "end": v(28.87, 125.52) * mm, "construction": true});
            skLineSegment(sketch, "E14.8.8.0", {"start": v(12.27, 142.12) * mm, "end": v(28.87, 142.12) * mm, "construction": true});
            skLineSegment(sketch, "E14.8.8.1", {"start": v(12.27, 158.72) * mm, "end": v(12.27, 142.12) * mm, "construction": true});
            skLineSegment(sketch, "E14.8.8.2", {"start": v(12.27, 158.72) * mm, "end": v(28.87, 158.72) * mm, "construction": true});
            skLineSegment(sketch, "E14.8.8.3", {"start": v(28.87, 158.72) * mm, "end": v(28.87, 142.12) * mm, "construction": true});
            skLineSegment(sketch, "E14.8.9.0", {"start": v(12.27, 158.72) * mm, "end": v(28.87, 158.72) * mm, "construction": true});
            skLineSegment(sketch, "E14.8.9.1", {"start": v(12.27, 175.32) * mm, "end": v(12.27, 158.72) * mm, "construction": true});
            skLineSegment(sketch, "E14.8.9.2", {"start": v(12.27, 175.32) * mm, "end": v(28.87, 175.32) * mm, "construction": true});
            skLineSegment(sketch, "E14.8.9.3", {"start": v(28.87, 175.32) * mm, "end": v(28.87, 158.72) * mm, "construction": true});
            skLineSegment(sketch, "E14.8.10.0", {"start": v(12.27, 175.32) * mm, "end": v(28.87, 175.32) * mm, "construction": true});
            skLineSegment(sketch, "E14.8.10.1", {"start": v(12.27, 191.92) * mm, "end": v(12.27, 175.32) * mm, "construction": true});
            skLineSegment(sketch, "E14.8.10.2", {"start": v(12.27, 191.92) * mm, "end": v(28.87, 191.92) * mm, "construction": true});
            skLineSegment(sketch, "E14.8.10.3", {"start": v(28.87, 191.92) * mm, "end": v(28.87, 175.32) * mm, "construction": true});
            skLineSegment(sketch, "E14.8.11.0", {"start": v(12.27, 191.92) * mm, "end": v(28.87, 191.92) * mm, "construction": true});
            skLineSegment(sketch, "E14.8.11.1", {"start": v(12.27, 208.52) * mm, "end": v(12.27, 191.92) * mm, "construction": true});
            skLineSegment(sketch, "E14.8.11.2", {"start": v(12.27, 208.52) * mm, "end": v(28.87, 208.52) * mm, "construction": true});
            skLineSegment(sketch, "E14.8.11.3", {"start": v(28.87, 208.52) * mm, "end": v(28.87, 191.92) * mm, "construction": true});
            skLineSegment(sketch, "E14.8.12.0", {"start": v(12.27, 208.52) * mm, "end": v(28.87, 208.52) * mm, "construction": true});
            skLineSegment(sketch, "E14.8.12.1", {"start": v(12.27, 225.12) * mm, "end": v(12.27, 208.52) * mm, "construction": true});
            skLineSegment(sketch, "E14.8.12.2", {"start": v(12.27, 225.12) * mm, "end": v(28.87, 225.12) * mm, "construction": true});
            skLineSegment(sketch, "E14.8.12.3", {"start": v(28.87, 225.12) * mm, "end": v(28.87, 208.52) * mm, "construction": true});
            skLineSegment(sketch, "E14.8.13.0", {"start": v(12.27, 225.12) * mm, "end": v(28.87, 225.12) * mm, "construction": true});
            skLineSegment(sketch, "E14.8.13.1", {"start": v(12.27, 241.72) * mm, "end": v(12.27, 225.12) * mm, "construction": true});
            skLineSegment(sketch, "E14.8.13.2", {"start": v(12.27, 241.72) * mm, "end": v(28.87, 241.72) * mm, "construction": true});
            skLineSegment(sketch, "E14.8.13.3", {"start": v(28.87, 241.72) * mm, "end": v(28.87, 225.12) * mm, "construction": true});
            skLineSegment(sketch, "E14.8.14.0", {"start": v(12.27, 241.72) * mm, "end": v(28.87, 241.72) * mm, "construction": true});
            skLineSegment(sketch, "E14.8.14.1", {"start": v(12.27, 258.32) * mm, "end": v(12.27, 241.72) * mm, "construction": true});
            skLineSegment(sketch, "E14.8.14.2", {"start": v(12.27, 258.32) * mm, "end": v(28.87, 258.32) * mm, "construction": true});
            skLineSegment(sketch, "E14.8.14.3", {"start": v(28.87, 258.32) * mm, "end": v(28.87, 241.72) * mm, "construction": true});
            skLineSegment(sketch, "E14.8.15.0", {"start": v(12.27, 258.32) * mm, "end": v(28.87, 258.32) * mm, "construction": true});
            skLineSegment(sketch, "E14.8.15.1", {"start": v(12.27, 274.92) * mm, "end": v(12.27, 258.32) * mm, "construction": true});
            skLineSegment(sketch, "E14.8.15.2", {"start": v(12.27, 274.92) * mm, "end": v(28.87, 274.92) * mm, "construction": true});
            skLineSegment(sketch, "E14.8.15.3", {"start": v(28.87, 274.92) * mm, "end": v(28.87, 258.32) * mm, "construction": true});
            skLineSegment(sketch, "E14.9.0.0", {"start": v(28.87, 9.32) * mm, "end": v(45.47, 9.32) * mm, "construction": true});
            skLineSegment(sketch, "E14.9.0.1", {"start": v(28.87, 25.92) * mm, "end": v(28.87, 9.32) * mm, "construction": true});
            skLineSegment(sketch, "E14.9.0.2", {"start": v(28.87, 25.92) * mm, "end": v(45.47, 25.92) * mm, "construction": true});
            skLineSegment(sketch, "E14.9.0.3", {"start": v(45.47, 25.92) * mm, "end": v(45.47, 9.32) * mm, "construction": true});
            skLineSegment(sketch, "E14.9.1.0", {"start": v(28.87, 25.92) * mm, "end": v(45.47, 25.92) * mm, "construction": true});
            skLineSegment(sketch, "E14.9.1.1", {"start": v(28.87, 42.52) * mm, "end": v(28.87, 25.92) * mm, "construction": true});
            skLineSegment(sketch, "E14.9.1.2", {"start": v(28.87, 42.52) * mm, "end": v(45.47, 42.52) * mm, "construction": true});
            skLineSegment(sketch, "E14.9.1.3", {"start": v(45.47, 42.52) * mm, "end": v(45.47, 25.92) * mm, "construction": true});
            skLineSegment(sketch, "E14.9.2.0", {"start": v(28.87, 42.52) * mm, "end": v(45.47, 42.52) * mm, "construction": true});
            skLineSegment(sketch, "E14.9.2.1", {"start": v(28.87, 59.12) * mm, "end": v(28.87, 42.52) * mm, "construction": true});
            skLineSegment(sketch, "E14.9.2.2", {"start": v(28.87, 59.12) * mm, "end": v(45.47, 59.12) * mm, "construction": true});
            skLineSegment(sketch, "E14.9.2.3", {"start": v(45.47, 59.12) * mm, "end": v(45.47, 42.52) * mm, "construction": true});
            skLineSegment(sketch, "E14.9.3.0", {"start": v(28.87, 59.12) * mm, "end": v(45.47, 59.12) * mm, "construction": true});
            skLineSegment(sketch, "E14.9.3.1", {"start": v(28.87, 75.72) * mm, "end": v(28.87, 59.12) * mm, "construction": true});
            skLineSegment(sketch, "E14.9.3.2", {"start": v(28.87, 75.72) * mm, "end": v(45.47, 75.72) * mm, "construction": true});
            skLineSegment(sketch, "E14.9.3.3", {"start": v(45.47, 75.72) * mm, "end": v(45.47, 59.12) * mm, "construction": true});
            skLineSegment(sketch, "E14.9.4.0", {"start": v(28.87, 75.72) * mm, "end": v(45.47, 75.72) * mm, "construction": true});
            skLineSegment(sketch, "E14.9.4.1", {"start": v(28.87, 92.32) * mm, "end": v(28.87, 75.72) * mm, "construction": true});
            skLineSegment(sketch, "E14.9.4.2", {"start": v(28.87, 92.32) * mm, "end": v(45.47, 92.32) * mm, "construction": true});
            skLineSegment(sketch, "E14.9.4.3", {"start": v(45.47, 92.32) * mm, "end": v(45.47, 75.72) * mm, "construction": true});
            skLineSegment(sketch, "E14.9.5.0", {"start": v(28.87, 92.32) * mm, "end": v(45.47, 92.32) * mm, "construction": true});
            skLineSegment(sketch, "E14.9.5.1", {"start": v(28.87, 108.92) * mm, "end": v(28.87, 92.32) * mm, "construction": true});
            skLineSegment(sketch, "E14.9.5.2", {"start": v(28.87, 108.92) * mm, "end": v(45.47, 108.92) * mm, "construction": true});
            skLineSegment(sketch, "E14.9.5.3", {"start": v(45.47, 108.92) * mm, "end": v(45.47, 92.32) * mm, "construction": true});
            skLineSegment(sketch, "E14.9.6.0", {"start": v(28.87, 108.92) * mm, "end": v(45.47, 108.92) * mm, "construction": true});
            skLineSegment(sketch, "E14.9.6.1", {"start": v(28.87, 125.52) * mm, "end": v(28.87, 108.92) * mm, "construction": true});
            skLineSegment(sketch, "E14.9.6.2", {"start": v(28.87, 125.52) * mm, "end": v(45.47, 125.52) * mm, "construction": true});
            skLineSegment(sketch, "E14.9.6.3", {"start": v(45.47, 125.52) * mm, "end": v(45.47, 108.92) * mm, "construction": true});
            skLineSegment(sketch, "E14.9.7.0", {"start": v(28.87, 125.52) * mm, "end": v(45.47, 125.52) * mm, "construction": true});
            skLineSegment(sketch, "E14.9.7.1", {"start": v(28.87, 142.12) * mm, "end": v(28.87, 125.52) * mm, "construction": true});
            skLineSegment(sketch, "E14.9.7.2", {"start": v(28.87, 142.12) * mm, "end": v(45.47, 142.12) * mm, "construction": true});
            skLineSegment(sketch, "E14.9.7.3", {"start": v(45.47, 142.12) * mm, "end": v(45.47, 125.52) * mm, "construction": true});
            skLineSegment(sketch, "E14.9.8.0", {"start": v(28.87, 142.12) * mm, "end": v(45.47, 142.12) * mm, "construction": true});
            skLineSegment(sketch, "E14.9.8.1", {"start": v(28.87, 158.72) * mm, "end": v(28.87, 142.12) * mm, "construction": true});
            skLineSegment(sketch, "E14.9.8.2", {"start": v(28.87, 158.72) * mm, "end": v(45.47, 158.72) * mm, "construction": true});
            skLineSegment(sketch, "E14.9.8.3", {"start": v(45.47, 158.72) * mm, "end": v(45.47, 142.12) * mm, "construction": true});
            skLineSegment(sketch, "E14.9.9.0", {"start": v(28.87, 158.72) * mm, "end": v(45.47, 158.72) * mm, "construction": true});
            skLineSegment(sketch, "E14.9.9.1", {"start": v(28.87, 175.32) * mm, "end": v(28.87, 158.72) * mm, "construction": true});
            skLineSegment(sketch, "E14.9.9.2", {"start": v(28.87, 175.32) * mm, "end": v(45.47, 175.32) * mm, "construction": true});
            skLineSegment(sketch, "E14.9.9.3", {"start": v(45.47, 175.32) * mm, "end": v(45.47, 158.72) * mm, "construction": true});
            skLineSegment(sketch, "E14.9.10.0", {"start": v(28.87, 175.32) * mm, "end": v(45.47, 175.32) * mm, "construction": true});
            skLineSegment(sketch, "E14.9.10.1", {"start": v(28.87, 191.92) * mm, "end": v(28.87, 175.32) * mm, "construction": true});
            skLineSegment(sketch, "E14.9.10.2", {"start": v(28.87, 191.92) * mm, "end": v(45.47, 191.92) * mm, "construction": true});
            skLineSegment(sketch, "E14.9.10.3", {"start": v(45.47, 191.92) * mm, "end": v(45.47, 175.32) * mm, "construction": true});
            skLineSegment(sketch, "E14.9.11.0", {"start": v(28.87, 191.92) * mm, "end": v(45.47, 191.92) * mm, "construction": true});
            skLineSegment(sketch, "E14.9.11.1", {"start": v(28.87, 208.52) * mm, "end": v(28.87, 191.92) * mm, "construction": true});
            skLineSegment(sketch, "E14.9.11.2", {"start": v(28.87, 208.52) * mm, "end": v(45.47, 208.52) * mm, "construction": true});
            skLineSegment(sketch, "E14.9.11.3", {"start": v(45.47, 208.52) * mm, "end": v(45.47, 191.92) * mm, "construction": true});
            skLineSegment(sketch, "E14.9.12.0", {"start": v(28.87, 208.52) * mm, "end": v(45.47, 208.52) * mm, "construction": true});
            skLineSegment(sketch, "E14.9.12.1", {"start": v(28.87, 225.12) * mm, "end": v(28.87, 208.52) * mm, "construction": true});
            skLineSegment(sketch, "E14.9.12.2", {"start": v(28.87, 225.12) * mm, "end": v(45.47, 225.12) * mm, "construction": true});
            skLineSegment(sketch, "E14.9.12.3", {"start": v(45.47, 225.12) * mm, "end": v(45.47, 208.52) * mm, "construction": true});
            skLineSegment(sketch, "E14.9.13.0", {"start": v(28.87, 225.12) * mm, "end": v(45.47, 225.12) * mm, "construction": true});
            skLineSegment(sketch, "E14.9.13.1", {"start": v(28.87, 241.72) * mm, "end": v(28.87, 225.12) * mm, "construction": true});
            skLineSegment(sketch, "E14.9.13.2", {"start": v(28.87, 241.72) * mm, "end": v(45.47, 241.72) * mm, "construction": true});
            skLineSegment(sketch, "E14.9.13.3", {"start": v(45.47, 241.72) * mm, "end": v(45.47, 225.12) * mm, "construction": true});
            skLineSegment(sketch, "E14.9.14.0", {"start": v(28.87, 241.72) * mm, "end": v(45.47, 241.72) * mm, "construction": true});
            skLineSegment(sketch, "E14.9.14.1", {"start": v(28.87, 258.32) * mm, "end": v(28.87, 241.72) * mm, "construction": true});
            skLineSegment(sketch, "E14.9.14.2", {"start": v(28.87, 258.32) * mm, "end": v(45.47, 258.32) * mm, "construction": true});
            skLineSegment(sketch, "E14.9.14.3", {"start": v(45.47, 258.32) * mm, "end": v(45.47, 241.72) * mm, "construction": true});
            skLineSegment(sketch, "E14.9.15.0", {"start": v(28.87, 258.32) * mm, "end": v(45.47, 258.32) * mm, "construction": true});
            skLineSegment(sketch, "E14.9.15.1", {"start": v(28.87, 274.92) * mm, "end": v(28.87, 258.32) * mm, "construction": true});
            skLineSegment(sketch, "E14.9.15.2", {"start": v(28.87, 274.92) * mm, "end": v(45.47, 274.92) * mm, "construction": true});
            skLineSegment(sketch, "E14.9.15.3", {"start": v(45.47, 274.92) * mm, "end": v(45.47, 258.32) * mm, "construction": true});
            skLineSegment(sketch, "E14.10.0.0", {"start": v(45.47, 9.32) * mm, "end": v(62.07, 9.32) * mm, "construction": true});
            skLineSegment(sketch, "E14.10.0.1", {"start": v(45.47, 25.92) * mm, "end": v(45.47, 9.32) * mm, "construction": true});
            skLineSegment(sketch, "E14.10.0.2", {"start": v(45.47, 25.92) * mm, "end": v(62.07, 25.92) * mm, "construction": true});
            skLineSegment(sketch, "E14.10.0.3", {"start": v(62.07, 25.92) * mm, "end": v(62.07, 9.32) * mm, "construction": true});
            skLineSegment(sketch, "E14.10.1.0", {"start": v(45.47, 25.92) * mm, "end": v(62.07, 25.92) * mm, "construction": true});
            skLineSegment(sketch, "E14.10.1.1", {"start": v(45.47, 42.52) * mm, "end": v(45.47, 25.92) * mm, "construction": true});
            skLineSegment(sketch, "E14.10.1.2", {"start": v(45.47, 42.52) * mm, "end": v(62.07, 42.52) * mm, "construction": true});
            skLineSegment(sketch, "E14.10.1.3", {"start": v(62.07, 42.52) * mm, "end": v(62.07, 25.92) * mm, "construction": true});
            skLineSegment(sketch, "E14.10.2.0", {"start": v(45.47, 42.52) * mm, "end": v(62.07, 42.52) * mm, "construction": true});
            skLineSegment(sketch, "E14.10.2.1", {"start": v(45.47, 59.12) * mm, "end": v(45.47, 42.52) * mm, "construction": true});
            skLineSegment(sketch, "E14.10.2.2", {"start": v(45.47, 59.12) * mm, "end": v(62.07, 59.12) * mm, "construction": true});
            skLineSegment(sketch, "E14.10.2.3", {"start": v(62.07, 59.12) * mm, "end": v(62.07, 42.52) * mm, "construction": true});
            skLineSegment(sketch, "E14.10.3.0", {"start": v(45.47, 59.12) * mm, "end": v(62.07, 59.12) * mm, "construction": true});
            skLineSegment(sketch, "E14.10.3.1", {"start": v(45.47, 75.72) * mm, "end": v(45.47, 59.12) * mm, "construction": true});
            skLineSegment(sketch, "E14.10.3.2", {"start": v(45.47, 75.72) * mm, "end": v(62.07, 75.72) * mm, "construction": true});
            skLineSegment(sketch, "E14.10.3.3", {"start": v(62.07, 75.72) * mm, "end": v(62.07, 59.12) * mm, "construction": true});
            skLineSegment(sketch, "E14.10.4.0", {"start": v(45.47, 75.72) * mm, "end": v(62.07, 75.72) * mm, "construction": true});
            skLineSegment(sketch, "E14.10.4.1", {"start": v(45.47, 92.32) * mm, "end": v(45.47, 75.72) * mm, "construction": true});
            skLineSegment(sketch, "E14.10.4.2", {"start": v(45.47, 92.32) * mm, "end": v(62.07, 92.32) * mm, "construction": true});
            skLineSegment(sketch, "E14.10.4.3", {"start": v(62.07, 92.32) * mm, "end": v(62.07, 75.72) * mm, "construction": true});
            skLineSegment(sketch, "E14.10.5.0", {"start": v(45.47, 92.32) * mm, "end": v(62.07, 92.32) * mm, "construction": true});
            skLineSegment(sketch, "E14.10.5.1", {"start": v(45.47, 108.92) * mm, "end": v(45.47, 92.32) * mm, "construction": true});
            skLineSegment(sketch, "E14.10.5.2", {"start": v(45.47, 108.92) * mm, "end": v(62.07, 108.92) * mm, "construction": true});
            skLineSegment(sketch, "E14.10.5.3", {"start": v(62.07, 108.92) * mm, "end": v(62.07, 92.32) * mm, "construction": true});
            skLineSegment(sketch, "E14.10.6.0", {"start": v(45.47, 108.92) * mm, "end": v(62.07, 108.92) * mm, "construction": true});
            skLineSegment(sketch, "E14.10.6.1", {"start": v(45.47, 125.52) * mm, "end": v(45.47, 108.92) * mm, "construction": true});
            skLineSegment(sketch, "E14.10.6.2", {"start": v(45.47, 125.52) * mm, "end": v(62.07, 125.52) * mm, "construction": true});
            skLineSegment(sketch, "E14.10.6.3", {"start": v(62.07, 125.52) * mm, "end": v(62.07, 108.92) * mm, "construction": true});
            skLineSegment(sketch, "E14.10.7.0", {"start": v(45.47, 125.52) * mm, "end": v(62.07, 125.52) * mm, "construction": true});
            skLineSegment(sketch, "E14.10.7.1", {"start": v(45.47, 142.12) * mm, "end": v(45.47, 125.52) * mm, "construction": true});
            skLineSegment(sketch, "E14.10.7.2", {"start": v(45.47, 142.12) * mm, "end": v(62.07, 142.12) * mm, "construction": true});
            skLineSegment(sketch, "E14.10.7.3", {"start": v(62.07, 142.12) * mm, "end": v(62.07, 125.52) * mm, "construction": true});
            skLineSegment(sketch, "E14.10.8.0", {"start": v(45.47, 142.12) * mm, "end": v(62.07, 142.12) * mm, "construction": true});
            skLineSegment(sketch, "E14.10.8.1", {"start": v(45.47, 158.72) * mm, "end": v(45.47, 142.12) * mm, "construction": true});
            skLineSegment(sketch, "E14.10.8.2", {"start": v(45.47, 158.72) * mm, "end": v(62.07, 158.72) * mm, "construction": true});
            skLineSegment(sketch, "E14.10.8.3", {"start": v(62.07, 158.72) * mm, "end": v(62.07, 142.12) * mm, "construction": true});
            skLineSegment(sketch, "E14.10.9.0", {"start": v(45.47, 158.72) * mm, "end": v(62.07, 158.72) * mm, "construction": true});
            skLineSegment(sketch, "E14.10.9.1", {"start": v(45.47, 175.32) * mm, "end": v(45.47, 158.72) * mm, "construction": true});
            skLineSegment(sketch, "E14.10.9.2", {"start": v(45.47, 175.32) * mm, "end": v(62.07, 175.32) * mm, "construction": true});
            skLineSegment(sketch, "E14.10.9.3", {"start": v(62.07, 175.32) * mm, "end": v(62.07, 158.72) * mm, "construction": true});
            skLineSegment(sketch, "E14.10.10.0", {"start": v(45.47, 175.32) * mm, "end": v(62.07, 175.32) * mm, "construction": true});
            skLineSegment(sketch, "E14.10.10.1", {"start": v(45.47, 191.92) * mm, "end": v(45.47, 175.32) * mm, "construction": true});
            skLineSegment(sketch, "E14.10.10.2", {"start": v(45.47, 191.92) * mm, "end": v(62.07, 191.92) * mm, "construction": true});
            skLineSegment(sketch, "E14.10.10.3", {"start": v(62.07, 191.92) * mm, "end": v(62.07, 175.32) * mm, "construction": true});
            skLineSegment(sketch, "E14.10.11.0", {"start": v(45.47, 191.92) * mm, "end": v(62.07, 191.92) * mm, "construction": true});
            skLineSegment(sketch, "E14.10.11.1", {"start": v(45.47, 208.52) * mm, "end": v(45.47, 191.92) * mm, "construction": true});
            skLineSegment(sketch, "E14.10.11.2", {"start": v(45.47, 208.52) * mm, "end": v(62.07, 208.52) * mm, "construction": true});
            skLineSegment(sketch, "E14.10.11.3", {"start": v(62.07, 208.52) * mm, "end": v(62.07, 191.92) * mm, "construction": true});
            skLineSegment(sketch, "E14.10.12.0", {"start": v(45.47, 208.52) * mm, "end": v(62.07, 208.52) * mm, "construction": true});
            skLineSegment(sketch, "E14.10.12.1", {"start": v(45.47, 225.12) * mm, "end": v(45.47, 208.52) * mm, "construction": true});
            skLineSegment(sketch, "E14.10.12.2", {"start": v(45.47, 225.12) * mm, "end": v(62.07, 225.12) * mm, "construction": true});
            skLineSegment(sketch, "E14.10.12.3", {"start": v(62.07, 225.12) * mm, "end": v(62.07, 208.52) * mm, "construction": true});
            skLineSegment(sketch, "E14.10.13.0", {"start": v(45.47, 225.12) * mm, "end": v(62.07, 225.12) * mm, "construction": true});
            skLineSegment(sketch, "E14.10.13.1", {"start": v(45.47, 241.72) * mm, "end": v(45.47, 225.12) * mm, "construction": true});
            skLineSegment(sketch, "E14.10.13.2", {"start": v(45.47, 241.72) * mm, "end": v(62.07, 241.72) * mm, "construction": true});
            skLineSegment(sketch, "E14.10.13.3", {"start": v(62.07, 241.72) * mm, "end": v(62.07, 225.12) * mm, "construction": true});
            skLineSegment(sketch, "E14.10.14.0", {"start": v(45.47, 241.72) * mm, "end": v(62.07, 241.72) * mm, "construction": true});
            skLineSegment(sketch, "E14.10.14.1", {"start": v(45.47, 258.32) * mm, "end": v(45.47, 241.72) * mm, "construction": true});
            skLineSegment(sketch, "E14.10.14.2", {"start": v(45.47, 258.32) * mm, "end": v(62.07, 258.32) * mm, "construction": true});
            skLineSegment(sketch, "E14.10.14.3", {"start": v(62.07, 258.32) * mm, "end": v(62.07, 241.72) * mm, "construction": true});
            skLineSegment(sketch, "E14.10.15.0", {"start": v(45.47, 258.32) * mm, "end": v(62.07, 258.32) * mm, "construction": true});
            skLineSegment(sketch, "E14.10.15.1", {"start": v(45.47, 274.92) * mm, "end": v(45.47, 258.32) * mm, "construction": true});
            skLineSegment(sketch, "E14.10.15.2", {"start": v(45.47, 274.92) * mm, "end": v(62.07, 274.92) * mm, "construction": true});
            skLineSegment(sketch, "E14.10.15.3", {"start": v(62.07, 274.92) * mm, "end": v(62.07, 258.32) * mm, "construction": true});
            skLineSegment(sketch, "E14.11.0.0", {"start": v(62.07, 9.32) * mm, "end": v(78.67, 9.32) * mm, "construction": true});
            skLineSegment(sketch, "E14.11.0.1", {"start": v(62.07, 25.92) * mm, "end": v(62.07, 9.32) * mm, "construction": true});
            skLineSegment(sketch, "E14.11.0.2", {"start": v(62.07, 25.92) * mm, "end": v(78.67, 25.92) * mm, "construction": true});
            skLineSegment(sketch, "E14.11.0.3", {"start": v(78.67, 25.92) * mm, "end": v(78.67, 9.32) * mm, "construction": true});
            skLineSegment(sketch, "E14.11.1.0", {"start": v(62.07, 25.92) * mm, "end": v(78.67, 25.92) * mm, "construction": true});
            skLineSegment(sketch, "E14.11.1.1", {"start": v(62.07, 42.52) * mm, "end": v(62.07, 25.92) * mm, "construction": true});
            skLineSegment(sketch, "E14.11.1.2", {"start": v(62.07, 42.52) * mm, "end": v(78.67, 42.52) * mm, "construction": true});
            skLineSegment(sketch, "E14.11.1.3", {"start": v(78.67, 42.52) * mm, "end": v(78.67, 25.92) * mm, "construction": true});
            skLineSegment(sketch, "E14.11.2.0", {"start": v(62.07, 42.52) * mm, "end": v(78.67, 42.52) * mm, "construction": true});
            skLineSegment(sketch, "E14.11.2.1", {"start": v(62.07, 59.12) * mm, "end": v(62.07, 42.52) * mm, "construction": true});
            skLineSegment(sketch, "E14.11.2.2", {"start": v(62.07, 59.12) * mm, "end": v(78.67, 59.12) * mm, "construction": true});
            skLineSegment(sketch, "E14.11.2.3", {"start": v(78.67, 59.12) * mm, "end": v(78.67, 42.52) * mm, "construction": true});
            skLineSegment(sketch, "E14.11.3.0", {"start": v(62.07, 59.12) * mm, "end": v(78.67, 59.12) * mm, "construction": true});
            skLineSegment(sketch, "E14.11.3.1", {"start": v(62.07, 75.72) * mm, "end": v(62.07, 59.12) * mm, "construction": true});
            skLineSegment(sketch, "E14.11.3.2", {"start": v(62.07, 75.72) * mm, "end": v(78.67, 75.72) * mm, "construction": true});
            skLineSegment(sketch, "E14.11.3.3", {"start": v(78.67, 75.72) * mm, "end": v(78.67, 59.12) * mm, "construction": true});
            skLineSegment(sketch, "E14.11.4.0", {"start": v(62.07, 75.72) * mm, "end": v(78.67, 75.72) * mm, "construction": true});
            skLineSegment(sketch, "E14.11.4.1", {"start": v(62.07, 92.32) * mm, "end": v(62.07, 75.72) * mm, "construction": true});
            skLineSegment(sketch, "E14.11.4.2", {"start": v(62.07, 92.32) * mm, "end": v(78.67, 92.32) * mm, "construction": true});
            skLineSegment(sketch, "E14.11.4.3", {"start": v(78.67, 92.32) * mm, "end": v(78.67, 75.72) * mm, "construction": true});
            skLineSegment(sketch, "E14.11.5.0", {"start": v(62.07, 92.32) * mm, "end": v(78.67, 92.32) * mm, "construction": true});
            skLineSegment(sketch, "E14.11.5.1", {"start": v(62.07, 108.92) * mm, "end": v(62.07, 92.32) * mm, "construction": true});
            skLineSegment(sketch, "E14.11.5.2", {"start": v(62.07, 108.92) * mm, "end": v(78.67, 108.92) * mm, "construction": true});
            skLineSegment(sketch, "E14.11.5.3", {"start": v(78.67, 108.92) * mm, "end": v(78.67, 92.32) * mm, "construction": true});
            skLineSegment(sketch, "E14.11.6.0", {"start": v(62.07, 108.92) * mm, "end": v(78.67, 108.92) * mm, "construction": true});
            skLineSegment(sketch, "E14.11.6.1", {"start": v(62.07, 125.52) * mm, "end": v(62.07, 108.92) * mm, "construction": true});
            skLineSegment(sketch, "E14.11.6.2", {"start": v(62.07, 125.52) * mm, "end": v(78.67, 125.52) * mm, "construction": true});
            skLineSegment(sketch, "E14.11.6.3", {"start": v(78.67, 125.52) * mm, "end": v(78.67, 108.92) * mm, "construction": true});
            skLineSegment(sketch, "E14.11.7.0", {"start": v(62.07, 125.52) * mm, "end": v(78.67, 125.52) * mm, "construction": true});
            skLineSegment(sketch, "E14.11.7.1", {"start": v(62.07, 142.12) * mm, "end": v(62.07, 125.52) * mm, "construction": true});
            skLineSegment(sketch, "E14.11.7.2", {"start": v(62.07, 142.12) * mm, "end": v(78.67, 142.12) * mm, "construction": true});
            skLineSegment(sketch, "E14.11.7.3", {"start": v(78.67, 142.12) * mm, "end": v(78.67, 125.52) * mm, "construction": true});
            skLineSegment(sketch, "E14.11.8.0", {"start": v(62.07, 142.12) * mm, "end": v(78.67, 142.12) * mm, "construction": true});
            skLineSegment(sketch, "E14.11.8.1", {"start": v(62.07, 158.72) * mm, "end": v(62.07, 142.12) * mm, "construction": true});
            skLineSegment(sketch, "E14.11.8.2", {"start": v(62.07, 158.72) * mm, "end": v(78.67, 158.72) * mm, "construction": true});
            skLineSegment(sketch, "E14.11.8.3", {"start": v(78.67, 158.72) * mm, "end": v(78.67, 142.12) * mm, "construction": true});
            skLineSegment(sketch, "E14.11.9.0", {"start": v(62.07, 158.72) * mm, "end": v(78.67, 158.72) * mm, "construction": true});
            skLineSegment(sketch, "E14.11.9.1", {"start": v(62.07, 175.32) * mm, "end": v(62.07, 158.72) * mm, "construction": true});
            skLineSegment(sketch, "E14.11.9.2", {"start": v(62.07, 175.32) * mm, "end": v(78.67, 175.32) * mm, "construction": true});
            skLineSegment(sketch, "E14.11.9.3", {"start": v(78.67, 175.32) * mm, "end": v(78.67, 158.72) * mm, "construction": true});
            skLineSegment(sketch, "E14.11.10.0", {"start": v(62.07, 175.32) * mm, "end": v(78.67, 175.32) * mm, "construction": true});
            skLineSegment(sketch, "E14.11.10.1", {"start": v(62.07, 191.92) * mm, "end": v(62.07, 175.32) * mm, "construction": true});
            skLineSegment(sketch, "E14.11.10.2", {"start": v(62.07, 191.92) * mm, "end": v(78.67, 191.92) * mm, "construction": true});
            skLineSegment(sketch, "E14.11.10.3", {"start": v(78.67, 191.92) * mm, "end": v(78.67, 175.32) * mm, "construction": true});
            skLineSegment(sketch, "E14.11.11.0", {"start": v(62.07, 191.92) * mm, "end": v(78.67, 191.92) * mm, "construction": true});
            skLineSegment(sketch, "E14.11.11.1", {"start": v(62.07, 208.52) * mm, "end": v(62.07, 191.92) * mm, "construction": true});
            skLineSegment(sketch, "E14.11.11.2", {"start": v(62.07, 208.52) * mm, "end": v(78.67, 208.52) * mm, "construction": true});
            skLineSegment(sketch, "E14.11.11.3", {"start": v(78.67, 208.52) * mm, "end": v(78.67, 191.92) * mm, "construction": true});
            skLineSegment(sketch, "E14.11.12.0", {"start": v(62.07, 208.52) * mm, "end": v(78.67, 208.52) * mm, "construction": true});
            skLineSegment(sketch, "E14.11.12.1", {"start": v(62.07, 225.12) * mm, "end": v(62.07, 208.52) * mm, "construction": true});
            skLineSegment(sketch, "E14.11.12.2", {"start": v(62.07, 225.12) * mm, "end": v(78.67, 225.12) * mm, "construction": true});
            skLineSegment(sketch, "E14.11.12.3", {"start": v(78.67, 225.12) * mm, "end": v(78.67, 208.52) * mm, "construction": true});
            skLineSegment(sketch, "E14.11.13.0", {"start": v(62.07, 225.12) * mm, "end": v(78.67, 225.12) * mm, "construction": true});
            skLineSegment(sketch, "E14.11.13.1", {"start": v(62.07, 241.72) * mm, "end": v(62.07, 225.12) * mm, "construction": true});
            skLineSegment(sketch, "E14.11.13.2", {"start": v(62.07, 241.72) * mm, "end": v(78.67, 241.72) * mm, "construction": true});
            skLineSegment(sketch, "E14.11.13.3", {"start": v(78.67, 241.72) * mm, "end": v(78.67, 225.12) * mm, "construction": true});
            skLineSegment(sketch, "E14.11.14.0", {"start": v(62.07, 241.72) * mm, "end": v(78.67, 241.72) * mm, "construction": true});
            skLineSegment(sketch, "E14.11.14.1", {"start": v(62.07, 258.32) * mm, "end": v(62.07, 241.72) * mm, "construction": true});
            skLineSegment(sketch, "E14.11.14.2", {"start": v(62.07, 258.32) * mm, "end": v(78.67, 258.32) * mm, "construction": true});
            skLineSegment(sketch, "E14.11.14.3", {"start": v(78.67, 258.32) * mm, "end": v(78.67, 241.72) * mm, "construction": true});
            skLineSegment(sketch, "E14.11.15.0", {"start": v(62.07, 258.32) * mm, "end": v(78.67, 258.32) * mm, "construction": true});
            skLineSegment(sketch, "E14.11.15.1", {"start": v(62.07, 274.92) * mm, "end": v(62.07, 258.32) * mm, "construction": true});
            skLineSegment(sketch, "E14.11.15.2", {"start": v(62.07, 274.92) * mm, "end": v(78.67, 274.92) * mm, "construction": true});
            skLineSegment(sketch, "E14.11.15.3", {"start": v(78.67, 274.92) * mm, "end": v(78.67, 258.32) * mm, "construction": true});
            skLineSegment(sketch, "E14.12.0.0", {"start": v(78.67, 9.32) * mm, "end": v(95.27, 9.32) * mm, "construction": true});
            skLineSegment(sketch, "E14.12.0.1", {"start": v(78.67, 25.92) * mm, "end": v(78.67, 9.32) * mm, "construction": true});
            skLineSegment(sketch, "E14.12.0.2", {"start": v(78.67, 25.92) * mm, "end": v(95.27, 25.92) * mm, "construction": true});
            skLineSegment(sketch, "E14.12.0.3", {"start": v(95.27, 25.92) * mm, "end": v(95.27, 9.32) * mm, "construction": true});
            skLineSegment(sketch, "E14.12.1.0", {"start": v(78.67, 25.92) * mm, "end": v(95.27, 25.92) * mm, "construction": true});
            skLineSegment(sketch, "E14.12.1.1", {"start": v(78.67, 42.52) * mm, "end": v(78.67, 25.92) * mm, "construction": true});
            skLineSegment(sketch, "E14.12.1.2", {"start": v(78.67, 42.52) * mm, "end": v(95.27, 42.52) * mm, "construction": true});
            skLineSegment(sketch, "E14.12.1.3", {"start": v(95.27, 42.52) * mm, "end": v(95.27, 25.92) * mm, "construction": true});
            skLineSegment(sketch, "E14.12.2.0", {"start": v(78.67, 42.52) * mm, "end": v(95.27, 42.52) * mm, "construction": true});
            skLineSegment(sketch, "E14.12.2.1", {"start": v(78.67, 59.12) * mm, "end": v(78.67, 42.52) * mm, "construction": true});
            skLineSegment(sketch, "E14.12.2.2", {"start": v(78.67, 59.12) * mm, "end": v(95.27, 59.12) * mm, "construction": true});
            skLineSegment(sketch, "E14.12.2.3", {"start": v(95.27, 59.12) * mm, "end": v(95.27, 42.52) * mm, "construction": true});
            skLineSegment(sketch, "E14.12.3.0", {"start": v(78.67, 59.12) * mm, "end": v(95.27, 59.12) * mm, "construction": true});
            skLineSegment(sketch, "E14.12.3.1", {"start": v(78.67, 75.72) * mm, "end": v(78.67, 59.12) * mm, "construction": true});
            skLineSegment(sketch, "E14.12.3.2", {"start": v(78.67, 75.72) * mm, "end": v(95.27, 75.72) * mm, "construction": true});
            skLineSegment(sketch, "E14.12.3.3", {"start": v(95.27, 75.72) * mm, "end": v(95.27, 59.12) * mm, "construction": true});
            skLineSegment(sketch, "E14.12.4.0", {"start": v(78.67, 75.72) * mm, "end": v(95.27, 75.72) * mm, "construction": true});
            skLineSegment(sketch, "E14.12.4.1", {"start": v(78.67, 92.32) * mm, "end": v(78.67, 75.72) * mm, "construction": true});
            skLineSegment(sketch, "E14.12.4.2", {"start": v(78.67, 92.32) * mm, "end": v(95.27, 92.32) * mm, "construction": true});
            skLineSegment(sketch, "E14.12.4.3", {"start": v(95.27, 92.32) * mm, "end": v(95.27, 75.72) * mm, "construction": true});
            skLineSegment(sketch, "E14.12.5.0", {"start": v(78.67, 92.32) * mm, "end": v(95.27, 92.32) * mm, "construction": true});
            skLineSegment(sketch, "E14.12.5.1", {"start": v(78.67, 108.92) * mm, "end": v(78.67, 92.32) * mm, "construction": true});
            skLineSegment(sketch, "E14.12.5.2", {"start": v(78.67, 108.92) * mm, "end": v(95.27, 108.92) * mm, "construction": true});
            skLineSegment(sketch, "E14.12.5.3", {"start": v(95.27, 108.92) * mm, "end": v(95.27, 92.32) * mm, "construction": true});
            skLineSegment(sketch, "E14.12.6.0", {"start": v(78.67, 108.92) * mm, "end": v(95.27, 108.92) * mm, "construction": true});
            skLineSegment(sketch, "E14.12.6.1", {"start": v(78.67, 125.52) * mm, "end": v(78.67, 108.92) * mm, "construction": true});
            skLineSegment(sketch, "E14.12.6.2", {"start": v(78.67, 125.52) * mm, "end": v(95.27, 125.52) * mm, "construction": true});
            skLineSegment(sketch, "E14.12.6.3", {"start": v(95.27, 125.52) * mm, "end": v(95.27, 108.92) * mm, "construction": true});
            skLineSegment(sketch, "E14.12.7.0", {"start": v(78.67, 125.52) * mm, "end": v(95.27, 125.52) * mm, "construction": true});
            skLineSegment(sketch, "E14.12.7.1", {"start": v(78.67, 142.12) * mm, "end": v(78.67, 125.52) * mm, "construction": true});
            skLineSegment(sketch, "E14.12.7.2", {"start": v(78.67, 142.12) * mm, "end": v(95.27, 142.12) * mm, "construction": true});
            skLineSegment(sketch, "E14.12.7.3", {"start": v(95.27, 142.12) * mm, "end": v(95.27, 125.52) * mm, "construction": true});
            skLineSegment(sketch, "E14.12.8.0", {"start": v(78.67, 142.12) * mm, "end": v(95.27, 142.12) * mm, "construction": true});
            skLineSegment(sketch, "E14.12.8.1", {"start": v(78.67, 158.72) * mm, "end": v(78.67, 142.12) * mm, "construction": true});
            skLineSegment(sketch, "E14.12.8.2", {"start": v(78.67, 158.72) * mm, "end": v(95.27, 158.72) * mm, "construction": true});
            skLineSegment(sketch, "E14.12.8.3", {"start": v(95.27, 158.72) * mm, "end": v(95.27, 142.12) * mm, "construction": true});
            skLineSegment(sketch, "E14.12.9.0", {"start": v(78.67, 158.72) * mm, "end": v(95.27, 158.72) * mm, "construction": true});
            skLineSegment(sketch, "E14.12.9.1", {"start": v(78.67, 175.32) * mm, "end": v(78.67, 158.72) * mm, "construction": true});
            skLineSegment(sketch, "E14.12.9.2", {"start": v(78.67, 175.32) * mm, "end": v(95.27, 175.32) * mm, "construction": true});
            skLineSegment(sketch, "E14.12.9.3", {"start": v(95.27, 175.32) * mm, "end": v(95.27, 158.72) * mm, "construction": true});
            skLineSegment(sketch, "E14.12.10.0", {"start": v(78.67, 175.32) * mm, "end": v(95.27, 175.32) * mm, "construction": true});
            skLineSegment(sketch, "E14.12.10.1", {"start": v(78.67, 191.92) * mm, "end": v(78.67, 175.32) * mm, "construction": true});
            skLineSegment(sketch, "E14.12.10.2", {"start": v(78.67, 191.92) * mm, "end": v(95.27, 191.92) * mm, "construction": true});
            skLineSegment(sketch, "E14.12.10.3", {"start": v(95.27, 191.92) * mm, "end": v(95.27, 175.32) * mm, "construction": true});
            skLineSegment(sketch, "E14.12.11.0", {"start": v(78.67, 191.92) * mm, "end": v(95.27, 191.92) * mm, "construction": true});
            skLineSegment(sketch, "E14.12.11.1", {"start": v(78.67, 208.52) * mm, "end": v(78.67, 191.92) * mm, "construction": true});
            skLineSegment(sketch, "E14.12.11.2", {"start": v(78.67, 208.52) * mm, "end": v(95.27, 208.52) * mm, "construction": true});
            skLineSegment(sketch, "E14.12.11.3", {"start": v(95.27, 208.52) * mm, "end": v(95.27, 191.92) * mm, "construction": true});
            skLineSegment(sketch, "E14.12.12.0", {"start": v(78.67, 208.52) * mm, "end": v(95.27, 208.52) * mm, "construction": true});
            skLineSegment(sketch, "E14.12.12.1", {"start": v(78.67, 225.12) * mm, "end": v(78.67, 208.52) * mm, "construction": true});
            skLineSegment(sketch, "E14.12.12.2", {"start": v(78.67, 225.12) * mm, "end": v(95.27, 225.12) * mm, "construction": true});
            skLineSegment(sketch, "E14.12.12.3", {"start": v(95.27, 225.12) * mm, "end": v(95.27, 208.52) * mm, "construction": true});
            skLineSegment(sketch, "E14.12.13.0", {"start": v(78.67, 225.12) * mm, "end": v(95.27, 225.12) * mm, "construction": true});
            skLineSegment(sketch, "E14.12.13.1", {"start": v(78.67, 241.72) * mm, "end": v(78.67, 225.12) * mm, "construction": true});
            skLineSegment(sketch, "E14.12.13.2", {"start": v(78.67, 241.72) * mm, "end": v(95.27, 241.72) * mm, "construction": true});
            skLineSegment(sketch, "E14.12.13.3", {"start": v(95.27, 241.72) * mm, "end": v(95.27, 225.12) * mm, "construction": true});
            skLineSegment(sketch, "E14.12.14.0", {"start": v(78.67, 241.72) * mm, "end": v(95.27, 241.72) * mm, "construction": true});
            skLineSegment(sketch, "E14.12.14.1", {"start": v(78.67, 258.32) * mm, "end": v(78.67, 241.72) * mm, "construction": true});
            skLineSegment(sketch, "E14.12.14.2", {"start": v(78.67, 258.32) * mm, "end": v(95.27, 258.32) * mm, "construction": true});
            skLineSegment(sketch, "E14.12.14.3", {"start": v(95.27, 258.32) * mm, "end": v(95.27, 241.72) * mm, "construction": true});
            skLineSegment(sketch, "E14.12.15.0", {"start": v(78.67, 258.32) * mm, "end": v(95.27, 258.32) * mm, "construction": true});
            skLineSegment(sketch, "E14.12.15.1", {"start": v(78.67, 274.92) * mm, "end": v(78.67, 258.32) * mm, "construction": true});
            skLineSegment(sketch, "E14.12.15.2", {"start": v(78.67, 274.92) * mm, "end": v(95.27, 274.92) * mm, "construction": true});
            skLineSegment(sketch, "E14.12.15.3", {"start": v(95.27, 274.92) * mm, "end": v(95.27, 258.32) * mm, "construction": true});
            skLineSegment(sketch, "E14.13.0.0", {"start": v(95.27, 9.32) * mm, "end": v(111.87, 9.32) * mm, "construction": true});
            skLineSegment(sketch, "E14.13.0.1", {"start": v(95.27, 25.92) * mm, "end": v(95.27, 9.32) * mm, "construction": true});
            skLineSegment(sketch, "E14.13.0.2", {"start": v(95.27, 25.92) * mm, "end": v(111.87, 25.92) * mm, "construction": true});
            skLineSegment(sketch, "E14.13.0.3", {"start": v(111.87, 25.92) * mm, "end": v(111.87, 9.32) * mm, "construction": true});
            skLineSegment(sketch, "E14.13.1.0", {"start": v(95.27, 25.92) * mm, "end": v(111.87, 25.92) * mm, "construction": true});
            skLineSegment(sketch, "E14.13.1.1", {"start": v(95.27, 42.52) * mm, "end": v(95.27, 25.92) * mm, "construction": true});
            skLineSegment(sketch, "E14.13.1.2", {"start": v(95.27, 42.52) * mm, "end": v(111.87, 42.52) * mm, "construction": true});
            skLineSegment(sketch, "E14.13.1.3", {"start": v(111.87, 42.52) * mm, "end": v(111.87, 25.92) * mm, "construction": true});
            skLineSegment(sketch, "E14.13.2.0", {"start": v(95.27, 42.52) * mm, "end": v(111.87, 42.52) * mm, "construction": true});
            skLineSegment(sketch, "E14.13.2.1", {"start": v(95.27, 59.12) * mm, "end": v(95.27, 42.52) * mm, "construction": true});
            skLineSegment(sketch, "E14.13.2.2", {"start": v(95.27, 59.12) * mm, "end": v(111.87, 59.12) * mm, "construction": true});
            skLineSegment(sketch, "E14.13.2.3", {"start": v(111.87, 59.12) * mm, "end": v(111.87, 42.52) * mm, "construction": true});
            skLineSegment(sketch, "E14.13.3.0", {"start": v(95.27, 59.12) * mm, "end": v(111.87, 59.12) * mm, "construction": true});
            skLineSegment(sketch, "E14.13.3.1", {"start": v(95.27, 75.72) * mm, "end": v(95.27, 59.12) * mm, "construction": true});
            skLineSegment(sketch, "E14.13.3.2", {"start": v(95.27, 75.72) * mm, "end": v(111.87, 75.72) * mm, "construction": true});
            skLineSegment(sketch, "E14.13.3.3", {"start": v(111.87, 75.72) * mm, "end": v(111.87, 59.12) * mm, "construction": true});
            skLineSegment(sketch, "E14.13.4.0", {"start": v(95.27, 75.72) * mm, "end": v(111.87, 75.72) * mm, "construction": true});
            skLineSegment(sketch, "E14.13.4.1", {"start": v(95.27, 92.32) * mm, "end": v(95.27, 75.72) * mm, "construction": true});
            skLineSegment(sketch, "E14.13.4.2", {"start": v(95.27, 92.32) * mm, "end": v(111.87, 92.32) * mm, "construction": true});
            skLineSegment(sketch, "E14.13.4.3", {"start": v(111.87, 92.32) * mm, "end": v(111.87, 75.72) * mm, "construction": true});
            skLineSegment(sketch, "E14.13.5.0", {"start": v(95.27, 92.32) * mm, "end": v(111.87, 92.32) * mm, "construction": true});
            skLineSegment(sketch, "E14.13.5.1", {"start": v(95.27, 108.92) * mm, "end": v(95.27, 92.32) * mm, "construction": true});
            skLineSegment(sketch, "E14.13.5.2", {"start": v(95.27, 108.92) * mm, "end": v(111.87, 108.92) * mm, "construction": true});
            skLineSegment(sketch, "E14.13.5.3", {"start": v(111.87, 108.92) * mm, "end": v(111.87, 92.32) * mm, "construction": true});
            skLineSegment(sketch, "E14.13.6.0", {"start": v(95.27, 108.92) * mm, "end": v(111.87, 108.92) * mm, "construction": true});
            skLineSegment(sketch, "E14.13.6.1", {"start": v(95.27, 125.52) * mm, "end": v(95.27, 108.92) * mm, "construction": true});
            skLineSegment(sketch, "E14.13.6.2", {"start": v(95.27, 125.52) * mm, "end": v(111.87, 125.52) * mm, "construction": true});
            skLineSegment(sketch, "E14.13.6.3", {"start": v(111.87, 125.52) * mm, "end": v(111.87, 108.92) * mm, "construction": true});
            skLineSegment(sketch, "E14.13.7.0", {"start": v(95.27, 125.52) * mm, "end": v(111.87, 125.52) * mm, "construction": true});
            skLineSegment(sketch, "E14.13.7.1", {"start": v(95.27, 142.12) * mm, "end": v(95.27, 125.52) * mm, "construction": true});
            skLineSegment(sketch, "E14.13.7.2", {"start": v(95.27, 142.12) * mm, "end": v(111.87, 142.12) * mm, "construction": true});
            skLineSegment(sketch, "E14.13.7.3", {"start": v(111.87, 142.12) * mm, "end": v(111.87, 125.52) * mm, "construction": true});
            skLineSegment(sketch, "E14.13.8.0", {"start": v(95.27, 142.12) * mm, "end": v(111.87, 142.12) * mm, "construction": true});
            skLineSegment(sketch, "E14.13.8.1", {"start": v(95.27, 158.72) * mm, "end": v(95.27, 142.12) * mm, "construction": true});
            skLineSegment(sketch, "E14.13.8.2", {"start": v(95.27, 158.72) * mm, "end": v(111.87, 158.72) * mm, "construction": true});
            skLineSegment(sketch, "E14.13.8.3", {"start": v(111.87, 158.72) * mm, "end": v(111.87, 142.12) * mm, "construction": true});
            skLineSegment(sketch, "E14.13.9.0", {"start": v(95.27, 158.72) * mm, "end": v(111.87, 158.72) * mm, "construction": true});
            skLineSegment(sketch, "E14.13.9.1", {"start": v(95.27, 175.32) * mm, "end": v(95.27, 158.72) * mm, "construction": true});
            skLineSegment(sketch, "E14.13.9.2", {"start": v(95.27, 175.32) * mm, "end": v(111.87, 175.32) * mm, "construction": true});
            skLineSegment(sketch, "E14.13.9.3", {"start": v(111.87, 175.32) * mm, "end": v(111.87, 158.72) * mm, "construction": true});
            skLineSegment(sketch, "E14.13.10.0", {"start": v(95.27, 175.32) * mm, "end": v(111.87, 175.32) * mm, "construction": true});
            skLineSegment(sketch, "E14.13.10.1", {"start": v(95.27, 191.92) * mm, "end": v(95.27, 175.32) * mm, "construction": true});
            skLineSegment(sketch, "E14.13.10.2", {"start": v(95.27, 191.92) * mm, "end": v(111.87, 191.92) * mm, "construction": true});
            skLineSegment(sketch, "E14.13.10.3", {"start": v(111.87, 191.92) * mm, "end": v(111.87, 175.32) * mm, "construction": true});
            skLineSegment(sketch, "E14.13.11.0", {"start": v(95.27, 191.92) * mm, "end": v(111.87, 191.92) * mm, "construction": true});
            skLineSegment(sketch, "E14.13.11.1", {"start": v(95.27, 208.52) * mm, "end": v(95.27, 191.92) * mm, "construction": true});
            skLineSegment(sketch, "E14.13.11.2", {"start": v(95.27, 208.52) * mm, "end": v(111.87, 208.52) * mm, "construction": true});
            skLineSegment(sketch, "E14.13.11.3", {"start": v(111.87, 208.52) * mm, "end": v(111.87, 191.92) * mm, "construction": true});
            skLineSegment(sketch, "E14.13.12.0", {"start": v(95.27, 208.52) * mm, "end": v(111.87, 208.52) * mm, "construction": true});
            skLineSegment(sketch, "E14.13.12.1", {"start": v(95.27, 225.12) * mm, "end": v(95.27, 208.52) * mm, "construction": true});
            skLineSegment(sketch, "E14.13.12.2", {"start": v(95.27, 225.12) * mm, "end": v(111.87, 225.12) * mm, "construction": true});
            skLineSegment(sketch, "E14.13.12.3", {"start": v(111.87, 225.12) * mm, "end": v(111.87, 208.52) * mm, "construction": true});
            skLineSegment(sketch, "E14.13.13.0", {"start": v(95.27, 225.12) * mm, "end": v(111.87, 225.12) * mm, "construction": true});
            skLineSegment(sketch, "E14.13.13.1", {"start": v(95.27, 241.72) * mm, "end": v(95.27, 225.12) * mm, "construction": true});
            skLineSegment(sketch, "E14.13.13.2", {"start": v(95.27, 241.72) * mm, "end": v(111.87, 241.72) * mm, "construction": true});
            skLineSegment(sketch, "E14.13.13.3", {"start": v(111.87, 241.72) * mm, "end": v(111.87, 225.12) * mm, "construction": true});
            skLineSegment(sketch, "E14.13.14.0", {"start": v(95.27, 241.72) * mm, "end": v(111.87, 241.72) * mm, "construction": true});
            skLineSegment(sketch, "E14.13.14.1", {"start": v(95.27, 258.32) * mm, "end": v(95.27, 241.72) * mm, "construction": true});
            skLineSegment(sketch, "E14.13.14.2", {"start": v(95.27, 258.32) * mm, "end": v(111.87, 258.32) * mm, "construction": true});
            skLineSegment(sketch, "E14.13.14.3", {"start": v(111.87, 258.32) * mm, "end": v(111.87, 241.72) * mm, "construction": true});
            skLineSegment(sketch, "E14.13.15.0", {"start": v(95.27, 258.32) * mm, "end": v(111.87, 258.32) * mm, "construction": true});
            skLineSegment(sketch, "E14.13.15.1", {"start": v(95.27, 274.92) * mm, "end": v(95.27, 258.32) * mm, "construction": true});
            skLineSegment(sketch, "E14.13.15.2", {"start": v(95.27, 274.92) * mm, "end": v(111.87, 274.92) * mm, "construction": true});
            skLineSegment(sketch, "E14.13.15.3", {"start": v(111.87, 274.92) * mm, "end": v(111.87, 258.32) * mm, "construction": true});
            skLineSegment(sketch, "E14.14.0.0", {"start": v(111.87, 9.32) * mm, "end": v(128.47, 9.32) * mm, "construction": true});
            skLineSegment(sketch, "E14.14.0.1", {"start": v(111.87, 25.92) * mm, "end": v(111.87, 9.32) * mm, "construction": true});
            skLineSegment(sketch, "E14.14.0.2", {"start": v(111.87, 25.92) * mm, "end": v(128.47, 25.92) * mm, "construction": true});
            skLineSegment(sketch, "E14.14.0.3", {"start": v(128.47, 25.92) * mm, "end": v(128.47, 9.32) * mm, "construction": true});
            skLineSegment(sketch, "E14.14.1.0", {"start": v(111.87, 25.92) * mm, "end": v(128.47, 25.92) * mm, "construction": true});
            skLineSegment(sketch, "E14.14.1.1", {"start": v(111.87, 42.52) * mm, "end": v(111.87, 25.92) * mm, "construction": true});
            skLineSegment(sketch, "E14.14.1.2", {"start": v(111.87, 42.52) * mm, "end": v(128.47, 42.52) * mm, "construction": true});
            skLineSegment(sketch, "E14.14.1.3", {"start": v(128.47, 42.52) * mm, "end": v(128.47, 25.92) * mm, "construction": true});
            skLineSegment(sketch, "E14.14.2.0", {"start": v(111.87, 42.52) * mm, "end": v(128.47, 42.52) * mm, "construction": true});
            skLineSegment(sketch, "E14.14.2.1", {"start": v(111.87, 59.12) * mm, "end": v(111.87, 42.52) * mm, "construction": true});
            skLineSegment(sketch, "E14.14.2.2", {"start": v(111.87, 59.12) * mm, "end": v(128.47, 59.12) * mm, "construction": true});
            skLineSegment(sketch, "E14.14.2.3", {"start": v(128.47, 59.12) * mm, "end": v(128.47, 42.52) * mm, "construction": true});
            skLineSegment(sketch, "E14.14.3.0", {"start": v(111.87, 59.12) * mm, "end": v(128.47, 59.12) * mm, "construction": true});
            skLineSegment(sketch, "E14.14.3.1", {"start": v(111.87, 75.72) * mm, "end": v(111.87, 59.12) * mm, "construction": true});
            skLineSegment(sketch, "E14.14.3.2", {"start": v(111.87, 75.72) * mm, "end": v(128.47, 75.72) * mm, "construction": true});
            skLineSegment(sketch, "E14.14.3.3", {"start": v(128.47, 75.72) * mm, "end": v(128.47, 59.12) * mm, "construction": true});
            skLineSegment(sketch, "E14.14.4.0", {"start": v(111.87, 75.72) * mm, "end": v(128.47, 75.72) * mm, "construction": true});
            skLineSegment(sketch, "E14.14.4.1", {"start": v(111.87, 92.32) * mm, "end": v(111.87, 75.72) * mm, "construction": true});
            skLineSegment(sketch, "E14.14.4.2", {"start": v(111.87, 92.32) * mm, "end": v(128.47, 92.32) * mm, "construction": true});
            skLineSegment(sketch, "E14.14.4.3", {"start": v(128.47, 92.32) * mm, "end": v(128.47, 75.72) * mm, "construction": true});
            skLineSegment(sketch, "E14.14.5.0", {"start": v(111.87, 92.32) * mm, "end": v(128.47, 92.32) * mm, "construction": true});
            skLineSegment(sketch, "E14.14.5.1", {"start": v(111.87, 108.92) * mm, "end": v(111.87, 92.32) * mm, "construction": true});
            skLineSegment(sketch, "E14.14.5.2", {"start": v(111.87, 108.92) * mm, "end": v(128.47, 108.92) * mm, "construction": true});
            skLineSegment(sketch, "E14.14.5.3", {"start": v(128.47, 108.92) * mm, "end": v(128.47, 92.32) * mm, "construction": true});
            skLineSegment(sketch, "E14.14.6.0", {"start": v(111.87, 108.92) * mm, "end": v(128.47, 108.92) * mm, "construction": true});
            skLineSegment(sketch, "E14.14.6.1", {"start": v(111.87, 125.52) * mm, "end": v(111.87, 108.92) * mm, "construction": true});
            skLineSegment(sketch, "E14.14.6.2", {"start": v(111.87, 125.52) * mm, "end": v(128.47, 125.52) * mm, "construction": true});
            skLineSegment(sketch, "E14.14.6.3", {"start": v(128.47, 125.52) * mm, "end": v(128.47, 108.92) * mm, "construction": true});
            skLineSegment(sketch, "E14.14.7.0", {"start": v(111.87, 125.52) * mm, "end": v(128.47, 125.52) * mm, "construction": true});
            skLineSegment(sketch, "E14.14.7.1", {"start": v(111.87, 142.12) * mm, "end": v(111.87, 125.52) * mm, "construction": true});
            skLineSegment(sketch, "E14.14.7.2", {"start": v(111.87, 142.12) * mm, "end": v(128.47, 142.12) * mm, "construction": true});
            skLineSegment(sketch, "E14.14.7.3", {"start": v(128.47, 142.12) * mm, "end": v(128.47, 125.52) * mm, "construction": true});
            skLineSegment(sketch, "E14.14.8.0", {"start": v(111.87, 142.12) * mm, "end": v(128.47, 142.12) * mm, "construction": true});
            skLineSegment(sketch, "E14.14.8.1", {"start": v(111.87, 158.72) * mm, "end": v(111.87, 142.12) * mm, "construction": true});
            skLineSegment(sketch, "E14.14.8.2", {"start": v(111.87, 158.72) * mm, "end": v(128.47, 158.72) * mm, "construction": true});
            skLineSegment(sketch, "E14.14.8.3", {"start": v(128.47, 158.72) * mm, "end": v(128.47, 142.12) * mm, "construction": true});
            skLineSegment(sketch, "E14.14.9.0", {"start": v(111.87, 158.72) * mm, "end": v(128.47, 158.72) * mm, "construction": true});
            skLineSegment(sketch, "E14.14.9.1", {"start": v(111.87, 175.32) * mm, "end": v(111.87, 158.72) * mm, "construction": true});
            skLineSegment(sketch, "E14.14.9.2", {"start": v(111.87, 175.32) * mm, "end": v(128.47, 175.32) * mm, "construction": true});
            skLineSegment(sketch, "E14.14.9.3", {"start": v(128.47, 175.32) * mm, "end": v(128.47, 158.72) * mm, "construction": true});
            skLineSegment(sketch, "E14.14.10.0", {"start": v(111.87, 175.32) * mm, "end": v(128.47, 175.32) * mm, "construction": true});
            skLineSegment(sketch, "E14.14.10.1", {"start": v(111.87, 191.92) * mm, "end": v(111.87, 175.32) * mm, "construction": true});
            skLineSegment(sketch, "E14.14.10.2", {"start": v(111.87, 191.92) * mm, "end": v(128.47, 191.92) * mm, "construction": true});
            skLineSegment(sketch, "E14.14.10.3", {"start": v(128.47, 191.92) * mm, "end": v(128.47, 175.32) * mm, "construction": true});
            skLineSegment(sketch, "E14.14.11.0", {"start": v(111.87, 191.92) * mm, "end": v(128.47, 191.92) * mm, "construction": true});
            skLineSegment(sketch, "E14.14.11.1", {"start": v(111.87, 208.52) * mm, "end": v(111.87, 191.92) * mm, "construction": true});
            skLineSegment(sketch, "E14.14.11.2", {"start": v(111.87, 208.52) * mm, "end": v(128.47, 208.52) * mm, "construction": true});
            skLineSegment(sketch, "E14.14.11.3", {"start": v(128.47, 208.52) * mm, "end": v(128.47, 191.92) * mm, "construction": true});
            skLineSegment(sketch, "E14.14.12.0", {"start": v(111.87, 208.52) * mm, "end": v(128.47, 208.52) * mm, "construction": true});
            skLineSegment(sketch, "E14.14.12.1", {"start": v(111.87, 225.12) * mm, "end": v(111.87, 208.52) * mm, "construction": true});
            skLineSegment(sketch, "E14.14.12.2", {"start": v(111.87, 225.12) * mm, "end": v(128.47, 225.12) * mm, "construction": true});
            skLineSegment(sketch, "E14.14.12.3", {"start": v(128.47, 225.12) * mm, "end": v(128.47, 208.52) * mm, "construction": true});
            skLineSegment(sketch, "E14.14.13.0", {"start": v(111.87, 225.12) * mm, "end": v(128.47, 225.12) * mm, "construction": true});
            skLineSegment(sketch, "E14.14.13.1", {"start": v(111.87, 241.72) * mm, "end": v(111.87, 225.12) * mm, "construction": true});
            skLineSegment(sketch, "E14.14.13.2", {"start": v(111.87, 241.72) * mm, "end": v(128.47, 241.72) * mm, "construction": true});
            skLineSegment(sketch, "E14.14.13.3", {"start": v(128.47, 241.72) * mm, "end": v(128.47, 225.12) * mm, "construction": true});
            skLineSegment(sketch, "E14.14.14.0", {"start": v(111.87, 241.72) * mm, "end": v(128.47, 241.72) * mm, "construction": true});
            skLineSegment(sketch, "E14.14.14.1", {"start": v(111.87, 258.32) * mm, "end": v(111.87, 241.72) * mm, "construction": true});
            skLineSegment(sketch, "E14.14.14.2", {"start": v(111.87, 258.32) * mm, "end": v(128.47, 258.32) * mm, "construction": true});
            skLineSegment(sketch, "E14.14.14.3", {"start": v(128.47, 258.32) * mm, "end": v(128.47, 241.72) * mm, "construction": true});
            skLineSegment(sketch, "E14.14.15.0", {"start": v(111.87, 258.32) * mm, "end": v(128.47, 258.32) * mm, "construction": true});
            skLineSegment(sketch, "E14.14.15.1", {"start": v(111.87, 274.92) * mm, "end": v(111.87, 258.32) * mm, "construction": true});
            skLineSegment(sketch, "E14.14.15.2", {"start": v(111.87, 274.92) * mm, "end": v(128.47, 274.92) * mm, "construction": true});
            skLineSegment(sketch, "E14.14.15.3", {"start": v(128.47, 274.92) * mm, "end": v(128.47, 258.32) * mm, "construction": true});
            skLineSegment(sketch, "E14.15.0.0", {"start": v(128.47, 9.32) * mm, "end": v(145.07, 9.32) * mm, "construction": true});
            skLineSegment(sketch, "E14.15.0.1", {"start": v(128.47, 25.92) * mm, "end": v(128.47, 9.32) * mm, "construction": true});
            skLineSegment(sketch, "E14.15.0.2", {"start": v(128.47, 25.92) * mm, "end": v(145.07, 25.92) * mm, "construction": true});
            skLineSegment(sketch, "E14.15.0.3", {"start": v(145.07, 25.92) * mm, "end": v(145.07, 9.32) * mm, "construction": true});
            skLineSegment(sketch, "E14.15.1.0", {"start": v(128.47, 25.92) * mm, "end": v(145.07, 25.92) * mm, "construction": true});
            skLineSegment(sketch, "E14.15.1.1", {"start": v(128.47, 42.52) * mm, "end": v(128.47, 25.92) * mm, "construction": true});
            skLineSegment(sketch, "E14.15.1.2", {"start": v(128.47, 42.52) * mm, "end": v(145.07, 42.52) * mm, "construction": true});
            skLineSegment(sketch, "E14.15.1.3", {"start": v(145.07, 42.52) * mm, "end": v(145.07, 25.92) * mm, "construction": true});
            skLineSegment(sketch, "E14.15.2.0", {"start": v(128.47, 42.52) * mm, "end": v(145.07, 42.52) * mm, "construction": true});
            skLineSegment(sketch, "E14.15.2.1", {"start": v(128.47, 59.12) * mm, "end": v(128.47, 42.52) * mm, "construction": true});
            skLineSegment(sketch, "E14.15.2.2", {"start": v(128.47, 59.12) * mm, "end": v(145.07, 59.12) * mm, "construction": true});
            skLineSegment(sketch, "E14.15.2.3", {"start": v(145.07, 59.12) * mm, "end": v(145.07, 42.52) * mm, "construction": true});
            skLineSegment(sketch, "E14.15.3.0", {"start": v(128.47, 59.12) * mm, "end": v(145.07, 59.12) * mm, "construction": true});
            skLineSegment(sketch, "E14.15.3.1", {"start": v(128.47, 75.72) * mm, "end": v(128.47, 59.12) * mm, "construction": true});
            skLineSegment(sketch, "E14.15.3.2", {"start": v(128.47, 75.72) * mm, "end": v(145.07, 75.72) * mm, "construction": true});
            skLineSegment(sketch, "E14.15.3.3", {"start": v(145.07, 75.72) * mm, "end": v(145.07, 59.12) * mm, "construction": true});
            skLineSegment(sketch, "E14.15.4.0", {"start": v(128.47, 75.72) * mm, "end": v(145.07, 75.72) * mm, "construction": true});
            skLineSegment(sketch, "E14.15.4.1", {"start": v(128.47, 92.32) * mm, "end": v(128.47, 75.72) * mm, "construction": true});
            skLineSegment(sketch, "E14.15.4.2", {"start": v(128.47, 92.32) * mm, "end": v(145.07, 92.32) * mm, "construction": true});
            skLineSegment(sketch, "E14.15.4.3", {"start": v(145.07, 92.32) * mm, "end": v(145.07, 75.72) * mm, "construction": true});
            skLineSegment(sketch, "E14.15.5.0", {"start": v(128.47, 92.32) * mm, "end": v(145.07, 92.32) * mm, "construction": true});
            skLineSegment(sketch, "E14.15.5.1", {"start": v(128.47, 108.92) * mm, "end": v(128.47, 92.32) * mm, "construction": true});
            skLineSegment(sketch, "E14.15.5.2", {"start": v(128.47, 108.92) * mm, "end": v(145.07, 108.92) * mm, "construction": true});
            skLineSegment(sketch, "E14.15.5.3", {"start": v(145.07, 108.92) * mm, "end": v(145.07, 92.32) * mm, "construction": true});
            skLineSegment(sketch, "E14.15.6.0", {"start": v(128.47, 108.92) * mm, "end": v(145.07, 108.92) * mm, "construction": true});
            skLineSegment(sketch, "E14.15.6.1", {"start": v(128.47, 125.52) * mm, "end": v(128.47, 108.92) * mm, "construction": true});
            skLineSegment(sketch, "E14.15.6.2", {"start": v(128.47, 125.52) * mm, "end": v(145.07, 125.52) * mm, "construction": true});
            skLineSegment(sketch, "E14.15.6.3", {"start": v(145.07, 125.52) * mm, "end": v(145.07, 108.92) * mm, "construction": true});
            skLineSegment(sketch, "E14.15.7.0", {"start": v(128.47, 125.52) * mm, "end": v(145.07, 125.52) * mm, "construction": true});
            skLineSegment(sketch, "E14.15.7.1", {"start": v(128.47, 142.12) * mm, "end": v(128.47, 125.52) * mm, "construction": true});
            skLineSegment(sketch, "E14.15.7.2", {"start": v(128.47, 142.12) * mm, "end": v(145.07, 142.12) * mm, "construction": true});
            skLineSegment(sketch, "E14.15.7.3", {"start": v(145.07, 142.12) * mm, "end": v(145.07, 125.52) * mm, "construction": true});
            skLineSegment(sketch, "E14.15.8.0", {"start": v(128.47, 142.12) * mm, "end": v(145.07, 142.12) * mm, "construction": true});
            skLineSegment(sketch, "E14.15.8.1", {"start": v(128.47, 158.72) * mm, "end": v(128.47, 142.12) * mm, "construction": true});
            skLineSegment(sketch, "E14.15.8.2", {"start": v(128.47, 158.72) * mm, "end": v(145.07, 158.72) * mm, "construction": true});
            skLineSegment(sketch, "E14.15.8.3", {"start": v(145.07, 158.72) * mm, "end": v(145.07, 142.12) * mm, "construction": true});
            skLineSegment(sketch, "E14.15.9.0", {"start": v(128.47, 158.72) * mm, "end": v(145.07, 158.72) * mm, "construction": true});
            skLineSegment(sketch, "E14.15.9.1", {"start": v(128.47, 175.32) * mm, "end": v(128.47, 158.72) * mm, "construction": true});
            skLineSegment(sketch, "E14.15.9.2", {"start": v(128.47, 175.32) * mm, "end": v(145.07, 175.32) * mm, "construction": true});
            skLineSegment(sketch, "E14.15.9.3", {"start": v(145.07, 175.32) * mm, "end": v(145.07, 158.72) * mm, "construction": true});
            skLineSegment(sketch, "E14.15.10.0", {"start": v(128.47, 175.32) * mm, "end": v(145.07, 175.32) * mm, "construction": true});
            skLineSegment(sketch, "E14.15.10.1", {"start": v(128.47, 191.92) * mm, "end": v(128.47, 175.32) * mm, "construction": true});
            skLineSegment(sketch, "E14.15.10.2", {"start": v(128.47, 191.92) * mm, "end": v(145.07, 191.92) * mm, "construction": true});
            skLineSegment(sketch, "E14.15.10.3", {"start": v(145.07, 191.92) * mm, "end": v(145.07, 175.32) * mm, "construction": true});
            skLineSegment(sketch, "E14.15.11.0", {"start": v(128.47, 191.92) * mm, "end": v(145.07, 191.92) * mm, "construction": true});
            skLineSegment(sketch, "E14.15.11.1", {"start": v(128.47, 208.52) * mm, "end": v(128.47, 191.92) * mm, "construction": true});
            skLineSegment(sketch, "E14.15.11.2", {"start": v(128.47, 208.52) * mm, "end": v(145.07, 208.52) * mm, "construction": true});
            skLineSegment(sketch, "E14.15.11.3", {"start": v(145.07, 208.52) * mm, "end": v(145.07, 191.92) * mm, "construction": true});
            skLineSegment(sketch, "E14.15.12.0", {"start": v(128.47, 208.52) * mm, "end": v(145.07, 208.52) * mm, "construction": true});
            skLineSegment(sketch, "E14.15.12.1", {"start": v(128.47, 225.12) * mm, "end": v(128.47, 208.52) * mm, "construction": true});
            skLineSegment(sketch, "E14.15.12.2", {"start": v(128.47, 225.12) * mm, "end": v(145.07, 225.12) * mm, "construction": true});
            skLineSegment(sketch, "E14.15.12.3", {"start": v(145.07, 225.12) * mm, "end": v(145.07, 208.52) * mm, "construction": true});
            skLineSegment(sketch, "E14.15.13.0", {"start": v(128.47, 225.12) * mm, "end": v(145.07, 225.12) * mm, "construction": true});
            skLineSegment(sketch, "E14.15.13.1", {"start": v(128.47, 241.72) * mm, "end": v(128.47, 225.12) * mm, "construction": true});
            skLineSegment(sketch, "E14.15.13.2", {"start": v(128.47, 241.72) * mm, "end": v(145.07, 241.72) * mm, "construction": true});
            skLineSegment(sketch, "E14.15.13.3", {"start": v(145.07, 241.72) * mm, "end": v(145.07, 225.12) * mm, "construction": true});
            skLineSegment(sketch, "E14.15.14.0", {"start": v(128.47, 241.72) * mm, "end": v(145.07, 241.72) * mm, "construction": true});
            skLineSegment(sketch, "E14.15.14.1", {"start": v(128.47, 258.32) * mm, "end": v(128.47, 241.72) * mm, "construction": true});
            skLineSegment(sketch, "E14.15.14.2", {"start": v(128.47, 258.32) * mm, "end": v(145.07, 258.32) * mm, "construction": true});
            skLineSegment(sketch, "E14.15.14.3", {"start": v(145.07, 258.32) * mm, "end": v(145.07, 241.72) * mm, "construction": true});
            skLineSegment(sketch, "E14.15.15.0", {"start": v(128.47, 258.32) * mm, "end": v(145.07, 258.32) * mm, "construction": true});
            skLineSegment(sketch, "E14.15.15.1", {"start": v(128.47, 274.92) * mm, "end": v(128.47, 258.32) * mm, "construction": true});
            skLineSegment(sketch, "E14.15.15.2", {"start": v(128.47, 274.92) * mm, "end": v(145.07, 274.92) * mm, "construction": true});
            skLineSegment(sketch, "E14.15.15.3", {"start": v(145.07, 274.92) * mm, "end": v(145.07, 258.32) * mm, "construction": true});
            skLineSegment(sketch, "E14.direction2", {"start": v(-120.53, 9.32) * mm, "end": v(-120.53, 25.92) * mm, "construction": true});
            skCircle(sketch, "E15", {"center": v(-127.53, 281.92) * mm, "radius": 1.55 * mm});
            skCircle(sketch, "E16.1.0.0", {"center": v(-34.33, 281.92) * mm, "radius": 1.55 * mm});
            skCircle(sketch, "E16.2.0.0", {"center": v(58.87, 281.92) * mm, "radius": 1.55 * mm});
            skCircle(sketch, "E16.3.0.0", {"center": v(152.07, 281.92) * mm, "radius": 1.55 * mm});
            skLineSegment(sketch, "E16.direction1", {"start": v(-127.53, 281.92) * mm, "end": v(-34.33, 281.92) * mm, "construction": true});
            skLineSegment(sketch, "E16.direction2", {"start": v(-127.53, 281.92) * mm, "end": v(-127.53, 243.92) * mm, "construction": true});
            skCircle(sketch, "E17.MirrorC", {"center": v(-34.33, 2.32) * mm, "radius": 1.55 * mm});
            skCircle(sketch, "E18.MirrorC", {"center": v(58.87, 2.32) * mm, "radius": 1.55 * mm});
            skCircle(sketch, "E19.MirrorC", {"center": v(-127.53, 2.32) * mm, "radius": 1.55 * mm});
            skCircle(sketch, "E20.MirrorC", {"center": v(152.07, 2.32) * mm, "radius": 1.55 * mm});
            skCircle(sketch, "E21.0.1.0", {"center": v(152.07, 95.52) * mm, "radius": 1.55 * mm});
            skCircle(sketch, "E21.0.2.0", {"center": v(152.07, 188.72) * mm, "radius": 1.55 * mm});
            skLineSegment(sketch, "E21.direction1", {"start": v(152.07, 2.32) * mm, "end": v(177.07, 2.32) * mm, "construction": true});
            skLineSegment(sketch, "E21.direction2", {"start": v(152.07, 2.32) * mm, "end": v(152.07, 95.52) * mm, "construction": true});
            skCircle(sketch, "E22.MirrorC", {"center": v(-127.53, 188.72) * mm, "radius": 1.55 * mm});
            skCircle(sketch, "E23.MirrorC", {"center": v(-127.53, 95.52) * mm, "radius": 1.55 * mm});
            skSolve(sketch);
        }
        {
            var Q0;
            Q0=makeQuery(id+"F0.imprint","IMPRINT",FACE,{"disambiguationData":[TD([[makeQuery(id+"F0.imprint","IMPRINT",EDGE,{"derivedFrom":sQuery(id+"F0.wireOp",EDGE,"E1.bottom")}),-1.0]])]});
            var Q1;
            Q1=makeQuery(id+"F0.imprint","IMPRINT",FACE,{"disambiguationData":[TD([[makeQuery(id+"F0.imprint","IMPRINT",EDGE,{"derivedFrom":sQuery(id+"F0.wireOp",EDGE,"E15")}),1.0]])]});
            var Q2;
            Q2=makeQuery(id+"F0.imprint","IMPRINT",FACE,{"disambiguationData":[TD([[makeQuery(id+"F0.imprint","IMPRINT",EDGE,{"derivedFrom":sQuery(id+"F0.wireOp",EDGE,"E16.1.0.0")}),1.0]])]});
            var Q3;
            Q3=makeQuery(id+"F0.imprint","IMPRINT",FACE,{"disambiguationData":[TD([[makeQuery(id+"F0.imprint","IMPRINT",EDGE,{"derivedFrom":sQuery(id+"F0.wireOp",EDGE,"E16.2.0.0")}),1.0]])]});
            var Q4;
            Q4=makeQuery(id+"F0.imprint","IMPRINT",FACE,{"disambiguationData":[TD([[makeQuery(id+"F0.imprint","IMPRINT",EDGE,{"derivedFrom":sQuery(id+"F0.wireOp",EDGE,"E16.3.0.0")}),1.0]])]});
            var Q5;
            Q5=makeQuery(id+"F0.imprint","IMPRINT",FACE,{"disambiguationData":[TD([[makeQuery(id+"F0.imprint","IMPRINT",EDGE,{"derivedFrom":sQuery(id+"F0.wireOp",EDGE,"E21.0.2.0")}),-1.0]])]});
            var Q6;
            Q6=makeQuery(id+"F0.imprint","IMPRINT",FACE,{"disambiguationData":[TD([[makeQuery(id+"F0.imprint","IMPRINT",EDGE,{"derivedFrom":sQuery(id+"F0.wireOp",EDGE,"E21.0.1.0")}),-1.0]])]});
            var Q7;
            Q7=makeQuery(id+"F0.imprint","IMPRINT",FACE,{"disambiguationData":[TD([[makeQuery(id+"F0.imprint","IMPRINT",EDGE,{"derivedFrom":sQuery(id+"F0.wireOp",EDGE,"E20.MirrorC")}),-1.0]])]});
            var Q8;
            Q8=makeQuery(id+"F0.imprint","IMPRINT",FACE,{"disambiguationData":[TD([[makeQuery(id+"F0.imprint","IMPRINT",EDGE,{"derivedFrom":sQuery(id+"F0.wireOp",EDGE,"E18.MirrorC")}),-1.0]])]});
            var Q9;
            Q9=makeQuery(id+"F0.imprint","IMPRINT",FACE,{"disambiguationData":[TD([[makeQuery(id+"F0.imprint","IMPRINT",EDGE,{"derivedFrom":sQuery(id+"F0.wireOp",EDGE,"E17.MirrorC")}),-1.0]])]});
            var Q10;
            Q10=makeQuery(id+"F0.imprint","IMPRINT",FACE,{"disambiguationData":[TD([[makeQuery(id+"F0.imprint","IMPRINT",EDGE,{"derivedFrom":sQuery(id+"F0.wireOp",EDGE,"E19.MirrorC")}),-1.0]])]});
            var Q11;
            Q11=makeQuery(id+"F0.imprint","IMPRINT",FACE,{"disambiguationData":[TD([[makeQuery(id+"F0.imprint","IMPRINT",EDGE,{"derivedFrom":sQuery(id+"F0.wireOp",EDGE,"E23.MirrorC")}),1.0]])]});
            var Q12;
            Q12=makeQuery(id+"F0.imprint","IMPRINT",FACE,{"disambiguationData":[TD([[makeQuery(id+"F0.imprint","IMPRINT",EDGE,{"derivedFrom":sQuery(id+"F0.wireOp",EDGE,"E22.MirrorC")}),1.0]])]});
            extrude(context, id + "F1", {"entities" : qUnion([Q0, Q1, Q2, Q3, Q4, Q5, Q6, Q7, Q8, Q9, Q10, Q11, Q12]), "depth" : 8 * mm});
        }
        {
            var Q0;
            Q0=makeQuery(id+"F0.imprint","IMPRINT",FACE,{"disambiguationData":[TD([[makeQuery(id+"F0.imprint","IMPRINT",EDGE,{"derivedFrom":sQuery(id+"F0.wireOp",EDGE,"E3.bottom")}),-1.0]])]});
            var Q1;
            Q1=makeQuery(id+"F0.imprint","IMPRINT",FACE,{"disambiguationData":[TD([[makeQuery(id+"F0.imprint","IMPRINT",EDGE,{"derivedFrom":sQuery(id+"F0.wireOp",EDGE,"E3.top")}),1.0]])]});
            extrude(context, id + "F2", {"entities" : qUnion([Q0, Q1]), "operationType" : NewBodyOperationType.ADD, "depth" : 6 * mm});
        }
        {
            var Q0;
            Q0=qCreatedBy(makeId("Top.planeOp"),FACE);
            var sketch = newSketch(context, id + "F3", { "sketchPlane" : qUnion([Q0])});
            skLineSegment(sketch, "E24.0", {"start": v(-132.53, 286.92) * mm, "end": v(-132.53, -2.68) * mm, "construction": true});
            skLineSegment(sketch, "E24.1", {"start": v(-132.53, 286.92) * mm, "end": v(157.07, 286.92) * mm, "construction": true});
            skLineSegment(sketch, "E24.2", {"start": v(157.07, 286.92) * mm, "end": v(157.07, -2.68) * mm, "construction": true});
            skLineSegment(sketch, "E24.3", {"start": v(-132.53, -2.68) * mm, "end": v(157.07, -2.68) * mm, "construction": true});
            skLineSegment(sketch, "E25", {"start": v(-132.53, 142.67) * mm, "end": v(157.07, 142.67) * mm, "construction": true});
            skLineSegment(sketch, "E26", {"start": v(12.82, -2.68) * mm, "end": v(12.82, 286.92) * mm, "construction": true});
            skArc(sketch, "E27.0.startCap", {"start": v(-85.7, -2.68) * mm, "mid": v(-85.75, -2.73) * mm, "end": v(-85.8, -2.68) * mm});
            skArc(sketch, "E27.0.endCap", {"start": v(-85.8, 286.92) * mm, "mid": v(-85.75, 286.97) * mm, "end": v(-85.7, 286.92) * mm});
            skArc(sketch, "E27.1.startCap", {"start": v(12.87, -2.68) * mm, "mid": v(12.82, -2.73) * mm, "end": v(12.77, -2.68) * mm});
            skArc(sketch, "E27.1.endCap", {"start": v(12.77, 286.92) * mm, "mid": v(12.82, 286.97) * mm, "end": v(12.87, 286.92) * mm});
            skLineSegment(sketch, "E27.1.left", {"start": v(12.77, -2.68) * mm, "end": v(12.77, 286.92) * mm});
            skLineSegment(sketch, "E27.1.right", {"start": v(12.87, -2.68) * mm, "end": v(12.87, 286.92) * mm});
            skArc(sketch, "E27.2.startCap", {"start": v(-132.53, 142.62) * mm, "mid": v(-132.58, 142.67) * mm, "end": v(-132.53, 142.72) * mm});
            skArc(sketch, "E27.2.endCap", {"start": v(157.07, 142.72) * mm, "mid": v(157.12, 142.67) * mm, "end": v(157.07, 142.62) * mm});
            skLineSegment(sketch, "E27.2.left", {"start": v(-132.53, 142.72) * mm, "end": v(157.07, 142.72) * mm});
            skLineSegment(sketch, "E27.2.right", {"start": v(-132.53, 142.62) * mm, "end": v(157.07, 142.62) * mm});
            skArc(sketch, "E27.3.startCap", {"start": v(-132.53, 44.05) * mm, "mid": v(-132.58, 44.1) * mm, "end": v(-132.53, 44.15) * mm});
            skArc(sketch, "E27.3.endCap", {"start": v(157.07, 44.15) * mm, "mid": v(157.12, 44.1) * mm, "end": v(157.07, 44.05) * mm});
            skSolve(sketch);
        }
        {
            var Q0;
            Q0=makeQuery(id+"F0.imprint","IMPRINT",FACE,{"disambiguationData":[TD([[makeQuery(id+"F0.imprint","IMPRINT",EDGE,{"derivedFrom":sQuery(id+"F0.wireOp",EDGE,"E11.0.15.0")}),1.0]])]});
            var Q1;
            Q1=makeQuery(id+"F0.imprint","IMPRINT",FACE,{"disambiguationData":[TD([[makeQuery(id+"F0.imprint","IMPRINT",EDGE,{"derivedFrom":sQuery(id+"F0.wireOp",EDGE,"E11.1.15.0")}),1.0]])]});
            var Q2;
            Q2=makeQuery(id+"F0.imprint","IMPRINT",FACE,{"disambiguationData":[TD([[makeQuery(id+"F0.imprint","IMPRINT",EDGE,{"derivedFrom":sQuery(id+"F0.wireOp",EDGE,"E11.2.15.0")}),1.0]])]});
            var Q3;
            Q3=makeQuery(id+"F0.imprint","IMPRINT",FACE,{"disambiguationData":[TD([[makeQuery(id+"F0.imprint","IMPRINT",EDGE,{"derivedFrom":sQuery(id+"F0.wireOp",EDGE,"E11.3.15.0")}),1.0]])]});
            var Q4;
            Q4=makeQuery(id+"F0.imprint","IMPRINT",FACE,{"disambiguationData":[TD([[makeQuery(id+"F0.imprint","IMPRINT",EDGE,{"derivedFrom":sQuery(id+"F0.wireOp",EDGE,"E11.4.15.0")}),1.0]])]});
            var Q5;
            Q5=makeQuery(id+"F0.imprint","IMPRINT",FACE,{"disambiguationData":[TD([[makeQuery(id+"F0.imprint","IMPRINT",EDGE,{"derivedFrom":sQuery(id+"F0.wireOp",EDGE,"E11.4.14.0")}),1.0]])]});
            var Q6;
            Q6=makeQuery(id+"F0.imprint","IMPRINT",FACE,{"disambiguationData":[TD([[makeQuery(id+"F0.imprint","IMPRINT",EDGE,{"derivedFrom":sQuery(id+"F0.wireOp",EDGE,"E11.3.14.0")}),1.0]])]});
            var Q7;
            Q7=makeQuery(id+"F0.imprint","IMPRINT",FACE,{"disambiguationData":[TD([[makeQuery(id+"F0.imprint","IMPRINT",EDGE,{"derivedFrom":sQuery(id+"F0.wireOp",EDGE,"E11.2.14.0")}),1.0]])]});
            var Q8;
            Q8=makeQuery(id+"F0.imprint","IMPRINT",FACE,{"disambiguationData":[TD([[makeQuery(id+"F0.imprint","IMPRINT",EDGE,{"derivedFrom":sQuery(id+"F0.wireOp",EDGE,"E11.1.14.0")}),1.0]])]});
            var Q9;
            Q9=makeQuery(id+"F0.imprint","IMPRINT",FACE,{"disambiguationData":[TD([[makeQuery(id+"F0.imprint","IMPRINT",EDGE,{"derivedFrom":sQuery(id+"F0.wireOp",EDGE,"E11.0.14.0")}),1.0]])]});
            var Q10;
            Q10=makeQuery(id+"F0.imprint","IMPRINT",FACE,{"disambiguationData":[TD([[makeQuery(id+"F0.imprint","IMPRINT",EDGE,{"derivedFrom":sQuery(id+"F0.wireOp",EDGE,"E11.0.13.0")}),1.0]])]});
            var Q11;
            Q11=makeQuery(id+"F0.imprint","IMPRINT",FACE,{"disambiguationData":[TD([[makeQuery(id+"F0.imprint","IMPRINT",EDGE,{"derivedFrom":sQuery(id+"F0.wireOp",EDGE,"E11.1.13.0")}),1.0]])]});
            var Q12;
            Q12=makeQuery(id+"F0.imprint","IMPRINT",FACE,{"disambiguationData":[TD([[makeQuery(id+"F0.imprint","IMPRINT",EDGE,{"derivedFrom":sQuery(id+"F0.wireOp",EDGE,"E11.2.13.0")}),1.0]])]});
            var Q13;
            Q13=makeQuery(id+"F0.imprint","IMPRINT",FACE,{"disambiguationData":[TD([[makeQuery(id+"F0.imprint","IMPRINT",EDGE,{"derivedFrom":sQuery(id+"F0.wireOp",EDGE,"E11.3.13.0")}),1.0]])]});
            var Q14;
            Q14=makeQuery(id+"F0.imprint","IMPRINT",FACE,{"disambiguationData":[TD([[makeQuery(id+"F0.imprint","IMPRINT",EDGE,{"derivedFrom":sQuery(id+"F0.wireOp",EDGE,"E11.4.13.0")}),1.0]])]});
            var Q15;
            Q15=makeQuery(id+"F0.imprint","IMPRINT",FACE,{"disambiguationData":[TD([[makeQuery(id+"F0.imprint","IMPRINT",EDGE,{"derivedFrom":sQuery(id+"F0.wireOp",EDGE,"E11.5.13.0")}),1.0]])]});
            var Q16;
            Q16=makeQuery(id+"F0.imprint","IMPRINT",FACE,{"disambiguationData":[TD([[makeQuery(id+"F0.imprint","IMPRINT",EDGE,{"derivedFrom":sQuery(id+"F0.wireOp",EDGE,"E11.5.14.0")}),1.0]])]});
            var Q17;
            Q17=makeQuery(id+"F0.imprint","IMPRINT",FACE,{"disambiguationData":[TD([[makeQuery(id+"F0.imprint","IMPRINT",EDGE,{"derivedFrom":sQuery(id+"F0.wireOp",EDGE,"E11.5.15.0")}),1.0]])]});
            var Q18;
            Q18=makeQuery(id+"F0.imprint","IMPRINT",FACE,{"disambiguationData":[TD([[makeQuery(id+"F0.imprint","IMPRINT",EDGE,{"derivedFrom":sQuery(id+"F0.wireOp",EDGE,"E11.5.12.0")}),1.0]])]});
            var Q19;
            Q19=makeQuery(id+"F0.imprint","IMPRINT",FACE,{"disambiguationData":[TD([[makeQuery(id+"F0.imprint","IMPRINT",EDGE,{"derivedFrom":sQuery(id+"F0.wireOp",EDGE,"E11.4.12.0")}),1.0]])]});
            var Q20;
            Q20=makeQuery(id+"F0.imprint","IMPRINT",FACE,{"disambiguationData":[TD([[makeQuery(id+"F0.imprint","IMPRINT",EDGE,{"derivedFrom":sQuery(id+"F0.wireOp",EDGE,"E11.3.12.0")}),1.0]])]});
            var Q21;
            Q21=makeQuery(id+"F0.imprint","IMPRINT",FACE,{"disambiguationData":[TD([[makeQuery(id+"F0.imprint","IMPRINT",EDGE,{"derivedFrom":sQuery(id+"F0.wireOp",EDGE,"E11.2.12.0")}),1.0]])]});
            var Q22;
            Q22=makeQuery(id+"F0.imprint","IMPRINT",FACE,{"disambiguationData":[TD([[makeQuery(id+"F0.imprint","IMPRINT",EDGE,{"derivedFrom":sQuery(id+"F0.wireOp",EDGE,"E11.1.12.0")}),1.0]])]});
            var Q23;
            Q23=makeQuery(id+"F0.imprint","IMPRINT",FACE,{"disambiguationData":[TD([[makeQuery(id+"F0.imprint","IMPRINT",EDGE,{"derivedFrom":sQuery(id+"F0.wireOp",EDGE,"E11.0.12.0")}),1.0]])]});
            var Q24;
            Q24=makeQuery(id+"F0.imprint","IMPRINT",FACE,{"disambiguationData":[TD([[makeQuery(id+"F0.imprint","IMPRINT",EDGE,{"derivedFrom":sQuery(id+"F0.wireOp",EDGE,"E11.0.11.0")}),1.0]])]});
            var Q25;
            Q25=makeQuery(id+"F0.imprint","IMPRINT",FACE,{"disambiguationData":[TD([[makeQuery(id+"F0.imprint","IMPRINT",EDGE,{"derivedFrom":sQuery(id+"F0.wireOp",EDGE,"E11.1.11.0")}),1.0]])]});
            var Q26;
            Q26=makeQuery(id+"F0.imprint","IMPRINT",FACE,{"disambiguationData":[TD([[makeQuery(id+"F0.imprint","IMPRINT",EDGE,{"derivedFrom":sQuery(id+"F0.wireOp",EDGE,"E11.2.11.0")}),1.0]])]});
            var Q27;
            Q27=makeQuery(id+"F0.imprint","IMPRINT",FACE,{"disambiguationData":[TD([[makeQuery(id+"F0.imprint","IMPRINT",EDGE,{"derivedFrom":sQuery(id+"F0.wireOp",EDGE,"E11.3.11.0")}),1.0]])]});
            var Q28;
            Q28=makeQuery(id+"F0.imprint","IMPRINT",FACE,{"disambiguationData":[TD([[makeQuery(id+"F0.imprint","IMPRINT",EDGE,{"derivedFrom":sQuery(id+"F0.wireOp",EDGE,"E11.4.11.0")}),1.0]])]});
            var Q29;
            Q29=makeQuery(id+"F0.imprint","IMPRINT",FACE,{"disambiguationData":[TD([[makeQuery(id+"F0.imprint","IMPRINT",EDGE,{"derivedFrom":sQuery(id+"F0.wireOp",EDGE,"E11.5.11.0")}),1.0]])]});
            var Q30;
            Q30=makeQuery(id+"F0.imprint","IMPRINT",FACE,{"disambiguationData":[TD([[makeQuery(id+"F0.imprint","IMPRINT",EDGE,{"derivedFrom":sQuery(id+"F0.wireOp",EDGE,"E11.5.10.0")}),1.0]])]});
            var Q31;
            Q31=makeQuery(id+"F0.imprint","IMPRINT",FACE,{"disambiguationData":[TD([[makeQuery(id+"F0.imprint","IMPRINT",EDGE,{"derivedFrom":sQuery(id+"F0.wireOp",EDGE,"E11.4.10.0")}),1.0]])]});
            var Q32;
            Q32=makeQuery(id+"F0.imprint","IMPRINT",FACE,{"disambiguationData":[TD([[makeQuery(id+"F0.imprint","IMPRINT",EDGE,{"derivedFrom":sQuery(id+"F0.wireOp",EDGE,"E11.3.10.0")}),1.0]])]});
            var Q33;
            Q33=makeQuery(id+"F0.imprint","IMPRINT",FACE,{"disambiguationData":[TD([[makeQuery(id+"F0.imprint","IMPRINT",EDGE,{"derivedFrom":sQuery(id+"F0.wireOp",EDGE,"E11.2.10.0")}),1.0]])]});
            var Q34;
            Q34=makeQuery(id+"F0.imprint","IMPRINT",FACE,{"disambiguationData":[TD([[makeQuery(id+"F0.imprint","IMPRINT",EDGE,{"derivedFrom":sQuery(id+"F0.wireOp",EDGE,"E11.1.10.0")}),1.0]])]});
            var Q35;
            Q35=makeQuery(id+"F0.imprint","IMPRINT",FACE,{"disambiguationData":[TD([[makeQuery(id+"F0.imprint","IMPRINT",EDGE,{"derivedFrom":sQuery(id+"F0.wireOp",EDGE,"E11.0.10.0")}),1.0]])]});
            var Q36;
            Q36=makeQuery(id+"F0.imprint","IMPRINT",FACE,{"disambiguationData":[TD([[makeQuery(id+"F0.imprint","IMPRINT",EDGE,{"derivedFrom":sQuery(id+"F0.wireOp",EDGE,"E11.0.9.0")}),1.0]])]});
            var Q37;
            Q37=makeQuery(id+"F0.imprint","IMPRINT",FACE,{"disambiguationData":[TD([[makeQuery(id+"F0.imprint","IMPRINT",EDGE,{"derivedFrom":sQuery(id+"F0.wireOp",EDGE,"E11.1.9.0")}),1.0]])]});
            var Q38;
            Q38=makeQuery(id+"F0.imprint","IMPRINT",FACE,{"disambiguationData":[TD([[makeQuery(id+"F0.imprint","IMPRINT",EDGE,{"derivedFrom":sQuery(id+"F0.wireOp",EDGE,"E11.2.9.0")}),1.0]])]});
            var Q39;
            Q39=makeQuery(id+"F0.imprint","IMPRINT",FACE,{"disambiguationData":[TD([[makeQuery(id+"F0.imprint","IMPRINT",EDGE,{"derivedFrom":sQuery(id+"F0.wireOp",EDGE,"E11.3.9.0")}),1.0]])]});
            var Q40;
            Q40=makeQuery(id+"F0.imprint","IMPRINT",FACE,{"disambiguationData":[TD([[makeQuery(id+"F0.imprint","IMPRINT",EDGE,{"derivedFrom":sQuery(id+"F0.wireOp",EDGE,"E11.4.9.0")}),1.0]])]});
            var Q41;
            Q41=makeQuery(id+"F0.imprint","IMPRINT",FACE,{"disambiguationData":[TD([[makeQuery(id+"F0.imprint","IMPRINT",EDGE,{"derivedFrom":sQuery(id+"F0.wireOp",EDGE,"E11.5.9.0")}),1.0]])]});
            var Q42;
            Q42=makeQuery(id+"F0.imprint","IMPRINT",FACE,{"disambiguationData":[TD([[makeQuery(id+"F0.imprint","IMPRINT",EDGE,{"derivedFrom":sQuery(id+"F0.wireOp",EDGE,"E11.5.8.0")}),1.0]])]});
            var Q43;
            Q43=makeQuery(id+"F0.imprint","IMPRINT",FACE,{"disambiguationData":[TD([[makeQuery(id+"F0.imprint","IMPRINT",EDGE,{"derivedFrom":sQuery(id+"F0.wireOp",EDGE,"E11.4.8.0")}),1.0]])]});
            var Q44;
            Q44=makeQuery(id+"F0.imprint","IMPRINT",FACE,{"disambiguationData":[TD([[makeQuery(id+"F0.imprint","IMPRINT",EDGE,{"derivedFrom":sQuery(id+"F0.wireOp",EDGE,"E11.3.8.0")}),1.0]])]});
            var Q45;
            Q45=makeQuery(id+"F0.imprint","IMPRINT",FACE,{"disambiguationData":[TD([[makeQuery(id+"F0.imprint","IMPRINT",EDGE,{"derivedFrom":sQuery(id+"F0.wireOp",EDGE,"E11.2.8.0")}),1.0]])]});
            var Q46;
            Q46=makeQuery(id+"F0.imprint","IMPRINT",FACE,{"disambiguationData":[TD([[makeQuery(id+"F0.imprint","IMPRINT",EDGE,{"derivedFrom":sQuery(id+"F0.wireOp",EDGE,"E11.1.8.0")}),1.0]])]});
            var Q47;
            Q47=makeQuery(id+"F0.imprint","IMPRINT",FACE,{"disambiguationData":[TD([[makeQuery(id+"F0.imprint","IMPRINT",EDGE,{"derivedFrom":sQuery(id+"F0.wireOp",EDGE,"E11.0.8.0")}),1.0]])]});
            var Q48;
            Q48=makeQuery(id+"F0.imprint","IMPRINT",FACE,{"disambiguationData":[TD([[makeQuery(id+"F0.imprint","IMPRINT",EDGE,{"derivedFrom":sQuery(id+"F0.wireOp",EDGE,"E11.5.7.0")}),1.0]])]});
            var Q49;
            Q49=makeQuery(id+"F0.imprint","IMPRINT",FACE,{"disambiguationData":[TD([[makeQuery(id+"F0.imprint","IMPRINT",EDGE,{"derivedFrom":sQuery(id+"F0.wireOp",EDGE,"E11.4.7.0")}),1.0]])]});
            var Q50;
            Q50=makeQuery(id+"F0.imprint","IMPRINT",FACE,{"disambiguationData":[TD([[makeQuery(id+"F0.imprint","IMPRINT",EDGE,{"derivedFrom":sQuery(id+"F0.wireOp",EDGE,"E11.3.7.0")}),1.0]])]});
            var Q51;
            Q51=makeQuery(id+"F0.imprint","IMPRINT",FACE,{"disambiguationData":[TD([[makeQuery(id+"F0.imprint","IMPRINT",EDGE,{"derivedFrom":sQuery(id+"F0.wireOp",EDGE,"E11.2.7.0")}),1.0]])]});
            var Q52;
            Q52=makeQuery(id+"F0.imprint","IMPRINT",FACE,{"disambiguationData":[TD([[makeQuery(id+"F0.imprint","IMPRINT",EDGE,{"derivedFrom":sQuery(id+"F0.wireOp",EDGE,"E11.1.7.0")}),1.0]])]});
            var Q53;
            Q53=makeQuery(id+"F0.imprint","IMPRINT",FACE,{"disambiguationData":[TD([[makeQuery(id+"F0.imprint","IMPRINT",EDGE,{"derivedFrom":sQuery(id+"F0.wireOp",EDGE,"E11.0.7.0")}),1.0]])]});
            var Q54;
            Q54=makeQuery(id+"F0.imprint","IMPRINT",FACE,{"disambiguationData":[TD([[makeQuery(id+"F0.imprint","IMPRINT",EDGE,{"derivedFrom":sQuery(id+"F0.wireOp",EDGE,"E11.0.6.0")}),1.0]])]});
            var Q55;
            Q55=makeQuery(id+"F0.imprint","IMPRINT",FACE,{"disambiguationData":[TD([[makeQuery(id+"F0.imprint","IMPRINT",EDGE,{"derivedFrom":sQuery(id+"F0.wireOp",EDGE,"E11.0.5.0")}),1.0]])]});
            var Q56;
            Q56=makeQuery(id+"F0.imprint","IMPRINT",FACE,{"disambiguationData":[TD([[makeQuery(id+"F0.imprint","IMPRINT",EDGE,{"derivedFrom":sQuery(id+"F0.wireOp",EDGE,"E11.0.4.0")}),1.0]])]});
            var Q57;
            Q57=makeQuery(id+"F0.imprint","IMPRINT",FACE,{"disambiguationData":[TD([[makeQuery(id+"F0.imprint","IMPRINT",EDGE,{"derivedFrom":sQuery(id+"F0.wireOp",EDGE,"E11.0.3.0")}),1.0]])]});
            var Q58;
            Q58=makeQuery(id+"F0.imprint","IMPRINT",FACE,{"disambiguationData":[TD([[makeQuery(id+"F0.imprint","IMPRINT",EDGE,{"derivedFrom":sQuery(id+"F0.wireOp",EDGE,"E11.1.3.0")}),1.0]])]});
            var Q59;
            Q59=makeQuery(id+"F0.imprint","IMPRINT",FACE,{"disambiguationData":[TD([[makeQuery(id+"F0.imprint","IMPRINT",EDGE,{"derivedFrom":sQuery(id+"F0.wireOp",EDGE,"E11.2.3.0")}),1.0]])]});
            var Q60;
            Q60=makeQuery(id+"F0.imprint","IMPRINT",FACE,{"disambiguationData":[TD([[makeQuery(id+"F0.imprint","IMPRINT",EDGE,{"derivedFrom":sQuery(id+"F0.wireOp",EDGE,"E11.3.3.0")}),1.0]])]});
            var Q61;
            Q61=makeQuery(id+"F0.imprint","IMPRINT",FACE,{"disambiguationData":[TD([[makeQuery(id+"F0.imprint","IMPRINT",EDGE,{"derivedFrom":sQuery(id+"F0.wireOp",EDGE,"E11.4.3.0")}),1.0]])]});
            var Q62;
            Q62=makeQuery(id+"F0.imprint","IMPRINT",FACE,{"disambiguationData":[TD([[makeQuery(id+"F0.imprint","IMPRINT",EDGE,{"derivedFrom":sQuery(id+"F0.wireOp",EDGE,"E11.5.3.0")}),1.0]])]});
            var Q63;
            Q63=makeQuery(id+"F0.imprint","IMPRINT",FACE,{"disambiguationData":[TD([[makeQuery(id+"F0.imprint","IMPRINT",EDGE,{"derivedFrom":sQuery(id+"F0.wireOp",EDGE,"E11.6.3.0")}),1.0]])]});
            var Q64;
            Q64=makeQuery(id+"F0.imprint","IMPRINT",FACE,{"disambiguationData":[TD([[makeQuery(id+"F0.imprint","IMPRINT",EDGE,{"derivedFrom":sQuery(id+"F0.wireOp",EDGE,"E11.6.4.0")}),1.0]])]});
            var Q65;
            Q65=makeQuery(id+"F0.imprint","IMPRINT",FACE,{"disambiguationData":[TD([[makeQuery(id+"F0.imprint","IMPRINT",EDGE,{"derivedFrom":sQuery(id+"F0.wireOp",EDGE,"E11.6.5.0")}),1.0]])]});
            var Q66;
            Q66=makeQuery(id+"F0.imprint","IMPRINT",FACE,{"disambiguationData":[TD([[makeQuery(id+"F0.imprint","IMPRINT",EDGE,{"derivedFrom":sQuery(id+"F0.wireOp",EDGE,"E11.7.5.0")}),1.0]])]});
            var Q67;
            Q67=makeQuery(id+"F0.imprint","IMPRINT",FACE,{"disambiguationData":[TD([[makeQuery(id+"F0.imprint","IMPRINT",EDGE,{"derivedFrom":sQuery(id+"F0.wireOp",EDGE,"E11.7.4.0")}),1.0]])]});
            var Q68;
            Q68=makeQuery(id+"F0.imprint","IMPRINT",FACE,{"disambiguationData":[TD([[makeQuery(id+"F0.imprint","IMPRINT",EDGE,{"derivedFrom":sQuery(id+"F0.wireOp",EDGE,"E11.7.3.0")}),1.0]])]});
            var Q69;
            Q69=makeQuery(id+"F0.imprint","IMPRINT",FACE,{"disambiguationData":[TD([[makeQuery(id+"F0.imprint","IMPRINT",EDGE,{"derivedFrom":sQuery(id+"F0.wireOp",EDGE,"E11.5.4.0")}),1.0]])]});
            var Q70;
            Q70=makeQuery(id+"F0.imprint","IMPRINT",FACE,{"disambiguationData":[TD([[makeQuery(id+"F0.imprint","IMPRINT",EDGE,{"derivedFrom":sQuery(id+"F0.wireOp",EDGE,"E11.5.5.0")}),1.0]])]});
            var Q71;
            Q71=makeQuery(id+"F0.imprint","IMPRINT",FACE,{"disambiguationData":[TD([[makeQuery(id+"F0.imprint","IMPRINT",EDGE,{"derivedFrom":sQuery(id+"F0.wireOp",EDGE,"E11.5.6.0")}),1.0]])]});
            var Q72;
            Q72=makeQuery(id+"F0.imprint","IMPRINT",FACE,{"disambiguationData":[TD([[makeQuery(id+"F0.imprint","IMPRINT",EDGE,{"derivedFrom":sQuery(id+"F0.wireOp",EDGE,"E11.6.6.0")}),1.0]])]});
            var Q73;
            Q73=makeQuery(id+"F0.imprint","IMPRINT",FACE,{"disambiguationData":[TD([[makeQuery(id+"F0.imprint","IMPRINT",EDGE,{"derivedFrom":sQuery(id+"F0.wireOp",EDGE,"E11.7.6.0")}),1.0]])]});
            var Q74;
            Q74=makeQuery(id+"F0.imprint","IMPRINT",FACE,{"disambiguationData":[TD([[makeQuery(id+"F0.imprint","IMPRINT",EDGE,{"derivedFrom":sQuery(id+"F0.wireOp",EDGE,"E11.7.7.0")}),1.0]])]});
            var Q75;
            Q75=makeQuery(id+"F0.imprint","IMPRINT",FACE,{"disambiguationData":[TD([[makeQuery(id+"F0.imprint","IMPRINT",EDGE,{"derivedFrom":sQuery(id+"F0.wireOp",EDGE,"E11.6.7.0")}),1.0]])]});
            var Q76;
            Q76=makeQuery(id+"F0.imprint","IMPRINT",FACE,{"disambiguationData":[TD([[makeQuery(id+"F0.imprint","IMPRINT",EDGE,{"derivedFrom":sQuery(id+"F0.wireOp",EDGE,"E11.4.6.0")}),1.0]])]});
            var Q77;
            Q77=makeQuery(id+"F0.imprint","IMPRINT",FACE,{"disambiguationData":[TD([[makeQuery(id+"F0.imprint","IMPRINT",EDGE,{"derivedFrom":sQuery(id+"F0.wireOp",EDGE,"E11.3.6.0")}),1.0]])]});
            var Q78;
            Q78=makeQuery(id+"F0.imprint","IMPRINT",FACE,{"disambiguationData":[TD([[makeQuery(id+"F0.imprint","IMPRINT",EDGE,{"derivedFrom":sQuery(id+"F0.wireOp",EDGE,"E11.2.6.0")}),1.0]])]});
            var Q79;
            Q79=makeQuery(id+"F0.imprint","IMPRINT",FACE,{"disambiguationData":[TD([[makeQuery(id+"F0.imprint","IMPRINT",EDGE,{"derivedFrom":sQuery(id+"F0.wireOp",EDGE,"E11.1.6.0")}),1.0]])]});
            var Q80;
            Q80=makeQuery(id+"F0.imprint","IMPRINT",FACE,{"disambiguationData":[TD([[makeQuery(id+"F0.imprint","IMPRINT",EDGE,{"derivedFrom":sQuery(id+"F0.wireOp",EDGE,"E11.1.5.0")}),1.0]])]});
            var Q81;
            Q81=makeQuery(id+"F0.imprint","IMPRINT",FACE,{"disambiguationData":[TD([[makeQuery(id+"F0.imprint","IMPRINT",EDGE,{"derivedFrom":sQuery(id+"F0.wireOp",EDGE,"E11.2.5.0")}),1.0]])]});
            var Q82;
            Q82=makeQuery(id+"F0.imprint","IMPRINT",FACE,{"disambiguationData":[TD([[makeQuery(id+"F0.imprint","IMPRINT",EDGE,{"derivedFrom":sQuery(id+"F0.wireOp",EDGE,"E11.3.5.0")}),1.0]])]});
            var Q83;
            Q83=makeQuery(id+"F0.imprint","IMPRINT",FACE,{"disambiguationData":[TD([[makeQuery(id+"F0.imprint","IMPRINT",EDGE,{"derivedFrom":sQuery(id+"F0.wireOp",EDGE,"E11.4.5.0")}),1.0]])]});
            var Q84;
            Q84=makeQuery(id+"F0.imprint","IMPRINT",FACE,{"disambiguationData":[TD([[makeQuery(id+"F0.imprint","IMPRINT",EDGE,{"derivedFrom":sQuery(id+"F0.wireOp",EDGE,"E11.4.4.0")}),1.0]])]});
            var Q85;
            Q85=makeQuery(id+"F0.imprint","IMPRINT",FACE,{"disambiguationData":[TD([[makeQuery(id+"F0.imprint","IMPRINT",EDGE,{"derivedFrom":sQuery(id+"F0.wireOp",EDGE,"E11.3.4.0")}),1.0]])]});
            var Q86;
            Q86=makeQuery(id+"F0.imprint","IMPRINT",FACE,{"disambiguationData":[TD([[makeQuery(id+"F0.imprint","IMPRINT",EDGE,{"derivedFrom":sQuery(id+"F0.wireOp",EDGE,"E11.2.4.0")}),1.0]])]});
            var Q87;
            Q87=makeQuery(id+"F0.imprint","IMPRINT",FACE,{"disambiguationData":[TD([[makeQuery(id+"F0.imprint","IMPRINT",EDGE,{"derivedFrom":sQuery(id+"F0.wireOp",EDGE,"E11.1.4.0")}),1.0]])]});
            var Q88;
            Q88=makeQuery(id+"F0.imprint","IMPRINT",FACE,{"disambiguationData":[TD([[makeQuery(id+"F0.imprint","IMPRINT",EDGE,{"derivedFrom":sQuery(id+"F0.wireOp",EDGE,"E11.0.2.0")}),1.0]])]});
            var Q89;
            Q89=makeQuery(id+"F0.imprint","IMPRINT",FACE,{"disambiguationData":[TD([[makeQuery(id+"F0.imprint","IMPRINT",EDGE,{"derivedFrom":sQuery(id+"F0.wireOp",EDGE,"E11.1.2.0")}),1.0]])]});
            var Q90;
            Q90=makeQuery(id+"F0.imprint","IMPRINT",FACE,{"disambiguationData":[TD([[makeQuery(id+"F0.imprint","IMPRINT",EDGE,{"derivedFrom":sQuery(id+"F0.wireOp",EDGE,"E11.2.2.0")}),1.0]])]});
            var Q91;
            Q91=makeQuery(id+"F0.imprint","IMPRINT",FACE,{"disambiguationData":[TD([[makeQuery(id+"F0.imprint","IMPRINT",EDGE,{"derivedFrom":sQuery(id+"F0.wireOp",EDGE,"E11.3.2.0")}),1.0]])]});
            var Q92;
            Q92=makeQuery(id+"F0.imprint","IMPRINT",FACE,{"disambiguationData":[TD([[makeQuery(id+"F0.imprint","IMPRINT",EDGE,{"derivedFrom":sQuery(id+"F0.wireOp",EDGE,"E11.4.2.0")}),1.0]])]});
            var Q93;
            Q93=makeQuery(id+"F0.imprint","IMPRINT",FACE,{"disambiguationData":[TD([[makeQuery(id+"F0.imprint","IMPRINT",EDGE,{"derivedFrom":sQuery(id+"F0.wireOp",EDGE,"E11.5.2.0")}),1.0]])]});
            var Q94;
            Q94=makeQuery(id+"F0.imprint","IMPRINT",FACE,{"disambiguationData":[TD([[makeQuery(id+"F0.imprint","IMPRINT",EDGE,{"derivedFrom":sQuery(id+"F0.wireOp",EDGE,"E11.6.2.0")}),1.0]])]});
            var Q95;
            Q95=makeQuery(id+"F0.imprint","IMPRINT",FACE,{"disambiguationData":[TD([[makeQuery(id+"F0.imprint","IMPRINT",EDGE,{"derivedFrom":sQuery(id+"F0.wireOp",EDGE,"E11.7.2.0")}),1.0]])]});
            var Q96;
            Q96=makeQuery(id+"F0.imprint","IMPRINT",FACE,{"disambiguationData":[TD([[makeQuery(id+"F0.imprint","IMPRINT",EDGE,{"derivedFrom":sQuery(id+"F0.wireOp",EDGE,"E11.7.1.0")}),1.0]])]});
            var Q97;
            Q97=makeQuery(id+"F0.imprint","IMPRINT",FACE,{"disambiguationData":[TD([[makeQuery(id+"F0.imprint","IMPRINT",EDGE,{"derivedFrom":sQuery(id+"F0.wireOp",EDGE,"E11.6.1.0")}),1.0]])]});
            var Q98;
            Q98=makeQuery(id+"F0.imprint","IMPRINT",FACE,{"disambiguationData":[TD([[makeQuery(id+"F0.imprint","IMPRINT",EDGE,{"derivedFrom":sQuery(id+"F0.wireOp",EDGE,"E11.5.1.0")}),1.0]])]});
            var Q99;
            Q99=makeQuery(id+"F0.imprint","IMPRINT",FACE,{"disambiguationData":[TD([[makeQuery(id+"F0.imprint","IMPRINT",EDGE,{"derivedFrom":sQuery(id+"F0.wireOp",EDGE,"E11.4.1.0")}),1.0]])]});
            var Q100;
            Q100=makeQuery(id+"F0.imprint","IMPRINT",FACE,{"disambiguationData":[TD([[makeQuery(id+"F0.imprint","IMPRINT",EDGE,{"derivedFrom":sQuery(id+"F0.wireOp",EDGE,"E11.3.1.0")}),1.0]])]});
            var Q101;
            Q101=makeQuery(id+"F0.imprint","IMPRINT",FACE,{"disambiguationData":[TD([[makeQuery(id+"F0.imprint","IMPRINT",EDGE,{"derivedFrom":sQuery(id+"F0.wireOp",EDGE,"E11.2.1.0")}),1.0]])]});
            var Q102;
            Q102=makeQuery(id+"F0.imprint","IMPRINT",FACE,{"disambiguationData":[TD([[makeQuery(id+"F0.imprint","IMPRINT",EDGE,{"derivedFrom":sQuery(id+"F0.wireOp",EDGE,"E11.1.1.0")}),1.0]])]});
            var Q103;
            Q103=makeQuery(id+"F0.imprint","IMPRINT",FACE,{"disambiguationData":[TD([[makeQuery(id+"F0.imprint","IMPRINT",EDGE,{"derivedFrom":sQuery(id+"F0.wireOp",EDGE,"E11.0.1.0")}),1.0]])]});
            var Q104;
            Q104=makeQuery(id+"F0.imprint","IMPRINT",FACE,{"disambiguationData":[TD([[makeQuery(id+"F0.imprint","IMPRINT",EDGE,{"derivedFrom":sQuery(id+"F0.wireOp",EDGE,"E10.bottom")}),-1.0]])]});
            var Q105;
            Q105=makeQuery(id+"F0.imprint","IMPRINT",FACE,{"disambiguationData":[TD([[makeQuery(id+"F0.imprint","IMPRINT",EDGE,{"derivedFrom":sQuery(id+"F0.wireOp",EDGE,"E11.1.0.0")}),1.0]])]});
            var Q106;
            Q106=makeQuery(id+"F0.imprint","IMPRINT",FACE,{"disambiguationData":[TD([[makeQuery(id+"F0.imprint","IMPRINT",EDGE,{"derivedFrom":sQuery(id+"F0.wireOp",EDGE,"E11.2.0.0")}),1.0]])]});
            var Q107;
            Q107=makeQuery(id+"F0.imprint","IMPRINT",FACE,{"disambiguationData":[TD([[makeQuery(id+"F0.imprint","IMPRINT",EDGE,{"derivedFrom":sQuery(id+"F0.wireOp",EDGE,"E11.3.0.0")}),1.0]])]});
            var Q108;
            Q108=makeQuery(id+"F0.imprint","IMPRINT",FACE,{"disambiguationData":[TD([[makeQuery(id+"F0.imprint","IMPRINT",EDGE,{"derivedFrom":sQuery(id+"F0.wireOp",EDGE,"E11.4.0.0")}),1.0]])]});
            var Q109;
            Q109=makeQuery(id+"F0.imprint","IMPRINT",FACE,{"disambiguationData":[TD([[makeQuery(id+"F0.imprint","IMPRINT",EDGE,{"derivedFrom":sQuery(id+"F0.wireOp",EDGE,"E11.5.0.0")}),1.0]])]});
            var Q110;
            Q110=makeQuery(id+"F0.imprint","IMPRINT",FACE,{"disambiguationData":[TD([[makeQuery(id+"F0.imprint","IMPRINT",EDGE,{"derivedFrom":sQuery(id+"F0.wireOp",EDGE,"E11.6.0.0")}),1.0]])]});
            var Q111;
            Q111=makeQuery(id+"F0.imprint","IMPRINT",FACE,{"disambiguationData":[TD([[makeQuery(id+"F0.imprint","IMPRINT",EDGE,{"derivedFrom":sQuery(id+"F0.wireOp",EDGE,"E11.7.0.0")}),1.0]])]});
            var Q112;
            Q112=makeQuery(id+"F0.imprint","IMPRINT",FACE,{"disambiguationData":[TD([[makeQuery(id+"F0.imprint","IMPRINT",EDGE,{"derivedFrom":sQuery(id+"F0.wireOp",EDGE,"E11.8.0.0")}),1.0]])]});
            var Q113;
            Q113=makeQuery(id+"F0.imprint","IMPRINT",FACE,{"disambiguationData":[TD([[makeQuery(id+"F0.imprint","IMPRINT",EDGE,{"derivedFrom":sQuery(id+"F0.wireOp",EDGE,"E11.9.0.0")}),1.0]])]});
            var Q114;
            Q114=makeQuery(id+"F0.imprint","IMPRINT",FACE,{"disambiguationData":[TD([[makeQuery(id+"F0.imprint","IMPRINT",EDGE,{"derivedFrom":sQuery(id+"F0.wireOp",EDGE,"E11.9.1.0")}),1.0]])]});
            var Q115;
            Q115=makeQuery(id+"F0.imprint","IMPRINT",FACE,{"disambiguationData":[TD([[makeQuery(id+"F0.imprint","IMPRINT",EDGE,{"derivedFrom":sQuery(id+"F0.wireOp",EDGE,"E11.9.2.0")}),1.0]])]});
            var Q116;
            Q116=makeQuery(id+"F0.imprint","IMPRINT",FACE,{"disambiguationData":[TD([[makeQuery(id+"F0.imprint","IMPRINT",EDGE,{"derivedFrom":sQuery(id+"F0.wireOp",EDGE,"E11.9.3.0")}),1.0]])]});
            var Q117;
            Q117=makeQuery(id+"F0.imprint","IMPRINT",FACE,{"disambiguationData":[TD([[makeQuery(id+"F0.imprint","IMPRINT",EDGE,{"derivedFrom":sQuery(id+"F0.wireOp",EDGE,"E11.8.3.0")}),1.0]])]});
            var Q118;
            Q118=makeQuery(id+"F0.imprint","IMPRINT",FACE,{"disambiguationData":[TD([[makeQuery(id+"F0.imprint","IMPRINT",EDGE,{"derivedFrom":sQuery(id+"F0.wireOp",EDGE,"E11.8.2.0")}),1.0]])]});
            var Q119;
            Q119=makeQuery(id+"F0.imprint","IMPRINT",FACE,{"disambiguationData":[TD([[makeQuery(id+"F0.imprint","IMPRINT",EDGE,{"derivedFrom":sQuery(id+"F0.wireOp",EDGE,"E11.8.1.0")}),1.0]])]});
            var Q120;
            Q120=makeQuery(id+"F0.imprint","IMPRINT",FACE,{"disambiguationData":[TD([[makeQuery(id+"F0.imprint","IMPRINT",EDGE,{"derivedFrom":sQuery(id+"F0.wireOp",EDGE,"E11.8.4.0")}),1.0]])]});
            var Q121;
            Q121=makeQuery(id+"F0.imprint","IMPRINT",FACE,{"disambiguationData":[TD([[makeQuery(id+"F0.imprint","IMPRINT",EDGE,{"derivedFrom":sQuery(id+"F0.wireOp",EDGE,"E11.9.4.0")}),1.0]])]});
            var Q122;
            Q122=makeQuery(id+"F0.imprint","IMPRINT",FACE,{"disambiguationData":[TD([[makeQuery(id+"F0.imprint","IMPRINT",EDGE,{"derivedFrom":sQuery(id+"F0.wireOp",EDGE,"E11.10.4.0")}),1.0]])]});
            var Q123;
            Q123=makeQuery(id+"F0.imprint","IMPRINT",FACE,{"disambiguationData":[TD([[makeQuery(id+"F0.imprint","IMPRINT",EDGE,{"derivedFrom":sQuery(id+"F0.wireOp",EDGE,"E11.10.3.0")}),1.0]])]});
            var Q124;
            Q124=makeQuery(id+"F0.imprint","IMPRINT",FACE,{"disambiguationData":[TD([[makeQuery(id+"F0.imprint","IMPRINT",EDGE,{"derivedFrom":sQuery(id+"F0.wireOp",EDGE,"E11.10.2.0")}),1.0]])]});
            var Q125;
            Q125=makeQuery(id+"F0.imprint","IMPRINT",FACE,{"disambiguationData":[TD([[makeQuery(id+"F0.imprint","IMPRINT",EDGE,{"derivedFrom":sQuery(id+"F0.wireOp",EDGE,"E11.10.1.0")}),1.0]])]});
            var Q126;
            Q126=makeQuery(id+"F0.imprint","IMPRINT",FACE,{"disambiguationData":[TD([[makeQuery(id+"F0.imprint","IMPRINT",EDGE,{"derivedFrom":sQuery(id+"F0.wireOp",EDGE,"E11.10.0.0")}),1.0]])]});
            var Q127;
            Q127=makeQuery(id+"F0.imprint","IMPRINT",FACE,{"disambiguationData":[TD([[makeQuery(id+"F0.imprint","IMPRINT",EDGE,{"derivedFrom":sQuery(id+"F0.wireOp",EDGE,"E11.11.0.0")}),1.0]])]});
            var Q128;
            Q128=makeQuery(id+"F0.imprint","IMPRINT",FACE,{"disambiguationData":[TD([[makeQuery(id+"F0.imprint","IMPRINT",EDGE,{"derivedFrom":sQuery(id+"F0.wireOp",EDGE,"E11.12.0.0")}),1.0]])]});
            var Q129;
            Q129=makeQuery(id+"F0.imprint","IMPRINT",FACE,{"disambiguationData":[TD([[makeQuery(id+"F0.imprint","IMPRINT",EDGE,{"derivedFrom":sQuery(id+"F0.wireOp",EDGE,"E11.13.0.0")}),1.0]])]});
            var Q130;
            Q130=makeQuery(id+"F0.imprint","IMPRINT",FACE,{"disambiguationData":[TD([[makeQuery(id+"F0.imprint","IMPRINT",EDGE,{"derivedFrom":sQuery(id+"F0.wireOp",EDGE,"E11.14.0.0")}),1.0]])]});
            var Q131;
            Q131=makeQuery(id+"F0.imprint","IMPRINT",FACE,{"disambiguationData":[TD([[makeQuery(id+"F0.imprint","IMPRINT",EDGE,{"derivedFrom":sQuery(id+"F0.wireOp",EDGE,"E11.15.0.0")}),1.0]])]});
            var Q132;
            Q132=makeQuery(id+"F0.imprint","IMPRINT",FACE,{"disambiguationData":[TD([[makeQuery(id+"F0.imprint","IMPRINT",EDGE,{"derivedFrom":sQuery(id+"F0.wireOp",EDGE,"E11.15.1.0")}),1.0]])]});
            var Q133;
            Q133=makeQuery(id+"F0.imprint","IMPRINT",FACE,{"disambiguationData":[TD([[makeQuery(id+"F0.imprint","IMPRINT",EDGE,{"derivedFrom":sQuery(id+"F0.wireOp",EDGE,"E11.14.1.0")}),1.0]])]});
            var Q134;
            Q134=makeQuery(id+"F0.imprint","IMPRINT",FACE,{"disambiguationData":[TD([[makeQuery(id+"F0.imprint","IMPRINT",EDGE,{"derivedFrom":sQuery(id+"F0.wireOp",EDGE,"E11.13.1.0")}),1.0]])]});
            var Q135;
            Q135=makeQuery(id+"F0.imprint","IMPRINT",FACE,{"disambiguationData":[TD([[makeQuery(id+"F0.imprint","IMPRINT",EDGE,{"derivedFrom":sQuery(id+"F0.wireOp",EDGE,"E11.12.1.0")}),1.0]])]});
            var Q136;
            Q136=makeQuery(id+"F0.imprint","IMPRINT",FACE,{"disambiguationData":[TD([[makeQuery(id+"F0.imprint","IMPRINT",EDGE,{"derivedFrom":sQuery(id+"F0.wireOp",EDGE,"E11.11.1.0")}),1.0]])]});
            var Q137;
            Q137=makeQuery(id+"F0.imprint","IMPRINT",FACE,{"disambiguationData":[TD([[makeQuery(id+"F0.imprint","IMPRINT",EDGE,{"derivedFrom":sQuery(id+"F0.wireOp",EDGE,"E11.11.2.0")}),1.0]])]});
            var Q138;
            Q138=makeQuery(id+"F0.imprint","IMPRINT",FACE,{"disambiguationData":[TD([[makeQuery(id+"F0.imprint","IMPRINT",EDGE,{"derivedFrom":sQuery(id+"F0.wireOp",EDGE,"E11.12.2.0")}),1.0]])]});
            var Q139;
            Q139=makeQuery(id+"F0.imprint","IMPRINT",FACE,{"disambiguationData":[TD([[makeQuery(id+"F0.imprint","IMPRINT",EDGE,{"derivedFrom":sQuery(id+"F0.wireOp",EDGE,"E11.13.2.0")}),1.0]])]});
            var Q140;
            Q140=makeQuery(id+"F0.imprint","IMPRINT",FACE,{"disambiguationData":[TD([[makeQuery(id+"F0.imprint","IMPRINT",EDGE,{"derivedFrom":sQuery(id+"F0.wireOp",EDGE,"E11.14.2.0")}),1.0]])]});
            var Q141;
            Q141=makeQuery(id+"F0.imprint","IMPRINT",FACE,{"disambiguationData":[TD([[makeQuery(id+"F0.imprint","IMPRINT",EDGE,{"derivedFrom":sQuery(id+"F0.wireOp",EDGE,"E11.15.2.0")}),1.0]])]});
            var Q142;
            Q142=makeQuery(id+"F0.imprint","IMPRINT",FACE,{"disambiguationData":[TD([[makeQuery(id+"F0.imprint","IMPRINT",EDGE,{"derivedFrom":sQuery(id+"F0.wireOp",EDGE,"E11.15.3.0")}),1.0]])]});
            var Q143;
            Q143=makeQuery(id+"F0.imprint","IMPRINT",FACE,{"disambiguationData":[TD([[makeQuery(id+"F0.imprint","IMPRINT",EDGE,{"derivedFrom":sQuery(id+"F0.wireOp",EDGE,"E11.14.3.0")}),1.0]])]});
            var Q144;
            Q144=makeQuery(id+"F0.imprint","IMPRINT",FACE,{"disambiguationData":[TD([[makeQuery(id+"F0.imprint","IMPRINT",EDGE,{"derivedFrom":sQuery(id+"F0.wireOp",EDGE,"E11.13.3.0")}),1.0]])]});
            var Q145;
            Q145=makeQuery(id+"F0.imprint","IMPRINT",FACE,{"disambiguationData":[TD([[makeQuery(id+"F0.imprint","IMPRINT",EDGE,{"derivedFrom":sQuery(id+"F0.wireOp",EDGE,"E11.12.3.0")}),1.0]])]});
            var Q146;
            Q146=makeQuery(id+"F0.imprint","IMPRINT",FACE,{"disambiguationData":[TD([[makeQuery(id+"F0.imprint","IMPRINT",EDGE,{"derivedFrom":sQuery(id+"F0.wireOp",EDGE,"E11.11.3.0")}),1.0]])]});
            var Q147;
            Q147=makeQuery(id+"F0.imprint","IMPRINT",FACE,{"disambiguationData":[TD([[makeQuery(id+"F0.imprint","IMPRINT",EDGE,{"derivedFrom":sQuery(id+"F0.wireOp",EDGE,"E11.11.4.0")}),1.0]])]});
            var Q148;
            Q148=makeQuery(id+"F0.imprint","IMPRINT",FACE,{"disambiguationData":[TD([[makeQuery(id+"F0.imprint","IMPRINT",EDGE,{"derivedFrom":sQuery(id+"F0.wireOp",EDGE,"E11.12.4.0")}),1.0]])]});
            var Q149;
            Q149=makeQuery(id+"F0.imprint","IMPRINT",FACE,{"disambiguationData":[TD([[makeQuery(id+"F0.imprint","IMPRINT",EDGE,{"derivedFrom":sQuery(id+"F0.wireOp",EDGE,"E11.13.4.0")}),1.0]])]});
            var Q150;
            Q150=makeQuery(id+"F0.imprint","IMPRINT",FACE,{"disambiguationData":[TD([[makeQuery(id+"F0.imprint","IMPRINT",EDGE,{"derivedFrom":sQuery(id+"F0.wireOp",EDGE,"E11.14.4.0")}),1.0]])]});
            var Q151;
            Q151=makeQuery(id+"F0.imprint","IMPRINT",FACE,{"disambiguationData":[TD([[makeQuery(id+"F0.imprint","IMPRINT",EDGE,{"derivedFrom":sQuery(id+"F0.wireOp",EDGE,"E11.15.4.0")}),1.0]])]});
            var Q152;
            Q152=makeQuery(id+"F0.imprint","IMPRINT",FACE,{"disambiguationData":[TD([[makeQuery(id+"F0.imprint","IMPRINT",EDGE,{"derivedFrom":sQuery(id+"F0.wireOp",EDGE,"E11.8.5.0")}),1.0]])]});
            var Q153;
            Q153=makeQuery(id+"F0.imprint","IMPRINT",FACE,{"disambiguationData":[TD([[makeQuery(id+"F0.imprint","IMPRINT",EDGE,{"derivedFrom":sQuery(id+"F0.wireOp",EDGE,"E11.8.6.0")}),1.0]])]});
            var Q154;
            Q154=makeQuery(id+"F0.imprint","IMPRINT",FACE,{"disambiguationData":[TD([[makeQuery(id+"F0.imprint","IMPRINT",EDGE,{"derivedFrom":sQuery(id+"F0.wireOp",EDGE,"E11.8.7.0")}),1.0]])]});
            var Q155;
            Q155=makeQuery(id+"F0.imprint","IMPRINT",FACE,{"disambiguationData":[TD([[makeQuery(id+"F0.imprint","IMPRINT",EDGE,{"derivedFrom":sQuery(id+"F0.wireOp",EDGE,"E11.8.8.0")}),1.0]])]});
            var Q156;
            Q156=makeQuery(id+"F0.imprint","IMPRINT",FACE,{"disambiguationData":[TD([[makeQuery(id+"F0.imprint","IMPRINT",EDGE,{"derivedFrom":sQuery(id+"F0.wireOp",EDGE,"E11.9.8.0")}),1.0]])]});
            var Q157;
            Q157=makeQuery(id+"F0.imprint","IMPRINT",FACE,{"disambiguationData":[TD([[makeQuery(id+"F0.imprint","IMPRINT",EDGE,{"derivedFrom":sQuery(id+"F0.wireOp",EDGE,"E11.10.8.0")}),1.0]])]});
            var Q158;
            Q158=makeQuery(id+"F0.imprint","IMPRINT",FACE,{"disambiguationData":[TD([[makeQuery(id+"F0.imprint","IMPRINT",EDGE,{"derivedFrom":sQuery(id+"F0.wireOp",EDGE,"E11.11.8.0")}),1.0]])]});
            var Q159;
            Q159=makeQuery(id+"F0.imprint","IMPRINT",FACE,{"disambiguationData":[TD([[makeQuery(id+"F0.imprint","IMPRINT",EDGE,{"derivedFrom":sQuery(id+"F0.wireOp",EDGE,"E11.12.8.0")}),1.0]])]});
            var Q160;
            Q160=makeQuery(id+"F0.imprint","IMPRINT",FACE,{"disambiguationData":[TD([[makeQuery(id+"F0.imprint","IMPRINT",EDGE,{"derivedFrom":sQuery(id+"F0.wireOp",EDGE,"E11.13.8.0")}),1.0]])]});
            var Q161;
            Q161=makeQuery(id+"F0.imprint","IMPRINT",FACE,{"disambiguationData":[TD([[makeQuery(id+"F0.imprint","IMPRINT",EDGE,{"derivedFrom":sQuery(id+"F0.wireOp",EDGE,"E11.14.8.0")}),1.0]])]});
            var Q162;
            Q162=makeQuery(id+"F0.imprint","IMPRINT",FACE,{"disambiguationData":[TD([[makeQuery(id+"F0.imprint","IMPRINT",EDGE,{"derivedFrom":sQuery(id+"F0.wireOp",EDGE,"E11.15.8.0")}),1.0]])]});
            var Q163;
            Q163=makeQuery(id+"F0.imprint","IMPRINT",FACE,{"disambiguationData":[TD([[makeQuery(id+"F0.imprint","IMPRINT",EDGE,{"derivedFrom":sQuery(id+"F0.wireOp",EDGE,"E11.15.7.0")}),1.0]])]});
            var Q164;
            Q164=makeQuery(id+"F0.imprint","IMPRINT",FACE,{"disambiguationData":[TD([[makeQuery(id+"F0.imprint","IMPRINT",EDGE,{"derivedFrom":sQuery(id+"F0.wireOp",EDGE,"E11.14.7.0")}),1.0]])]});
            var Q165;
            Q165=makeQuery(id+"F0.imprint","IMPRINT",FACE,{"disambiguationData":[TD([[makeQuery(id+"F0.imprint","IMPRINT",EDGE,{"derivedFrom":sQuery(id+"F0.wireOp",EDGE,"E11.13.7.0")}),1.0]])]});
            var Q166;
            Q166=makeQuery(id+"F0.imprint","IMPRINT",FACE,{"disambiguationData":[TD([[makeQuery(id+"F0.imprint","IMPRINT",EDGE,{"derivedFrom":sQuery(id+"F0.wireOp",EDGE,"E11.12.7.0")}),1.0]])]});
            var Q167;
            Q167=makeQuery(id+"F0.imprint","IMPRINT",FACE,{"disambiguationData":[TD([[makeQuery(id+"F0.imprint","IMPRINT",EDGE,{"derivedFrom":sQuery(id+"F0.wireOp",EDGE,"E11.11.7.0")}),1.0]])]});
            var Q168;
            Q168=makeQuery(id+"F0.imprint","IMPRINT",FACE,{"disambiguationData":[TD([[makeQuery(id+"F0.imprint","IMPRINT",EDGE,{"derivedFrom":sQuery(id+"F0.wireOp",EDGE,"E11.10.7.0")}),1.0]])]});
            var Q169;
            Q169=makeQuery(id+"F0.imprint","IMPRINT",FACE,{"disambiguationData":[TD([[makeQuery(id+"F0.imprint","IMPRINT",EDGE,{"derivedFrom":sQuery(id+"F0.wireOp",EDGE,"E11.9.7.0")}),1.0]])]});
            var Q170;
            Q170=makeQuery(id+"F0.imprint","IMPRINT",FACE,{"disambiguationData":[TD([[makeQuery(id+"F0.imprint","IMPRINT",EDGE,{"derivedFrom":sQuery(id+"F0.wireOp",EDGE,"E11.9.6.0")}),1.0]])]});
            var Q171;
            Q171=makeQuery(id+"F0.imprint","IMPRINT",FACE,{"disambiguationData":[TD([[makeQuery(id+"F0.imprint","IMPRINT",EDGE,{"derivedFrom":sQuery(id+"F0.wireOp",EDGE,"E11.10.6.0")}),1.0]])]});
            var Q172;
            Q172=makeQuery(id+"F0.imprint","IMPRINT",FACE,{"disambiguationData":[TD([[makeQuery(id+"F0.imprint","IMPRINT",EDGE,{"derivedFrom":sQuery(id+"F0.wireOp",EDGE,"E11.11.6.0")}),1.0]])]});
            var Q173;
            Q173=makeQuery(id+"F0.imprint","IMPRINT",FACE,{"disambiguationData":[TD([[makeQuery(id+"F0.imprint","IMPRINT",EDGE,{"derivedFrom":sQuery(id+"F0.wireOp",EDGE,"E11.12.6.0")}),1.0]])]});
            var Q174;
            Q174=makeQuery(id+"F0.imprint","IMPRINT",FACE,{"disambiguationData":[TD([[makeQuery(id+"F0.imprint","IMPRINT",EDGE,{"derivedFrom":sQuery(id+"F0.wireOp",EDGE,"E11.13.6.0")}),1.0]])]});
            var Q175;
            Q175=makeQuery(id+"F0.imprint","IMPRINT",FACE,{"disambiguationData":[TD([[makeQuery(id+"F0.imprint","IMPRINT",EDGE,{"derivedFrom":sQuery(id+"F0.wireOp",EDGE,"E11.14.6.0")}),1.0]])]});
            var Q176;
            Q176=makeQuery(id+"F0.imprint","IMPRINT",FACE,{"disambiguationData":[TD([[makeQuery(id+"F0.imprint","IMPRINT",EDGE,{"derivedFrom":sQuery(id+"F0.wireOp",EDGE,"E11.15.6.0")}),1.0]])]});
            var Q177;
            Q177=makeQuery(id+"F0.imprint","IMPRINT",FACE,{"disambiguationData":[TD([[makeQuery(id+"F0.imprint","IMPRINT",EDGE,{"derivedFrom":sQuery(id+"F0.wireOp",EDGE,"E11.15.5.0")}),1.0]])]});
            var Q178;
            Q178=makeQuery(id+"F0.imprint","IMPRINT",FACE,{"disambiguationData":[TD([[makeQuery(id+"F0.imprint","IMPRINT",EDGE,{"derivedFrom":sQuery(id+"F0.wireOp",EDGE,"E11.14.5.0")}),1.0]])]});
            var Q179;
            Q179=makeQuery(id+"F0.imprint","IMPRINT",FACE,{"disambiguationData":[TD([[makeQuery(id+"F0.imprint","IMPRINT",EDGE,{"derivedFrom":sQuery(id+"F0.wireOp",EDGE,"E11.13.5.0")}),1.0]])]});
            var Q180;
            Q180=makeQuery(id+"F0.imprint","IMPRINT",FACE,{"disambiguationData":[TD([[makeQuery(id+"F0.imprint","IMPRINT",EDGE,{"derivedFrom":sQuery(id+"F0.wireOp",EDGE,"E11.12.5.0")}),1.0]])]});
            var Q181;
            Q181=makeQuery(id+"F0.imprint","IMPRINT",FACE,{"disambiguationData":[TD([[makeQuery(id+"F0.imprint","IMPRINT",EDGE,{"derivedFrom":sQuery(id+"F0.wireOp",EDGE,"E11.11.5.0")}),1.0]])]});
            var Q182;
            Q182=makeQuery(id+"F0.imprint","IMPRINT",FACE,{"disambiguationData":[TD([[makeQuery(id+"F0.imprint","IMPRINT",EDGE,{"derivedFrom":sQuery(id+"F0.wireOp",EDGE,"E11.10.5.0")}),1.0]])]});
            var Q183;
            Q183=makeQuery(id+"F0.imprint","IMPRINT",FACE,{"disambiguationData":[TD([[makeQuery(id+"F0.imprint","IMPRINT",EDGE,{"derivedFrom":sQuery(id+"F0.wireOp",EDGE,"E11.9.5.0")}),1.0]])]});
            var Q184;
            Q184=makeQuery(id+"F0.imprint","IMPRINT",FACE,{"disambiguationData":[TD([[makeQuery(id+"F0.imprint","IMPRINT",EDGE,{"derivedFrom":sQuery(id+"F0.wireOp",EDGE,"E11.6.8.0")}),1.0]])]});
            var Q185;
            Q185=makeQuery(id+"F0.imprint","IMPRINT",FACE,{"disambiguationData":[TD([[makeQuery(id+"F0.imprint","IMPRINT",EDGE,{"derivedFrom":sQuery(id+"F0.wireOp",EDGE,"E11.7.8.0")}),1.0]])]});
            var Q186;
            Q186=makeQuery(id+"F0.imprint","IMPRINT",FACE,{"disambiguationData":[TD([[makeQuery(id+"F0.imprint","IMPRINT",EDGE,{"derivedFrom":sQuery(id+"F0.wireOp",EDGE,"E11.6.9.0")}),1.0]])]});
            var Q187;
            Q187=makeQuery(id+"F0.imprint","IMPRINT",FACE,{"disambiguationData":[TD([[makeQuery(id+"F0.imprint","IMPRINT",EDGE,{"derivedFrom":sQuery(id+"F0.wireOp",EDGE,"E11.7.9.0")}),1.0]])]});
            var Q188;
            Q188=makeQuery(id+"F0.imprint","IMPRINT",FACE,{"disambiguationData":[TD([[makeQuery(id+"F0.imprint","IMPRINT",EDGE,{"derivedFrom":sQuery(id+"F0.wireOp",EDGE,"E11.8.9.0")}),1.0]])]});
            var Q189;
            Q189=makeQuery(id+"F0.imprint","IMPRINT",FACE,{"disambiguationData":[TD([[makeQuery(id+"F0.imprint","IMPRINT",EDGE,{"derivedFrom":sQuery(id+"F0.wireOp",EDGE,"E11.9.9.0")}),1.0]])]});
            var Q190;
            Q190=makeQuery(id+"F0.imprint","IMPRINT",FACE,{"disambiguationData":[TD([[makeQuery(id+"F0.imprint","IMPRINT",EDGE,{"derivedFrom":sQuery(id+"F0.wireOp",EDGE,"E11.10.9.0")}),1.0]])]});
            var Q191;
            Q191=makeQuery(id+"F0.imprint","IMPRINT",FACE,{"disambiguationData":[TD([[makeQuery(id+"F0.imprint","IMPRINT",EDGE,{"derivedFrom":sQuery(id+"F0.wireOp",EDGE,"E11.11.9.0")}),1.0]])]});
            var Q192;
            Q192=makeQuery(id+"F0.imprint","IMPRINT",FACE,{"disambiguationData":[TD([[makeQuery(id+"F0.imprint","IMPRINT",EDGE,{"derivedFrom":sQuery(id+"F0.wireOp",EDGE,"E11.12.9.0")}),1.0]])]});
            var Q193;
            Q193=makeQuery(id+"F0.imprint","IMPRINT",FACE,{"disambiguationData":[TD([[makeQuery(id+"F0.imprint","IMPRINT",EDGE,{"derivedFrom":sQuery(id+"F0.wireOp",EDGE,"E11.6.10.0")}),1.0]])]});
            var Q194;
            Q194=makeQuery(id+"F0.imprint","IMPRINT",FACE,{"disambiguationData":[TD([[makeQuery(id+"F0.imprint","IMPRINT",EDGE,{"derivedFrom":sQuery(id+"F0.wireOp",EDGE,"E11.6.11.0")}),1.0]])]});
            var Q195;
            Q195=makeQuery(id+"F0.imprint","IMPRINT",FACE,{"disambiguationData":[TD([[makeQuery(id+"F0.imprint","IMPRINT",EDGE,{"derivedFrom":sQuery(id+"F0.wireOp",EDGE,"E11.6.12.0")}),1.0]])]});
            var Q196;
            Q196=makeQuery(id+"F0.imprint","IMPRINT",FACE,{"disambiguationData":[TD([[makeQuery(id+"F0.imprint","IMPRINT",EDGE,{"derivedFrom":sQuery(id+"F0.wireOp",EDGE,"E11.6.13.0")}),1.0]])]});
            var Q197;
            Q197=makeQuery(id+"F0.imprint","IMPRINT",FACE,{"disambiguationData":[TD([[makeQuery(id+"F0.imprint","IMPRINT",EDGE,{"derivedFrom":sQuery(id+"F0.wireOp",EDGE,"E11.6.14.0")}),1.0]])]});
            var Q198;
            Q198=makeQuery(id+"F0.imprint","IMPRINT",FACE,{"disambiguationData":[TD([[makeQuery(id+"F0.imprint","IMPRINT",EDGE,{"derivedFrom":sQuery(id+"F0.wireOp",EDGE,"E11.7.14.0")}),1.0]])]});
            var Q199;
            Q199=makeQuery(id+"F0.imprint","IMPRINT",FACE,{"disambiguationData":[TD([[makeQuery(id+"F0.imprint","IMPRINT",EDGE,{"derivedFrom":sQuery(id+"F0.wireOp",EDGE,"E11.7.13.0")}),1.0]])]});
            var Q200;
            Q200=makeQuery(id+"F0.imprint","IMPRINT",FACE,{"disambiguationData":[TD([[makeQuery(id+"F0.imprint","IMPRINT",EDGE,{"derivedFrom":sQuery(id+"F0.wireOp",EDGE,"E11.7.12.0")}),1.0]])]});
            var Q201;
            Q201=makeQuery(id+"F0.imprint","IMPRINT",FACE,{"disambiguationData":[TD([[makeQuery(id+"F0.imprint","IMPRINT",EDGE,{"derivedFrom":sQuery(id+"F0.wireOp",EDGE,"E11.7.11.0")}),1.0]])]});
            var Q202;
            Q202=makeQuery(id+"F0.imprint","IMPRINT",FACE,{"disambiguationData":[TD([[makeQuery(id+"F0.imprint","IMPRINT",EDGE,{"derivedFrom":sQuery(id+"F0.wireOp",EDGE,"E11.7.10.0")}),1.0]])]});
            var Q203;
            Q203=makeQuery(id+"F0.imprint","IMPRINT",FACE,{"disambiguationData":[TD([[makeQuery(id+"F0.imprint","IMPRINT",EDGE,{"derivedFrom":sQuery(id+"F0.wireOp",EDGE,"E11.8.10.0")}),1.0]])]});
            var Q204;
            Q204=makeQuery(id+"F0.imprint","IMPRINT",FACE,{"disambiguationData":[TD([[makeQuery(id+"F0.imprint","IMPRINT",EDGE,{"derivedFrom":sQuery(id+"F0.wireOp",EDGE,"E11.8.11.0")}),1.0]])]});
            var Q205;
            Q205=makeQuery(id+"F0.imprint","IMPRINT",FACE,{"disambiguationData":[TD([[makeQuery(id+"F0.imprint","IMPRINT",EDGE,{"derivedFrom":sQuery(id+"F0.wireOp",EDGE,"E11.8.12.0")}),1.0]])]});
            var Q206;
            Q206=makeQuery(id+"F0.imprint","IMPRINT",FACE,{"disambiguationData":[TD([[makeQuery(id+"F0.imprint","IMPRINT",EDGE,{"derivedFrom":sQuery(id+"F0.wireOp",EDGE,"E11.8.13.0")}),1.0]])]});
            var Q207;
            Q207=makeQuery(id+"F0.imprint","IMPRINT",FACE,{"disambiguationData":[TD([[makeQuery(id+"F0.imprint","IMPRINT",EDGE,{"derivedFrom":sQuery(id+"F0.wireOp",EDGE,"E11.8.14.0")}),1.0]])]});
            var Q208;
            Q208=makeQuery(id+"F0.imprint","IMPRINT",FACE,{"disambiguationData":[TD([[makeQuery(id+"F0.imprint","IMPRINT",EDGE,{"derivedFrom":sQuery(id+"F0.wireOp",EDGE,"E11.9.14.0")}),1.0]])]});
            var Q209;
            Q209=makeQuery(id+"F0.imprint","IMPRINT",FACE,{"disambiguationData":[TD([[makeQuery(id+"F0.imprint","IMPRINT",EDGE,{"derivedFrom":sQuery(id+"F0.wireOp",EDGE,"E11.9.13.0")}),1.0]])]});
            var Q210;
            Q210=makeQuery(id+"F0.imprint","IMPRINT",FACE,{"disambiguationData":[TD([[makeQuery(id+"F0.imprint","IMPRINT",EDGE,{"derivedFrom":sQuery(id+"F0.wireOp",EDGE,"E11.9.12.0")}),1.0]])]});
            var Q211;
            Q211=makeQuery(id+"F0.imprint","IMPRINT",FACE,{"disambiguationData":[TD([[makeQuery(id+"F0.imprint","IMPRINT",EDGE,{"derivedFrom":sQuery(id+"F0.wireOp",EDGE,"E11.9.11.0")}),1.0]])]});
            var Q212;
            Q212=makeQuery(id+"F0.imprint","IMPRINT",FACE,{"disambiguationData":[TD([[makeQuery(id+"F0.imprint","IMPRINT",EDGE,{"derivedFrom":sQuery(id+"F0.wireOp",EDGE,"E11.9.10.0")}),1.0]])]});
            var Q213;
            Q213=makeQuery(id+"F0.imprint","IMPRINT",FACE,{"disambiguationData":[TD([[makeQuery(id+"F0.imprint","IMPRINT",EDGE,{"derivedFrom":sQuery(id+"F0.wireOp",EDGE,"E11.10.10.0")}),1.0]])]});
            var Q214;
            Q214=makeQuery(id+"F0.imprint","IMPRINT",FACE,{"disambiguationData":[TD([[makeQuery(id+"F0.imprint","IMPRINT",EDGE,{"derivedFrom":sQuery(id+"F0.wireOp",EDGE,"E11.11.10.0")}),1.0]])]});
            var Q215;
            Q215=makeQuery(id+"F0.imprint","IMPRINT",FACE,{"disambiguationData":[TD([[makeQuery(id+"F0.imprint","IMPRINT",EDGE,{"derivedFrom":sQuery(id+"F0.wireOp",EDGE,"E11.12.10.0")}),1.0]])]});
            var Q216;
            Q216=makeQuery(id+"F0.imprint","IMPRINT",FACE,{"disambiguationData":[TD([[makeQuery(id+"F0.imprint","IMPRINT",EDGE,{"derivedFrom":sQuery(id+"F0.wireOp",EDGE,"E11.12.11.0")}),1.0]])]});
            var Q217;
            Q217=makeQuery(id+"F0.imprint","IMPRINT",FACE,{"disambiguationData":[TD([[makeQuery(id+"F0.imprint","IMPRINT",EDGE,{"derivedFrom":sQuery(id+"F0.wireOp",EDGE,"E11.11.11.0")}),1.0]])]});
            var Q218;
            Q218=makeQuery(id+"F0.imprint","IMPRINT",FACE,{"disambiguationData":[TD([[makeQuery(id+"F0.imprint","IMPRINT",EDGE,{"derivedFrom":sQuery(id+"F0.wireOp",EDGE,"E11.10.11.0")}),1.0]])]});
            var Q219;
            Q219=makeQuery(id+"F0.imprint","IMPRINT",FACE,{"disambiguationData":[TD([[makeQuery(id+"F0.imprint","IMPRINT",EDGE,{"derivedFrom":sQuery(id+"F0.wireOp",EDGE,"E11.10.12.0")}),1.0]])]});
            var Q220;
            Q220=makeQuery(id+"F0.imprint","IMPRINT",FACE,{"disambiguationData":[TD([[makeQuery(id+"F0.imprint","IMPRINT",EDGE,{"derivedFrom":sQuery(id+"F0.wireOp",EDGE,"E11.11.12.0")}),1.0]])]});
            var Q221;
            Q221=makeQuery(id+"F0.imprint","IMPRINT",FACE,{"disambiguationData":[TD([[makeQuery(id+"F0.imprint","IMPRINT",EDGE,{"derivedFrom":sQuery(id+"F0.wireOp",EDGE,"E11.12.12.0")}),1.0]])]});
            var Q222;
            Q222=makeQuery(id+"F0.imprint","IMPRINT",FACE,{"disambiguationData":[TD([[makeQuery(id+"F0.imprint","IMPRINT",EDGE,{"derivedFrom":sQuery(id+"F0.wireOp",EDGE,"E11.12.13.0")}),1.0]])]});
            var Q223;
            Q223=makeQuery(id+"F0.imprint","IMPRINT",FACE,{"disambiguationData":[TD([[makeQuery(id+"F0.imprint","IMPRINT",EDGE,{"derivedFrom":sQuery(id+"F0.wireOp",EDGE,"E11.11.13.0")}),1.0]])]});
            var Q224;
            Q224=makeQuery(id+"F0.imprint","IMPRINT",FACE,{"disambiguationData":[TD([[makeQuery(id+"F0.imprint","IMPRINT",EDGE,{"derivedFrom":sQuery(id+"F0.wireOp",EDGE,"E11.10.13.0")}),1.0]])]});
            var Q225;
            Q225=makeQuery(id+"F0.imprint","IMPRINT",FACE,{"disambiguationData":[TD([[makeQuery(id+"F0.imprint","IMPRINT",EDGE,{"derivedFrom":sQuery(id+"F0.wireOp",EDGE,"E11.10.14.0")}),1.0]])]});
            var Q226;
            Q226=makeQuery(id+"F0.imprint","IMPRINT",FACE,{"disambiguationData":[TD([[makeQuery(id+"F0.imprint","IMPRINT",EDGE,{"derivedFrom":sQuery(id+"F0.wireOp",EDGE,"E11.11.14.0")}),1.0]])]});
            var Q227;
            Q227=makeQuery(id+"F0.imprint","IMPRINT",FACE,{"disambiguationData":[TD([[makeQuery(id+"F0.imprint","IMPRINT",EDGE,{"derivedFrom":sQuery(id+"F0.wireOp",EDGE,"E11.12.14.0")}),1.0]])]});
            var Q228;
            Q228=makeQuery(id+"F0.imprint","IMPRINT",FACE,{"disambiguationData":[TD([[makeQuery(id+"F0.imprint","IMPRINT",EDGE,{"derivedFrom":sQuery(id+"F0.wireOp",EDGE,"E11.6.15.0")}),1.0]])]});
            var Q229;
            Q229=makeQuery(id+"F0.imprint","IMPRINT",FACE,{"disambiguationData":[TD([[makeQuery(id+"F0.imprint","IMPRINT",EDGE,{"derivedFrom":sQuery(id+"F0.wireOp",EDGE,"E11.7.15.0")}),1.0]])]});
            var Q230;
            Q230=makeQuery(id+"F0.imprint","IMPRINT",FACE,{"disambiguationData":[TD([[makeQuery(id+"F0.imprint","IMPRINT",EDGE,{"derivedFrom":sQuery(id+"F0.wireOp",EDGE,"E11.8.15.0")}),1.0]])]});
            var Q231;
            Q231=makeQuery(id+"F0.imprint","IMPRINT",FACE,{"disambiguationData":[TD([[makeQuery(id+"F0.imprint","IMPRINT",EDGE,{"derivedFrom":sQuery(id+"F0.wireOp",EDGE,"E11.9.15.0")}),1.0]])]});
            var Q232;
            Q232=makeQuery(id+"F0.imprint","IMPRINT",FACE,{"disambiguationData":[TD([[makeQuery(id+"F0.imprint","IMPRINT",EDGE,{"derivedFrom":sQuery(id+"F0.wireOp",EDGE,"E11.10.15.0")}),1.0]])]});
            var Q233;
            Q233=makeQuery(id+"F0.imprint","IMPRINT",FACE,{"disambiguationData":[TD([[makeQuery(id+"F0.imprint","IMPRINT",EDGE,{"derivedFrom":sQuery(id+"F0.wireOp",EDGE,"E11.11.15.0")}),1.0]])]});
            var Q234;
            Q234=makeQuery(id+"F0.imprint","IMPRINT",FACE,{"disambiguationData":[TD([[makeQuery(id+"F0.imprint","IMPRINT",EDGE,{"derivedFrom":sQuery(id+"F0.wireOp",EDGE,"E11.12.15.0")}),1.0]])]});
            var Q235;
            Q235=makeQuery(id+"F0.imprint","IMPRINT",FACE,{"disambiguationData":[TD([[makeQuery(id+"F0.imprint","IMPRINT",EDGE,{"derivedFrom":sQuery(id+"F0.wireOp",EDGE,"E11.13.9.0")}),1.0]])]});
            var Q236;
            Q236=makeQuery(id+"F0.imprint","IMPRINT",FACE,{"disambiguationData":[TD([[makeQuery(id+"F0.imprint","IMPRINT",EDGE,{"derivedFrom":sQuery(id+"F0.wireOp",EDGE,"E11.13.10.0")}),1.0]])]});
            var Q237;
            Q237=makeQuery(id+"F0.imprint","IMPRINT",FACE,{"disambiguationData":[TD([[makeQuery(id+"F0.imprint","IMPRINT",EDGE,{"derivedFrom":sQuery(id+"F0.wireOp",EDGE,"E11.14.9.0")}),1.0]])]});
            var Q238;
            Q238=makeQuery(id+"F0.imprint","IMPRINT",FACE,{"disambiguationData":[TD([[makeQuery(id+"F0.imprint","IMPRINT",EDGE,{"derivedFrom":sQuery(id+"F0.wireOp",EDGE,"E11.15.9.0")}),1.0]])]});
            var Q239;
            Q239=makeQuery(id+"F0.imprint","IMPRINT",FACE,{"disambiguationData":[TD([[makeQuery(id+"F0.imprint","IMPRINT",EDGE,{"derivedFrom":sQuery(id+"F0.wireOp",EDGE,"E11.15.10.0")}),1.0]])]});
            var Q240;
            Q240=makeQuery(id+"F0.imprint","IMPRINT",FACE,{"disambiguationData":[TD([[makeQuery(id+"F0.imprint","IMPRINT",EDGE,{"derivedFrom":sQuery(id+"F0.wireOp",EDGE,"E11.14.10.0")}),1.0]])]});
            var Q241;
            Q241=makeQuery(id+"F0.imprint","IMPRINT",FACE,{"disambiguationData":[TD([[makeQuery(id+"F0.imprint","IMPRINT",EDGE,{"derivedFrom":sQuery(id+"F0.wireOp",EDGE,"E11.14.11.0")}),1.0]])]});
            var Q242;
            Q242=makeQuery(id+"F0.imprint","IMPRINT",FACE,{"disambiguationData":[TD([[makeQuery(id+"F0.imprint","IMPRINT",EDGE,{"derivedFrom":sQuery(id+"F0.wireOp",EDGE,"E11.15.11.0")}),1.0]])]});
            var Q243;
            Q243=makeQuery(id+"F0.imprint","IMPRINT",FACE,{"disambiguationData":[TD([[makeQuery(id+"F0.imprint","IMPRINT",EDGE,{"derivedFrom":sQuery(id+"F0.wireOp",EDGE,"E11.13.11.0")}),1.0]])]});
            var Q244;
            Q244=makeQuery(id+"F0.imprint","IMPRINT",FACE,{"disambiguationData":[TD([[makeQuery(id+"F0.imprint","IMPRINT",EDGE,{"derivedFrom":sQuery(id+"F0.wireOp",EDGE,"E11.13.12.0")}),1.0]])]});
            var Q245;
            Q245=makeQuery(id+"F0.imprint","IMPRINT",FACE,{"disambiguationData":[TD([[makeQuery(id+"F0.imprint","IMPRINT",EDGE,{"derivedFrom":sQuery(id+"F0.wireOp",EDGE,"E11.14.12.0")}),1.0]])]});
            var Q246;
            Q246=makeQuery(id+"F0.imprint","IMPRINT",FACE,{"disambiguationData":[TD([[makeQuery(id+"F0.imprint","IMPRINT",EDGE,{"derivedFrom":sQuery(id+"F0.wireOp",EDGE,"E11.15.12.0")}),1.0]])]});
            var Q247;
            Q247=makeQuery(id+"F0.imprint","IMPRINT",FACE,{"disambiguationData":[TD([[makeQuery(id+"F0.imprint","IMPRINT",EDGE,{"derivedFrom":sQuery(id+"F0.wireOp",EDGE,"E11.15.13.0")}),1.0]])]});
            var Q248;
            Q248=makeQuery(id+"F0.imprint","IMPRINT",FACE,{"disambiguationData":[TD([[makeQuery(id+"F0.imprint","IMPRINT",EDGE,{"derivedFrom":sQuery(id+"F0.wireOp",EDGE,"E11.14.13.0")}),1.0]])]});
            var Q249;
            Q249=makeQuery(id+"F0.imprint","IMPRINT",FACE,{"disambiguationData":[TD([[makeQuery(id+"F0.imprint","IMPRINT",EDGE,{"derivedFrom":sQuery(id+"F0.wireOp",EDGE,"E11.13.13.0")}),1.0]])]});
            var Q250;
            Q250=makeQuery(id+"F0.imprint","IMPRINT",FACE,{"disambiguationData":[TD([[makeQuery(id+"F0.imprint","IMPRINT",EDGE,{"derivedFrom":sQuery(id+"F0.wireOp",EDGE,"E11.13.14.0")}),1.0]])]});
            var Q251;
            Q251=makeQuery(id+"F0.imprint","IMPRINT",FACE,{"disambiguationData":[TD([[makeQuery(id+"F0.imprint","IMPRINT",EDGE,{"derivedFrom":sQuery(id+"F0.wireOp",EDGE,"E11.14.14.0")}),1.0]])]});
            var Q252;
            Q252=makeQuery(id+"F0.imprint","IMPRINT",FACE,{"disambiguationData":[TD([[makeQuery(id+"F0.imprint","IMPRINT",EDGE,{"derivedFrom":sQuery(id+"F0.wireOp",EDGE,"E11.15.14.0")}),1.0]])]});
            var Q253;
            Q253=makeQuery(id+"F0.imprint","IMPRINT",FACE,{"disambiguationData":[TD([[makeQuery(id+"F0.imprint","IMPRINT",EDGE,{"derivedFrom":sQuery(id+"F0.wireOp",EDGE,"E11.13.15.0")}),1.0]])]});
            var Q254;
            Q254=makeQuery(id+"F0.imprint","IMPRINT",FACE,{"disambiguationData":[TD([[makeQuery(id+"F0.imprint","IMPRINT",EDGE,{"derivedFrom":sQuery(id+"F0.wireOp",EDGE,"E11.14.15.0")}),1.0]])]});
            var Q255;
            Q255=makeQuery(id+"F0.imprint","IMPRINT",FACE,{"disambiguationData":[TD([[makeQuery(id+"F0.imprint","IMPRINT",EDGE,{"derivedFrom":sQuery(id+"F0.wireOp",EDGE,"E11.15.15.0")}),1.0]])]});
            extrude(context, id + "F4", {"entities" : qUnion([Q0, Q1, Q2, Q3, Q4, Q5, Q6, Q7, Q8, Q9, Q10, Q11, Q12, Q13, Q14, Q15, Q16, Q17, Q18, Q19, Q20, Q21, Q22, Q23, Q24, Q25, Q26, Q27, Q28, Q29, Q30, Q31, Q32, Q33, Q34, Q35, Q36, Q37, Q38, Q39, Q40, Q41, Q42, Q43, Q44, Q45, Q46, Q47, Q48, Q49, Q50, Q51, Q52, Q53, Q54, Q55, Q56, Q57, Q58, Q59, Q60, Q61, Q62, Q63, Q64, Q65, Q66, Q67, Q68, Q69, Q70, Q71, Q72, Q73, Q74, Q75, Q76, Q77, Q78, Q79, Q80, Q81, Q82, Q83, Q84, Q85, Q86, Q87, Q88, Q89, Q90, Q91, Q92, Q93, Q94, Q95, Q96, Q97, Q98, Q99, Q100, Q101, Q102, Q103, Q104, Q105, Q106, Q107, Q108, Q109, Q110, Q111, Q112, Q113, Q114, Q115, Q116, Q117, Q118, Q119, Q120, Q121, Q122, Q123, Q124, Q125, Q126, Q127, Q128, Q129, Q130, Q131, Q132, Q133, Q134, Q135, Q136, Q137, Q138, Q139, Q140, Q141, Q142, Q143, Q144, Q145, Q146, Q147, Q148, Q149, Q150, Q151, Q152, Q153, Q154, Q155, Q156, Q157, Q158, Q159, Q160, Q161, Q162, Q163, Q164, Q165, Q166, Q167, Q168, Q169, Q170, Q171, Q172, Q173, Q174, Q175, Q176, Q177, Q178, Q179, Q180, Q181, Q182, Q183, Q184, Q185, Q186, Q187, Q188, Q189, Q190, Q191, Q192, Q193, Q194, Q195, Q196, Q197, Q198, Q199, Q200, Q201, Q202, Q203, Q204, Q205, Q206, Q207, Q208, Q209, Q210, Q211, Q212, Q213, Q214, Q215, Q216, Q217, Q218, Q219, Q220, Q221, Q222, Q223, Q224, Q225, Q226, Q227, Q228, Q229, Q230, Q231, Q232, Q233, Q234, Q235, Q236, Q237, Q238, Q239, Q240, Q241, Q242, Q243, Q244, Q245, Q246, Q247, Q248, Q249, Q250, Q251, Q252, Q253, Q254, Q255]), "operationType" : NewBodyOperationType.ADD, "depth" : .6 * mm});
        }
        {
            var Q0;
            Q0=makeQuery(id+"F0.imprint","IMPRINT",FACE,{"disambiguationData":[TD([[makeQuery(id+"F0.imprint","IMPRINT",EDGE,{"derivedFrom":sQuery(id+"F0.wireOp",EDGE,"E16.3.0.0")}),1.0]])]});
            var Q1;
            Q1=makeQuery(id+"F0.imprint","IMPRINT",FACE,{"disambiguationData":[TD([[makeQuery(id+"F0.imprint","IMPRINT",EDGE,{"derivedFrom":sQuery(id+"F0.wireOp",EDGE,"E16.2.0.0")}),1.0]])]});
            var Q2;
            Q2=makeQuery(id+"F0.imprint","IMPRINT",FACE,{"disambiguationData":[TD([[makeQuery(id+"F0.imprint","IMPRINT",EDGE,{"derivedFrom":sQuery(id+"F0.wireOp",EDGE,"E16.1.0.0")}),1.0]])]});
            var Q3;
            Q3=makeQuery(id+"F0.imprint","IMPRINT",FACE,{"disambiguationData":[TD([[makeQuery(id+"F0.imprint","IMPRINT",EDGE,{"derivedFrom":sQuery(id+"F0.wireOp",EDGE,"E15")}),1.0]])]});
            var Q4;
            Q4=makeQuery(id+"F0.imprint","IMPRINT",FACE,{"disambiguationData":[TD([[makeQuery(id+"F0.imprint","IMPRINT",EDGE,{"derivedFrom":sQuery(id+"F0.wireOp",EDGE,"E21.0.2.0")}),-1.0]])]});
            var Q5;
            Q5=makeQuery(id+"F0.imprint","IMPRINT",FACE,{"disambiguationData":[TD([[makeQuery(id+"F0.imprint","IMPRINT",EDGE,{"derivedFrom":sQuery(id+"F0.wireOp",EDGE,"E21.0.1.0")}),-1.0]])]});
            var Q6;
            Q6=makeQuery(id+"F0.imprint","IMPRINT",FACE,{"disambiguationData":[TD([[makeQuery(id+"F0.imprint","IMPRINT",EDGE,{"derivedFrom":sQuery(id+"F0.wireOp",EDGE,"E20.MirrorC")}),-1.0]])]});
            var Q7;
            Q7=makeQuery(id+"F0.imprint","IMPRINT",FACE,{"disambiguationData":[TD([[makeQuery(id+"F0.imprint","IMPRINT",EDGE,{"derivedFrom":sQuery(id+"F0.wireOp",EDGE,"E18.MirrorC")}),-1.0]])]});
            var Q8;
            Q8=makeQuery(id+"F0.imprint","IMPRINT",FACE,{"disambiguationData":[TD([[makeQuery(id+"F0.imprint","IMPRINT",EDGE,{"derivedFrom":sQuery(id+"F0.wireOp",EDGE,"E17.MirrorC")}),-1.0]])]});
            var Q9;
            Q9=makeQuery(id+"F0.imprint","IMPRINT",FACE,{"disambiguationData":[TD([[makeQuery(id+"F0.imprint","IMPRINT",EDGE,{"derivedFrom":sQuery(id+"F0.wireOp",EDGE,"E19.MirrorC")}),-1.0]])]});
            var Q10;
            Q10=makeQuery(id+"F0.imprint","IMPRINT",FACE,{"disambiguationData":[TD([[makeQuery(id+"F0.imprint","IMPRINT",EDGE,{"derivedFrom":sQuery(id+"F0.wireOp",EDGE,"E23.MirrorC")}),1.0]])]});
            var Q11;
            Q11=makeQuery(id+"F0.imprint","IMPRINT",FACE,{"disambiguationData":[TD([[makeQuery(id+"F0.imprint","IMPRINT",EDGE,{"derivedFrom":sQuery(id+"F0.wireOp",EDGE,"E22.MirrorC")}),1.0]])]});
            extrude(context, id + "F5", {"entities" : qUnion([Q0, Q1, Q2, Q3, Q4, Q5, Q6, Q7, Q8, Q9, Q10, Q11]), "operationType" : NewBodyOperationType.REMOVE, "depth" : 6 * mm});
        }
        {
            var Q0;
            {var subQ0=sQuery(id+"F3.wireOp",EDGE,"E27.3.left");var subQ1=sQuery(id+"F3.wireOp",EDGE,"E27.0.left");var subQ2=makeQuery(id+"F3.imprint","INTERSECT",VERTEX,{"derivedFrom":[subQ1,subQ0]});Q0=makeQuery(id+"F3.imprint","IMPRINT",FACE,{"disambiguationData":[TD([[makeQuery(id+"F3.imprint","IMPRINT",EDGE,{"disambiguationData":[TD([[subQ2,-1.0]])],"derivedFrom":subQ1}),-1.0]])]});}
            var Q1;
            {var subQ0=sQuery(id+"F3.wireOp",EDGE,"E27.0.endCap");Q1=makeQuery(id+"F3.imprint","IMPRINT",FACE,{"disambiguationData":[TD([[makeQuery(id+"F3.imprint","IMPRINT",EDGE,{"derivedFrom":subQ0}),-1.0]])]});}
            var Q2;
            {var subQ5=sQuery(id+"F3.wireOp",EDGE,"E27.2.startCap");Q2=makeQuery(id+"F3.imprint","IMPRINT",FACE,{"disambiguationData":[TD([[makeQuery(id+"F3.imprint","IMPRINT",EDGE,{"derivedFrom":subQ5}),-1.0]])]});}
            var Q3;
            {var subQ0=sQuery(id+"F3.wireOp",EDGE,"E27.2.right");var subQ1=sQuery(id+"F3.wireOp",EDGE,"E27.0.left");var subQ2=makeQuery(id+"F3.imprint","INTERSECT",VERTEX,{"derivedFrom":[subQ1,subQ0]});Q3=makeQuery(id+"F3.imprint","IMPRINT",FACE,{"disambiguationData":[TD([[makeQuery(id+"F3.imprint","IMPRINT",EDGE,{"disambiguationData":[TD([[subQ2,-1.0]])],"derivedFrom":subQ1}),-1.0]])]});}
            var Q4;
            {var subQ0=sQuery(id+"F3.wireOp",EDGE,"E27.2.left");var subQ1=sQuery(id+"F3.wireOp",EDGE,"E27.0.right");var subQ2=makeQuery(id+"F3.imprint","INTERSECT",VERTEX,{"derivedFrom":[subQ1,subQ0]});Q4=makeQuery(id+"F3.imprint","IMPRINT",FACE,{"disambiguationData":[TD([[makeQuery(id+"F3.imprint","IMPRINT",EDGE,{"disambiguationData":[TD([[subQ2,1.0]])],"derivedFrom":subQ1}),-1.0]])]});}
            var Q5;
            {var subQ0=sQuery(id+"F3.wireOp",EDGE,"E27.3.left");var subQ1=sQuery(id+"F3.wireOp",EDGE,"E27.1.left");var subQ2=makeQuery(id+"F3.imprint","INTERSECT",VERTEX,{"derivedFrom":[subQ1,subQ0]});Q5=makeQuery(id+"F3.imprint","IMPRINT",FACE,{"disambiguationData":[TD([[makeQuery(id+"F3.imprint","IMPRINT",EDGE,{"disambiguationData":[TD([[subQ2,-1.0]])],"derivedFrom":subQ1}),-1.0]])]});}
            var Q6;
            {var subQ0=sQuery(id+"F3.wireOp",EDGE,"E27.2.left");var subQ1=sQuery(id+"F3.wireOp",EDGE,"E27.1.left");var subQ2=makeQuery(id+"F3.imprint","INTERSECT",VERTEX,{"derivedFrom":[subQ1,subQ0]});Q6=makeQuery(id+"F3.imprint","IMPRINT",FACE,{"disambiguationData":[TD([[makeQuery(id+"F3.imprint","IMPRINT",EDGE,{"disambiguationData":[TD([[subQ2,1.0]])],"derivedFrom":subQ1}),-1.0]])]});}
            var Q7;
            {var subQ0=sQuery(id+"F3.wireOp",EDGE,"E27.1.endCap");Q7=makeQuery(id+"F3.imprint","IMPRINT",FACE,{"disambiguationData":[TD([[makeQuery(id+"F3.imprint","IMPRINT",EDGE,{"derivedFrom":subQ0}),-1.0]])]});}
            var Q8;
            {var subQ5=sQuery(id+"F3.wireOp",EDGE,"E27.2.endCap");Q8=makeQuery(id+"F3.imprint","IMPRINT",FACE,{"disambiguationData":[TD([[makeQuery(id+"F3.imprint","IMPRINT",EDGE,{"derivedFrom":subQ5}),-1.0]])]});}
            var Q9;
            {var subQ0=sQuery(id+"F3.wireOp",EDGE,"E27.1.startCap");Q9=makeQuery(id+"F3.imprint","IMPRINT",FACE,{"disambiguationData":[TD([[makeQuery(id+"F3.imprint","IMPRINT",EDGE,{"derivedFrom":subQ0}),-1.0]])]});}
            var Q10;
            {var subQ0=sQuery(id+"F3.wireOp",EDGE,"E27.3.right");var subQ1=sQuery(id+"F3.wireOp",EDGE,"E27.1.left");var subQ2=makeQuery(id+"F3.imprint","INTERSECT",VERTEX,{"derivedFrom":[subQ1,subQ0]});Q10=makeQuery(id+"F3.imprint","IMPRINT",FACE,{"disambiguationData":[TD([[makeQuery(id+"F3.imprint","IMPRINT",EDGE,{"disambiguationData":[TD([[subQ2,-1.0]])],"derivedFrom":subQ1}),-1.0]])]});}
            var Q11;
            {var subQ5=sQuery(id+"F3.wireOp",EDGE,"E27.3.endCap");Q11=makeQuery(id+"F3.imprint","IMPRINT",FACE,{"disambiguationData":[TD([[makeQuery(id+"F3.imprint","IMPRINT",EDGE,{"derivedFrom":subQ5}),-1.0]])]});}
            var Q12;
            {var subQ0=sQuery(id+"F3.wireOp",EDGE,"E27.3.right");var subQ1=sQuery(id+"F3.wireOp",EDGE,"E27.0.right");var subQ2=makeQuery(id+"F3.imprint","INTERSECT",VERTEX,{"derivedFrom":[subQ1,subQ0]});Q12=makeQuery(id+"F3.imprint","IMPRINT",FACE,{"disambiguationData":[TD([[makeQuery(id+"F3.imprint","IMPRINT",EDGE,{"disambiguationData":[TD([[subQ2,-1.0]])],"derivedFrom":subQ1}),-1.0]])]});}
            var Q13;
            {var subQ5=sQuery(id+"F3.wireOp",EDGE,"E27.3.startCap");Q13=makeQuery(id+"F3.imprint","IMPRINT",FACE,{"disambiguationData":[TD([[makeQuery(id+"F3.imprint","IMPRINT",EDGE,{"derivedFrom":subQ5}),-1.0]])]});}
            var Q14;
            {var subQ0=sQuery(id+"F3.wireOp",EDGE,"E27.3.right");var subQ1=sQuery(id+"F3.wireOp",EDGE,"E27.0.left");var subQ2=makeQuery(id+"F3.imprint","INTERSECT",VERTEX,{"derivedFrom":[subQ1,subQ0]});Q14=makeQuery(id+"F3.imprint","IMPRINT",FACE,{"disambiguationData":[TD([[makeQuery(id+"F3.imprint","IMPRINT",EDGE,{"disambiguationData":[TD([[subQ2,-1.0]])],"derivedFrom":subQ1}),-1.0]])]});}
            var Q15;
            {var subQ0=sQuery(id+"F3.wireOp",EDGE,"E27.0.startCap");Q15=makeQuery(id+"F3.imprint","IMPRINT",FACE,{"disambiguationData":[TD([[makeQuery(id+"F3.imprint","IMPRINT",EDGE,{"derivedFrom":subQ0}),-1.0]])]});}
            extrude(context, id + "F6", {"entities" : qUnion([Q0, Q1, Q2, Q3, Q4, Q5, Q6, Q7, Q8, Q9, Q10, Q11, Q12, Q13, Q14, Q15]), "operationType" : NewBodyOperationType.REMOVE, "depth" : 25 * mm});
        }
    });
